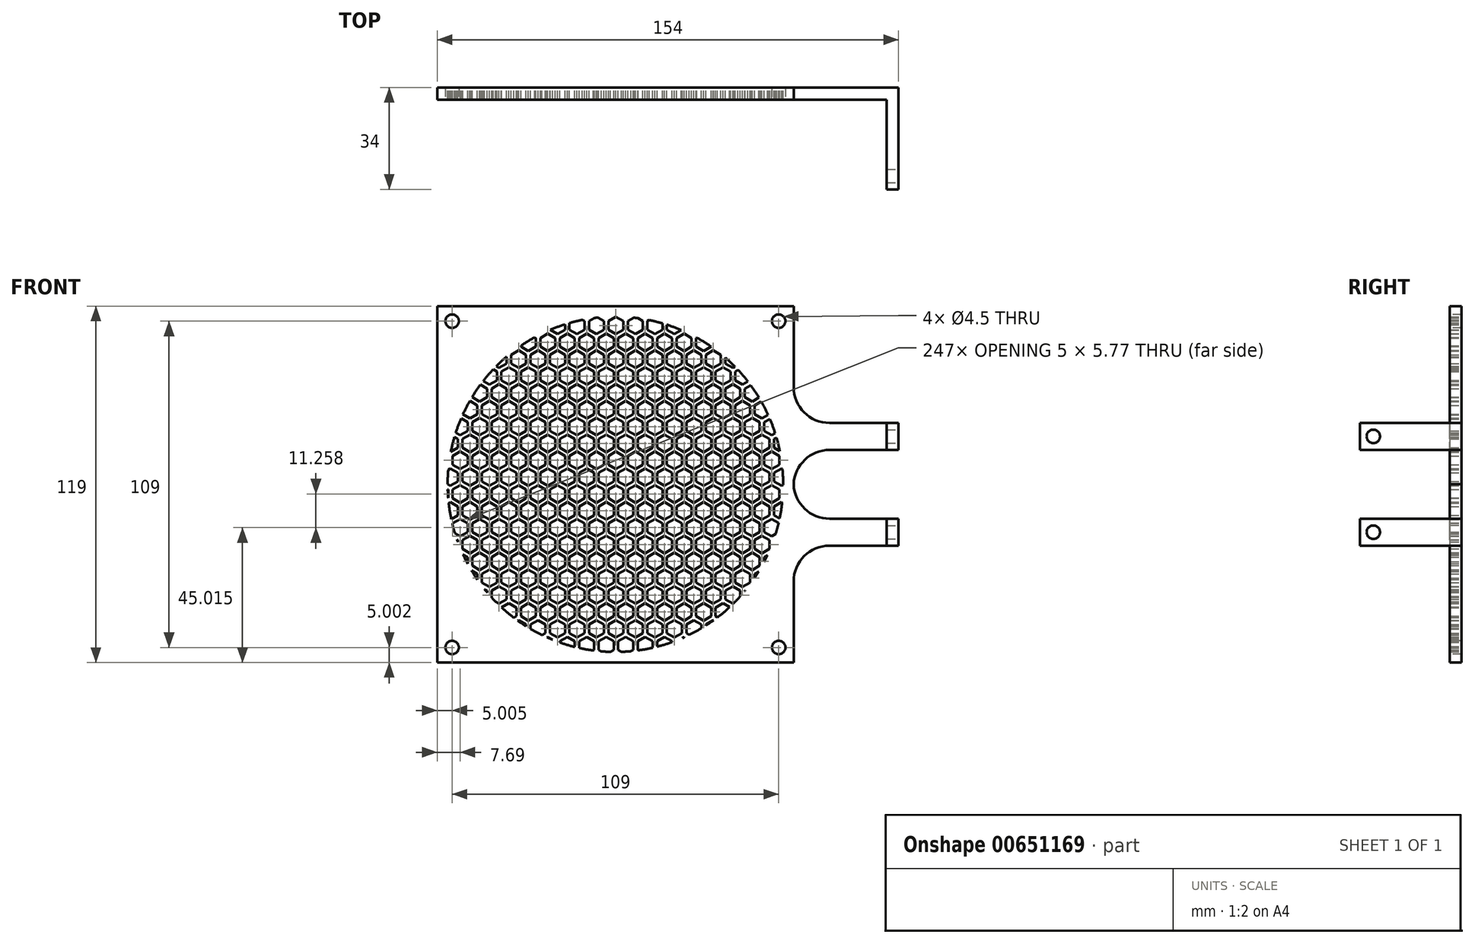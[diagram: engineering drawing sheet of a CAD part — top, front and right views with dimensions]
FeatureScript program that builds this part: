
annotation { "Feature Type Name" : "Feature", "Feature Type Description" : "" }
export const myFeature = defineFeature(function(context is Context, id is Id, definition is map)
    precondition{}
    {
        {
            var Q0;
            Q0=qCreatedBy(makeId("Front.planeOp"),FACE);
            var sketch = newSketch(context, id + "F0", { "sketchPlane" : qUnion([Q0])});
            skCircle(sketch, "E0.cCircle", {"center": v(0, 0) * mm, "radius": 2.5 * mm, "construction": true});
            skLineSegment(sketch, "E0.0", {"start": v(0, 2.89) * mm, "end": v(2.5, 1.44) * mm});
            skLineSegment(sketch, "E0.1", {"start": v(2.5, 1.44) * mm, "end": v(2.5, -1.44) * mm});
            skLineSegment(sketch, "E0.2", {"start": v(2.5, -1.44) * mm, "end": v(0, -2.89) * mm});
            skLineSegment(sketch, "E0.3", {"start": v(0, -2.89) * mm, "end": v(-2.5, -1.44) * mm});
            skLineSegment(sketch, "E0.4", {"start": v(-2.5, -1.44) * mm, "end": v(-2.5, 1.44) * mm});
            skLineSegment(sketch, "E0.5", {"start": v(-2.5, 1.44) * mm, "end": v(0, 2.89) * mm});
            skPoint(sketch, "E0.0.midPoint", {"position": v(1.25, 2.17) * mm});
            skLineSegment(sketch, "E1", {"start": v(0, 0) * mm, "end": v(18.77, -32.51) * mm, "construction": true});
            skCircle(sketch, "E2.cCircle", {"center": v(3.25, -5.63) * mm, "radius": 2.5 * mm, "construction": true});
            skLineSegment(sketch, "E2.0", {"start": v(3.25, -2.74) * mm, "end": v(5.75, -4.19) * mm});
            skLineSegment(sketch, "E2.1", {"start": v(5.75, -4.19) * mm, "end": v(5.75, -7.07) * mm});
            skLineSegment(sketch, "E2.2", {"start": v(5.75, -7.07) * mm, "end": v(3.25, -8.52) * mm});
            skLineSegment(sketch, "E2.3", {"start": v(3.25, -8.52) * mm, "end": v(0.75, -7.07) * mm});
            skLineSegment(sketch, "E2.4", {"start": v(0.75, -7.07) * mm, "end": v(0.75, -4.19) * mm});
            skLineSegment(sketch, "E2.5", {"start": v(0.75, -4.19) * mm, "end": v(3.25, -2.74) * mm});
            skPoint(sketch, "E2.0.midPoint", {"position": v(4.5, -3.46) * mm});
            skCircle(sketch, "E3.0.1.0", {"center": v(3.25, 5.63) * mm, "radius": 2.5 * mm, "construction": true});
            skCircle(sketch, "E3.0.1.1", {"center": v(0, 11.26) * mm, "radius": 2.5 * mm, "construction": true});
            skPoint(sketch, "E3.0.1.2", {"position": v(1.25, 13.42) * mm});
            skPoint(sketch, "E3.0.1.3", {"position": v(4.5, 7.8) * mm});
            skLineSegment(sketch, "E3.0.1.4", {"start": v(3.25, 2.74) * mm, "end": v(0.75, 4.19) * mm});
            skLineSegment(sketch, "E3.0.1.5", {"start": v(5.75, 4.19) * mm, "end": v(3.25, 2.74) * mm});
            skLineSegment(sketch, "E3.0.1.6", {"start": v(5.75, 7.07) * mm, "end": v(5.75, 4.19) * mm});
            skLineSegment(sketch, "E3.0.1.7", {"start": v(3.25, 8.52) * mm, "end": v(5.75, 7.07) * mm});
            skLineSegment(sketch, "E3.0.1.8", {"start": v(-2.5, 12.7) * mm, "end": v(0, 14.15) * mm});
            skLineSegment(sketch, "E3.0.1.9", {"start": v(-2.5, 9.81) * mm, "end": v(-2.5, 12.7) * mm});
            skLineSegment(sketch, "E3.0.1.10", {"start": v(0, 8.37) * mm, "end": v(-2.5, 9.81) * mm});
            skLineSegment(sketch, "E3.0.1.11", {"start": v(2.5, 9.81) * mm, "end": v(0, 8.37) * mm});
            skLineSegment(sketch, "E3.0.1.12", {"start": v(2.5, 12.7) * mm, "end": v(2.5, 9.81) * mm});
            skLineSegment(sketch, "E3.0.1.13", {"start": v(0, 14.15) * mm, "end": v(2.5, 12.7) * mm});
            skLineSegment(sketch, "E3.0.1.14", {"start": v(0.75, 7.07) * mm, "end": v(3.25, 8.52) * mm});
            skLineSegment(sketch, "E3.0.1.15", {"start": v(0.75, 4.19) * mm, "end": v(0.75, 7.07) * mm});
            skCircle(sketch, "E3.0.2.0", {"center": v(3.25, 16.89) * mm, "radius": 2.5 * mm, "construction": true});
            skCircle(sketch, "E3.0.2.1", {"center": v(0, 22.52) * mm, "radius": 2.5 * mm, "construction": true});
            skPoint(sketch, "E3.0.2.2", {"position": v(1.25, 24.68) * mm});
            skPoint(sketch, "E3.0.2.3", {"position": v(4.5, 19.05) * mm});
            skLineSegment(sketch, "E3.0.2.4", {"start": v(3.25, 14) * mm, "end": v(0.75, 15.44) * mm});
            skLineSegment(sketch, "E3.0.2.5", {"start": v(5.75, 15.44) * mm, "end": v(3.25, 14) * mm});
            skLineSegment(sketch, "E3.0.2.6", {"start": v(5.75, 18.33) * mm, "end": v(5.75, 15.44) * mm});
            skLineSegment(sketch, "E3.0.2.7", {"start": v(3.25, 19.77) * mm, "end": v(5.75, 18.33) * mm});
            skLineSegment(sketch, "E3.0.2.8", {"start": v(-2.5, 23.96) * mm, "end": v(0, 25.4) * mm});
            skLineSegment(sketch, "E3.0.2.9", {"start": v(-2.5, 21.07) * mm, "end": v(-2.5, 23.96) * mm});
            skLineSegment(sketch, "E3.0.2.10", {"start": v(0, 19.63) * mm, "end": v(-2.5, 21.07) * mm});
            skLineSegment(sketch, "E3.0.2.11", {"start": v(2.5, 21.07) * mm, "end": v(0, 19.63) * mm});
            skLineSegment(sketch, "E3.0.2.12", {"start": v(2.5, 23.96) * mm, "end": v(2.5, 21.07) * mm});
            skLineSegment(sketch, "E3.0.2.13", {"start": v(0, 25.4) * mm, "end": v(2.5, 23.96) * mm});
            skLineSegment(sketch, "E3.0.2.14", {"start": v(0.75, 18.33) * mm, "end": v(3.25, 19.77) * mm});
            skLineSegment(sketch, "E3.0.2.15", {"start": v(0.75, 15.44) * mm, "end": v(0.75, 18.33) * mm});
            skCircle(sketch, "E3.0.3.0", {"center": v(3.25, 28.15) * mm, "radius": 2.5 * mm, "construction": true});
            skCircle(sketch, "E3.0.3.1", {"center": v(0, 33.77) * mm, "radius": 2.5 * mm, "construction": true});
            skPoint(sketch, "E3.0.3.2", {"position": v(1.25, 35.94) * mm});
            skPoint(sketch, "E3.0.3.3", {"position": v(4.5, 30.31) * mm});
            skLineSegment(sketch, "E3.0.3.4", {"start": v(3.25, 25.26) * mm, "end": v(0.75, 26.7) * mm});
            skLineSegment(sketch, "E3.0.3.5", {"start": v(5.75, 26.7) * mm, "end": v(3.25, 25.26) * mm});
            skLineSegment(sketch, "E3.0.3.6", {"start": v(5.75, 29.59) * mm, "end": v(5.75, 26.7) * mm});
            skLineSegment(sketch, "E3.0.3.7", {"start": v(3.25, 31.03) * mm, "end": v(5.75, 29.59) * mm});
            skLineSegment(sketch, "E3.0.3.8", {"start": v(-2.5, 35.22) * mm, "end": v(0, 36.66) * mm});
            skLineSegment(sketch, "E3.0.3.9", {"start": v(-2.5, 32.33) * mm, "end": v(-2.5, 35.22) * mm});
            skLineSegment(sketch, "E3.0.3.10", {"start": v(0, 30.89) * mm, "end": v(-2.5, 32.33) * mm});
            skLineSegment(sketch, "E3.0.3.11", {"start": v(2.5, 32.33) * mm, "end": v(0, 30.89) * mm});
            skLineSegment(sketch, "E3.0.3.12", {"start": v(2.5, 35.22) * mm, "end": v(2.5, 32.33) * mm});
            skLineSegment(sketch, "E3.0.3.13", {"start": v(0, 36.66) * mm, "end": v(2.5, 35.22) * mm});
            skLineSegment(sketch, "E3.0.3.14", {"start": v(0.75, 29.59) * mm, "end": v(3.25, 31.03) * mm});
            skLineSegment(sketch, "E3.0.3.15", {"start": v(0.75, 26.7) * mm, "end": v(0.75, 29.59) * mm});
            skCircle(sketch, "E3.0.4.0", {"center": v(3.25, 39.4) * mm, "radius": 2.5 * mm, "construction": true});
            skCircle(sketch, "E3.0.4.1", {"center": v(0, 45.03) * mm, "radius": 2.5 * mm, "construction": true});
            skPoint(sketch, "E3.0.4.2", {"position": v(1.25, 47.2) * mm});
            skPoint(sketch, "E3.0.4.3", {"position": v(4.5, 41.57) * mm});
            skLineSegment(sketch, "E3.0.4.4", {"start": v(3.25, 36.52) * mm, "end": v(0.75, 37.96) * mm});
            skLineSegment(sketch, "E3.0.4.5", {"start": v(5.75, 37.96) * mm, "end": v(3.25, 36.52) * mm});
            skLineSegment(sketch, "E3.0.4.6", {"start": v(5.75, 40.85) * mm, "end": v(5.75, 37.96) * mm});
            skLineSegment(sketch, "E3.0.4.7", {"start": v(3.25, 42.3) * mm, "end": v(5.75, 40.85) * mm});
            skLineSegment(sketch, "E3.0.4.8", {"start": v(-2.5, 46.48) * mm, "end": v(0, 47.92) * mm});
            skLineSegment(sketch, "E3.0.4.9", {"start": v(-2.5, 43.59) * mm, "end": v(-2.5, 46.48) * mm});
            skLineSegment(sketch, "E3.0.4.10", {"start": v(0, 42.15) * mm, "end": v(-2.5, 43.59) * mm});
            skLineSegment(sketch, "E3.0.4.11", {"start": v(2.5, 43.59) * mm, "end": v(0, 42.15) * mm});
            skLineSegment(sketch, "E3.0.4.12", {"start": v(2.5, 46.48) * mm, "end": v(2.5, 43.59) * mm});
            skLineSegment(sketch, "E3.0.4.13", {"start": v(0, 47.92) * mm, "end": v(2.5, 46.48) * mm});
            skLineSegment(sketch, "E3.0.4.14", {"start": v(0.75, 40.85) * mm, "end": v(3.25, 42.3) * mm});
            skLineSegment(sketch, "E3.0.4.15", {"start": v(0.75, 37.96) * mm, "end": v(0.75, 40.85) * mm});
            skCircle(sketch, "E3.0.5.0", {"center": v(3.25, 50.66) * mm, "radius": 2.5 * mm, "construction": true});
            skCircle(sketch, "E3.0.5.1", {"center": v(0, 56.3) * mm, "radius": 2.5 * mm, "construction": true});
            skPoint(sketch, "E3.0.5.2", {"position": v(1.25, 58.46) * mm});
            skPoint(sketch, "E3.0.5.3", {"position": v(4.5, 52.83) * mm});
            skLineSegment(sketch, "E3.0.5.4", {"start": v(3.25, 47.78) * mm, "end": v(0.75, 49.22) * mm});
            skLineSegment(sketch, "E3.0.5.5", {"start": v(5.75, 49.22) * mm, "end": v(3.25, 47.78) * mm});
            skLineSegment(sketch, "E3.0.5.6", {"start": v(5.75, 52.1) * mm, "end": v(5.75, 49.22) * mm});
            skLineSegment(sketch, "E3.0.5.7", {"start": v(3.25, 53.55) * mm, "end": v(5.75, 52.1) * mm});
            skLineSegment(sketch, "E3.0.5.8", {"start": v(-2.5, 57.74) * mm, "end": v(0, 59.18) * mm});
            skLineSegment(sketch, "E3.0.5.9", {"start": v(-2.5, 54.85) * mm, "end": v(-2.5, 57.74) * mm});
            skLineSegment(sketch, "E3.0.5.10", {"start": v(0, 53.4) * mm, "end": v(-2.5, 54.85) * mm});
            skLineSegment(sketch, "E3.0.5.11", {"start": v(2.5, 54.85) * mm, "end": v(0, 53.4) * mm});
            skLineSegment(sketch, "E3.0.5.12", {"start": v(2.5, 57.74) * mm, "end": v(2.5, 54.85) * mm});
            skLineSegment(sketch, "E3.0.5.13", {"start": v(0, 59.18) * mm, "end": v(2.5, 57.74) * mm});
            skLineSegment(sketch, "E3.0.5.14", {"start": v(0.75, 52.1) * mm, "end": v(3.25, 53.55) * mm});
            skLineSegment(sketch, "E3.0.5.15", {"start": v(0.75, 49.22) * mm, "end": v(0.75, 52.1) * mm});
            skCircle(sketch, "E3.0.6.0", {"center": v(3.25, 61.92) * mm, "radius": 2.5 * mm, "construction": true});
            skCircle(sketch, "E3.0.6.1", {"center": v(0, 67.55) * mm, "radius": 2.5 * mm, "construction": true});
            skPoint(sketch, "E3.0.6.2", {"position": v(1.25, 69.72) * mm});
            skPoint(sketch, "E3.0.6.3", {"position": v(4.5, 64.09) * mm});
            skLineSegment(sketch, "E3.0.6.4", {"start": v(3.25, 59.03) * mm, "end": v(0.75, 60.48) * mm});
            skLineSegment(sketch, "E3.0.6.5", {"start": v(5.75, 60.48) * mm, "end": v(3.25, 59.03) * mm});
            skLineSegment(sketch, "E3.0.6.6", {"start": v(5.75, 63.36) * mm, "end": v(5.75, 60.48) * mm});
            skLineSegment(sketch, "E3.0.6.7", {"start": v(3.25, 64.8) * mm, "end": v(5.75, 63.36) * mm});
            skLineSegment(sketch, "E3.0.6.8", {"start": v(-2.5, 69) * mm, "end": v(0, 70.44) * mm});
            skLineSegment(sketch, "E3.0.6.9", {"start": v(-2.5, 66.1) * mm, "end": v(-2.5, 69) * mm});
            skLineSegment(sketch, "E3.0.6.10", {"start": v(0, 64.66) * mm, "end": v(-2.5, 66.1) * mm});
            skLineSegment(sketch, "E3.0.6.11", {"start": v(2.5, 66.1) * mm, "end": v(0, 64.66) * mm});
            skLineSegment(sketch, "E3.0.6.12", {"start": v(2.5, 69) * mm, "end": v(2.5, 66.1) * mm});
            skLineSegment(sketch, "E3.0.6.13", {"start": v(0, 70.44) * mm, "end": v(2.5, 69) * mm});
            skLineSegment(sketch, "E3.0.6.14", {"start": v(0.75, 63.36) * mm, "end": v(3.25, 64.8) * mm});
            skLineSegment(sketch, "E3.0.6.15", {"start": v(0.75, 60.48) * mm, "end": v(0.75, 63.36) * mm});
            skCircle(sketch, "E3.0.7.0", {"center": v(3.25, 73.18) * mm, "radius": 2.5 * mm, "construction": true});
            skCircle(sketch, "E3.0.7.1", {"center": v(0, 78.8) * mm, "radius": 2.5 * mm, "construction": true});
            skPoint(sketch, "E3.0.7.2", {"position": v(1.25, 80.97) * mm});
            skPoint(sketch, "E3.0.7.3", {"position": v(4.5, 75.34) * mm});
            skLineSegment(sketch, "E3.0.7.4", {"start": v(3.25, 70.3) * mm, "end": v(0.75, 71.74) * mm});
            skLineSegment(sketch, "E3.0.7.5", {"start": v(5.75, 71.74) * mm, "end": v(3.25, 70.3) * mm});
            skLineSegment(sketch, "E3.0.7.6", {"start": v(5.75, 74.62) * mm, "end": v(5.75, 71.74) * mm});
            skLineSegment(sketch, "E3.0.7.7", {"start": v(3.25, 76.07) * mm, "end": v(5.75, 74.62) * mm});
            skLineSegment(sketch, "E3.0.7.8", {"start": v(-2.5, 80.25) * mm, "end": v(0, 81.7) * mm});
            skLineSegment(sketch, "E3.0.7.9", {"start": v(-2.5, 77.36) * mm, "end": v(-2.5, 80.25) * mm});
            skLineSegment(sketch, "E3.0.7.10", {"start": v(0, 75.92) * mm, "end": v(-2.5, 77.36) * mm});
            skLineSegment(sketch, "E3.0.7.11", {"start": v(2.5, 77.36) * mm, "end": v(0, 75.92) * mm});
            skLineSegment(sketch, "E3.0.7.12", {"start": v(2.5, 80.25) * mm, "end": v(2.5, 77.36) * mm});
            skLineSegment(sketch, "E3.0.7.13", {"start": v(0, 81.7) * mm, "end": v(2.5, 80.25) * mm});
            skLineSegment(sketch, "E3.0.7.14", {"start": v(0.75, 74.62) * mm, "end": v(3.25, 76.07) * mm});
            skLineSegment(sketch, "E3.0.7.15", {"start": v(0.75, 71.74) * mm, "end": v(0.75, 74.62) * mm});
            skCircle(sketch, "E3.0.8.0", {"center": v(3.25, 84.44) * mm, "radius": 2.5 * mm, "construction": true});
            skCircle(sketch, "E3.0.8.1", {"center": v(0, 90.07) * mm, "radius": 2.5 * mm, "construction": true});
            skPoint(sketch, "E3.0.8.2", {"position": v(1.25, 92.23) * mm});
            skPoint(sketch, "E3.0.8.3", {"position": v(4.5, 86.6) * mm});
            skLineSegment(sketch, "E3.0.8.4", {"start": v(3.25, 81.55) * mm, "end": v(0.75, 83) * mm});
            skLineSegment(sketch, "E3.0.8.5", {"start": v(5.75, 83) * mm, "end": v(3.25, 81.55) * mm});
            skLineSegment(sketch, "E3.0.8.6", {"start": v(5.75, 85.88) * mm, "end": v(5.75, 83) * mm});
            skLineSegment(sketch, "E3.0.8.7", {"start": v(3.25, 87.32) * mm, "end": v(5.75, 85.88) * mm});
            skLineSegment(sketch, "E3.0.8.8", {"start": v(-2.5, 91.51) * mm, "end": v(0, 92.95) * mm});
            skLineSegment(sketch, "E3.0.8.9", {"start": v(-2.5, 88.62) * mm, "end": v(-2.5, 91.51) * mm});
            skLineSegment(sketch, "E3.0.8.10", {"start": v(0, 87.18) * mm, "end": v(-2.5, 88.62) * mm});
            skLineSegment(sketch, "E3.0.8.11", {"start": v(2.5, 88.62) * mm, "end": v(0, 87.18) * mm});
            skLineSegment(sketch, "E3.0.8.12", {"start": v(2.5, 91.51) * mm, "end": v(2.5, 88.62) * mm});
            skLineSegment(sketch, "E3.0.8.13", {"start": v(0, 92.95) * mm, "end": v(2.5, 91.51) * mm});
            skLineSegment(sketch, "E3.0.8.14", {"start": v(0.75, 85.88) * mm, "end": v(3.25, 87.32) * mm});
            skLineSegment(sketch, "E3.0.8.15", {"start": v(0.75, 83) * mm, "end": v(0.75, 85.88) * mm});
            skCircle(sketch, "E3.0.9.0", {"center": v(3.25, 95.7) * mm, "radius": 2.5 * mm, "construction": true});
            skCircle(sketch, "E3.0.9.1", {"center": v(0, 101.32) * mm, "radius": 2.5 * mm, "construction": true});
            skPoint(sketch, "E3.0.9.2", {"position": v(1.25, 103.5) * mm});
            skPoint(sketch, "E3.0.9.3", {"position": v(4.5, 97.86) * mm});
            skLineSegment(sketch, "E3.0.9.4", {"start": v(3.25, 92.8) * mm, "end": v(0.75, 94.25) * mm});
            skLineSegment(sketch, "E3.0.9.5", {"start": v(5.75, 94.25) * mm, "end": v(3.25, 92.8) * mm});
            skLineSegment(sketch, "E3.0.9.6", {"start": v(5.75, 97.14) * mm, "end": v(5.75, 94.25) * mm});
            skLineSegment(sketch, "E3.0.9.7", {"start": v(3.25, 98.58) * mm, "end": v(5.75, 97.14) * mm});
            skLineSegment(sketch, "E3.0.9.8", {"start": v(-2.5, 102.77) * mm, "end": v(0, 104.21) * mm});
            skLineSegment(sketch, "E3.0.9.9", {"start": v(-2.5, 99.88) * mm, "end": v(-2.5, 102.77) * mm});
            skLineSegment(sketch, "E3.0.9.10", {"start": v(0, 98.44) * mm, "end": v(-2.5, 99.88) * mm});
            skLineSegment(sketch, "E3.0.9.11", {"start": v(2.5, 99.88) * mm, "end": v(0, 98.44) * mm});
            skLineSegment(sketch, "E3.0.9.12", {"start": v(2.5, 102.77) * mm, "end": v(2.5, 99.88) * mm});
            skLineSegment(sketch, "E3.0.9.13", {"start": v(0, 104.21) * mm, "end": v(2.5, 102.77) * mm});
            skLineSegment(sketch, "E3.0.9.14", {"start": v(0.75, 97.14) * mm, "end": v(3.25, 98.58) * mm});
            skLineSegment(sketch, "E3.0.9.15", {"start": v(0.75, 94.25) * mm, "end": v(0.75, 97.14) * mm});
            skCircle(sketch, "E3.1.0.0", {"center": v(9.75, -5.63) * mm, "radius": 2.5 * mm, "construction": true});
            skCircle(sketch, "E3.1.0.1", {"center": v(6.5, 0) * mm, "radius": 2.5 * mm, "construction": true});
            skPoint(sketch, "E3.1.0.2", {"position": v(7.75, 2.17) * mm});
            skPoint(sketch, "E3.1.0.3", {"position": v(11, -3.46) * mm});
            skLineSegment(sketch, "E3.1.0.4", {"start": v(9.75, -8.52) * mm, "end": v(7.25, -7.07) * mm});
            skLineSegment(sketch, "E3.1.0.5", {"start": v(12.25, -7.07) * mm, "end": v(9.75, -8.52) * mm});
            skLineSegment(sketch, "E3.1.0.6", {"start": v(12.25, -4.19) * mm, "end": v(12.25, -7.07) * mm});
            skLineSegment(sketch, "E3.1.0.7", {"start": v(9.75, -2.74) * mm, "end": v(12.25, -4.19) * mm});
            skLineSegment(sketch, "E3.1.0.8", {"start": v(4, 1.44) * mm, "end": v(6.5, 2.89) * mm});
            skLineSegment(sketch, "E3.1.0.9", {"start": v(4, -1.44) * mm, "end": v(4, 1.44) * mm});
            skLineSegment(sketch, "E3.1.0.10", {"start": v(6.5, -2.89) * mm, "end": v(4, -1.44) * mm});
            skLineSegment(sketch, "E3.1.0.11", {"start": v(9, -1.44) * mm, "end": v(6.5, -2.89) * mm});
            skLineSegment(sketch, "E3.1.0.12", {"start": v(9, 1.44) * mm, "end": v(9, -1.44) * mm});
            skLineSegment(sketch, "E3.1.0.13", {"start": v(6.5, 2.89) * mm, "end": v(9, 1.44) * mm});
            skLineSegment(sketch, "E3.1.0.14", {"start": v(7.25, -4.19) * mm, "end": v(9.75, -2.74) * mm});
            skLineSegment(sketch, "E3.1.0.15", {"start": v(7.25, -7.07) * mm, "end": v(7.25, -4.19) * mm});
            skCircle(sketch, "E3.1.1.0", {"center": v(9.75, 5.63) * mm, "radius": 2.5 * mm, "construction": true});
            skCircle(sketch, "E3.1.1.1", {"center": v(6.5, 11.26) * mm, "radius": 2.5 * mm, "construction": true});
            skPoint(sketch, "E3.1.1.2", {"position": v(7.75, 13.42) * mm});
            skPoint(sketch, "E3.1.1.3", {"position": v(11, 7.8) * mm});
            skLineSegment(sketch, "E3.1.1.4", {"start": v(9.75, 2.74) * mm, "end": v(7.25, 4.19) * mm});
            skLineSegment(sketch, "E3.1.1.5", {"start": v(12.25, 4.19) * mm, "end": v(9.75, 2.74) * mm});
            skLineSegment(sketch, "E3.1.1.6", {"start": v(12.25, 7.07) * mm, "end": v(12.25, 4.19) * mm});
            skLineSegment(sketch, "E3.1.1.7", {"start": v(9.75, 8.52) * mm, "end": v(12.25, 7.07) * mm});
            skLineSegment(sketch, "E3.1.1.8", {"start": v(4, 12.7) * mm, "end": v(6.5, 14.15) * mm});
            skLineSegment(sketch, "E3.1.1.9", {"start": v(4, 9.81) * mm, "end": v(4, 12.7) * mm});
            skLineSegment(sketch, "E3.1.1.10", {"start": v(6.5, 8.37) * mm, "end": v(4, 9.81) * mm});
            skLineSegment(sketch, "E3.1.1.11", {"start": v(9, 9.81) * mm, "end": v(6.5, 8.37) * mm});
            skLineSegment(sketch, "E3.1.1.12", {"start": v(9, 12.7) * mm, "end": v(9, 9.81) * mm});
            skLineSegment(sketch, "E3.1.1.13", {"start": v(6.5, 14.15) * mm, "end": v(9, 12.7) * mm});
            skLineSegment(sketch, "E3.1.1.14", {"start": v(7.25, 7.07) * mm, "end": v(9.75, 8.52) * mm});
            skLineSegment(sketch, "E3.1.1.15", {"start": v(7.25, 4.19) * mm, "end": v(7.25, 7.07) * mm});
            skCircle(sketch, "E3.1.2.0", {"center": v(9.75, 16.89) * mm, "radius": 2.5 * mm, "construction": true});
            skCircle(sketch, "E3.1.2.1", {"center": v(6.5, 22.52) * mm, "radius": 2.5 * mm, "construction": true});
            skPoint(sketch, "E3.1.2.2", {"position": v(7.75, 24.68) * mm});
            skPoint(sketch, "E3.1.2.3", {"position": v(11, 19.05) * mm});
            skLineSegment(sketch, "E3.1.2.4", {"start": v(9.75, 14) * mm, "end": v(7.25, 15.44) * mm});
            skLineSegment(sketch, "E3.1.2.5", {"start": v(12.25, 15.44) * mm, "end": v(9.75, 14) * mm});
            skLineSegment(sketch, "E3.1.2.6", {"start": v(12.25, 18.33) * mm, "end": v(12.25, 15.44) * mm});
            skLineSegment(sketch, "E3.1.2.7", {"start": v(9.75, 19.77) * mm, "end": v(12.25, 18.33) * mm});
            skLineSegment(sketch, "E3.1.2.8", {"start": v(4, 23.96) * mm, "end": v(6.5, 25.4) * mm});
            skLineSegment(sketch, "E3.1.2.9", {"start": v(4, 21.07) * mm, "end": v(4, 23.96) * mm});
            skLineSegment(sketch, "E3.1.2.10", {"start": v(6.5, 19.63) * mm, "end": v(4, 21.07) * mm});
            skLineSegment(sketch, "E3.1.2.11", {"start": v(9, 21.07) * mm, "end": v(6.5, 19.63) * mm});
            skLineSegment(sketch, "E3.1.2.12", {"start": v(9, 23.96) * mm, "end": v(9, 21.07) * mm});
            skLineSegment(sketch, "E3.1.2.13", {"start": v(6.5, 25.4) * mm, "end": v(9, 23.96) * mm});
            skLineSegment(sketch, "E3.1.2.14", {"start": v(7.25, 18.33) * mm, "end": v(9.75, 19.77) * mm});
            skLineSegment(sketch, "E3.1.2.15", {"start": v(7.25, 15.44) * mm, "end": v(7.25, 18.33) * mm});
            skCircle(sketch, "E3.1.3.0", {"center": v(9.75, 28.15) * mm, "radius": 2.5 * mm, "construction": true});
            skCircle(sketch, "E3.1.3.1", {"center": v(6.5, 33.77) * mm, "radius": 2.5 * mm, "construction": true});
            skPoint(sketch, "E3.1.3.2", {"position": v(7.75, 35.94) * mm});
            skPoint(sketch, "E3.1.3.3", {"position": v(11, 30.31) * mm});
            skLineSegment(sketch, "E3.1.3.4", {"start": v(9.75, 25.26) * mm, "end": v(7.25, 26.7) * mm});
            skLineSegment(sketch, "E3.1.3.5", {"start": v(12.25, 26.7) * mm, "end": v(9.75, 25.26) * mm});
            skLineSegment(sketch, "E3.1.3.6", {"start": v(12.25, 29.59) * mm, "end": v(12.25, 26.7) * mm});
            skLineSegment(sketch, "E3.1.3.7", {"start": v(9.75, 31.03) * mm, "end": v(12.25, 29.59) * mm});
            skLineSegment(sketch, "E3.1.3.8", {"start": v(4, 35.22) * mm, "end": v(6.5, 36.66) * mm});
            skLineSegment(sketch, "E3.1.3.9", {"start": v(4, 32.33) * mm, "end": v(4, 35.22) * mm});
            skLineSegment(sketch, "E3.1.3.10", {"start": v(6.5, 30.89) * mm, "end": v(4, 32.33) * mm});
            skLineSegment(sketch, "E3.1.3.11", {"start": v(9, 32.33) * mm, "end": v(6.5, 30.89) * mm});
            skLineSegment(sketch, "E3.1.3.12", {"start": v(9, 35.22) * mm, "end": v(9, 32.33) * mm});
            skLineSegment(sketch, "E3.1.3.13", {"start": v(6.5, 36.66) * mm, "end": v(9, 35.22) * mm});
            skLineSegment(sketch, "E3.1.3.14", {"start": v(7.25, 29.59) * mm, "end": v(9.75, 31.03) * mm});
            skLineSegment(sketch, "E3.1.3.15", {"start": v(7.25, 26.7) * mm, "end": v(7.25, 29.59) * mm});
            skCircle(sketch, "E3.1.4.0", {"center": v(9.75, 39.4) * mm, "radius": 2.5 * mm, "construction": true});
            skCircle(sketch, "E3.1.4.1", {"center": v(6.5, 45.03) * mm, "radius": 2.5 * mm, "construction": true});
            skPoint(sketch, "E3.1.4.2", {"position": v(7.75, 47.2) * mm});
            skPoint(sketch, "E3.1.4.3", {"position": v(11, 41.57) * mm});
            skLineSegment(sketch, "E3.1.4.4", {"start": v(9.75, 36.52) * mm, "end": v(7.25, 37.96) * mm});
            skLineSegment(sketch, "E3.1.4.5", {"start": v(12.25, 37.96) * mm, "end": v(9.75, 36.52) * mm});
            skLineSegment(sketch, "E3.1.4.6", {"start": v(12.25, 40.85) * mm, "end": v(12.25, 37.96) * mm});
            skLineSegment(sketch, "E3.1.4.7", {"start": v(9.75, 42.3) * mm, "end": v(12.25, 40.85) * mm});
            skLineSegment(sketch, "E3.1.4.8", {"start": v(4, 46.48) * mm, "end": v(6.5, 47.92) * mm});
            skLineSegment(sketch, "E3.1.4.9", {"start": v(4, 43.59) * mm, "end": v(4, 46.48) * mm});
            skLineSegment(sketch, "E3.1.4.10", {"start": v(6.5, 42.15) * mm, "end": v(4, 43.59) * mm});
            skLineSegment(sketch, "E3.1.4.11", {"start": v(9, 43.59) * mm, "end": v(6.5, 42.15) * mm});
            skLineSegment(sketch, "E3.1.4.12", {"start": v(9, 46.48) * mm, "end": v(9, 43.59) * mm});
            skLineSegment(sketch, "E3.1.4.13", {"start": v(6.5, 47.92) * mm, "end": v(9, 46.48) * mm});
            skLineSegment(sketch, "E3.1.4.14", {"start": v(7.25, 40.85) * mm, "end": v(9.75, 42.3) * mm});
            skLineSegment(sketch, "E3.1.4.15", {"start": v(7.25, 37.96) * mm, "end": v(7.25, 40.85) * mm});
            skCircle(sketch, "E3.1.5.0", {"center": v(9.75, 50.66) * mm, "radius": 2.5 * mm, "construction": true});
            skCircle(sketch, "E3.1.5.1", {"center": v(6.5, 56.3) * mm, "radius": 2.5 * mm, "construction": true});
            skPoint(sketch, "E3.1.5.2", {"position": v(7.75, 58.46) * mm});
            skPoint(sketch, "E3.1.5.3", {"position": v(11, 52.83) * mm});
            skLineSegment(sketch, "E3.1.5.4", {"start": v(9.75, 47.78) * mm, "end": v(7.25, 49.22) * mm});
            skLineSegment(sketch, "E3.1.5.5", {"start": v(12.25, 49.22) * mm, "end": v(9.75, 47.78) * mm});
            skLineSegment(sketch, "E3.1.5.6", {"start": v(12.25, 52.1) * mm, "end": v(12.25, 49.22) * mm});
            skLineSegment(sketch, "E3.1.5.7", {"start": v(9.75, 53.55) * mm, "end": v(12.25, 52.1) * mm});
            skLineSegment(sketch, "E3.1.5.8", {"start": v(4, 57.74) * mm, "end": v(6.5, 59.18) * mm});
            skLineSegment(sketch, "E3.1.5.9", {"start": v(4, 54.85) * mm, "end": v(4, 57.74) * mm});
            skLineSegment(sketch, "E3.1.5.10", {"start": v(6.5, 53.4) * mm, "end": v(4, 54.85) * mm});
            skLineSegment(sketch, "E3.1.5.11", {"start": v(9, 54.85) * mm, "end": v(6.5, 53.4) * mm});
            skLineSegment(sketch, "E3.1.5.12", {"start": v(9, 57.74) * mm, "end": v(9, 54.85) * mm});
            skLineSegment(sketch, "E3.1.5.13", {"start": v(6.5, 59.18) * mm, "end": v(9, 57.74) * mm});
            skLineSegment(sketch, "E3.1.5.14", {"start": v(7.25, 52.1) * mm, "end": v(9.75, 53.55) * mm});
            skLineSegment(sketch, "E3.1.5.15", {"start": v(7.25, 49.22) * mm, "end": v(7.25, 52.1) * mm});
            skCircle(sketch, "E3.1.6.0", {"center": v(9.75, 61.92) * mm, "radius": 2.5 * mm, "construction": true});
            skCircle(sketch, "E3.1.6.1", {"center": v(6.5, 67.55) * mm, "radius": 2.5 * mm, "construction": true});
            skPoint(sketch, "E3.1.6.2", {"position": v(7.75, 69.72) * mm});
            skPoint(sketch, "E3.1.6.3", {"position": v(11, 64.09) * mm});
            skLineSegment(sketch, "E3.1.6.4", {"start": v(9.75, 59.03) * mm, "end": v(7.25, 60.48) * mm});
            skLineSegment(sketch, "E3.1.6.5", {"start": v(12.25, 60.48) * mm, "end": v(9.75, 59.03) * mm});
            skLineSegment(sketch, "E3.1.6.6", {"start": v(12.25, 63.36) * mm, "end": v(12.25, 60.48) * mm});
            skLineSegment(sketch, "E3.1.6.7", {"start": v(9.75, 64.8) * mm, "end": v(12.25, 63.36) * mm});
            skLineSegment(sketch, "E3.1.6.8", {"start": v(4, 69) * mm, "end": v(6.5, 70.44) * mm});
            skLineSegment(sketch, "E3.1.6.9", {"start": v(4, 66.1) * mm, "end": v(4, 69) * mm});
            skLineSegment(sketch, "E3.1.6.10", {"start": v(6.5, 64.66) * mm, "end": v(4, 66.1) * mm});
            skLineSegment(sketch, "E3.1.6.11", {"start": v(9, 66.1) * mm, "end": v(6.5, 64.66) * mm});
            skLineSegment(sketch, "E3.1.6.12", {"start": v(9, 69) * mm, "end": v(9, 66.1) * mm});
            skLineSegment(sketch, "E3.1.6.13", {"start": v(6.5, 70.44) * mm, "end": v(9, 69) * mm});
            skLineSegment(sketch, "E3.1.6.14", {"start": v(7.25, 63.36) * mm, "end": v(9.75, 64.8) * mm});
            skLineSegment(sketch, "E3.1.6.15", {"start": v(7.25, 60.48) * mm, "end": v(7.25, 63.36) * mm});
            skCircle(sketch, "E3.1.7.0", {"center": v(9.75, 73.18) * mm, "radius": 2.5 * mm, "construction": true});
            skCircle(sketch, "E3.1.7.1", {"center": v(6.5, 78.8) * mm, "radius": 2.5 * mm, "construction": true});
            skPoint(sketch, "E3.1.7.2", {"position": v(7.75, 80.97) * mm});
            skPoint(sketch, "E3.1.7.3", {"position": v(11, 75.34) * mm});
            skLineSegment(sketch, "E3.1.7.4", {"start": v(9.75, 70.3) * mm, "end": v(7.25, 71.74) * mm});
            skLineSegment(sketch, "E3.1.7.5", {"start": v(12.25, 71.74) * mm, "end": v(9.75, 70.3) * mm});
            skLineSegment(sketch, "E3.1.7.6", {"start": v(12.25, 74.62) * mm, "end": v(12.25, 71.74) * mm});
            skLineSegment(sketch, "E3.1.7.7", {"start": v(9.75, 76.07) * mm, "end": v(12.25, 74.62) * mm});
            skLineSegment(sketch, "E3.1.7.8", {"start": v(4, 80.25) * mm, "end": v(6.5, 81.7) * mm});
            skLineSegment(sketch, "E3.1.7.9", {"start": v(4, 77.36) * mm, "end": v(4, 80.25) * mm});
            skLineSegment(sketch, "E3.1.7.10", {"start": v(6.5, 75.92) * mm, "end": v(4, 77.36) * mm});
            skLineSegment(sketch, "E3.1.7.11", {"start": v(9, 77.36) * mm, "end": v(6.5, 75.92) * mm});
            skLineSegment(sketch, "E3.1.7.12", {"start": v(9, 80.25) * mm, "end": v(9, 77.36) * mm});
            skLineSegment(sketch, "E3.1.7.13", {"start": v(6.5, 81.7) * mm, "end": v(9, 80.25) * mm});
            skLineSegment(sketch, "E3.1.7.14", {"start": v(7.25, 74.62) * mm, "end": v(9.75, 76.07) * mm});
            skLineSegment(sketch, "E3.1.7.15", {"start": v(7.25, 71.74) * mm, "end": v(7.25, 74.62) * mm});
            skCircle(sketch, "E3.1.8.0", {"center": v(9.75, 84.44) * mm, "radius": 2.5 * mm, "construction": true});
            skCircle(sketch, "E3.1.8.1", {"center": v(6.5, 90.07) * mm, "radius": 2.5 * mm, "construction": true});
            skPoint(sketch, "E3.1.8.2", {"position": v(7.75, 92.23) * mm});
            skPoint(sketch, "E3.1.8.3", {"position": v(11, 86.6) * mm});
            skLineSegment(sketch, "E3.1.8.4", {"start": v(9.75, 81.55) * mm, "end": v(7.25, 83) * mm});
            skLineSegment(sketch, "E3.1.8.5", {"start": v(12.25, 83) * mm, "end": v(9.75, 81.55) * mm});
            skLineSegment(sketch, "E3.1.8.6", {"start": v(12.25, 85.88) * mm, "end": v(12.25, 83) * mm});
            skLineSegment(sketch, "E3.1.8.7", {"start": v(9.75, 87.32) * mm, "end": v(12.25, 85.88) * mm});
            skLineSegment(sketch, "E3.1.8.8", {"start": v(4, 91.51) * mm, "end": v(6.5, 92.95) * mm});
            skLineSegment(sketch, "E3.1.8.9", {"start": v(4, 88.62) * mm, "end": v(4, 91.51) * mm});
            skLineSegment(sketch, "E3.1.8.10", {"start": v(6.5, 87.18) * mm, "end": v(4, 88.62) * mm});
            skLineSegment(sketch, "E3.1.8.11", {"start": v(9, 88.62) * mm, "end": v(6.5, 87.18) * mm});
            skLineSegment(sketch, "E3.1.8.12", {"start": v(9, 91.51) * mm, "end": v(9, 88.62) * mm});
            skLineSegment(sketch, "E3.1.8.13", {"start": v(6.5, 92.95) * mm, "end": v(9, 91.51) * mm});
            skLineSegment(sketch, "E3.1.8.14", {"start": v(7.25, 85.88) * mm, "end": v(9.75, 87.32) * mm});
            skLineSegment(sketch, "E3.1.8.15", {"start": v(7.25, 83) * mm, "end": v(7.25, 85.88) * mm});
            skCircle(sketch, "E3.1.9.0", {"center": v(9.75, 95.7) * mm, "radius": 2.5 * mm, "construction": true});
            skCircle(sketch, "E3.1.9.1", {"center": v(6.5, 101.32) * mm, "radius": 2.5 * mm, "construction": true});
            skPoint(sketch, "E3.1.9.2", {"position": v(7.75, 103.5) * mm});
            skPoint(sketch, "E3.1.9.3", {"position": v(11, 97.86) * mm});
            skLineSegment(sketch, "E3.1.9.4", {"start": v(9.75, 92.8) * mm, "end": v(7.25, 94.25) * mm});
            skLineSegment(sketch, "E3.1.9.5", {"start": v(12.25, 94.25) * mm, "end": v(9.75, 92.8) * mm});
            skLineSegment(sketch, "E3.1.9.6", {"start": v(12.25, 97.14) * mm, "end": v(12.25, 94.25) * mm});
            skLineSegment(sketch, "E3.1.9.7", {"start": v(9.75, 98.58) * mm, "end": v(12.25, 97.14) * mm});
            skLineSegment(sketch, "E3.1.9.8", {"start": v(4, 102.77) * mm, "end": v(6.5, 104.21) * mm});
            skLineSegment(sketch, "E3.1.9.9", {"start": v(4, 99.88) * mm, "end": v(4, 102.77) * mm});
            skLineSegment(sketch, "E3.1.9.10", {"start": v(6.5, 98.44) * mm, "end": v(4, 99.88) * mm});
            skLineSegment(sketch, "E3.1.9.11", {"start": v(9, 99.88) * mm, "end": v(6.5, 98.44) * mm});
            skLineSegment(sketch, "E3.1.9.12", {"start": v(9, 102.77) * mm, "end": v(9, 99.88) * mm});
            skLineSegment(sketch, "E3.1.9.13", {"start": v(6.5, 104.21) * mm, "end": v(9, 102.77) * mm});
            skLineSegment(sketch, "E3.1.9.14", {"start": v(7.25, 97.14) * mm, "end": v(9.75, 98.58) * mm});
            skLineSegment(sketch, "E3.1.9.15", {"start": v(7.25, 94.25) * mm, "end": v(7.25, 97.14) * mm});
            skCircle(sketch, "E3.2.0.0", {"center": v(16.25, -5.63) * mm, "radius": 2.5 * mm, "construction": true});
            skCircle(sketch, "E3.2.0.1", {"center": v(13, 0) * mm, "radius": 2.5 * mm, "construction": true});
            skPoint(sketch, "E3.2.0.2", {"position": v(14.25, 2.17) * mm});
            skPoint(sketch, "E3.2.0.3", {"position": v(17.5, -3.46) * mm});
            skLineSegment(sketch, "E3.2.0.4", {"start": v(16.25, -8.52) * mm, "end": v(13.75, -7.07) * mm});
            skLineSegment(sketch, "E3.2.0.5", {"start": v(18.75, -7.07) * mm, "end": v(16.25, -8.52) * mm});
            skLineSegment(sketch, "E3.2.0.6", {"start": v(18.75, -4.19) * mm, "end": v(18.75, -7.07) * mm});
            skLineSegment(sketch, "E3.2.0.7", {"start": v(16.25, -2.74) * mm, "end": v(18.75, -4.19) * mm});
            skLineSegment(sketch, "E3.2.0.8", {"start": v(10.5, 1.44) * mm, "end": v(13, 2.89) * mm});
            skLineSegment(sketch, "E3.2.0.9", {"start": v(10.5, -1.44) * mm, "end": v(10.5, 1.44) * mm});
            skLineSegment(sketch, "E3.2.0.10", {"start": v(13, -2.89) * mm, "end": v(10.5, -1.44) * mm});
            skLineSegment(sketch, "E3.2.0.11", {"start": v(15.5, -1.44) * mm, "end": v(13, -2.89) * mm});
            skLineSegment(sketch, "E3.2.0.12", {"start": v(15.5, 1.44) * mm, "end": v(15.5, -1.44) * mm});
            skLineSegment(sketch, "E3.2.0.13", {"start": v(13, 2.89) * mm, "end": v(15.5, 1.44) * mm});
            skLineSegment(sketch, "E3.2.0.14", {"start": v(13.75, -4.19) * mm, "end": v(16.25, -2.74) * mm});
            skLineSegment(sketch, "E3.2.0.15", {"start": v(13.75, -7.07) * mm, "end": v(13.75, -4.19) * mm});
            skCircle(sketch, "E3.2.1.0", {"center": v(16.25, 5.63) * mm, "radius": 2.5 * mm, "construction": true});
            skCircle(sketch, "E3.2.1.1", {"center": v(13, 11.26) * mm, "radius": 2.5 * mm, "construction": true});
            skPoint(sketch, "E3.2.1.2", {"position": v(14.25, 13.42) * mm});
            skPoint(sketch, "E3.2.1.3", {"position": v(17.5, 7.8) * mm});
            skLineSegment(sketch, "E3.2.1.4", {"start": v(16.25, 2.74) * mm, "end": v(13.75, 4.19) * mm});
            skLineSegment(sketch, "E3.2.1.5", {"start": v(18.75, 4.19) * mm, "end": v(16.25, 2.74) * mm});
            skLineSegment(sketch, "E3.2.1.6", {"start": v(18.75, 7.07) * mm, "end": v(18.75, 4.19) * mm});
            skLineSegment(sketch, "E3.2.1.7", {"start": v(16.25, 8.52) * mm, "end": v(18.75, 7.07) * mm});
            skLineSegment(sketch, "E3.2.1.8", {"start": v(10.5, 12.7) * mm, "end": v(13, 14.15) * mm});
            skLineSegment(sketch, "E3.2.1.9", {"start": v(10.5, 9.81) * mm, "end": v(10.5, 12.7) * mm});
            skLineSegment(sketch, "E3.2.1.10", {"start": v(13, 8.37) * mm, "end": v(10.5, 9.81) * mm});
            skLineSegment(sketch, "E3.2.1.11", {"start": v(15.5, 9.81) * mm, "end": v(13, 8.37) * mm});
            skLineSegment(sketch, "E3.2.1.12", {"start": v(15.5, 12.7) * mm, "end": v(15.5, 9.81) * mm});
            skLineSegment(sketch, "E3.2.1.13", {"start": v(13, 14.15) * mm, "end": v(15.5, 12.7) * mm});
            skLineSegment(sketch, "E3.2.1.14", {"start": v(13.75, 7.07) * mm, "end": v(16.25, 8.52) * mm});
            skLineSegment(sketch, "E3.2.1.15", {"start": v(13.75, 4.19) * mm, "end": v(13.75, 7.07) * mm});
            skCircle(sketch, "E3.2.2.0", {"center": v(16.25, 16.89) * mm, "radius": 2.5 * mm, "construction": true});
            skCircle(sketch, "E3.2.2.1", {"center": v(13, 22.52) * mm, "radius": 2.5 * mm, "construction": true});
            skPoint(sketch, "E3.2.2.2", {"position": v(14.25, 24.68) * mm});
            skPoint(sketch, "E3.2.2.3", {"position": v(17.5, 19.05) * mm});
            skLineSegment(sketch, "E3.2.2.4", {"start": v(16.25, 14) * mm, "end": v(13.75, 15.44) * mm});
            skLineSegment(sketch, "E3.2.2.5", {"start": v(18.75, 15.44) * mm, "end": v(16.25, 14) * mm});
            skLineSegment(sketch, "E3.2.2.6", {"start": v(18.75, 18.33) * mm, "end": v(18.75, 15.44) * mm});
            skLineSegment(sketch, "E3.2.2.7", {"start": v(16.25, 19.77) * mm, "end": v(18.75, 18.33) * mm});
            skLineSegment(sketch, "E3.2.2.8", {"start": v(10.5, 23.96) * mm, "end": v(13, 25.4) * mm});
            skLineSegment(sketch, "E3.2.2.9", {"start": v(10.5, 21.07) * mm, "end": v(10.5, 23.96) * mm});
            skLineSegment(sketch, "E3.2.2.10", {"start": v(13, 19.63) * mm, "end": v(10.5, 21.07) * mm});
            skLineSegment(sketch, "E3.2.2.11", {"start": v(15.5, 21.07) * mm, "end": v(13, 19.63) * mm});
            skLineSegment(sketch, "E3.2.2.12", {"start": v(15.5, 23.96) * mm, "end": v(15.5, 21.07) * mm});
            skLineSegment(sketch, "E3.2.2.13", {"start": v(13, 25.4) * mm, "end": v(15.5, 23.96) * mm});
            skLineSegment(sketch, "E3.2.2.14", {"start": v(13.75, 18.33) * mm, "end": v(16.25, 19.77) * mm});
            skLineSegment(sketch, "E3.2.2.15", {"start": v(13.75, 15.44) * mm, "end": v(13.75, 18.33) * mm});
            skCircle(sketch, "E3.2.3.0", {"center": v(16.25, 28.15) * mm, "radius": 2.5 * mm, "construction": true});
            skCircle(sketch, "E3.2.3.1", {"center": v(13, 33.77) * mm, "radius": 2.5 * mm, "construction": true});
            skPoint(sketch, "E3.2.3.2", {"position": v(14.25, 35.94) * mm});
            skPoint(sketch, "E3.2.3.3", {"position": v(17.5, 30.31) * mm});
            skLineSegment(sketch, "E3.2.3.4", {"start": v(16.25, 25.26) * mm, "end": v(13.75, 26.7) * mm});
            skLineSegment(sketch, "E3.2.3.5", {"start": v(18.75, 26.7) * mm, "end": v(16.25, 25.26) * mm});
            skLineSegment(sketch, "E3.2.3.6", {"start": v(18.75, 29.59) * mm, "end": v(18.75, 26.7) * mm});
            skLineSegment(sketch, "E3.2.3.7", {"start": v(16.25, 31.03) * mm, "end": v(18.75, 29.59) * mm});
            skLineSegment(sketch, "E3.2.3.8", {"start": v(10.5, 35.22) * mm, "end": v(13, 36.66) * mm});
            skLineSegment(sketch, "E3.2.3.9", {"start": v(10.5, 32.33) * mm, "end": v(10.5, 35.22) * mm});
            skLineSegment(sketch, "E3.2.3.10", {"start": v(13, 30.89) * mm, "end": v(10.5, 32.33) * mm});
            skLineSegment(sketch, "E3.2.3.11", {"start": v(15.5, 32.33) * mm, "end": v(13, 30.89) * mm});
            skLineSegment(sketch, "E3.2.3.12", {"start": v(15.5, 35.22) * mm, "end": v(15.5, 32.33) * mm});
            skLineSegment(sketch, "E3.2.3.13", {"start": v(13, 36.66) * mm, "end": v(15.5, 35.22) * mm});
            skLineSegment(sketch, "E3.2.3.14", {"start": v(13.75, 29.59) * mm, "end": v(16.25, 31.03) * mm});
            skLineSegment(sketch, "E3.2.3.15", {"start": v(13.75, 26.7) * mm, "end": v(13.75, 29.59) * mm});
            skCircle(sketch, "E3.2.4.0", {"center": v(16.25, 39.4) * mm, "radius": 2.5 * mm, "construction": true});
            skCircle(sketch, "E3.2.4.1", {"center": v(13, 45.03) * mm, "radius": 2.5 * mm, "construction": true});
            skPoint(sketch, "E3.2.4.2", {"position": v(14.25, 47.2) * mm});
            skPoint(sketch, "E3.2.4.3", {"position": v(17.5, 41.57) * mm});
            skLineSegment(sketch, "E3.2.4.4", {"start": v(16.25, 36.52) * mm, "end": v(13.75, 37.96) * mm});
            skLineSegment(sketch, "E3.2.4.5", {"start": v(18.75, 37.96) * mm, "end": v(16.25, 36.52) * mm});
            skLineSegment(sketch, "E3.2.4.6", {"start": v(18.75, 40.85) * mm, "end": v(18.75, 37.96) * mm});
            skLineSegment(sketch, "E3.2.4.7", {"start": v(16.25, 42.3) * mm, "end": v(18.75, 40.85) * mm});
            skLineSegment(sketch, "E3.2.4.8", {"start": v(10.5, 46.48) * mm, "end": v(13, 47.92) * mm});
            skLineSegment(sketch, "E3.2.4.9", {"start": v(10.5, 43.59) * mm, "end": v(10.5, 46.48) * mm});
            skLineSegment(sketch, "E3.2.4.10", {"start": v(13, 42.15) * mm, "end": v(10.5, 43.59) * mm});
            skLineSegment(sketch, "E3.2.4.11", {"start": v(15.5, 43.59) * mm, "end": v(13, 42.15) * mm});
            skLineSegment(sketch, "E3.2.4.12", {"start": v(15.5, 46.48) * mm, "end": v(15.5, 43.59) * mm});
            skLineSegment(sketch, "E3.2.4.13", {"start": v(13, 47.92) * mm, "end": v(15.5, 46.48) * mm});
            skLineSegment(sketch, "E3.2.4.14", {"start": v(13.75, 40.85) * mm, "end": v(16.25, 42.3) * mm});
            skLineSegment(sketch, "E3.2.4.15", {"start": v(13.75, 37.96) * mm, "end": v(13.75, 40.85) * mm});
            skCircle(sketch, "E3.2.5.0", {"center": v(16.25, 50.66) * mm, "radius": 2.5 * mm, "construction": true});
            skCircle(sketch, "E3.2.5.1", {"center": v(13, 56.3) * mm, "radius": 2.5 * mm, "construction": true});
            skPoint(sketch, "E3.2.5.2", {"position": v(14.25, 58.46) * mm});
            skPoint(sketch, "E3.2.5.3", {"position": v(17.5, 52.83) * mm});
            skLineSegment(sketch, "E3.2.5.4", {"start": v(16.25, 47.78) * mm, "end": v(13.75, 49.22) * mm});
            skLineSegment(sketch, "E3.2.5.5", {"start": v(18.75, 49.22) * mm, "end": v(16.25, 47.78) * mm});
            skLineSegment(sketch, "E3.2.5.6", {"start": v(18.75, 52.1) * mm, "end": v(18.75, 49.22) * mm});
            skLineSegment(sketch, "E3.2.5.7", {"start": v(16.25, 53.55) * mm, "end": v(18.75, 52.1) * mm});
            skLineSegment(sketch, "E3.2.5.8", {"start": v(10.5, 57.74) * mm, "end": v(13, 59.18) * mm});
            skLineSegment(sketch, "E3.2.5.9", {"start": v(10.5, 54.85) * mm, "end": v(10.5, 57.74) * mm});
            skLineSegment(sketch, "E3.2.5.10", {"start": v(13, 53.4) * mm, "end": v(10.5, 54.85) * mm});
            skLineSegment(sketch, "E3.2.5.11", {"start": v(15.5, 54.85) * mm, "end": v(13, 53.4) * mm});
            skLineSegment(sketch, "E3.2.5.12", {"start": v(15.5, 57.74) * mm, "end": v(15.5, 54.85) * mm});
            skLineSegment(sketch, "E3.2.5.13", {"start": v(13, 59.18) * mm, "end": v(15.5, 57.74) * mm});
            skLineSegment(sketch, "E3.2.5.14", {"start": v(13.75, 52.1) * mm, "end": v(16.25, 53.55) * mm});
            skLineSegment(sketch, "E3.2.5.15", {"start": v(13.75, 49.22) * mm, "end": v(13.75, 52.1) * mm});
            skCircle(sketch, "E3.2.6.0", {"center": v(16.25, 61.92) * mm, "radius": 2.5 * mm, "construction": true});
            skCircle(sketch, "E3.2.6.1", {"center": v(13, 67.55) * mm, "radius": 2.5 * mm, "construction": true});
            skPoint(sketch, "E3.2.6.2", {"position": v(14.25, 69.72) * mm});
            skPoint(sketch, "E3.2.6.3", {"position": v(17.5, 64.09) * mm});
            skLineSegment(sketch, "E3.2.6.4", {"start": v(16.25, 59.03) * mm, "end": v(13.75, 60.48) * mm});
            skLineSegment(sketch, "E3.2.6.5", {"start": v(18.75, 60.48) * mm, "end": v(16.25, 59.03) * mm});
            skLineSegment(sketch, "E3.2.6.6", {"start": v(18.75, 63.36) * mm, "end": v(18.75, 60.48) * mm});
            skLineSegment(sketch, "E3.2.6.7", {"start": v(16.25, 64.8) * mm, "end": v(18.75, 63.36) * mm});
            skLineSegment(sketch, "E3.2.6.8", {"start": v(10.5, 69) * mm, "end": v(13, 70.44) * mm});
            skLineSegment(sketch, "E3.2.6.9", {"start": v(10.5, 66.1) * mm, "end": v(10.5, 69) * mm});
            skLineSegment(sketch, "E3.2.6.10", {"start": v(13, 64.66) * mm, "end": v(10.5, 66.1) * mm});
            skLineSegment(sketch, "E3.2.6.11", {"start": v(15.5, 66.1) * mm, "end": v(13, 64.66) * mm});
            skLineSegment(sketch, "E3.2.6.12", {"start": v(15.5, 69) * mm, "end": v(15.5, 66.1) * mm});
            skLineSegment(sketch, "E3.2.6.13", {"start": v(13, 70.44) * mm, "end": v(15.5, 69) * mm});
            skLineSegment(sketch, "E3.2.6.14", {"start": v(13.75, 63.36) * mm, "end": v(16.25, 64.8) * mm});
            skLineSegment(sketch, "E3.2.6.15", {"start": v(13.75, 60.48) * mm, "end": v(13.75, 63.36) * mm});
            skCircle(sketch, "E3.2.7.0", {"center": v(16.25, 73.18) * mm, "radius": 2.5 * mm, "construction": true});
            skCircle(sketch, "E3.2.7.1", {"center": v(13, 78.8) * mm, "radius": 2.5 * mm, "construction": true});
            skPoint(sketch, "E3.2.7.2", {"position": v(14.25, 80.97) * mm});
            skPoint(sketch, "E3.2.7.3", {"position": v(17.5, 75.34) * mm});
            skLineSegment(sketch, "E3.2.7.4", {"start": v(16.25, 70.3) * mm, "end": v(13.75, 71.74) * mm});
            skLineSegment(sketch, "E3.2.7.5", {"start": v(18.75, 71.74) * mm, "end": v(16.25, 70.3) * mm});
            skLineSegment(sketch, "E3.2.7.6", {"start": v(18.75, 74.62) * mm, "end": v(18.75, 71.74) * mm});
            skLineSegment(sketch, "E3.2.7.7", {"start": v(16.25, 76.07) * mm, "end": v(18.75, 74.62) * mm});
            skLineSegment(sketch, "E3.2.7.8", {"start": v(10.5, 80.25) * mm, "end": v(13, 81.7) * mm});
            skLineSegment(sketch, "E3.2.7.9", {"start": v(10.5, 77.36) * mm, "end": v(10.5, 80.25) * mm});
            skLineSegment(sketch, "E3.2.7.10", {"start": v(13, 75.92) * mm, "end": v(10.5, 77.36) * mm});
            skLineSegment(sketch, "E3.2.7.11", {"start": v(15.5, 77.36) * mm, "end": v(13, 75.92) * mm});
            skLineSegment(sketch, "E3.2.7.12", {"start": v(15.5, 80.25) * mm, "end": v(15.5, 77.36) * mm});
            skLineSegment(sketch, "E3.2.7.13", {"start": v(13, 81.7) * mm, "end": v(15.5, 80.25) * mm});
            skLineSegment(sketch, "E3.2.7.14", {"start": v(13.75, 74.62) * mm, "end": v(16.25, 76.07) * mm});
            skLineSegment(sketch, "E3.2.7.15", {"start": v(13.75, 71.74) * mm, "end": v(13.75, 74.62) * mm});
            skCircle(sketch, "E3.2.8.0", {"center": v(16.25, 84.44) * mm, "radius": 2.5 * mm, "construction": true});
            skCircle(sketch, "E3.2.8.1", {"center": v(13, 90.07) * mm, "radius": 2.5 * mm, "construction": true});
            skPoint(sketch, "E3.2.8.2", {"position": v(14.25, 92.23) * mm});
            skPoint(sketch, "E3.2.8.3", {"position": v(17.5, 86.6) * mm});
            skLineSegment(sketch, "E3.2.8.4", {"start": v(16.25, 81.55) * mm, "end": v(13.75, 83) * mm});
            skLineSegment(sketch, "E3.2.8.5", {"start": v(18.75, 83) * mm, "end": v(16.25, 81.55) * mm});
            skLineSegment(sketch, "E3.2.8.6", {"start": v(18.75, 85.88) * mm, "end": v(18.75, 83) * mm});
            skLineSegment(sketch, "E3.2.8.7", {"start": v(16.25, 87.32) * mm, "end": v(18.75, 85.88) * mm});
            skLineSegment(sketch, "E3.2.8.8", {"start": v(10.5, 91.51) * mm, "end": v(13, 92.95) * mm});
            skLineSegment(sketch, "E3.2.8.9", {"start": v(10.5, 88.62) * mm, "end": v(10.5, 91.51) * mm});
            skLineSegment(sketch, "E3.2.8.10", {"start": v(13, 87.18) * mm, "end": v(10.5, 88.62) * mm});
            skLineSegment(sketch, "E3.2.8.11", {"start": v(15.5, 88.62) * mm, "end": v(13, 87.18) * mm});
            skLineSegment(sketch, "E3.2.8.12", {"start": v(15.5, 91.51) * mm, "end": v(15.5, 88.62) * mm});
            skLineSegment(sketch, "E3.2.8.13", {"start": v(13, 92.95) * mm, "end": v(15.5, 91.51) * mm});
            skLineSegment(sketch, "E3.2.8.14", {"start": v(13.75, 85.88) * mm, "end": v(16.25, 87.32) * mm});
            skLineSegment(sketch, "E3.2.8.15", {"start": v(13.75, 83) * mm, "end": v(13.75, 85.88) * mm});
            skCircle(sketch, "E3.2.9.0", {"center": v(16.25, 95.7) * mm, "radius": 2.5 * mm, "construction": true});
            skCircle(sketch, "E3.2.9.1", {"center": v(13, 101.32) * mm, "radius": 2.5 * mm, "construction": true});
            skPoint(sketch, "E3.2.9.2", {"position": v(14.25, 103.5) * mm});
            skPoint(sketch, "E3.2.9.3", {"position": v(17.5, 97.86) * mm});
            skLineSegment(sketch, "E3.2.9.4", {"start": v(16.25, 92.8) * mm, "end": v(13.75, 94.25) * mm});
            skLineSegment(sketch, "E3.2.9.5", {"start": v(18.75, 94.25) * mm, "end": v(16.25, 92.8) * mm});
            skLineSegment(sketch, "E3.2.9.6", {"start": v(18.75, 97.14) * mm, "end": v(18.75, 94.25) * mm});
            skLineSegment(sketch, "E3.2.9.7", {"start": v(16.25, 98.58) * mm, "end": v(18.75, 97.14) * mm});
            skLineSegment(sketch, "E3.2.9.8", {"start": v(10.5, 102.77) * mm, "end": v(13, 104.21) * mm});
            skLineSegment(sketch, "E3.2.9.9", {"start": v(10.5, 99.88) * mm, "end": v(10.5, 102.77) * mm});
            skLineSegment(sketch, "E3.2.9.10", {"start": v(13, 98.44) * mm, "end": v(10.5, 99.88) * mm});
            skLineSegment(sketch, "E3.2.9.11", {"start": v(15.5, 99.88) * mm, "end": v(13, 98.44) * mm});
            skLineSegment(sketch, "E3.2.9.12", {"start": v(15.5, 102.77) * mm, "end": v(15.5, 99.88) * mm});
            skLineSegment(sketch, "E3.2.9.13", {"start": v(13, 104.21) * mm, "end": v(15.5, 102.77) * mm});
            skLineSegment(sketch, "E3.2.9.14", {"start": v(13.75, 97.14) * mm, "end": v(16.25, 98.58) * mm});
            skLineSegment(sketch, "E3.2.9.15", {"start": v(13.75, 94.25) * mm, "end": v(13.75, 97.14) * mm});
            skCircle(sketch, "E3.3.0.0", {"center": v(22.75, -5.63) * mm, "radius": 2.5 * mm, "construction": true});
            skCircle(sketch, "E3.3.0.1", {"center": v(19.5, 0) * mm, "radius": 2.5 * mm, "construction": true});
            skPoint(sketch, "E3.3.0.2", {"position": v(20.75, 2.17) * mm});
            skPoint(sketch, "E3.3.0.3", {"position": v(24, -3.46) * mm});
            skLineSegment(sketch, "E3.3.0.4", {"start": v(22.75, -8.52) * mm, "end": v(20.25, -7.07) * mm});
            skLineSegment(sketch, "E3.3.0.5", {"start": v(25.25, -7.07) * mm, "end": v(22.75, -8.52) * mm});
            skLineSegment(sketch, "E3.3.0.6", {"start": v(25.25, -4.19) * mm, "end": v(25.25, -7.07) * mm});
            skLineSegment(sketch, "E3.3.0.7", {"start": v(22.75, -2.74) * mm, "end": v(25.25, -4.19) * mm});
            skLineSegment(sketch, "E3.3.0.8", {"start": v(17, 1.44) * mm, "end": v(19.5, 2.89) * mm});
            skLineSegment(sketch, "E3.3.0.9", {"start": v(17, -1.44) * mm, "end": v(17, 1.44) * mm});
            skLineSegment(sketch, "E3.3.0.10", {"start": v(19.5, -2.89) * mm, "end": v(17, -1.44) * mm});
            skLineSegment(sketch, "E3.3.0.11", {"start": v(22, -1.44) * mm, "end": v(19.5, -2.89) * mm});
            skLineSegment(sketch, "E3.3.0.12", {"start": v(22, 1.44) * mm, "end": v(22, -1.44) * mm});
            skLineSegment(sketch, "E3.3.0.13", {"start": v(19.5, 2.89) * mm, "end": v(22, 1.44) * mm});
            skLineSegment(sketch, "E3.3.0.14", {"start": v(20.25, -4.19) * mm, "end": v(22.75, -2.74) * mm});
            skLineSegment(sketch, "E3.3.0.15", {"start": v(20.25, -7.07) * mm, "end": v(20.25, -4.19) * mm});
            skCircle(sketch, "E3.3.1.0", {"center": v(22.75, 5.63) * mm, "radius": 2.5 * mm, "construction": true});
            skCircle(sketch, "E3.3.1.1", {"center": v(19.5, 11.26) * mm, "radius": 2.5 * mm, "construction": true});
            skPoint(sketch, "E3.3.1.2", {"position": v(20.75, 13.42) * mm});
            skPoint(sketch, "E3.3.1.3", {"position": v(24, 7.8) * mm});
            skLineSegment(sketch, "E3.3.1.4", {"start": v(22.75, 2.74) * mm, "end": v(20.25, 4.19) * mm});
            skLineSegment(sketch, "E3.3.1.5", {"start": v(25.25, 4.19) * mm, "end": v(22.75, 2.74) * mm});
            skLineSegment(sketch, "E3.3.1.6", {"start": v(25.25, 7.07) * mm, "end": v(25.25, 4.19) * mm});
            skLineSegment(sketch, "E3.3.1.7", {"start": v(22.75, 8.52) * mm, "end": v(25.25, 7.07) * mm});
            skLineSegment(sketch, "E3.3.1.8", {"start": v(17, 12.7) * mm, "end": v(19.5, 14.15) * mm});
            skLineSegment(sketch, "E3.3.1.9", {"start": v(17, 9.81) * mm, "end": v(17, 12.7) * mm});
            skLineSegment(sketch, "E3.3.1.10", {"start": v(19.5, 8.37) * mm, "end": v(17, 9.81) * mm});
            skLineSegment(sketch, "E3.3.1.11", {"start": v(22, 9.81) * mm, "end": v(19.5, 8.37) * mm});
            skLineSegment(sketch, "E3.3.1.12", {"start": v(22, 12.7) * mm, "end": v(22, 9.81) * mm});
            skLineSegment(sketch, "E3.3.1.13", {"start": v(19.5, 14.15) * mm, "end": v(22, 12.7) * mm});
            skLineSegment(sketch, "E3.3.1.14", {"start": v(20.25, 7.07) * mm, "end": v(22.75, 8.52) * mm});
            skLineSegment(sketch, "E3.3.1.15", {"start": v(20.25, 4.19) * mm, "end": v(20.25, 7.07) * mm});
            skCircle(sketch, "E3.3.2.0", {"center": v(22.75, 16.89) * mm, "radius": 2.5 * mm, "construction": true});
            skCircle(sketch, "E3.3.2.1", {"center": v(19.5, 22.52) * mm, "radius": 2.5 * mm, "construction": true});
            skPoint(sketch, "E3.3.2.2", {"position": v(20.75, 24.68) * mm});
            skPoint(sketch, "E3.3.2.3", {"position": v(24, 19.05) * mm});
            skLineSegment(sketch, "E3.3.2.4", {"start": v(22.75, 14) * mm, "end": v(20.25, 15.44) * mm});
            skLineSegment(sketch, "E3.3.2.5", {"start": v(25.25, 15.44) * mm, "end": v(22.75, 14) * mm});
            skLineSegment(sketch, "E3.3.2.6", {"start": v(25.25, 18.33) * mm, "end": v(25.25, 15.44) * mm});
            skLineSegment(sketch, "E3.3.2.7", {"start": v(22.75, 19.77) * mm, "end": v(25.25, 18.33) * mm});
            skLineSegment(sketch, "E3.3.2.8", {"start": v(17, 23.96) * mm, "end": v(19.5, 25.4) * mm});
            skLineSegment(sketch, "E3.3.2.9", {"start": v(17, 21.07) * mm, "end": v(17, 23.96) * mm});
            skLineSegment(sketch, "E3.3.2.10", {"start": v(19.5, 19.63) * mm, "end": v(17, 21.07) * mm});
            skLineSegment(sketch, "E3.3.2.11", {"start": v(22, 21.07) * mm, "end": v(19.5, 19.63) * mm});
            skLineSegment(sketch, "E3.3.2.12", {"start": v(22, 23.96) * mm, "end": v(22, 21.07) * mm});
            skLineSegment(sketch, "E3.3.2.13", {"start": v(19.5, 25.4) * mm, "end": v(22, 23.96) * mm});
            skLineSegment(sketch, "E3.3.2.14", {"start": v(20.25, 18.33) * mm, "end": v(22.75, 19.77) * mm});
            skLineSegment(sketch, "E3.3.2.15", {"start": v(20.25, 15.44) * mm, "end": v(20.25, 18.33) * mm});
            skCircle(sketch, "E3.3.3.0", {"center": v(22.75, 28.15) * mm, "radius": 2.5 * mm, "construction": true});
            skCircle(sketch, "E3.3.3.1", {"center": v(19.5, 33.77) * mm, "radius": 2.5 * mm, "construction": true});
            skPoint(sketch, "E3.3.3.2", {"position": v(20.75, 35.94) * mm});
            skPoint(sketch, "E3.3.3.3", {"position": v(24, 30.31) * mm});
            skLineSegment(sketch, "E3.3.3.4", {"start": v(22.75, 25.26) * mm, "end": v(20.25, 26.7) * mm});
            skLineSegment(sketch, "E3.3.3.5", {"start": v(25.25, 26.7) * mm, "end": v(22.75, 25.26) * mm});
            skLineSegment(sketch, "E3.3.3.6", {"start": v(25.25, 29.59) * mm, "end": v(25.25, 26.7) * mm});
            skLineSegment(sketch, "E3.3.3.7", {"start": v(22.75, 31.03) * mm, "end": v(25.25, 29.59) * mm});
            skLineSegment(sketch, "E3.3.3.8", {"start": v(17, 35.22) * mm, "end": v(19.5, 36.66) * mm});
            skLineSegment(sketch, "E3.3.3.9", {"start": v(17, 32.33) * mm, "end": v(17, 35.22) * mm});
            skLineSegment(sketch, "E3.3.3.10", {"start": v(19.5, 30.89) * mm, "end": v(17, 32.33) * mm});
            skLineSegment(sketch, "E3.3.3.11", {"start": v(22, 32.33) * mm, "end": v(19.5, 30.89) * mm});
            skLineSegment(sketch, "E3.3.3.12", {"start": v(22, 35.22) * mm, "end": v(22, 32.33) * mm});
            skLineSegment(sketch, "E3.3.3.13", {"start": v(19.5, 36.66) * mm, "end": v(22, 35.22) * mm});
            skLineSegment(sketch, "E3.3.3.14", {"start": v(20.25, 29.59) * mm, "end": v(22.75, 31.03) * mm});
            skLineSegment(sketch, "E3.3.3.15", {"start": v(20.25, 26.7) * mm, "end": v(20.25, 29.59) * mm});
            skCircle(sketch, "E3.3.4.0", {"center": v(22.75, 39.4) * mm, "radius": 2.5 * mm, "construction": true});
            skCircle(sketch, "E3.3.4.1", {"center": v(19.5, 45.03) * mm, "radius": 2.5 * mm, "construction": true});
            skPoint(sketch, "E3.3.4.2", {"position": v(20.75, 47.2) * mm});
            skPoint(sketch, "E3.3.4.3", {"position": v(24, 41.57) * mm});
            skLineSegment(sketch, "E3.3.4.4", {"start": v(22.75, 36.52) * mm, "end": v(20.25, 37.96) * mm});
            skLineSegment(sketch, "E3.3.4.5", {"start": v(25.25, 37.96) * mm, "end": v(22.75, 36.52) * mm});
            skLineSegment(sketch, "E3.3.4.6", {"start": v(25.25, 40.85) * mm, "end": v(25.25, 37.96) * mm});
            skLineSegment(sketch, "E3.3.4.7", {"start": v(22.75, 42.3) * mm, "end": v(25.25, 40.85) * mm});
            skLineSegment(sketch, "E3.3.4.8", {"start": v(17, 46.48) * mm, "end": v(19.5, 47.92) * mm});
            skLineSegment(sketch, "E3.3.4.9", {"start": v(17, 43.59) * mm, "end": v(17, 46.48) * mm});
            skLineSegment(sketch, "E3.3.4.10", {"start": v(19.5, 42.15) * mm, "end": v(17, 43.59) * mm});
            skLineSegment(sketch, "E3.3.4.11", {"start": v(22, 43.59) * mm, "end": v(19.5, 42.15) * mm});
            skLineSegment(sketch, "E3.3.4.12", {"start": v(22, 46.48) * mm, "end": v(22, 43.59) * mm});
            skLineSegment(sketch, "E3.3.4.13", {"start": v(19.5, 47.92) * mm, "end": v(22, 46.48) * mm});
            skLineSegment(sketch, "E3.3.4.14", {"start": v(20.25, 40.85) * mm, "end": v(22.75, 42.3) * mm});
            skLineSegment(sketch, "E3.3.4.15", {"start": v(20.25, 37.96) * mm, "end": v(20.25, 40.85) * mm});
            skCircle(sketch, "E3.3.5.0", {"center": v(22.75, 50.66) * mm, "radius": 2.5 * mm, "construction": true});
            skCircle(sketch, "E3.3.5.1", {"center": v(19.5, 56.3) * mm, "radius": 2.5 * mm, "construction": true});
            skPoint(sketch, "E3.3.5.2", {"position": v(20.75, 58.46) * mm});
            skPoint(sketch, "E3.3.5.3", {"position": v(24, 52.83) * mm});
            skLineSegment(sketch, "E3.3.5.4", {"start": v(22.75, 47.78) * mm, "end": v(20.25, 49.22) * mm});
            skLineSegment(sketch, "E3.3.5.5", {"start": v(25.25, 49.22) * mm, "end": v(22.75, 47.78) * mm});
            skLineSegment(sketch, "E3.3.5.6", {"start": v(25.25, 52.1) * mm, "end": v(25.25, 49.22) * mm});
            skLineSegment(sketch, "E3.3.5.7", {"start": v(22.75, 53.55) * mm, "end": v(25.25, 52.1) * mm});
            skLineSegment(sketch, "E3.3.5.8", {"start": v(17, 57.74) * mm, "end": v(19.5, 59.18) * mm});
            skLineSegment(sketch, "E3.3.5.9", {"start": v(17, 54.85) * mm, "end": v(17, 57.74) * mm});
            skLineSegment(sketch, "E3.3.5.10", {"start": v(19.5, 53.4) * mm, "end": v(17, 54.85) * mm});
            skLineSegment(sketch, "E3.3.5.11", {"start": v(22, 54.85) * mm, "end": v(19.5, 53.4) * mm});
            skLineSegment(sketch, "E3.3.5.12", {"start": v(22, 57.74) * mm, "end": v(22, 54.85) * mm});
            skLineSegment(sketch, "E3.3.5.13", {"start": v(19.5, 59.18) * mm, "end": v(22, 57.74) * mm});
            skLineSegment(sketch, "E3.3.5.14", {"start": v(20.25, 52.1) * mm, "end": v(22.75, 53.55) * mm});
            skLineSegment(sketch, "E3.3.5.15", {"start": v(20.25, 49.22) * mm, "end": v(20.25, 52.1) * mm});
            skCircle(sketch, "E3.3.6.0", {"center": v(22.75, 61.92) * mm, "radius": 2.5 * mm, "construction": true});
            skCircle(sketch, "E3.3.6.1", {"center": v(19.5, 67.55) * mm, "radius": 2.5 * mm, "construction": true});
            skPoint(sketch, "E3.3.6.2", {"position": v(20.75, 69.72) * mm});
            skPoint(sketch, "E3.3.6.3", {"position": v(24, 64.09) * mm});
            skLineSegment(sketch, "E3.3.6.4", {"start": v(22.75, 59.03) * mm, "end": v(20.25, 60.48) * mm});
            skLineSegment(sketch, "E3.3.6.5", {"start": v(25.25, 60.48) * mm, "end": v(22.75, 59.03) * mm});
            skLineSegment(sketch, "E3.3.6.6", {"start": v(25.25, 63.36) * mm, "end": v(25.25, 60.48) * mm});
            skLineSegment(sketch, "E3.3.6.7", {"start": v(22.75, 64.8) * mm, "end": v(25.25, 63.36) * mm});
            skLineSegment(sketch, "E3.3.6.8", {"start": v(17, 69) * mm, "end": v(19.5, 70.44) * mm});
            skLineSegment(sketch, "E3.3.6.9", {"start": v(17, 66.1) * mm, "end": v(17, 69) * mm});
            skLineSegment(sketch, "E3.3.6.10", {"start": v(19.5, 64.66) * mm, "end": v(17, 66.1) * mm});
            skLineSegment(sketch, "E3.3.6.11", {"start": v(22, 66.1) * mm, "end": v(19.5, 64.66) * mm});
            skLineSegment(sketch, "E3.3.6.12", {"start": v(22, 69) * mm, "end": v(22, 66.1) * mm});
            skLineSegment(sketch, "E3.3.6.13", {"start": v(19.5, 70.44) * mm, "end": v(22, 69) * mm});
            skLineSegment(sketch, "E3.3.6.14", {"start": v(20.25, 63.36) * mm, "end": v(22.75, 64.8) * mm});
            skLineSegment(sketch, "E3.3.6.15", {"start": v(20.25, 60.48) * mm, "end": v(20.25, 63.36) * mm});
            skCircle(sketch, "E3.3.7.0", {"center": v(22.75, 73.18) * mm, "radius": 2.5 * mm, "construction": true});
            skCircle(sketch, "E3.3.7.1", {"center": v(19.5, 78.8) * mm, "radius": 2.5 * mm, "construction": true});
            skPoint(sketch, "E3.3.7.2", {"position": v(20.75, 80.97) * mm});
            skPoint(sketch, "E3.3.7.3", {"position": v(24, 75.34) * mm});
            skLineSegment(sketch, "E3.3.7.4", {"start": v(22.75, 70.3) * mm, "end": v(20.25, 71.74) * mm});
            skLineSegment(sketch, "E3.3.7.5", {"start": v(25.25, 71.74) * mm, "end": v(22.75, 70.3) * mm});
            skLineSegment(sketch, "E3.3.7.6", {"start": v(25.25, 74.62) * mm, "end": v(25.25, 71.74) * mm});
            skLineSegment(sketch, "E3.3.7.7", {"start": v(22.75, 76.07) * mm, "end": v(25.25, 74.62) * mm});
            skLineSegment(sketch, "E3.3.7.8", {"start": v(17, 80.25) * mm, "end": v(19.5, 81.7) * mm});
            skLineSegment(sketch, "E3.3.7.9", {"start": v(17, 77.36) * mm, "end": v(17, 80.25) * mm});
            skLineSegment(sketch, "E3.3.7.10", {"start": v(19.5, 75.92) * mm, "end": v(17, 77.36) * mm});
            skLineSegment(sketch, "E3.3.7.11", {"start": v(22, 77.36) * mm, "end": v(19.5, 75.92) * mm});
            skLineSegment(sketch, "E3.3.7.12", {"start": v(22, 80.25) * mm, "end": v(22, 77.36) * mm});
            skLineSegment(sketch, "E3.3.7.13", {"start": v(19.5, 81.7) * mm, "end": v(22, 80.25) * mm});
            skLineSegment(sketch, "E3.3.7.14", {"start": v(20.25, 74.62) * mm, "end": v(22.75, 76.07) * mm});
            skLineSegment(sketch, "E3.3.7.15", {"start": v(20.25, 71.74) * mm, "end": v(20.25, 74.62) * mm});
            skCircle(sketch, "E3.3.8.0", {"center": v(22.75, 84.44) * mm, "radius": 2.5 * mm, "construction": true});
            skCircle(sketch, "E3.3.8.1", {"center": v(19.5, 90.07) * mm, "radius": 2.5 * mm, "construction": true});
            skPoint(sketch, "E3.3.8.2", {"position": v(20.75, 92.23) * mm});
            skPoint(sketch, "E3.3.8.3", {"position": v(24, 86.6) * mm});
            skLineSegment(sketch, "E3.3.8.4", {"start": v(22.75, 81.55) * mm, "end": v(20.25, 83) * mm});
            skLineSegment(sketch, "E3.3.8.5", {"start": v(25.25, 83) * mm, "end": v(22.75, 81.55) * mm});
            skLineSegment(sketch, "E3.3.8.6", {"start": v(25.25, 85.88) * mm, "end": v(25.25, 83) * mm});
            skLineSegment(sketch, "E3.3.8.7", {"start": v(22.75, 87.32) * mm, "end": v(25.25, 85.88) * mm});
            skLineSegment(sketch, "E3.3.8.8", {"start": v(17, 91.51) * mm, "end": v(19.5, 92.95) * mm});
            skLineSegment(sketch, "E3.3.8.9", {"start": v(17, 88.62) * mm, "end": v(17, 91.51) * mm});
            skLineSegment(sketch, "E3.3.8.10", {"start": v(19.5, 87.18) * mm, "end": v(17, 88.62) * mm});
            skLineSegment(sketch, "E3.3.8.11", {"start": v(22, 88.62) * mm, "end": v(19.5, 87.18) * mm});
            skLineSegment(sketch, "E3.3.8.12", {"start": v(22, 91.51) * mm, "end": v(22, 88.62) * mm});
            skLineSegment(sketch, "E3.3.8.13", {"start": v(19.5, 92.95) * mm, "end": v(22, 91.51) * mm});
            skLineSegment(sketch, "E3.3.8.14", {"start": v(20.25, 85.88) * mm, "end": v(22.75, 87.32) * mm});
            skLineSegment(sketch, "E3.3.8.15", {"start": v(20.25, 83) * mm, "end": v(20.25, 85.88) * mm});
            skCircle(sketch, "E3.3.9.0", {"center": v(22.75, 95.7) * mm, "radius": 2.5 * mm, "construction": true});
            skCircle(sketch, "E3.3.9.1", {"center": v(19.5, 101.32) * mm, "radius": 2.5 * mm, "construction": true});
            skPoint(sketch, "E3.3.9.2", {"position": v(20.75, 103.5) * mm});
            skPoint(sketch, "E3.3.9.3", {"position": v(24, 97.86) * mm});
            skLineSegment(sketch, "E3.3.9.4", {"start": v(22.75, 92.8) * mm, "end": v(20.25, 94.25) * mm});
            skLineSegment(sketch, "E3.3.9.5", {"start": v(25.25, 94.25) * mm, "end": v(22.75, 92.8) * mm});
            skLineSegment(sketch, "E3.3.9.6", {"start": v(25.25, 97.14) * mm, "end": v(25.25, 94.25) * mm});
            skLineSegment(sketch, "E3.3.9.7", {"start": v(22.75, 98.58) * mm, "end": v(25.25, 97.14) * mm});
            skLineSegment(sketch, "E3.3.9.8", {"start": v(17, 102.77) * mm, "end": v(19.5, 104.21) * mm});
            skLineSegment(sketch, "E3.3.9.9", {"start": v(17, 99.88) * mm, "end": v(17, 102.77) * mm});
            skLineSegment(sketch, "E3.3.9.10", {"start": v(19.5, 98.44) * mm, "end": v(17, 99.88) * mm});
            skLineSegment(sketch, "E3.3.9.11", {"start": v(22, 99.88) * mm, "end": v(19.5, 98.44) * mm});
            skLineSegment(sketch, "E3.3.9.12", {"start": v(22, 102.77) * mm, "end": v(22, 99.88) * mm});
            skLineSegment(sketch, "E3.3.9.13", {"start": v(19.5, 104.21) * mm, "end": v(22, 102.77) * mm});
            skLineSegment(sketch, "E3.3.9.14", {"start": v(20.25, 97.14) * mm, "end": v(22.75, 98.58) * mm});
            skLineSegment(sketch, "E3.3.9.15", {"start": v(20.25, 94.25) * mm, "end": v(20.25, 97.14) * mm});
            skCircle(sketch, "E3.4.0.0", {"center": v(29.25, -5.63) * mm, "radius": 2.5 * mm, "construction": true});
            skCircle(sketch, "E3.4.0.1", {"center": v(26, 0) * mm, "radius": 2.5 * mm, "construction": true});
            skPoint(sketch, "E3.4.0.2", {"position": v(27.25, 2.17) * mm});
            skPoint(sketch, "E3.4.0.3", {"position": v(30.5, -3.46) * mm});
            skLineSegment(sketch, "E3.4.0.4", {"start": v(29.25, -8.52) * mm, "end": v(26.75, -7.07) * mm});
            skLineSegment(sketch, "E3.4.0.5", {"start": v(31.75, -7.07) * mm, "end": v(29.25, -8.52) * mm});
            skLineSegment(sketch, "E3.4.0.6", {"start": v(31.75, -4.19) * mm, "end": v(31.75, -7.07) * mm});
            skLineSegment(sketch, "E3.4.0.7", {"start": v(29.25, -2.74) * mm, "end": v(31.75, -4.19) * mm});
            skLineSegment(sketch, "E3.4.0.8", {"start": v(23.5, 1.44) * mm, "end": v(26, 2.89) * mm});
            skLineSegment(sketch, "E3.4.0.9", {"start": v(23.5, -1.44) * mm, "end": v(23.5, 1.44) * mm});
            skLineSegment(sketch, "E3.4.0.10", {"start": v(26, -2.89) * mm, "end": v(23.5, -1.44) * mm});
            skLineSegment(sketch, "E3.4.0.11", {"start": v(28.5, -1.44) * mm, "end": v(26, -2.89) * mm});
            skLineSegment(sketch, "E3.4.0.12", {"start": v(28.5, 1.44) * mm, "end": v(28.5, -1.44) * mm});
            skLineSegment(sketch, "E3.4.0.13", {"start": v(26, 2.89) * mm, "end": v(28.5, 1.44) * mm});
            skLineSegment(sketch, "E3.4.0.14", {"start": v(26.75, -4.19) * mm, "end": v(29.25, -2.74) * mm});
            skLineSegment(sketch, "E3.4.0.15", {"start": v(26.75, -7.07) * mm, "end": v(26.75, -4.19) * mm});
            skCircle(sketch, "E3.4.1.0", {"center": v(29.25, 5.63) * mm, "radius": 2.5 * mm, "construction": true});
            skCircle(sketch, "E3.4.1.1", {"center": v(26, 11.26) * mm, "radius": 2.5 * mm, "construction": true});
            skPoint(sketch, "E3.4.1.2", {"position": v(27.25, 13.42) * mm});
            skPoint(sketch, "E3.4.1.3", {"position": v(30.5, 7.8) * mm});
            skLineSegment(sketch, "E3.4.1.4", {"start": v(29.25, 2.74) * mm, "end": v(26.75, 4.19) * mm});
            skLineSegment(sketch, "E3.4.1.5", {"start": v(31.75, 4.19) * mm, "end": v(29.25, 2.74) * mm});
            skLineSegment(sketch, "E3.4.1.6", {"start": v(31.75, 7.07) * mm, "end": v(31.75, 4.19) * mm});
            skLineSegment(sketch, "E3.4.1.7", {"start": v(29.25, 8.52) * mm, "end": v(31.75, 7.07) * mm});
            skLineSegment(sketch, "E3.4.1.8", {"start": v(23.5, 12.7) * mm, "end": v(26, 14.15) * mm});
            skLineSegment(sketch, "E3.4.1.9", {"start": v(23.5, 9.81) * mm, "end": v(23.5, 12.7) * mm});
            skLineSegment(sketch, "E3.4.1.10", {"start": v(26, 8.37) * mm, "end": v(23.5, 9.81) * mm});
            skLineSegment(sketch, "E3.4.1.11", {"start": v(28.5, 9.81) * mm, "end": v(26, 8.37) * mm});
            skLineSegment(sketch, "E3.4.1.12", {"start": v(28.5, 12.7) * mm, "end": v(28.5, 9.81) * mm});
            skLineSegment(sketch, "E3.4.1.13", {"start": v(26, 14.15) * mm, "end": v(28.5, 12.7) * mm});
            skLineSegment(sketch, "E3.4.1.14", {"start": v(26.75, 7.07) * mm, "end": v(29.25, 8.52) * mm});
            skLineSegment(sketch, "E3.4.1.15", {"start": v(26.75, 4.19) * mm, "end": v(26.75, 7.07) * mm});
            skCircle(sketch, "E3.4.2.0", {"center": v(29.25, 16.89) * mm, "radius": 2.5 * mm, "construction": true});
            skCircle(sketch, "E3.4.2.1", {"center": v(26, 22.52) * mm, "radius": 2.5 * mm, "construction": true});
            skPoint(sketch, "E3.4.2.2", {"position": v(27.25, 24.68) * mm});
            skPoint(sketch, "E3.4.2.3", {"position": v(30.5, 19.05) * mm});
            skLineSegment(sketch, "E3.4.2.4", {"start": v(29.25, 14) * mm, "end": v(26.75, 15.44) * mm});
            skLineSegment(sketch, "E3.4.2.5", {"start": v(31.75, 15.44) * mm, "end": v(29.25, 14) * mm});
            skLineSegment(sketch, "E3.4.2.6", {"start": v(31.75, 18.33) * mm, "end": v(31.75, 15.44) * mm});
            skLineSegment(sketch, "E3.4.2.7", {"start": v(29.25, 19.77) * mm, "end": v(31.75, 18.33) * mm});
            skLineSegment(sketch, "E3.4.2.8", {"start": v(23.5, 23.96) * mm, "end": v(26, 25.4) * mm});
            skLineSegment(sketch, "E3.4.2.9", {"start": v(23.5, 21.07) * mm, "end": v(23.5, 23.96) * mm});
            skLineSegment(sketch, "E3.4.2.10", {"start": v(26, 19.63) * mm, "end": v(23.5, 21.07) * mm});
            skLineSegment(sketch, "E3.4.2.11", {"start": v(28.5, 21.07) * mm, "end": v(26, 19.63) * mm});
            skLineSegment(sketch, "E3.4.2.12", {"start": v(28.5, 23.96) * mm, "end": v(28.5, 21.07) * mm});
            skLineSegment(sketch, "E3.4.2.13", {"start": v(26, 25.4) * mm, "end": v(28.5, 23.96) * mm});
            skLineSegment(sketch, "E3.4.2.14", {"start": v(26.75, 18.33) * mm, "end": v(29.25, 19.77) * mm});
            skLineSegment(sketch, "E3.4.2.15", {"start": v(26.75, 15.44) * mm, "end": v(26.75, 18.33) * mm});
            skCircle(sketch, "E3.4.3.0", {"center": v(29.25, 28.15) * mm, "radius": 2.5 * mm, "construction": true});
            skCircle(sketch, "E3.4.3.1", {"center": v(26, 33.77) * mm, "radius": 2.5 * mm, "construction": true});
            skPoint(sketch, "E3.4.3.2", {"position": v(27.25, 35.94) * mm});
            skPoint(sketch, "E3.4.3.3", {"position": v(30.5, 30.31) * mm});
            skLineSegment(sketch, "E3.4.3.4", {"start": v(29.25, 25.26) * mm, "end": v(26.75, 26.7) * mm});
            skLineSegment(sketch, "E3.4.3.5", {"start": v(31.75, 26.7) * mm, "end": v(29.25, 25.26) * mm});
            skLineSegment(sketch, "E3.4.3.6", {"start": v(31.75, 29.59) * mm, "end": v(31.75, 26.7) * mm});
            skLineSegment(sketch, "E3.4.3.7", {"start": v(29.25, 31.03) * mm, "end": v(31.75, 29.59) * mm});
            skLineSegment(sketch, "E3.4.3.8", {"start": v(23.5, 35.22) * mm, "end": v(26, 36.66) * mm});
            skLineSegment(sketch, "E3.4.3.9", {"start": v(23.5, 32.33) * mm, "end": v(23.5, 35.22) * mm});
            skLineSegment(sketch, "E3.4.3.10", {"start": v(26, 30.89) * mm, "end": v(23.5, 32.33) * mm});
            skLineSegment(sketch, "E3.4.3.11", {"start": v(28.5, 32.33) * mm, "end": v(26, 30.89) * mm});
            skLineSegment(sketch, "E3.4.3.12", {"start": v(28.5, 35.22) * mm, "end": v(28.5, 32.33) * mm});
            skLineSegment(sketch, "E3.4.3.13", {"start": v(26, 36.66) * mm, "end": v(28.5, 35.22) * mm});
            skLineSegment(sketch, "E3.4.3.14", {"start": v(26.75, 29.59) * mm, "end": v(29.25, 31.03) * mm});
            skLineSegment(sketch, "E3.4.3.15", {"start": v(26.75, 26.7) * mm, "end": v(26.75, 29.59) * mm});
            skCircle(sketch, "E3.4.4.0", {"center": v(29.25, 39.4) * mm, "radius": 2.5 * mm, "construction": true});
            skCircle(sketch, "E3.4.4.1", {"center": v(26, 45.03) * mm, "radius": 2.5 * mm, "construction": true});
            skPoint(sketch, "E3.4.4.2", {"position": v(27.25, 47.2) * mm});
            skPoint(sketch, "E3.4.4.3", {"position": v(30.5, 41.57) * mm});
            skLineSegment(sketch, "E3.4.4.4", {"start": v(29.25, 36.52) * mm, "end": v(26.75, 37.96) * mm});
            skLineSegment(sketch, "E3.4.4.5", {"start": v(31.75, 37.96) * mm, "end": v(29.25, 36.52) * mm});
            skLineSegment(sketch, "E3.4.4.6", {"start": v(31.75, 40.85) * mm, "end": v(31.75, 37.96) * mm});
            skLineSegment(sketch, "E3.4.4.7", {"start": v(29.25, 42.3) * mm, "end": v(31.75, 40.85) * mm});
            skLineSegment(sketch, "E3.4.4.8", {"start": v(23.5, 46.48) * mm, "end": v(26, 47.92) * mm});
            skLineSegment(sketch, "E3.4.4.9", {"start": v(23.5, 43.59) * mm, "end": v(23.5, 46.48) * mm});
            skLineSegment(sketch, "E3.4.4.10", {"start": v(26, 42.15) * mm, "end": v(23.5, 43.59) * mm});
            skLineSegment(sketch, "E3.4.4.11", {"start": v(28.5, 43.59) * mm, "end": v(26, 42.15) * mm});
            skLineSegment(sketch, "E3.4.4.12", {"start": v(28.5, 46.48) * mm, "end": v(28.5, 43.59) * mm});
            skLineSegment(sketch, "E3.4.4.13", {"start": v(26, 47.92) * mm, "end": v(28.5, 46.48) * mm});
            skLineSegment(sketch, "E3.4.4.14", {"start": v(26.75, 40.85) * mm, "end": v(29.25, 42.3) * mm});
            skLineSegment(sketch, "E3.4.4.15", {"start": v(26.75, 37.96) * mm, "end": v(26.75, 40.85) * mm});
            skCircle(sketch, "E3.4.5.0", {"center": v(29.25, 50.66) * mm, "radius": 2.5 * mm, "construction": true});
            skCircle(sketch, "E3.4.5.1", {"center": v(26, 56.3) * mm, "radius": 2.5 * mm, "construction": true});
            skPoint(sketch, "E3.4.5.2", {"position": v(27.25, 58.46) * mm});
            skPoint(sketch, "E3.4.5.3", {"position": v(30.5, 52.83) * mm});
            skLineSegment(sketch, "E3.4.5.4", {"start": v(29.25, 47.78) * mm, "end": v(26.75, 49.22) * mm});
            skLineSegment(sketch, "E3.4.5.5", {"start": v(31.75, 49.22) * mm, "end": v(29.25, 47.78) * mm});
            skLineSegment(sketch, "E3.4.5.6", {"start": v(31.75, 52.1) * mm, "end": v(31.75, 49.22) * mm});
            skLineSegment(sketch, "E3.4.5.7", {"start": v(29.25, 53.55) * mm, "end": v(31.75, 52.1) * mm});
            skLineSegment(sketch, "E3.4.5.8", {"start": v(23.5, 57.74) * mm, "end": v(26, 59.18) * mm});
            skLineSegment(sketch, "E3.4.5.9", {"start": v(23.5, 54.85) * mm, "end": v(23.5, 57.74) * mm});
            skLineSegment(sketch, "E3.4.5.10", {"start": v(26, 53.4) * mm, "end": v(23.5, 54.85) * mm});
            skLineSegment(sketch, "E3.4.5.11", {"start": v(28.5, 54.85) * mm, "end": v(26, 53.4) * mm});
            skLineSegment(sketch, "E3.4.5.12", {"start": v(28.5, 57.74) * mm, "end": v(28.5, 54.85) * mm});
            skLineSegment(sketch, "E3.4.5.13", {"start": v(26, 59.18) * mm, "end": v(28.5, 57.74) * mm});
            skLineSegment(sketch, "E3.4.5.14", {"start": v(26.75, 52.1) * mm, "end": v(29.25, 53.55) * mm});
            skLineSegment(sketch, "E3.4.5.15", {"start": v(26.75, 49.22) * mm, "end": v(26.75, 52.1) * mm});
            skCircle(sketch, "E3.4.6.0", {"center": v(29.25, 61.92) * mm, "radius": 2.5 * mm, "construction": true});
            skCircle(sketch, "E3.4.6.1", {"center": v(26, 67.55) * mm, "radius": 2.5 * mm, "construction": true});
            skPoint(sketch, "E3.4.6.2", {"position": v(27.25, 69.72) * mm});
            skPoint(sketch, "E3.4.6.3", {"position": v(30.5, 64.09) * mm});
            skLineSegment(sketch, "E3.4.6.4", {"start": v(29.25, 59.03) * mm, "end": v(26.75, 60.48) * mm});
            skLineSegment(sketch, "E3.4.6.5", {"start": v(31.75, 60.48) * mm, "end": v(29.25, 59.03) * mm});
            skLineSegment(sketch, "E3.4.6.6", {"start": v(31.75, 63.36) * mm, "end": v(31.75, 60.48) * mm});
            skLineSegment(sketch, "E3.4.6.7", {"start": v(29.25, 64.8) * mm, "end": v(31.75, 63.36) * mm});
            skLineSegment(sketch, "E3.4.6.8", {"start": v(23.5, 69) * mm, "end": v(26, 70.44) * mm});
            skLineSegment(sketch, "E3.4.6.9", {"start": v(23.5, 66.1) * mm, "end": v(23.5, 69) * mm});
            skLineSegment(sketch, "E3.4.6.10", {"start": v(26, 64.66) * mm, "end": v(23.5, 66.1) * mm});
            skLineSegment(sketch, "E3.4.6.11", {"start": v(28.5, 66.1) * mm, "end": v(26, 64.66) * mm});
            skLineSegment(sketch, "E3.4.6.12", {"start": v(28.5, 69) * mm, "end": v(28.5, 66.1) * mm});
            skLineSegment(sketch, "E3.4.6.13", {"start": v(26, 70.44) * mm, "end": v(28.5, 69) * mm});
            skLineSegment(sketch, "E3.4.6.14", {"start": v(26.75, 63.36) * mm, "end": v(29.25, 64.8) * mm});
            skLineSegment(sketch, "E3.4.6.15", {"start": v(26.75, 60.48) * mm, "end": v(26.75, 63.36) * mm});
            skCircle(sketch, "E3.4.7.0", {"center": v(29.25, 73.18) * mm, "radius": 2.5 * mm, "construction": true});
            skCircle(sketch, "E3.4.7.1", {"center": v(26, 78.8) * mm, "radius": 2.5 * mm, "construction": true});
            skPoint(sketch, "E3.4.7.2", {"position": v(27.25, 80.97) * mm});
            skPoint(sketch, "E3.4.7.3", {"position": v(30.5, 75.34) * mm});
            skLineSegment(sketch, "E3.4.7.4", {"start": v(29.25, 70.3) * mm, "end": v(26.75, 71.74) * mm});
            skLineSegment(sketch, "E3.4.7.5", {"start": v(31.75, 71.74) * mm, "end": v(29.25, 70.3) * mm});
            skLineSegment(sketch, "E3.4.7.6", {"start": v(31.75, 74.62) * mm, "end": v(31.75, 71.74) * mm});
            skLineSegment(sketch, "E3.4.7.7", {"start": v(29.25, 76.07) * mm, "end": v(31.75, 74.62) * mm});
            skLineSegment(sketch, "E3.4.7.8", {"start": v(23.5, 80.25) * mm, "end": v(26, 81.7) * mm});
            skLineSegment(sketch, "E3.4.7.9", {"start": v(23.5, 77.36) * mm, "end": v(23.5, 80.25) * mm});
            skLineSegment(sketch, "E3.4.7.10", {"start": v(26, 75.92) * mm, "end": v(23.5, 77.36) * mm});
            skLineSegment(sketch, "E3.4.7.11", {"start": v(28.5, 77.36) * mm, "end": v(26, 75.92) * mm});
            skLineSegment(sketch, "E3.4.7.12", {"start": v(28.5, 80.25) * mm, "end": v(28.5, 77.36) * mm});
            skLineSegment(sketch, "E3.4.7.13", {"start": v(26, 81.7) * mm, "end": v(28.5, 80.25) * mm});
            skLineSegment(sketch, "E3.4.7.14", {"start": v(26.75, 74.62) * mm, "end": v(29.25, 76.07) * mm});
            skLineSegment(sketch, "E3.4.7.15", {"start": v(26.75, 71.74) * mm, "end": v(26.75, 74.62) * mm});
            skCircle(sketch, "E3.4.8.0", {"center": v(29.25, 84.44) * mm, "radius": 2.5 * mm, "construction": true});
            skCircle(sketch, "E3.4.8.1", {"center": v(26, 90.07) * mm, "radius": 2.5 * mm, "construction": true});
            skPoint(sketch, "E3.4.8.2", {"position": v(27.25, 92.23) * mm});
            skPoint(sketch, "E3.4.8.3", {"position": v(30.5, 86.6) * mm});
            skLineSegment(sketch, "E3.4.8.4", {"start": v(29.25, 81.55) * mm, "end": v(26.75, 83) * mm});
            skLineSegment(sketch, "E3.4.8.5", {"start": v(31.75, 83) * mm, "end": v(29.25, 81.55) * mm});
            skLineSegment(sketch, "E3.4.8.6", {"start": v(31.75, 85.88) * mm, "end": v(31.75, 83) * mm});
            skLineSegment(sketch, "E3.4.8.7", {"start": v(29.25, 87.32) * mm, "end": v(31.75, 85.88) * mm});
            skLineSegment(sketch, "E3.4.8.8", {"start": v(23.5, 91.51) * mm, "end": v(26, 92.95) * mm});
            skLineSegment(sketch, "E3.4.8.9", {"start": v(23.5, 88.62) * mm, "end": v(23.5, 91.51) * mm});
            skLineSegment(sketch, "E3.4.8.10", {"start": v(26, 87.18) * mm, "end": v(23.5, 88.62) * mm});
            skLineSegment(sketch, "E3.4.8.11", {"start": v(28.5, 88.62) * mm, "end": v(26, 87.18) * mm});
            skLineSegment(sketch, "E3.4.8.12", {"start": v(28.5, 91.51) * mm, "end": v(28.5, 88.62) * mm});
            skLineSegment(sketch, "E3.4.8.13", {"start": v(26, 92.95) * mm, "end": v(28.5, 91.51) * mm});
            skLineSegment(sketch, "E3.4.8.14", {"start": v(26.75, 85.88) * mm, "end": v(29.25, 87.32) * mm});
            skLineSegment(sketch, "E3.4.8.15", {"start": v(26.75, 83) * mm, "end": v(26.75, 85.88) * mm});
            skCircle(sketch, "E3.4.9.0", {"center": v(29.25, 95.7) * mm, "radius": 2.5 * mm, "construction": true});
            skCircle(sketch, "E3.4.9.1", {"center": v(26, 101.32) * mm, "radius": 2.5 * mm, "construction": true});
            skPoint(sketch, "E3.4.9.2", {"position": v(27.25, 103.5) * mm});
            skPoint(sketch, "E3.4.9.3", {"position": v(30.5, 97.86) * mm});
            skLineSegment(sketch, "E3.4.9.4", {"start": v(29.25, 92.8) * mm, "end": v(26.75, 94.25) * mm});
            skLineSegment(sketch, "E3.4.9.5", {"start": v(31.75, 94.25) * mm, "end": v(29.25, 92.8) * mm});
            skLineSegment(sketch, "E3.4.9.6", {"start": v(31.75, 97.14) * mm, "end": v(31.75, 94.25) * mm});
            skLineSegment(sketch, "E3.4.9.7", {"start": v(29.25, 98.58) * mm, "end": v(31.75, 97.14) * mm});
            skLineSegment(sketch, "E3.4.9.8", {"start": v(23.5, 102.77) * mm, "end": v(26, 104.21) * mm});
            skLineSegment(sketch, "E3.4.9.9", {"start": v(23.5, 99.88) * mm, "end": v(23.5, 102.77) * mm});
            skLineSegment(sketch, "E3.4.9.10", {"start": v(26, 98.44) * mm, "end": v(23.5, 99.88) * mm});
            skLineSegment(sketch, "E3.4.9.11", {"start": v(28.5, 99.88) * mm, "end": v(26, 98.44) * mm});
            skLineSegment(sketch, "E3.4.9.12", {"start": v(28.5, 102.77) * mm, "end": v(28.5, 99.88) * mm});
            skLineSegment(sketch, "E3.4.9.13", {"start": v(26, 104.21) * mm, "end": v(28.5, 102.77) * mm});
            skLineSegment(sketch, "E3.4.9.14", {"start": v(26.75, 97.14) * mm, "end": v(29.25, 98.58) * mm});
            skLineSegment(sketch, "E3.4.9.15", {"start": v(26.75, 94.25) * mm, "end": v(26.75, 97.14) * mm});
            skCircle(sketch, "E3.5.0.0", {"center": v(35.75, -5.63) * mm, "radius": 2.5 * mm, "construction": true});
            skCircle(sketch, "E3.5.0.1", {"center": v(32.5, 0) * mm, "radius": 2.5 * mm, "construction": true});
            skPoint(sketch, "E3.5.0.2", {"position": v(33.75, 2.17) * mm});
            skPoint(sketch, "E3.5.0.3", {"position": v(37, -3.46) * mm});
            skLineSegment(sketch, "E3.5.0.4", {"start": v(35.75, -8.52) * mm, "end": v(33.25, -7.07) * mm});
            skLineSegment(sketch, "E3.5.0.5", {"start": v(38.25, -7.07) * mm, "end": v(35.75, -8.52) * mm});
            skLineSegment(sketch, "E3.5.0.6", {"start": v(38.25, -4.19) * mm, "end": v(38.25, -7.07) * mm});
            skLineSegment(sketch, "E3.5.0.7", {"start": v(35.75, -2.74) * mm, "end": v(38.25, -4.19) * mm});
            skLineSegment(sketch, "E3.5.0.8", {"start": v(30, 1.44) * mm, "end": v(32.5, 2.89) * mm});
            skLineSegment(sketch, "E3.5.0.9", {"start": v(30, -1.44) * mm, "end": v(30, 1.44) * mm});
            skLineSegment(sketch, "E3.5.0.10", {"start": v(32.5, -2.89) * mm, "end": v(30, -1.44) * mm});
            skLineSegment(sketch, "E3.5.0.11", {"start": v(35, -1.44) * mm, "end": v(32.5, -2.89) * mm});
            skLineSegment(sketch, "E3.5.0.12", {"start": v(35, 1.44) * mm, "end": v(35, -1.44) * mm});
            skLineSegment(sketch, "E3.5.0.13", {"start": v(32.5, 2.89) * mm, "end": v(35, 1.44) * mm});
            skLineSegment(sketch, "E3.5.0.14", {"start": v(33.25, -4.19) * mm, "end": v(35.75, -2.74) * mm});
            skLineSegment(sketch, "E3.5.0.15", {"start": v(33.25, -7.07) * mm, "end": v(33.25, -4.19) * mm});
            skCircle(sketch, "E3.5.1.0", {"center": v(35.75, 5.63) * mm, "radius": 2.5 * mm, "construction": true});
            skCircle(sketch, "E3.5.1.1", {"center": v(32.5, 11.26) * mm, "radius": 2.5 * mm, "construction": true});
            skPoint(sketch, "E3.5.1.2", {"position": v(33.75, 13.42) * mm});
            skPoint(sketch, "E3.5.1.3", {"position": v(37, 7.8) * mm});
            skLineSegment(sketch, "E3.5.1.4", {"start": v(35.75, 2.74) * mm, "end": v(33.25, 4.19) * mm});
            skLineSegment(sketch, "E3.5.1.5", {"start": v(38.25, 4.19) * mm, "end": v(35.75, 2.74) * mm});
            skLineSegment(sketch, "E3.5.1.6", {"start": v(38.25, 7.07) * mm, "end": v(38.25, 4.19) * mm});
            skLineSegment(sketch, "E3.5.1.7", {"start": v(35.75, 8.52) * mm, "end": v(38.25, 7.07) * mm});
            skLineSegment(sketch, "E3.5.1.8", {"start": v(30, 12.7) * mm, "end": v(32.5, 14.15) * mm});
            skLineSegment(sketch, "E3.5.1.9", {"start": v(30, 9.81) * mm, "end": v(30, 12.7) * mm});
            skLineSegment(sketch, "E3.5.1.10", {"start": v(32.5, 8.37) * mm, "end": v(30, 9.81) * mm});
            skLineSegment(sketch, "E3.5.1.11", {"start": v(35, 9.81) * mm, "end": v(32.5, 8.37) * mm});
            skLineSegment(sketch, "E3.5.1.12", {"start": v(35, 12.7) * mm, "end": v(35, 9.81) * mm});
            skLineSegment(sketch, "E3.5.1.13", {"start": v(32.5, 14.15) * mm, "end": v(35, 12.7) * mm});
            skLineSegment(sketch, "E3.5.1.14", {"start": v(33.25, 7.07) * mm, "end": v(35.75, 8.52) * mm});
            skLineSegment(sketch, "E3.5.1.15", {"start": v(33.25, 4.19) * mm, "end": v(33.25, 7.07) * mm});
            skCircle(sketch, "E3.5.2.0", {"center": v(35.75, 16.89) * mm, "radius": 2.5 * mm, "construction": true});
            skCircle(sketch, "E3.5.2.1", {"center": v(32.5, 22.52) * mm, "radius": 2.5 * mm, "construction": true});
            skPoint(sketch, "E3.5.2.2", {"position": v(33.75, 24.68) * mm});
            skPoint(sketch, "E3.5.2.3", {"position": v(37, 19.05) * mm});
            skLineSegment(sketch, "E3.5.2.4", {"start": v(35.75, 14) * mm, "end": v(33.25, 15.44) * mm});
            skLineSegment(sketch, "E3.5.2.5", {"start": v(38.25, 15.44) * mm, "end": v(35.75, 14) * mm});
            skLineSegment(sketch, "E3.5.2.6", {"start": v(38.25, 18.33) * mm, "end": v(38.25, 15.44) * mm});
            skLineSegment(sketch, "E3.5.2.7", {"start": v(35.75, 19.77) * mm, "end": v(38.25, 18.33) * mm});
            skLineSegment(sketch, "E3.5.2.8", {"start": v(30, 23.96) * mm, "end": v(32.5, 25.4) * mm});
            skLineSegment(sketch, "E3.5.2.9", {"start": v(30, 21.07) * mm, "end": v(30, 23.96) * mm});
            skLineSegment(sketch, "E3.5.2.10", {"start": v(32.5, 19.63) * mm, "end": v(30, 21.07) * mm});
            skLineSegment(sketch, "E3.5.2.11", {"start": v(35, 21.07) * mm, "end": v(32.5, 19.63) * mm});
            skLineSegment(sketch, "E3.5.2.12", {"start": v(35, 23.96) * mm, "end": v(35, 21.07) * mm});
            skLineSegment(sketch, "E3.5.2.13", {"start": v(32.5, 25.4) * mm, "end": v(35, 23.96) * mm});
            skLineSegment(sketch, "E3.5.2.14", {"start": v(33.25, 18.33) * mm, "end": v(35.75, 19.77) * mm});
            skLineSegment(sketch, "E3.5.2.15", {"start": v(33.25, 15.44) * mm, "end": v(33.25, 18.33) * mm});
            skCircle(sketch, "E3.5.3.0", {"center": v(35.75, 28.15) * mm, "radius": 2.5 * mm, "construction": true});
            skCircle(sketch, "E3.5.3.1", {"center": v(32.5, 33.77) * mm, "radius": 2.5 * mm, "construction": true});
            skPoint(sketch, "E3.5.3.2", {"position": v(33.75, 35.94) * mm});
            skPoint(sketch, "E3.5.3.3", {"position": v(37, 30.31) * mm});
            skLineSegment(sketch, "E3.5.3.4", {"start": v(35.75, 25.26) * mm, "end": v(33.25, 26.7) * mm});
            skLineSegment(sketch, "E3.5.3.5", {"start": v(38.25, 26.7) * mm, "end": v(35.75, 25.26) * mm});
            skLineSegment(sketch, "E3.5.3.6", {"start": v(38.25, 29.59) * mm, "end": v(38.25, 26.7) * mm});
            skLineSegment(sketch, "E3.5.3.7", {"start": v(35.75, 31.03) * mm, "end": v(38.25, 29.59) * mm});
            skLineSegment(sketch, "E3.5.3.8", {"start": v(30, 35.22) * mm, "end": v(32.5, 36.66) * mm});
            skLineSegment(sketch, "E3.5.3.9", {"start": v(30, 32.33) * mm, "end": v(30, 35.22) * mm});
            skLineSegment(sketch, "E3.5.3.10", {"start": v(32.5, 30.89) * mm, "end": v(30, 32.33) * mm});
            skLineSegment(sketch, "E3.5.3.11", {"start": v(35, 32.33) * mm, "end": v(32.5, 30.89) * mm});
            skLineSegment(sketch, "E3.5.3.12", {"start": v(35, 35.22) * mm, "end": v(35, 32.33) * mm});
            skLineSegment(sketch, "E3.5.3.13", {"start": v(32.5, 36.66) * mm, "end": v(35, 35.22) * mm});
            skLineSegment(sketch, "E3.5.3.14", {"start": v(33.25, 29.59) * mm, "end": v(35.75, 31.03) * mm});
            skLineSegment(sketch, "E3.5.3.15", {"start": v(33.25, 26.7) * mm, "end": v(33.25, 29.59) * mm});
            skCircle(sketch, "E3.5.4.0", {"center": v(35.75, 39.4) * mm, "radius": 2.5 * mm, "construction": true});
            skCircle(sketch, "E3.5.4.1", {"center": v(32.5, 45.03) * mm, "radius": 2.5 * mm, "construction": true});
            skPoint(sketch, "E3.5.4.2", {"position": v(33.75, 47.2) * mm});
            skPoint(sketch, "E3.5.4.3", {"position": v(37, 41.57) * mm});
            skLineSegment(sketch, "E3.5.4.4", {"start": v(35.75, 36.52) * mm, "end": v(33.25, 37.96) * mm});
            skLineSegment(sketch, "E3.5.4.5", {"start": v(38.25, 37.96) * mm, "end": v(35.75, 36.52) * mm});
            skLineSegment(sketch, "E3.5.4.6", {"start": v(38.25, 40.85) * mm, "end": v(38.25, 37.96) * mm});
            skLineSegment(sketch, "E3.5.4.7", {"start": v(35.75, 42.3) * mm, "end": v(38.25, 40.85) * mm});
            skLineSegment(sketch, "E3.5.4.8", {"start": v(30, 46.48) * mm, "end": v(32.5, 47.92) * mm});
            skLineSegment(sketch, "E3.5.4.9", {"start": v(30, 43.59) * mm, "end": v(30, 46.48) * mm});
            skLineSegment(sketch, "E3.5.4.10", {"start": v(32.5, 42.15) * mm, "end": v(30, 43.59) * mm});
            skLineSegment(sketch, "E3.5.4.11", {"start": v(35, 43.59) * mm, "end": v(32.5, 42.15) * mm});
            skLineSegment(sketch, "E3.5.4.12", {"start": v(35, 46.48) * mm, "end": v(35, 43.59) * mm});
            skLineSegment(sketch, "E3.5.4.13", {"start": v(32.5, 47.92) * mm, "end": v(35, 46.48) * mm});
            skLineSegment(sketch, "E3.5.4.14", {"start": v(33.25, 40.85) * mm, "end": v(35.75, 42.3) * mm});
            skLineSegment(sketch, "E3.5.4.15", {"start": v(33.25, 37.96) * mm, "end": v(33.25, 40.85) * mm});
            skCircle(sketch, "E3.5.5.0", {"center": v(35.75, 50.66) * mm, "radius": 2.5 * mm, "construction": true});
            skCircle(sketch, "E3.5.5.1", {"center": v(32.5, 56.3) * mm, "radius": 2.5 * mm, "construction": true});
            skPoint(sketch, "E3.5.5.2", {"position": v(33.75, 58.46) * mm});
            skPoint(sketch, "E3.5.5.3", {"position": v(37, 52.83) * mm});
            skLineSegment(sketch, "E3.5.5.4", {"start": v(35.75, 47.78) * mm, "end": v(33.25, 49.22) * mm});
            skLineSegment(sketch, "E3.5.5.5", {"start": v(38.25, 49.22) * mm, "end": v(35.75, 47.78) * mm});
            skLineSegment(sketch, "E3.5.5.6", {"start": v(38.25, 52.1) * mm, "end": v(38.25, 49.22) * mm});
            skLineSegment(sketch, "E3.5.5.7", {"start": v(35.75, 53.55) * mm, "end": v(38.25, 52.1) * mm});
            skLineSegment(sketch, "E3.5.5.8", {"start": v(30, 57.74) * mm, "end": v(32.5, 59.18) * mm});
            skLineSegment(sketch, "E3.5.5.9", {"start": v(30, 54.85) * mm, "end": v(30, 57.74) * mm});
            skLineSegment(sketch, "E3.5.5.10", {"start": v(32.5, 53.4) * mm, "end": v(30, 54.85) * mm});
            skLineSegment(sketch, "E3.5.5.11", {"start": v(35, 54.85) * mm, "end": v(32.5, 53.4) * mm});
            skLineSegment(sketch, "E3.5.5.12", {"start": v(35, 57.74) * mm, "end": v(35, 54.85) * mm});
            skLineSegment(sketch, "E3.5.5.13", {"start": v(32.5, 59.18) * mm, "end": v(35, 57.74) * mm});
            skLineSegment(sketch, "E3.5.5.14", {"start": v(33.25, 52.1) * mm, "end": v(35.75, 53.55) * mm});
            skLineSegment(sketch, "E3.5.5.15", {"start": v(33.25, 49.22) * mm, "end": v(33.25, 52.1) * mm});
            skCircle(sketch, "E3.5.6.0", {"center": v(35.75, 61.92) * mm, "radius": 2.5 * mm, "construction": true});
            skCircle(sketch, "E3.5.6.1", {"center": v(32.5, 67.55) * mm, "radius": 2.5 * mm, "construction": true});
            skPoint(sketch, "E3.5.6.2", {"position": v(33.75, 69.72) * mm});
            skPoint(sketch, "E3.5.6.3", {"position": v(37, 64.09) * mm});
            skLineSegment(sketch, "E3.5.6.4", {"start": v(35.75, 59.03) * mm, "end": v(33.25, 60.48) * mm});
            skLineSegment(sketch, "E3.5.6.5", {"start": v(38.25, 60.48) * mm, "end": v(35.75, 59.03) * mm});
            skLineSegment(sketch, "E3.5.6.6", {"start": v(38.25, 63.36) * mm, "end": v(38.25, 60.48) * mm});
            skLineSegment(sketch, "E3.5.6.7", {"start": v(35.75, 64.8) * mm, "end": v(38.25, 63.36) * mm});
            skLineSegment(sketch, "E3.5.6.8", {"start": v(30, 69) * mm, "end": v(32.5, 70.44) * mm});
            skLineSegment(sketch, "E3.5.6.9", {"start": v(30, 66.1) * mm, "end": v(30, 69) * mm});
            skLineSegment(sketch, "E3.5.6.10", {"start": v(32.5, 64.66) * mm, "end": v(30, 66.1) * mm});
            skLineSegment(sketch, "E3.5.6.11", {"start": v(35, 66.1) * mm, "end": v(32.5, 64.66) * mm});
            skLineSegment(sketch, "E3.5.6.12", {"start": v(35, 69) * mm, "end": v(35, 66.1) * mm});
            skLineSegment(sketch, "E3.5.6.13", {"start": v(32.5, 70.44) * mm, "end": v(35, 69) * mm});
            skLineSegment(sketch, "E3.5.6.14", {"start": v(33.25, 63.36) * mm, "end": v(35.75, 64.8) * mm});
            skLineSegment(sketch, "E3.5.6.15", {"start": v(33.25, 60.48) * mm, "end": v(33.25, 63.36) * mm});
            skCircle(sketch, "E3.5.7.0", {"center": v(35.75, 73.18) * mm, "radius": 2.5 * mm, "construction": true});
            skCircle(sketch, "E3.5.7.1", {"center": v(32.5, 78.8) * mm, "radius": 2.5 * mm, "construction": true});
            skPoint(sketch, "E3.5.7.2", {"position": v(33.75, 80.97) * mm});
            skPoint(sketch, "E3.5.7.3", {"position": v(37, 75.34) * mm});
            skLineSegment(sketch, "E3.5.7.4", {"start": v(35.75, 70.3) * mm, "end": v(33.25, 71.74) * mm});
            skLineSegment(sketch, "E3.5.7.5", {"start": v(38.25, 71.74) * mm, "end": v(35.75, 70.3) * mm});
            skLineSegment(sketch, "E3.5.7.6", {"start": v(38.25, 74.62) * mm, "end": v(38.25, 71.74) * mm});
            skLineSegment(sketch, "E3.5.7.7", {"start": v(35.75, 76.07) * mm, "end": v(38.25, 74.62) * mm});
            skLineSegment(sketch, "E3.5.7.8", {"start": v(30, 80.25) * mm, "end": v(32.5, 81.7) * mm});
            skLineSegment(sketch, "E3.5.7.9", {"start": v(30, 77.36) * mm, "end": v(30, 80.25) * mm});
            skLineSegment(sketch, "E3.5.7.10", {"start": v(32.5, 75.92) * mm, "end": v(30, 77.36) * mm});
            skLineSegment(sketch, "E3.5.7.11", {"start": v(35, 77.36) * mm, "end": v(32.5, 75.92) * mm});
            skLineSegment(sketch, "E3.5.7.12", {"start": v(35, 80.25) * mm, "end": v(35, 77.36) * mm});
            skLineSegment(sketch, "E3.5.7.13", {"start": v(32.5, 81.7) * mm, "end": v(35, 80.25) * mm});
            skLineSegment(sketch, "E3.5.7.14", {"start": v(33.25, 74.62) * mm, "end": v(35.75, 76.07) * mm});
            skLineSegment(sketch, "E3.5.7.15", {"start": v(33.25, 71.74) * mm, "end": v(33.25, 74.62) * mm});
            skCircle(sketch, "E3.5.8.0", {"center": v(35.75, 84.44) * mm, "radius": 2.5 * mm, "construction": true});
            skCircle(sketch, "E3.5.8.1", {"center": v(32.5, 90.07) * mm, "radius": 2.5 * mm, "construction": true});
            skPoint(sketch, "E3.5.8.2", {"position": v(33.75, 92.23) * mm});
            skPoint(sketch, "E3.5.8.3", {"position": v(37, 86.6) * mm});
            skLineSegment(sketch, "E3.5.8.4", {"start": v(35.75, 81.55) * mm, "end": v(33.25, 83) * mm});
            skLineSegment(sketch, "E3.5.8.5", {"start": v(38.25, 83) * mm, "end": v(35.75, 81.55) * mm});
            skLineSegment(sketch, "E3.5.8.6", {"start": v(38.25, 85.88) * mm, "end": v(38.25, 83) * mm});
            skLineSegment(sketch, "E3.5.8.7", {"start": v(35.75, 87.32) * mm, "end": v(38.25, 85.88) * mm});
            skLineSegment(sketch, "E3.5.8.8", {"start": v(30, 91.51) * mm, "end": v(32.5, 92.95) * mm});
            skLineSegment(sketch, "E3.5.8.9", {"start": v(30, 88.62) * mm, "end": v(30, 91.51) * mm});
            skLineSegment(sketch, "E3.5.8.10", {"start": v(32.5, 87.18) * mm, "end": v(30, 88.62) * mm});
            skLineSegment(sketch, "E3.5.8.11", {"start": v(35, 88.62) * mm, "end": v(32.5, 87.18) * mm});
            skLineSegment(sketch, "E3.5.8.12", {"start": v(35, 91.51) * mm, "end": v(35, 88.62) * mm});
            skLineSegment(sketch, "E3.5.8.13", {"start": v(32.5, 92.95) * mm, "end": v(35, 91.51) * mm});
            skLineSegment(sketch, "E3.5.8.14", {"start": v(33.25, 85.88) * mm, "end": v(35.75, 87.32) * mm});
            skLineSegment(sketch, "E3.5.8.15", {"start": v(33.25, 83) * mm, "end": v(33.25, 85.88) * mm});
            skCircle(sketch, "E3.5.9.0", {"center": v(35.75, 95.7) * mm, "radius": 2.5 * mm, "construction": true});
            skCircle(sketch, "E3.5.9.1", {"center": v(32.5, 101.32) * mm, "radius": 2.5 * mm, "construction": true});
            skPoint(sketch, "E3.5.9.2", {"position": v(33.75, 103.5) * mm});
            skPoint(sketch, "E3.5.9.3", {"position": v(37, 97.86) * mm});
            skLineSegment(sketch, "E3.5.9.4", {"start": v(35.75, 92.8) * mm, "end": v(33.25, 94.25) * mm});
            skLineSegment(sketch, "E3.5.9.5", {"start": v(38.25, 94.25) * mm, "end": v(35.75, 92.8) * mm});
            skLineSegment(sketch, "E3.5.9.6", {"start": v(38.25, 97.14) * mm, "end": v(38.25, 94.25) * mm});
            skLineSegment(sketch, "E3.5.9.7", {"start": v(35.75, 98.58) * mm, "end": v(38.25, 97.14) * mm});
            skLineSegment(sketch, "E3.5.9.8", {"start": v(30, 102.77) * mm, "end": v(32.5, 104.21) * mm});
            skLineSegment(sketch, "E3.5.9.9", {"start": v(30, 99.88) * mm, "end": v(30, 102.77) * mm});
            skLineSegment(sketch, "E3.5.9.10", {"start": v(32.5, 98.44) * mm, "end": v(30, 99.88) * mm});
            skLineSegment(sketch, "E3.5.9.11", {"start": v(35, 99.88) * mm, "end": v(32.5, 98.44) * mm});
            skLineSegment(sketch, "E3.5.9.12", {"start": v(35, 102.77) * mm, "end": v(35, 99.88) * mm});
            skLineSegment(sketch, "E3.5.9.13", {"start": v(32.5, 104.21) * mm, "end": v(35, 102.77) * mm});
            skLineSegment(sketch, "E3.5.9.14", {"start": v(33.25, 97.14) * mm, "end": v(35.75, 98.58) * mm});
            skLineSegment(sketch, "E3.5.9.15", {"start": v(33.25, 94.25) * mm, "end": v(33.25, 97.14) * mm});
            skCircle(sketch, "E3.6.0.0", {"center": v(42.25, -5.63) * mm, "radius": 2.5 * mm, "construction": true});
            skCircle(sketch, "E3.6.0.1", {"center": v(39, 0) * mm, "radius": 2.5 * mm, "construction": true});
            skPoint(sketch, "E3.6.0.2", {"position": v(40.25, 2.17) * mm});
            skPoint(sketch, "E3.6.0.3", {"position": v(43.5, -3.46) * mm});
            skLineSegment(sketch, "E3.6.0.4", {"start": v(42.25, -8.52) * mm, "end": v(39.75, -7.07) * mm});
            skLineSegment(sketch, "E3.6.0.5", {"start": v(44.75, -7.07) * mm, "end": v(42.25, -8.52) * mm});
            skLineSegment(sketch, "E3.6.0.6", {"start": v(44.75, -4.19) * mm, "end": v(44.75, -7.07) * mm});
            skLineSegment(sketch, "E3.6.0.7", {"start": v(42.25, -2.74) * mm, "end": v(44.75, -4.19) * mm});
            skLineSegment(sketch, "E3.6.0.8", {"start": v(36.5, 1.44) * mm, "end": v(39, 2.89) * mm});
            skLineSegment(sketch, "E3.6.0.9", {"start": v(36.5, -1.44) * mm, "end": v(36.5, 1.44) * mm});
            skLineSegment(sketch, "E3.6.0.10", {"start": v(39, -2.89) * mm, "end": v(36.5, -1.44) * mm});
            skLineSegment(sketch, "E3.6.0.11", {"start": v(41.5, -1.44) * mm, "end": v(39, -2.89) * mm});
            skLineSegment(sketch, "E3.6.0.12", {"start": v(41.5, 1.44) * mm, "end": v(41.5, -1.44) * mm});
            skLineSegment(sketch, "E3.6.0.13", {"start": v(39, 2.89) * mm, "end": v(41.5, 1.44) * mm});
            skLineSegment(sketch, "E3.6.0.14", {"start": v(39.75, -4.19) * mm, "end": v(42.25, -2.74) * mm});
            skLineSegment(sketch, "E3.6.0.15", {"start": v(39.75, -7.07) * mm, "end": v(39.75, -4.19) * mm});
            skCircle(sketch, "E3.6.1.0", {"center": v(42.25, 5.63) * mm, "radius": 2.5 * mm, "construction": true});
            skCircle(sketch, "E3.6.1.1", {"center": v(39, 11.26) * mm, "radius": 2.5 * mm, "construction": true});
            skPoint(sketch, "E3.6.1.2", {"position": v(40.25, 13.42) * mm});
            skPoint(sketch, "E3.6.1.3", {"position": v(43.5, 7.8) * mm});
            skLineSegment(sketch, "E3.6.1.4", {"start": v(42.25, 2.74) * mm, "end": v(39.75, 4.19) * mm});
            skLineSegment(sketch, "E3.6.1.5", {"start": v(44.75, 4.19) * mm, "end": v(42.25, 2.74) * mm});
            skLineSegment(sketch, "E3.6.1.6", {"start": v(44.75, 7.07) * mm, "end": v(44.75, 4.19) * mm});
            skLineSegment(sketch, "E3.6.1.7", {"start": v(42.25, 8.52) * mm, "end": v(44.75, 7.07) * mm});
            skLineSegment(sketch, "E3.6.1.8", {"start": v(36.5, 12.7) * mm, "end": v(39, 14.15) * mm});
            skLineSegment(sketch, "E3.6.1.9", {"start": v(36.5, 9.81) * mm, "end": v(36.5, 12.7) * mm});
            skLineSegment(sketch, "E3.6.1.10", {"start": v(39, 8.37) * mm, "end": v(36.5, 9.81) * mm});
            skLineSegment(sketch, "E3.6.1.11", {"start": v(41.5, 9.81) * mm, "end": v(39, 8.37) * mm});
            skLineSegment(sketch, "E3.6.1.12", {"start": v(41.5, 12.7) * mm, "end": v(41.5, 9.81) * mm});
            skLineSegment(sketch, "E3.6.1.13", {"start": v(39, 14.15) * mm, "end": v(41.5, 12.7) * mm});
            skLineSegment(sketch, "E3.6.1.14", {"start": v(39.75, 7.07) * mm, "end": v(42.25, 8.52) * mm});
            skLineSegment(sketch, "E3.6.1.15", {"start": v(39.75, 4.19) * mm, "end": v(39.75, 7.07) * mm});
            skCircle(sketch, "E3.6.2.0", {"center": v(42.25, 16.89) * mm, "radius": 2.5 * mm, "construction": true});
            skCircle(sketch, "E3.6.2.1", {"center": v(39, 22.52) * mm, "radius": 2.5 * mm, "construction": true});
            skPoint(sketch, "E3.6.2.2", {"position": v(40.25, 24.68) * mm});
            skPoint(sketch, "E3.6.2.3", {"position": v(43.5, 19.05) * mm});
            skLineSegment(sketch, "E3.6.2.4", {"start": v(42.25, 14) * mm, "end": v(39.75, 15.44) * mm});
            skLineSegment(sketch, "E3.6.2.5", {"start": v(44.75, 15.44) * mm, "end": v(42.25, 14) * mm});
            skLineSegment(sketch, "E3.6.2.6", {"start": v(44.75, 18.33) * mm, "end": v(44.75, 15.44) * mm});
            skLineSegment(sketch, "E3.6.2.7", {"start": v(42.25, 19.77) * mm, "end": v(44.75, 18.33) * mm});
            skLineSegment(sketch, "E3.6.2.8", {"start": v(36.5, 23.96) * mm, "end": v(39, 25.4) * mm});
            skLineSegment(sketch, "E3.6.2.9", {"start": v(36.5, 21.07) * mm, "end": v(36.5, 23.96) * mm});
            skLineSegment(sketch, "E3.6.2.10", {"start": v(39, 19.63) * mm, "end": v(36.5, 21.07) * mm});
            skLineSegment(sketch, "E3.6.2.11", {"start": v(41.5, 21.07) * mm, "end": v(39, 19.63) * mm});
            skLineSegment(sketch, "E3.6.2.12", {"start": v(41.5, 23.96) * mm, "end": v(41.5, 21.07) * mm});
            skLineSegment(sketch, "E3.6.2.13", {"start": v(39, 25.4) * mm, "end": v(41.5, 23.96) * mm});
            skLineSegment(sketch, "E3.6.2.14", {"start": v(39.75, 18.33) * mm, "end": v(42.25, 19.77) * mm});
            skLineSegment(sketch, "E3.6.2.15", {"start": v(39.75, 15.44) * mm, "end": v(39.75, 18.33) * mm});
            skCircle(sketch, "E3.6.3.0", {"center": v(42.25, 28.15) * mm, "radius": 2.5 * mm, "construction": true});
            skCircle(sketch, "E3.6.3.1", {"center": v(39, 33.77) * mm, "radius": 2.5 * mm, "construction": true});
            skPoint(sketch, "E3.6.3.2", {"position": v(40.25, 35.94) * mm});
            skPoint(sketch, "E3.6.3.3", {"position": v(43.5, 30.31) * mm});
            skLineSegment(sketch, "E3.6.3.4", {"start": v(42.25, 25.26) * mm, "end": v(39.75, 26.7) * mm});
            skLineSegment(sketch, "E3.6.3.5", {"start": v(44.75, 26.7) * mm, "end": v(42.25, 25.26) * mm});
            skLineSegment(sketch, "E3.6.3.6", {"start": v(44.75, 29.59) * mm, "end": v(44.75, 26.7) * mm});
            skLineSegment(sketch, "E3.6.3.7", {"start": v(42.25, 31.03) * mm, "end": v(44.75, 29.59) * mm});
            skLineSegment(sketch, "E3.6.3.8", {"start": v(36.5, 35.22) * mm, "end": v(39, 36.66) * mm});
            skLineSegment(sketch, "E3.6.3.9", {"start": v(36.5, 32.33) * mm, "end": v(36.5, 35.22) * mm});
            skLineSegment(sketch, "E3.6.3.10", {"start": v(39, 30.89) * mm, "end": v(36.5, 32.33) * mm});
            skLineSegment(sketch, "E3.6.3.11", {"start": v(41.5, 32.33) * mm, "end": v(39, 30.89) * mm});
            skLineSegment(sketch, "E3.6.3.12", {"start": v(41.5, 35.22) * mm, "end": v(41.5, 32.33) * mm});
            skLineSegment(sketch, "E3.6.3.13", {"start": v(39, 36.66) * mm, "end": v(41.5, 35.22) * mm});
            skLineSegment(sketch, "E3.6.3.14", {"start": v(39.75, 29.59) * mm, "end": v(42.25, 31.03) * mm});
            skLineSegment(sketch, "E3.6.3.15", {"start": v(39.75, 26.7) * mm, "end": v(39.75, 29.59) * mm});
            skCircle(sketch, "E3.6.4.0", {"center": v(42.25, 39.4) * mm, "radius": 2.5 * mm, "construction": true});
            skCircle(sketch, "E3.6.4.1", {"center": v(39, 45.03) * mm, "radius": 2.5 * mm, "construction": true});
            skPoint(sketch, "E3.6.4.2", {"position": v(40.25, 47.2) * mm});
            skPoint(sketch, "E3.6.4.3", {"position": v(43.5, 41.57) * mm});
            skLineSegment(sketch, "E3.6.4.4", {"start": v(42.25, 36.52) * mm, "end": v(39.75, 37.96) * mm});
            skLineSegment(sketch, "E3.6.4.5", {"start": v(44.75, 37.96) * mm, "end": v(42.25, 36.52) * mm});
            skLineSegment(sketch, "E3.6.4.6", {"start": v(44.75, 40.85) * mm, "end": v(44.75, 37.96) * mm});
            skLineSegment(sketch, "E3.6.4.7", {"start": v(42.25, 42.3) * mm, "end": v(44.75, 40.85) * mm});
            skLineSegment(sketch, "E3.6.4.8", {"start": v(36.5, 46.48) * mm, "end": v(39, 47.92) * mm});
            skLineSegment(sketch, "E3.6.4.9", {"start": v(36.5, 43.59) * mm, "end": v(36.5, 46.48) * mm});
            skLineSegment(sketch, "E3.6.4.10", {"start": v(39, 42.15) * mm, "end": v(36.5, 43.59) * mm});
            skLineSegment(sketch, "E3.6.4.11", {"start": v(41.5, 43.59) * mm, "end": v(39, 42.15) * mm});
            skLineSegment(sketch, "E3.6.4.12", {"start": v(41.5, 46.48) * mm, "end": v(41.5, 43.59) * mm});
            skLineSegment(sketch, "E3.6.4.13", {"start": v(39, 47.92) * mm, "end": v(41.5, 46.48) * mm});
            skLineSegment(sketch, "E3.6.4.14", {"start": v(39.75, 40.85) * mm, "end": v(42.25, 42.3) * mm});
            skLineSegment(sketch, "E3.6.4.15", {"start": v(39.75, 37.96) * mm, "end": v(39.75, 40.85) * mm});
            skCircle(sketch, "E3.6.5.0", {"center": v(42.25, 50.66) * mm, "radius": 2.5 * mm, "construction": true});
            skCircle(sketch, "E3.6.5.1", {"center": v(39, 56.3) * mm, "radius": 2.5 * mm, "construction": true});
            skPoint(sketch, "E3.6.5.2", {"position": v(40.25, 58.46) * mm});
            skPoint(sketch, "E3.6.5.3", {"position": v(43.5, 52.83) * mm});
            skLineSegment(sketch, "E3.6.5.4", {"start": v(42.25, 47.78) * mm, "end": v(39.75, 49.22) * mm});
            skLineSegment(sketch, "E3.6.5.5", {"start": v(44.75, 49.22) * mm, "end": v(42.25, 47.78) * mm});
            skLineSegment(sketch, "E3.6.5.6", {"start": v(44.75, 52.1) * mm, "end": v(44.75, 49.22) * mm});
            skLineSegment(sketch, "E3.6.5.7", {"start": v(42.25, 53.55) * mm, "end": v(44.75, 52.1) * mm});
            skLineSegment(sketch, "E3.6.5.8", {"start": v(36.5, 57.74) * mm, "end": v(39, 59.18) * mm});
            skLineSegment(sketch, "E3.6.5.9", {"start": v(36.5, 54.85) * mm, "end": v(36.5, 57.74) * mm});
            skLineSegment(sketch, "E3.6.5.10", {"start": v(39, 53.4) * mm, "end": v(36.5, 54.85) * mm});
            skLineSegment(sketch, "E3.6.5.11", {"start": v(41.5, 54.85) * mm, "end": v(39, 53.4) * mm});
            skLineSegment(sketch, "E3.6.5.12", {"start": v(41.5, 57.74) * mm, "end": v(41.5, 54.85) * mm});
            skLineSegment(sketch, "E3.6.5.13", {"start": v(39, 59.18) * mm, "end": v(41.5, 57.74) * mm});
            skLineSegment(sketch, "E3.6.5.14", {"start": v(39.75, 52.1) * mm, "end": v(42.25, 53.55) * mm});
            skLineSegment(sketch, "E3.6.5.15", {"start": v(39.75, 49.22) * mm, "end": v(39.75, 52.1) * mm});
            skCircle(sketch, "E3.6.6.0", {"center": v(42.25, 61.92) * mm, "radius": 2.5 * mm, "construction": true});
            skCircle(sketch, "E3.6.6.1", {"center": v(39, 67.55) * mm, "radius": 2.5 * mm, "construction": true});
            skPoint(sketch, "E3.6.6.2", {"position": v(40.25, 69.72) * mm});
            skPoint(sketch, "E3.6.6.3", {"position": v(43.5, 64.09) * mm});
            skLineSegment(sketch, "E3.6.6.4", {"start": v(42.25, 59.03) * mm, "end": v(39.75, 60.48) * mm});
            skLineSegment(sketch, "E3.6.6.5", {"start": v(44.75, 60.48) * mm, "end": v(42.25, 59.03) * mm});
            skLineSegment(sketch, "E3.6.6.6", {"start": v(44.75, 63.36) * mm, "end": v(44.75, 60.48) * mm});
            skLineSegment(sketch, "E3.6.6.7", {"start": v(42.25, 64.8) * mm, "end": v(44.75, 63.36) * mm});
            skLineSegment(sketch, "E3.6.6.8", {"start": v(36.5, 69) * mm, "end": v(39, 70.44) * mm});
            skLineSegment(sketch, "E3.6.6.9", {"start": v(36.5, 66.1) * mm, "end": v(36.5, 69) * mm});
            skLineSegment(sketch, "E3.6.6.10", {"start": v(39, 64.66) * mm, "end": v(36.5, 66.1) * mm});
            skLineSegment(sketch, "E3.6.6.11", {"start": v(41.5, 66.1) * mm, "end": v(39, 64.66) * mm});
            skLineSegment(sketch, "E3.6.6.12", {"start": v(41.5, 69) * mm, "end": v(41.5, 66.1) * mm});
            skLineSegment(sketch, "E3.6.6.13", {"start": v(39, 70.44) * mm, "end": v(41.5, 69) * mm});
            skLineSegment(sketch, "E3.6.6.14", {"start": v(39.75, 63.36) * mm, "end": v(42.25, 64.8) * mm});
            skLineSegment(sketch, "E3.6.6.15", {"start": v(39.75, 60.48) * mm, "end": v(39.75, 63.36) * mm});
            skCircle(sketch, "E3.6.7.0", {"center": v(42.25, 73.18) * mm, "radius": 2.5 * mm, "construction": true});
            skCircle(sketch, "E3.6.7.1", {"center": v(39, 78.8) * mm, "radius": 2.5 * mm, "construction": true});
            skPoint(sketch, "E3.6.7.2", {"position": v(40.25, 80.97) * mm});
            skPoint(sketch, "E3.6.7.3", {"position": v(43.5, 75.34) * mm});
            skLineSegment(sketch, "E3.6.7.4", {"start": v(42.25, 70.3) * mm, "end": v(39.75, 71.74) * mm});
            skLineSegment(sketch, "E3.6.7.5", {"start": v(44.75, 71.74) * mm, "end": v(42.25, 70.3) * mm});
            skLineSegment(sketch, "E3.6.7.6", {"start": v(44.75, 74.62) * mm, "end": v(44.75, 71.74) * mm});
            skLineSegment(sketch, "E3.6.7.7", {"start": v(42.25, 76.07) * mm, "end": v(44.75, 74.62) * mm});
            skLineSegment(sketch, "E3.6.7.8", {"start": v(36.5, 80.25) * mm, "end": v(39, 81.7) * mm});
            skLineSegment(sketch, "E3.6.7.9", {"start": v(36.5, 77.36) * mm, "end": v(36.5, 80.25) * mm});
            skLineSegment(sketch, "E3.6.7.10", {"start": v(39, 75.92) * mm, "end": v(36.5, 77.36) * mm});
            skLineSegment(sketch, "E3.6.7.11", {"start": v(41.5, 77.36) * mm, "end": v(39, 75.92) * mm});
            skLineSegment(sketch, "E3.6.7.12", {"start": v(41.5, 80.25) * mm, "end": v(41.5, 77.36) * mm});
            skLineSegment(sketch, "E3.6.7.13", {"start": v(39, 81.7) * mm, "end": v(41.5, 80.25) * mm});
            skLineSegment(sketch, "E3.6.7.14", {"start": v(39.75, 74.62) * mm, "end": v(42.25, 76.07) * mm});
            skLineSegment(sketch, "E3.6.7.15", {"start": v(39.75, 71.74) * mm, "end": v(39.75, 74.62) * mm});
            skCircle(sketch, "E3.6.8.0", {"center": v(42.25, 84.44) * mm, "radius": 2.5 * mm, "construction": true});
            skCircle(sketch, "E3.6.8.1", {"center": v(39, 90.07) * mm, "radius": 2.5 * mm, "construction": true});
            skPoint(sketch, "E3.6.8.2", {"position": v(40.25, 92.23) * mm});
            skPoint(sketch, "E3.6.8.3", {"position": v(43.5, 86.6) * mm});
            skLineSegment(sketch, "E3.6.8.4", {"start": v(42.25, 81.55) * mm, "end": v(39.75, 83) * mm});
            skLineSegment(sketch, "E3.6.8.5", {"start": v(44.75, 83) * mm, "end": v(42.25, 81.55) * mm});
            skLineSegment(sketch, "E3.6.8.6", {"start": v(44.75, 85.88) * mm, "end": v(44.75, 83) * mm});
            skLineSegment(sketch, "E3.6.8.7", {"start": v(42.25, 87.32) * mm, "end": v(44.75, 85.88) * mm});
            skLineSegment(sketch, "E3.6.8.8", {"start": v(36.5, 91.51) * mm, "end": v(39, 92.95) * mm});
            skLineSegment(sketch, "E3.6.8.9", {"start": v(36.5, 88.62) * mm, "end": v(36.5, 91.51) * mm});
            skLineSegment(sketch, "E3.6.8.10", {"start": v(39, 87.18) * mm, "end": v(36.5, 88.62) * mm});
            skLineSegment(sketch, "E3.6.8.11", {"start": v(41.5, 88.62) * mm, "end": v(39, 87.18) * mm});
            skLineSegment(sketch, "E3.6.8.12", {"start": v(41.5, 91.51) * mm, "end": v(41.5, 88.62) * mm});
            skLineSegment(sketch, "E3.6.8.13", {"start": v(39, 92.95) * mm, "end": v(41.5, 91.51) * mm});
            skLineSegment(sketch, "E3.6.8.14", {"start": v(39.75, 85.88) * mm, "end": v(42.25, 87.32) * mm});
            skLineSegment(sketch, "E3.6.8.15", {"start": v(39.75, 83) * mm, "end": v(39.75, 85.88) * mm});
            skCircle(sketch, "E3.6.9.0", {"center": v(42.25, 95.7) * mm, "radius": 2.5 * mm, "construction": true});
            skCircle(sketch, "E3.6.9.1", {"center": v(39, 101.32) * mm, "radius": 2.5 * mm, "construction": true});
            skPoint(sketch, "E3.6.9.2", {"position": v(40.25, 103.5) * mm});
            skPoint(sketch, "E3.6.9.3", {"position": v(43.5, 97.86) * mm});
            skLineSegment(sketch, "E3.6.9.4", {"start": v(42.25, 92.8) * mm, "end": v(39.75, 94.25) * mm});
            skLineSegment(sketch, "E3.6.9.5", {"start": v(44.75, 94.25) * mm, "end": v(42.25, 92.8) * mm});
            skLineSegment(sketch, "E3.6.9.6", {"start": v(44.75, 97.14) * mm, "end": v(44.75, 94.25) * mm});
            skLineSegment(sketch, "E3.6.9.7", {"start": v(42.25, 98.58) * mm, "end": v(44.75, 97.14) * mm});
            skLineSegment(sketch, "E3.6.9.8", {"start": v(36.5, 102.77) * mm, "end": v(39, 104.21) * mm});
            skLineSegment(sketch, "E3.6.9.9", {"start": v(36.5, 99.88) * mm, "end": v(36.5, 102.77) * mm});
            skLineSegment(sketch, "E3.6.9.10", {"start": v(39, 98.44) * mm, "end": v(36.5, 99.88) * mm});
            skLineSegment(sketch, "E3.6.9.11", {"start": v(41.5, 99.88) * mm, "end": v(39, 98.44) * mm});
            skLineSegment(sketch, "E3.6.9.12", {"start": v(41.5, 102.77) * mm, "end": v(41.5, 99.88) * mm});
            skLineSegment(sketch, "E3.6.9.13", {"start": v(39, 104.21) * mm, "end": v(41.5, 102.77) * mm});
            skLineSegment(sketch, "E3.6.9.14", {"start": v(39.75, 97.14) * mm, "end": v(42.25, 98.58) * mm});
            skLineSegment(sketch, "E3.6.9.15", {"start": v(39.75, 94.25) * mm, "end": v(39.75, 97.14) * mm});
            skCircle(sketch, "E3.7.0.0", {"center": v(48.75, -5.63) * mm, "radius": 2.5 * mm, "construction": true});
            skCircle(sketch, "E3.7.0.1", {"center": v(45.5, 0) * mm, "radius": 2.5 * mm, "construction": true});
            skPoint(sketch, "E3.7.0.2", {"position": v(46.75, 2.17) * mm});
            skPoint(sketch, "E3.7.0.3", {"position": v(50, -3.46) * mm});
            skLineSegment(sketch, "E3.7.0.4", {"start": v(48.75, -8.52) * mm, "end": v(46.25, -7.07) * mm});
            skLineSegment(sketch, "E3.7.0.5", {"start": v(51.25, -7.07) * mm, "end": v(48.75, -8.52) * mm});
            skLineSegment(sketch, "E3.7.0.6", {"start": v(51.25, -4.19) * mm, "end": v(51.25, -7.07) * mm});
            skLineSegment(sketch, "E3.7.0.7", {"start": v(48.75, -2.74) * mm, "end": v(51.25, -4.19) * mm});
            skLineSegment(sketch, "E3.7.0.8", {"start": v(43, 1.44) * mm, "end": v(45.5, 2.89) * mm});
            skLineSegment(sketch, "E3.7.0.9", {"start": v(43, -1.44) * mm, "end": v(43, 1.44) * mm});
            skLineSegment(sketch, "E3.7.0.10", {"start": v(45.5, -2.89) * mm, "end": v(43, -1.44) * mm});
            skLineSegment(sketch, "E3.7.0.11", {"start": v(48, -1.44) * mm, "end": v(45.5, -2.89) * mm});
            skLineSegment(sketch, "E3.7.0.12", {"start": v(48, 1.44) * mm, "end": v(48, -1.44) * mm});
            skLineSegment(sketch, "E3.7.0.13", {"start": v(45.5, 2.89) * mm, "end": v(48, 1.44) * mm});
            skLineSegment(sketch, "E3.7.0.14", {"start": v(46.25, -4.19) * mm, "end": v(48.75, -2.74) * mm});
            skLineSegment(sketch, "E3.7.0.15", {"start": v(46.25, -7.07) * mm, "end": v(46.25, -4.19) * mm});
            skCircle(sketch, "E3.7.1.0", {"center": v(48.75, 5.63) * mm, "radius": 2.5 * mm, "construction": true});
            skCircle(sketch, "E3.7.1.1", {"center": v(45.5, 11.26) * mm, "radius": 2.5 * mm, "construction": true});
            skPoint(sketch, "E3.7.1.2", {"position": v(46.75, 13.42) * mm});
            skPoint(sketch, "E3.7.1.3", {"position": v(50, 7.8) * mm});
            skLineSegment(sketch, "E3.7.1.4", {"start": v(48.75, 2.74) * mm, "end": v(46.25, 4.19) * mm});
            skLineSegment(sketch, "E3.7.1.5", {"start": v(51.25, 4.19) * mm, "end": v(48.75, 2.74) * mm});
            skLineSegment(sketch, "E3.7.1.6", {"start": v(51.25, 7.07) * mm, "end": v(51.25, 4.19) * mm});
            skLineSegment(sketch, "E3.7.1.7", {"start": v(48.75, 8.52) * mm, "end": v(51.25, 7.07) * mm});
            skLineSegment(sketch, "E3.7.1.8", {"start": v(43, 12.7) * mm, "end": v(45.5, 14.15) * mm});
            skLineSegment(sketch, "E3.7.1.9", {"start": v(43, 9.81) * mm, "end": v(43, 12.7) * mm});
            skLineSegment(sketch, "E3.7.1.10", {"start": v(45.5, 8.37) * mm, "end": v(43, 9.81) * mm});
            skLineSegment(sketch, "E3.7.1.11", {"start": v(48, 9.81) * mm, "end": v(45.5, 8.37) * mm});
            skLineSegment(sketch, "E3.7.1.12", {"start": v(48, 12.7) * mm, "end": v(48, 9.81) * mm});
            skLineSegment(sketch, "E3.7.1.13", {"start": v(45.5, 14.15) * mm, "end": v(48, 12.7) * mm});
            skLineSegment(sketch, "E3.7.1.14", {"start": v(46.25, 7.07) * mm, "end": v(48.75, 8.52) * mm});
            skLineSegment(sketch, "E3.7.1.15", {"start": v(46.25, 4.19) * mm, "end": v(46.25, 7.07) * mm});
            skCircle(sketch, "E3.7.2.0", {"center": v(48.75, 16.89) * mm, "radius": 2.5 * mm, "construction": true});
            skCircle(sketch, "E3.7.2.1", {"center": v(45.5, 22.52) * mm, "radius": 2.5 * mm, "construction": true});
            skPoint(sketch, "E3.7.2.2", {"position": v(46.75, 24.68) * mm});
            skPoint(sketch, "E3.7.2.3", {"position": v(50, 19.05) * mm});
            skLineSegment(sketch, "E3.7.2.4", {"start": v(48.75, 14) * mm, "end": v(46.25, 15.44) * mm});
            skLineSegment(sketch, "E3.7.2.5", {"start": v(51.25, 15.44) * mm, "end": v(48.75, 14) * mm});
            skLineSegment(sketch, "E3.7.2.6", {"start": v(51.25, 18.33) * mm, "end": v(51.25, 15.44) * mm});
            skLineSegment(sketch, "E3.7.2.7", {"start": v(48.75, 19.77) * mm, "end": v(51.25, 18.33) * mm});
            skLineSegment(sketch, "E3.7.2.8", {"start": v(43, 23.96) * mm, "end": v(45.5, 25.4) * mm});
            skLineSegment(sketch, "E3.7.2.9", {"start": v(43, 21.07) * mm, "end": v(43, 23.96) * mm});
            skLineSegment(sketch, "E3.7.2.10", {"start": v(45.5, 19.63) * mm, "end": v(43, 21.07) * mm});
            skLineSegment(sketch, "E3.7.2.11", {"start": v(48, 21.07) * mm, "end": v(45.5, 19.63) * mm});
            skLineSegment(sketch, "E3.7.2.12", {"start": v(48, 23.96) * mm, "end": v(48, 21.07) * mm});
            skLineSegment(sketch, "E3.7.2.13", {"start": v(45.5, 25.4) * mm, "end": v(48, 23.96) * mm});
            skLineSegment(sketch, "E3.7.2.14", {"start": v(46.25, 18.33) * mm, "end": v(48.75, 19.77) * mm});
            skLineSegment(sketch, "E3.7.2.15", {"start": v(46.25, 15.44) * mm, "end": v(46.25, 18.33) * mm});
            skCircle(sketch, "E3.7.3.0", {"center": v(48.75, 28.15) * mm, "radius": 2.5 * mm, "construction": true});
            skCircle(sketch, "E3.7.3.1", {"center": v(45.5, 33.77) * mm, "radius": 2.5 * mm, "construction": true});
            skPoint(sketch, "E3.7.3.2", {"position": v(46.75, 35.94) * mm});
            skPoint(sketch, "E3.7.3.3", {"position": v(50, 30.31) * mm});
            skLineSegment(sketch, "E3.7.3.4", {"start": v(48.75, 25.26) * mm, "end": v(46.25, 26.7) * mm});
            skLineSegment(sketch, "E3.7.3.5", {"start": v(51.25, 26.7) * mm, "end": v(48.75, 25.26) * mm});
            skLineSegment(sketch, "E3.7.3.6", {"start": v(51.25, 29.59) * mm, "end": v(51.25, 26.7) * mm});
            skLineSegment(sketch, "E3.7.3.7", {"start": v(48.75, 31.03) * mm, "end": v(51.25, 29.59) * mm});
            skLineSegment(sketch, "E3.7.3.8", {"start": v(43, 35.22) * mm, "end": v(45.5, 36.66) * mm});
            skLineSegment(sketch, "E3.7.3.9", {"start": v(43, 32.33) * mm, "end": v(43, 35.22) * mm});
            skLineSegment(sketch, "E3.7.3.10", {"start": v(45.5, 30.89) * mm, "end": v(43, 32.33) * mm});
            skLineSegment(sketch, "E3.7.3.11", {"start": v(48, 32.33) * mm, "end": v(45.5, 30.89) * mm});
            skLineSegment(sketch, "E3.7.3.12", {"start": v(48, 35.22) * mm, "end": v(48, 32.33) * mm});
            skLineSegment(sketch, "E3.7.3.13", {"start": v(45.5, 36.66) * mm, "end": v(48, 35.22) * mm});
            skLineSegment(sketch, "E3.7.3.14", {"start": v(46.25, 29.59) * mm, "end": v(48.75, 31.03) * mm});
            skLineSegment(sketch, "E3.7.3.15", {"start": v(46.25, 26.7) * mm, "end": v(46.25, 29.59) * mm});
            skCircle(sketch, "E3.7.4.0", {"center": v(48.75, 39.4) * mm, "radius": 2.5 * mm, "construction": true});
            skCircle(sketch, "E3.7.4.1", {"center": v(45.5, 45.03) * mm, "radius": 2.5 * mm, "construction": true});
            skPoint(sketch, "E3.7.4.2", {"position": v(46.75, 47.2) * mm});
            skPoint(sketch, "E3.7.4.3", {"position": v(50, 41.57) * mm});
            skLineSegment(sketch, "E3.7.4.4", {"start": v(48.75, 36.52) * mm, "end": v(46.25, 37.96) * mm});
            skLineSegment(sketch, "E3.7.4.5", {"start": v(51.25, 37.96) * mm, "end": v(48.75, 36.52) * mm});
            skLineSegment(sketch, "E3.7.4.6", {"start": v(51.25, 40.85) * mm, "end": v(51.25, 37.96) * mm});
            skLineSegment(sketch, "E3.7.4.7", {"start": v(48.75, 42.3) * mm, "end": v(51.25, 40.85) * mm});
            skLineSegment(sketch, "E3.7.4.8", {"start": v(43, 46.48) * mm, "end": v(45.5, 47.92) * mm});
            skLineSegment(sketch, "E3.7.4.9", {"start": v(43, 43.59) * mm, "end": v(43, 46.48) * mm});
            skLineSegment(sketch, "E3.7.4.10", {"start": v(45.5, 42.15) * mm, "end": v(43, 43.59) * mm});
            skLineSegment(sketch, "E3.7.4.11", {"start": v(48, 43.59) * mm, "end": v(45.5, 42.15) * mm});
            skLineSegment(sketch, "E3.7.4.12", {"start": v(48, 46.48) * mm, "end": v(48, 43.59) * mm});
            skLineSegment(sketch, "E3.7.4.13", {"start": v(45.5, 47.92) * mm, "end": v(48, 46.48) * mm});
            skLineSegment(sketch, "E3.7.4.14", {"start": v(46.25, 40.85) * mm, "end": v(48.75, 42.3) * mm});
            skLineSegment(sketch, "E3.7.4.15", {"start": v(46.25, 37.96) * mm, "end": v(46.25, 40.85) * mm});
            skCircle(sketch, "E3.7.5.0", {"center": v(48.75, 50.66) * mm, "radius": 2.5 * mm, "construction": true});
            skCircle(sketch, "E3.7.5.1", {"center": v(45.5, 56.3) * mm, "radius": 2.5 * mm, "construction": true});
            skPoint(sketch, "E3.7.5.2", {"position": v(46.75, 58.46) * mm});
            skPoint(sketch, "E3.7.5.3", {"position": v(50, 52.83) * mm});
            skLineSegment(sketch, "E3.7.5.4", {"start": v(48.75, 47.78) * mm, "end": v(46.25, 49.22) * mm});
            skLineSegment(sketch, "E3.7.5.5", {"start": v(51.25, 49.22) * mm, "end": v(48.75, 47.78) * mm});
            skLineSegment(sketch, "E3.7.5.6", {"start": v(51.25, 52.1) * mm, "end": v(51.25, 49.22) * mm});
            skLineSegment(sketch, "E3.7.5.7", {"start": v(48.75, 53.55) * mm, "end": v(51.25, 52.1) * mm});
            skLineSegment(sketch, "E3.7.5.8", {"start": v(43, 57.74) * mm, "end": v(45.5, 59.18) * mm});
            skLineSegment(sketch, "E3.7.5.9", {"start": v(43, 54.85) * mm, "end": v(43, 57.74) * mm});
            skLineSegment(sketch, "E3.7.5.10", {"start": v(45.5, 53.4) * mm, "end": v(43, 54.85) * mm});
            skLineSegment(sketch, "E3.7.5.11", {"start": v(48, 54.85) * mm, "end": v(45.5, 53.4) * mm});
            skLineSegment(sketch, "E3.7.5.12", {"start": v(48, 57.74) * mm, "end": v(48, 54.85) * mm});
            skLineSegment(sketch, "E3.7.5.13", {"start": v(45.5, 59.18) * mm, "end": v(48, 57.74) * mm});
            skLineSegment(sketch, "E3.7.5.14", {"start": v(46.25, 52.1) * mm, "end": v(48.75, 53.55) * mm});
            skLineSegment(sketch, "E3.7.5.15", {"start": v(46.25, 49.22) * mm, "end": v(46.25, 52.1) * mm});
            skCircle(sketch, "E3.7.6.0", {"center": v(48.75, 61.92) * mm, "radius": 2.5 * mm, "construction": true});
            skCircle(sketch, "E3.7.6.1", {"center": v(45.5, 67.55) * mm, "radius": 2.5 * mm, "construction": true});
            skPoint(sketch, "E3.7.6.2", {"position": v(46.75, 69.72) * mm});
            skPoint(sketch, "E3.7.6.3", {"position": v(50, 64.09) * mm});
            skLineSegment(sketch, "E3.7.6.4", {"start": v(48.75, 59.03) * mm, "end": v(46.25, 60.48) * mm});
            skLineSegment(sketch, "E3.7.6.5", {"start": v(51.25, 60.48) * mm, "end": v(48.75, 59.03) * mm});
            skLineSegment(sketch, "E3.7.6.6", {"start": v(51.25, 63.36) * mm, "end": v(51.25, 60.48) * mm});
            skLineSegment(sketch, "E3.7.6.7", {"start": v(48.75, 64.8) * mm, "end": v(51.25, 63.36) * mm});
            skLineSegment(sketch, "E3.7.6.8", {"start": v(43, 69) * mm, "end": v(45.5, 70.44) * mm});
            skLineSegment(sketch, "E3.7.6.9", {"start": v(43, 66.1) * mm, "end": v(43, 69) * mm});
            skLineSegment(sketch, "E3.7.6.10", {"start": v(45.5, 64.66) * mm, "end": v(43, 66.1) * mm});
            skLineSegment(sketch, "E3.7.6.11", {"start": v(48, 66.1) * mm, "end": v(45.5, 64.66) * mm});
            skLineSegment(sketch, "E3.7.6.12", {"start": v(48, 69) * mm, "end": v(48, 66.1) * mm});
            skLineSegment(sketch, "E3.7.6.13", {"start": v(45.5, 70.44) * mm, "end": v(48, 69) * mm});
            skLineSegment(sketch, "E3.7.6.14", {"start": v(46.25, 63.36) * mm, "end": v(48.75, 64.8) * mm});
            skLineSegment(sketch, "E3.7.6.15", {"start": v(46.25, 60.48) * mm, "end": v(46.25, 63.36) * mm});
            skCircle(sketch, "E3.7.7.0", {"center": v(48.75, 73.18) * mm, "radius": 2.5 * mm, "construction": true});
            skCircle(sketch, "E3.7.7.1", {"center": v(45.5, 78.8) * mm, "radius": 2.5 * mm, "construction": true});
            skPoint(sketch, "E3.7.7.2", {"position": v(46.75, 80.97) * mm});
            skPoint(sketch, "E3.7.7.3", {"position": v(50, 75.34) * mm});
            skLineSegment(sketch, "E3.7.7.4", {"start": v(48.75, 70.3) * mm, "end": v(46.25, 71.74) * mm});
            skLineSegment(sketch, "E3.7.7.5", {"start": v(51.25, 71.74) * mm, "end": v(48.75, 70.3) * mm});
            skLineSegment(sketch, "E3.7.7.6", {"start": v(51.25, 74.62) * mm, "end": v(51.25, 71.74) * mm});
            skLineSegment(sketch, "E3.7.7.7", {"start": v(48.75, 76.07) * mm, "end": v(51.25, 74.62) * mm});
            skLineSegment(sketch, "E3.7.7.8", {"start": v(43, 80.25) * mm, "end": v(45.5, 81.7) * mm});
            skLineSegment(sketch, "E3.7.7.9", {"start": v(43, 77.36) * mm, "end": v(43, 80.25) * mm});
            skLineSegment(sketch, "E3.7.7.10", {"start": v(45.5, 75.92) * mm, "end": v(43, 77.36) * mm});
            skLineSegment(sketch, "E3.7.7.11", {"start": v(48, 77.36) * mm, "end": v(45.5, 75.92) * mm});
            skLineSegment(sketch, "E3.7.7.12", {"start": v(48, 80.25) * mm, "end": v(48, 77.36) * mm});
            skLineSegment(sketch, "E3.7.7.13", {"start": v(45.5, 81.7) * mm, "end": v(48, 80.25) * mm});
            skLineSegment(sketch, "E3.7.7.14", {"start": v(46.25, 74.62) * mm, "end": v(48.75, 76.07) * mm});
            skLineSegment(sketch, "E3.7.7.15", {"start": v(46.25, 71.74) * mm, "end": v(46.25, 74.62) * mm});
            skCircle(sketch, "E3.7.8.0", {"center": v(48.75, 84.44) * mm, "radius": 2.5 * mm, "construction": true});
            skCircle(sketch, "E3.7.8.1", {"center": v(45.5, 90.07) * mm, "radius": 2.5 * mm, "construction": true});
            skPoint(sketch, "E3.7.8.2", {"position": v(46.75, 92.23) * mm});
            skPoint(sketch, "E3.7.8.3", {"position": v(50, 86.6) * mm});
            skLineSegment(sketch, "E3.7.8.4", {"start": v(48.75, 81.55) * mm, "end": v(46.25, 83) * mm});
            skLineSegment(sketch, "E3.7.8.5", {"start": v(51.25, 83) * mm, "end": v(48.75, 81.55) * mm});
            skLineSegment(sketch, "E3.7.8.6", {"start": v(51.25, 85.88) * mm, "end": v(51.25, 83) * mm});
            skLineSegment(sketch, "E3.7.8.7", {"start": v(48.75, 87.32) * mm, "end": v(51.25, 85.88) * mm});
            skLineSegment(sketch, "E3.7.8.8", {"start": v(43, 91.51) * mm, "end": v(45.5, 92.95) * mm});
            skLineSegment(sketch, "E3.7.8.9", {"start": v(43, 88.62) * mm, "end": v(43, 91.51) * mm});
            skLineSegment(sketch, "E3.7.8.10", {"start": v(45.5, 87.18) * mm, "end": v(43, 88.62) * mm});
            skLineSegment(sketch, "E3.7.8.11", {"start": v(48, 88.62) * mm, "end": v(45.5, 87.18) * mm});
            skLineSegment(sketch, "E3.7.8.12", {"start": v(48, 91.51) * mm, "end": v(48, 88.62) * mm});
            skLineSegment(sketch, "E3.7.8.13", {"start": v(45.5, 92.95) * mm, "end": v(48, 91.51) * mm});
            skLineSegment(sketch, "E3.7.8.14", {"start": v(46.25, 85.88) * mm, "end": v(48.75, 87.32) * mm});
            skLineSegment(sketch, "E3.7.8.15", {"start": v(46.25, 83) * mm, "end": v(46.25, 85.88) * mm});
            skCircle(sketch, "E3.7.9.0", {"center": v(48.75, 95.7) * mm, "radius": 2.5 * mm, "construction": true});
            skCircle(sketch, "E3.7.9.1", {"center": v(45.5, 101.32) * mm, "radius": 2.5 * mm, "construction": true});
            skPoint(sketch, "E3.7.9.2", {"position": v(46.75, 103.5) * mm});
            skPoint(sketch, "E3.7.9.3", {"position": v(50, 97.86) * mm});
            skLineSegment(sketch, "E3.7.9.4", {"start": v(48.75, 92.8) * mm, "end": v(46.25, 94.25) * mm});
            skLineSegment(sketch, "E3.7.9.5", {"start": v(51.25, 94.25) * mm, "end": v(48.75, 92.8) * mm});
            skLineSegment(sketch, "E3.7.9.6", {"start": v(51.25, 97.14) * mm, "end": v(51.25, 94.25) * mm});
            skLineSegment(sketch, "E3.7.9.7", {"start": v(48.75, 98.58) * mm, "end": v(51.25, 97.14) * mm});
            skLineSegment(sketch, "E3.7.9.8", {"start": v(43, 102.77) * mm, "end": v(45.5, 104.21) * mm});
            skLineSegment(sketch, "E3.7.9.9", {"start": v(43, 99.88) * mm, "end": v(43, 102.77) * mm});
            skLineSegment(sketch, "E3.7.9.10", {"start": v(45.5, 98.44) * mm, "end": v(43, 99.88) * mm});
            skLineSegment(sketch, "E3.7.9.11", {"start": v(48, 99.88) * mm, "end": v(45.5, 98.44) * mm});
            skLineSegment(sketch, "E3.7.9.12", {"start": v(48, 102.77) * mm, "end": v(48, 99.88) * mm});
            skLineSegment(sketch, "E3.7.9.13", {"start": v(45.5, 104.21) * mm, "end": v(48, 102.77) * mm});
            skLineSegment(sketch, "E3.7.9.14", {"start": v(46.25, 97.14) * mm, "end": v(48.75, 98.58) * mm});
            skLineSegment(sketch, "E3.7.9.15", {"start": v(46.25, 94.25) * mm, "end": v(46.25, 97.14) * mm});
            skCircle(sketch, "E3.8.0.0", {"center": v(55.25, -5.63) * mm, "radius": 2.5 * mm, "construction": true});
            skCircle(sketch, "E3.8.0.1", {"center": v(52, 0) * mm, "radius": 2.5 * mm, "construction": true});
            skPoint(sketch, "E3.8.0.2", {"position": v(53.25, 2.17) * mm});
            skPoint(sketch, "E3.8.0.3", {"position": v(56.5, -3.46) * mm});
            skLineSegment(sketch, "E3.8.0.4", {"start": v(55.25, -8.52) * mm, "end": v(52.75, -7.07) * mm});
            skLineSegment(sketch, "E3.8.0.5", {"start": v(57.75, -7.07) * mm, "end": v(55.25, -8.52) * mm});
            skLineSegment(sketch, "E3.8.0.6", {"start": v(57.75, -4.19) * mm, "end": v(57.75, -7.07) * mm});
            skLineSegment(sketch, "E3.8.0.7", {"start": v(55.25, -2.74) * mm, "end": v(57.75, -4.19) * mm});
            skLineSegment(sketch, "E3.8.0.8", {"start": v(49.5, 1.44) * mm, "end": v(52, 2.89) * mm});
            skLineSegment(sketch, "E3.8.0.9", {"start": v(49.5, -1.44) * mm, "end": v(49.5, 1.44) * mm});
            skLineSegment(sketch, "E3.8.0.10", {"start": v(52, -2.89) * mm, "end": v(49.5, -1.44) * mm});
            skLineSegment(sketch, "E3.8.0.11", {"start": v(54.5, -1.44) * mm, "end": v(52, -2.89) * mm});
            skLineSegment(sketch, "E3.8.0.12", {"start": v(54.5, 1.44) * mm, "end": v(54.5, -1.44) * mm});
            skLineSegment(sketch, "E3.8.0.13", {"start": v(52, 2.89) * mm, "end": v(54.5, 1.44) * mm});
            skLineSegment(sketch, "E3.8.0.14", {"start": v(52.75, -4.19) * mm, "end": v(55.25, -2.74) * mm});
            skLineSegment(sketch, "E3.8.0.15", {"start": v(52.75, -7.07) * mm, "end": v(52.75, -4.19) * mm});
            skCircle(sketch, "E3.8.1.0", {"center": v(55.25, 5.63) * mm, "radius": 2.5 * mm, "construction": true});
            skCircle(sketch, "E3.8.1.1", {"center": v(52, 11.26) * mm, "radius": 2.5 * mm, "construction": true});
            skPoint(sketch, "E3.8.1.2", {"position": v(53.25, 13.42) * mm});
            skPoint(sketch, "E3.8.1.3", {"position": v(56.5, 7.8) * mm});
            skLineSegment(sketch, "E3.8.1.4", {"start": v(55.25, 2.74) * mm, "end": v(52.75, 4.19) * mm});
            skLineSegment(sketch, "E3.8.1.5", {"start": v(57.75, 4.19) * mm, "end": v(55.25, 2.74) * mm});
            skLineSegment(sketch, "E3.8.1.6", {"start": v(57.75, 7.07) * mm, "end": v(57.75, 4.19) * mm});
            skLineSegment(sketch, "E3.8.1.7", {"start": v(55.25, 8.52) * mm, "end": v(57.75, 7.07) * mm});
            skLineSegment(sketch, "E3.8.1.8", {"start": v(49.5, 12.7) * mm, "end": v(52, 14.15) * mm});
            skLineSegment(sketch, "E3.8.1.9", {"start": v(49.5, 9.81) * mm, "end": v(49.5, 12.7) * mm});
            skLineSegment(sketch, "E3.8.1.10", {"start": v(52, 8.37) * mm, "end": v(49.5, 9.81) * mm});
            skLineSegment(sketch, "E3.8.1.11", {"start": v(54.5, 9.81) * mm, "end": v(52, 8.37) * mm});
            skLineSegment(sketch, "E3.8.1.12", {"start": v(54.5, 12.7) * mm, "end": v(54.5, 9.81) * mm});
            skLineSegment(sketch, "E3.8.1.13", {"start": v(52, 14.15) * mm, "end": v(54.5, 12.7) * mm});
            skLineSegment(sketch, "E3.8.1.14", {"start": v(52.75, 7.07) * mm, "end": v(55.25, 8.52) * mm});
            skLineSegment(sketch, "E3.8.1.15", {"start": v(52.75, 4.19) * mm, "end": v(52.75, 7.07) * mm});
            skCircle(sketch, "E3.8.2.0", {"center": v(55.25, 16.89) * mm, "radius": 2.5 * mm, "construction": true});
            skCircle(sketch, "E3.8.2.1", {"center": v(52, 22.52) * mm, "radius": 2.5 * mm, "construction": true});
            skPoint(sketch, "E3.8.2.2", {"position": v(53.25, 24.68) * mm});
            skPoint(sketch, "E3.8.2.3", {"position": v(56.5, 19.05) * mm});
            skLineSegment(sketch, "E3.8.2.4", {"start": v(55.25, 14) * mm, "end": v(52.75, 15.44) * mm});
            skLineSegment(sketch, "E3.8.2.5", {"start": v(57.75, 15.44) * mm, "end": v(55.25, 14) * mm});
            skLineSegment(sketch, "E3.8.2.6", {"start": v(57.75, 18.33) * mm, "end": v(57.75, 15.44) * mm});
            skLineSegment(sketch, "E3.8.2.7", {"start": v(55.25, 19.77) * mm, "end": v(57.75, 18.33) * mm});
            skLineSegment(sketch, "E3.8.2.8", {"start": v(49.5, 23.96) * mm, "end": v(52, 25.4) * mm});
            skLineSegment(sketch, "E3.8.2.9", {"start": v(49.5, 21.07) * mm, "end": v(49.5, 23.96) * mm});
            skLineSegment(sketch, "E3.8.2.10", {"start": v(52, 19.63) * mm, "end": v(49.5, 21.07) * mm});
            skLineSegment(sketch, "E3.8.2.11", {"start": v(54.5, 21.07) * mm, "end": v(52, 19.63) * mm});
            skLineSegment(sketch, "E3.8.2.12", {"start": v(54.5, 23.96) * mm, "end": v(54.5, 21.07) * mm});
            skLineSegment(sketch, "E3.8.2.13", {"start": v(52, 25.4) * mm, "end": v(54.5, 23.96) * mm});
            skLineSegment(sketch, "E3.8.2.14", {"start": v(52.75, 18.33) * mm, "end": v(55.25, 19.77) * mm});
            skLineSegment(sketch, "E3.8.2.15", {"start": v(52.75, 15.44) * mm, "end": v(52.75, 18.33) * mm});
            skCircle(sketch, "E3.8.3.0", {"center": v(55.25, 28.15) * mm, "radius": 2.5 * mm, "construction": true});
            skCircle(sketch, "E3.8.3.1", {"center": v(52, 33.77) * mm, "radius": 2.5 * mm, "construction": true});
            skPoint(sketch, "E3.8.3.2", {"position": v(53.25, 35.94) * mm});
            skPoint(sketch, "E3.8.3.3", {"position": v(56.5, 30.31) * mm});
            skLineSegment(sketch, "E3.8.3.4", {"start": v(55.25, 25.26) * mm, "end": v(52.75, 26.7) * mm});
            skLineSegment(sketch, "E3.8.3.5", {"start": v(57.75, 26.7) * mm, "end": v(55.25, 25.26) * mm});
            skLineSegment(sketch, "E3.8.3.6", {"start": v(57.75, 29.59) * mm, "end": v(57.75, 26.7) * mm});
            skLineSegment(sketch, "E3.8.3.7", {"start": v(55.25, 31.03) * mm, "end": v(57.75, 29.59) * mm});
            skLineSegment(sketch, "E3.8.3.8", {"start": v(49.5, 35.22) * mm, "end": v(52, 36.66) * mm});
            skLineSegment(sketch, "E3.8.3.9", {"start": v(49.5, 32.33) * mm, "end": v(49.5, 35.22) * mm});
            skLineSegment(sketch, "E3.8.3.10", {"start": v(52, 30.89) * mm, "end": v(49.5, 32.33) * mm});
            skLineSegment(sketch, "E3.8.3.11", {"start": v(54.5, 32.33) * mm, "end": v(52, 30.89) * mm});
            skLineSegment(sketch, "E3.8.3.12", {"start": v(54.5, 35.22) * mm, "end": v(54.5, 32.33) * mm});
            skLineSegment(sketch, "E3.8.3.13", {"start": v(52, 36.66) * mm, "end": v(54.5, 35.22) * mm});
            skLineSegment(sketch, "E3.8.3.14", {"start": v(52.75, 29.59) * mm, "end": v(55.25, 31.03) * mm});
            skLineSegment(sketch, "E3.8.3.15", {"start": v(52.75, 26.7) * mm, "end": v(52.75, 29.59) * mm});
            skCircle(sketch, "E3.8.4.0", {"center": v(55.25, 39.4) * mm, "radius": 2.5 * mm, "construction": true});
            skCircle(sketch, "E3.8.4.1", {"center": v(52, 45.03) * mm, "radius": 2.5 * mm, "construction": true});
            skPoint(sketch, "E3.8.4.2", {"position": v(53.25, 47.2) * mm});
            skPoint(sketch, "E3.8.4.3", {"position": v(56.5, 41.57) * mm});
            skLineSegment(sketch, "E3.8.4.4", {"start": v(55.25, 36.52) * mm, "end": v(52.75, 37.96) * mm});
            skLineSegment(sketch, "E3.8.4.5", {"start": v(57.75, 37.96) * mm, "end": v(55.25, 36.52) * mm});
            skLineSegment(sketch, "E3.8.4.6", {"start": v(57.75, 40.85) * mm, "end": v(57.75, 37.96) * mm});
            skLineSegment(sketch, "E3.8.4.7", {"start": v(55.25, 42.3) * mm, "end": v(57.75, 40.85) * mm});
            skLineSegment(sketch, "E3.8.4.8", {"start": v(49.5, 46.48) * mm, "end": v(52, 47.92) * mm});
            skLineSegment(sketch, "E3.8.4.9", {"start": v(49.5, 43.59) * mm, "end": v(49.5, 46.48) * mm});
            skLineSegment(sketch, "E3.8.4.10", {"start": v(52, 42.15) * mm, "end": v(49.5, 43.59) * mm});
            skLineSegment(sketch, "E3.8.4.11", {"start": v(54.5, 43.59) * mm, "end": v(52, 42.15) * mm});
            skLineSegment(sketch, "E3.8.4.12", {"start": v(54.5, 46.48) * mm, "end": v(54.5, 43.59) * mm});
            skLineSegment(sketch, "E3.8.4.13", {"start": v(52, 47.92) * mm, "end": v(54.5, 46.48) * mm});
            skLineSegment(sketch, "E3.8.4.14", {"start": v(52.75, 40.85) * mm, "end": v(55.25, 42.3) * mm});
            skLineSegment(sketch, "E3.8.4.15", {"start": v(52.75, 37.96) * mm, "end": v(52.75, 40.85) * mm});
            skCircle(sketch, "E3.8.5.0", {"center": v(55.25, 50.66) * mm, "radius": 2.5 * mm, "construction": true});
            skCircle(sketch, "E3.8.5.1", {"center": v(52, 56.3) * mm, "radius": 2.5 * mm, "construction": true});
            skPoint(sketch, "E3.8.5.2", {"position": v(53.25, 58.46) * mm});
            skPoint(sketch, "E3.8.5.3", {"position": v(56.5, 52.83) * mm});
            skLineSegment(sketch, "E3.8.5.4", {"start": v(55.25, 47.78) * mm, "end": v(52.75, 49.22) * mm});
            skLineSegment(sketch, "E3.8.5.5", {"start": v(57.75, 49.22) * mm, "end": v(55.25, 47.78) * mm});
            skLineSegment(sketch, "E3.8.5.6", {"start": v(57.75, 52.1) * mm, "end": v(57.75, 49.22) * mm});
            skLineSegment(sketch, "E3.8.5.7", {"start": v(55.25, 53.55) * mm, "end": v(57.75, 52.1) * mm});
            skLineSegment(sketch, "E3.8.5.8", {"start": v(49.5, 57.74) * mm, "end": v(52, 59.18) * mm});
            skLineSegment(sketch, "E3.8.5.9", {"start": v(49.5, 54.85) * mm, "end": v(49.5, 57.74) * mm});
            skLineSegment(sketch, "E3.8.5.10", {"start": v(52, 53.4) * mm, "end": v(49.5, 54.85) * mm});
            skLineSegment(sketch, "E3.8.5.11", {"start": v(54.5, 54.85) * mm, "end": v(52, 53.4) * mm});
            skLineSegment(sketch, "E3.8.5.12", {"start": v(54.5, 57.74) * mm, "end": v(54.5, 54.85) * mm});
            skLineSegment(sketch, "E3.8.5.13", {"start": v(52, 59.18) * mm, "end": v(54.5, 57.74) * mm});
            skLineSegment(sketch, "E3.8.5.14", {"start": v(52.75, 52.1) * mm, "end": v(55.25, 53.55) * mm});
            skLineSegment(sketch, "E3.8.5.15", {"start": v(52.75, 49.22) * mm, "end": v(52.75, 52.1) * mm});
            skCircle(sketch, "E3.8.6.0", {"center": v(55.25, 61.92) * mm, "radius": 2.5 * mm, "construction": true});
            skCircle(sketch, "E3.8.6.1", {"center": v(52, 67.55) * mm, "radius": 2.5 * mm, "construction": true});
            skPoint(sketch, "E3.8.6.2", {"position": v(53.25, 69.72) * mm});
            skPoint(sketch, "E3.8.6.3", {"position": v(56.5, 64.09) * mm});
            skLineSegment(sketch, "E3.8.6.4", {"start": v(55.25, 59.03) * mm, "end": v(52.75, 60.48) * mm});
            skLineSegment(sketch, "E3.8.6.5", {"start": v(57.75, 60.48) * mm, "end": v(55.25, 59.03) * mm});
            skLineSegment(sketch, "E3.8.6.6", {"start": v(57.75, 63.36) * mm, "end": v(57.75, 60.48) * mm});
            skLineSegment(sketch, "E3.8.6.7", {"start": v(55.25, 64.8) * mm, "end": v(57.75, 63.36) * mm});
            skLineSegment(sketch, "E3.8.6.8", {"start": v(49.5, 69) * mm, "end": v(52, 70.44) * mm});
            skLineSegment(sketch, "E3.8.6.9", {"start": v(49.5, 66.1) * mm, "end": v(49.5, 69) * mm});
            skLineSegment(sketch, "E3.8.6.10", {"start": v(52, 64.66) * mm, "end": v(49.5, 66.1) * mm});
            skLineSegment(sketch, "E3.8.6.11", {"start": v(54.5, 66.1) * mm, "end": v(52, 64.66) * mm});
            skLineSegment(sketch, "E3.8.6.12", {"start": v(54.5, 69) * mm, "end": v(54.5, 66.1) * mm});
            skLineSegment(sketch, "E3.8.6.13", {"start": v(52, 70.44) * mm, "end": v(54.5, 69) * mm});
            skLineSegment(sketch, "E3.8.6.14", {"start": v(52.75, 63.36) * mm, "end": v(55.25, 64.8) * mm});
            skLineSegment(sketch, "E3.8.6.15", {"start": v(52.75, 60.48) * mm, "end": v(52.75, 63.36) * mm});
            skCircle(sketch, "E3.8.7.0", {"center": v(55.25, 73.18) * mm, "radius": 2.5 * mm, "construction": true});
            skCircle(sketch, "E3.8.7.1", {"center": v(52, 78.8) * mm, "radius": 2.5 * mm, "construction": true});
            skPoint(sketch, "E3.8.7.2", {"position": v(53.25, 80.97) * mm});
            skPoint(sketch, "E3.8.7.3", {"position": v(56.5, 75.34) * mm});
            skLineSegment(sketch, "E3.8.7.4", {"start": v(55.25, 70.3) * mm, "end": v(52.75, 71.74) * mm});
            skLineSegment(sketch, "E3.8.7.5", {"start": v(57.75, 71.74) * mm, "end": v(55.25, 70.3) * mm});
            skLineSegment(sketch, "E3.8.7.6", {"start": v(57.75, 74.62) * mm, "end": v(57.75, 71.74) * mm});
            skLineSegment(sketch, "E3.8.7.7", {"start": v(55.25, 76.07) * mm, "end": v(57.75, 74.62) * mm});
            skLineSegment(sketch, "E3.8.7.8", {"start": v(49.5, 80.25) * mm, "end": v(52, 81.7) * mm});
            skLineSegment(sketch, "E3.8.7.9", {"start": v(49.5, 77.36) * mm, "end": v(49.5, 80.25) * mm});
            skLineSegment(sketch, "E3.8.7.10", {"start": v(52, 75.92) * mm, "end": v(49.5, 77.36) * mm});
            skLineSegment(sketch, "E3.8.7.11", {"start": v(54.5, 77.36) * mm, "end": v(52, 75.92) * mm});
            skLineSegment(sketch, "E3.8.7.12", {"start": v(54.5, 80.25) * mm, "end": v(54.5, 77.36) * mm});
            skLineSegment(sketch, "E3.8.7.13", {"start": v(52, 81.7) * mm, "end": v(54.5, 80.25) * mm});
            skLineSegment(sketch, "E3.8.7.14", {"start": v(52.75, 74.62) * mm, "end": v(55.25, 76.07) * mm});
            skLineSegment(sketch, "E3.8.7.15", {"start": v(52.75, 71.74) * mm, "end": v(52.75, 74.62) * mm});
            skCircle(sketch, "E3.8.8.0", {"center": v(55.25, 84.44) * mm, "radius": 2.5 * mm, "construction": true});
            skCircle(sketch, "E3.8.8.1", {"center": v(52, 90.07) * mm, "radius": 2.5 * mm, "construction": true});
            skPoint(sketch, "E3.8.8.2", {"position": v(53.25, 92.23) * mm});
            skPoint(sketch, "E3.8.8.3", {"position": v(56.5, 86.6) * mm});
            skLineSegment(sketch, "E3.8.8.4", {"start": v(55.25, 81.55) * mm, "end": v(52.75, 83) * mm});
            skLineSegment(sketch, "E3.8.8.5", {"start": v(57.75, 83) * mm, "end": v(55.25, 81.55) * mm});
            skLineSegment(sketch, "E3.8.8.6", {"start": v(57.75, 85.88) * mm, "end": v(57.75, 83) * mm});
            skLineSegment(sketch, "E3.8.8.7", {"start": v(55.25, 87.32) * mm, "end": v(57.75, 85.88) * mm});
            skLineSegment(sketch, "E3.8.8.8", {"start": v(49.5, 91.51) * mm, "end": v(52, 92.95) * mm});
            skLineSegment(sketch, "E3.8.8.9", {"start": v(49.5, 88.62) * mm, "end": v(49.5, 91.51) * mm});
            skLineSegment(sketch, "E3.8.8.10", {"start": v(52, 87.18) * mm, "end": v(49.5, 88.62) * mm});
            skLineSegment(sketch, "E3.8.8.11", {"start": v(54.5, 88.62) * mm, "end": v(52, 87.18) * mm});
            skLineSegment(sketch, "E3.8.8.12", {"start": v(54.5, 91.51) * mm, "end": v(54.5, 88.62) * mm});
            skLineSegment(sketch, "E3.8.8.13", {"start": v(52, 92.95) * mm, "end": v(54.5, 91.51) * mm});
            skLineSegment(sketch, "E3.8.8.14", {"start": v(52.75, 85.88) * mm, "end": v(55.25, 87.32) * mm});
            skLineSegment(sketch, "E3.8.8.15", {"start": v(52.75, 83) * mm, "end": v(52.75, 85.88) * mm});
            skCircle(sketch, "E3.8.9.0", {"center": v(55.25, 95.7) * mm, "radius": 2.5 * mm, "construction": true});
            skCircle(sketch, "E3.8.9.1", {"center": v(52, 101.32) * mm, "radius": 2.5 * mm, "construction": true});
            skPoint(sketch, "E3.8.9.2", {"position": v(53.25, 103.5) * mm});
            skPoint(sketch, "E3.8.9.3", {"position": v(56.5, 97.86) * mm});
            skLineSegment(sketch, "E3.8.9.4", {"start": v(55.25, 92.8) * mm, "end": v(52.75, 94.25) * mm});
            skLineSegment(sketch, "E3.8.9.5", {"start": v(57.75, 94.25) * mm, "end": v(55.25, 92.8) * mm});
            skLineSegment(sketch, "E3.8.9.6", {"start": v(57.75, 97.14) * mm, "end": v(57.75, 94.25) * mm});
            skLineSegment(sketch, "E3.8.9.7", {"start": v(55.25, 98.58) * mm, "end": v(57.75, 97.14) * mm});
            skLineSegment(sketch, "E3.8.9.8", {"start": v(49.5, 102.77) * mm, "end": v(52, 104.21) * mm});
            skLineSegment(sketch, "E3.8.9.9", {"start": v(49.5, 99.88) * mm, "end": v(49.5, 102.77) * mm});
            skLineSegment(sketch, "E3.8.9.10", {"start": v(52, 98.44) * mm, "end": v(49.5, 99.88) * mm});
            skLineSegment(sketch, "E3.8.9.11", {"start": v(54.5, 99.88) * mm, "end": v(52, 98.44) * mm});
            skLineSegment(sketch, "E3.8.9.12", {"start": v(54.5, 102.77) * mm, "end": v(54.5, 99.88) * mm});
            skLineSegment(sketch, "E3.8.9.13", {"start": v(52, 104.21) * mm, "end": v(54.5, 102.77) * mm});
            skLineSegment(sketch, "E3.8.9.14", {"start": v(52.75, 97.14) * mm, "end": v(55.25, 98.58) * mm});
            skLineSegment(sketch, "E3.8.9.15", {"start": v(52.75, 94.25) * mm, "end": v(52.75, 97.14) * mm});
            skCircle(sketch, "E3.9.0.0", {"center": v(61.75, -5.63) * mm, "radius": 2.5 * mm, "construction": true});
            skCircle(sketch, "E3.9.0.1", {"center": v(58.5, 0) * mm, "radius": 2.5 * mm, "construction": true});
            skPoint(sketch, "E3.9.0.2", {"position": v(59.75, 2.17) * mm});
            skPoint(sketch, "E3.9.0.3", {"position": v(63, -3.46) * mm});
            skLineSegment(sketch, "E3.9.0.4", {"start": v(61.75, -8.52) * mm, "end": v(59.25, -7.07) * mm});
            skLineSegment(sketch, "E3.9.0.5", {"start": v(64.25, -7.07) * mm, "end": v(61.75, -8.52) * mm});
            skLineSegment(sketch, "E3.9.0.6", {"start": v(64.25, -4.19) * mm, "end": v(64.25, -7.07) * mm});
            skLineSegment(sketch, "E3.9.0.7", {"start": v(61.75, -2.74) * mm, "end": v(64.25, -4.19) * mm});
            skLineSegment(sketch, "E3.9.0.8", {"start": v(56, 1.44) * mm, "end": v(58.5, 2.89) * mm});
            skLineSegment(sketch, "E3.9.0.9", {"start": v(56, -1.44) * mm, "end": v(56, 1.44) * mm});
            skLineSegment(sketch, "E3.9.0.10", {"start": v(58.5, -2.89) * mm, "end": v(56, -1.44) * mm});
            skLineSegment(sketch, "E3.9.0.11", {"start": v(61, -1.44) * mm, "end": v(58.5, -2.89) * mm});
            skLineSegment(sketch, "E3.9.0.12", {"start": v(61, 1.44) * mm, "end": v(61, -1.44) * mm});
            skLineSegment(sketch, "E3.9.0.13", {"start": v(58.5, 2.89) * mm, "end": v(61, 1.44) * mm});
            skLineSegment(sketch, "E3.9.0.14", {"start": v(59.25, -4.19) * mm, "end": v(61.75, -2.74) * mm});
            skLineSegment(sketch, "E3.9.0.15", {"start": v(59.25, -7.07) * mm, "end": v(59.25, -4.19) * mm});
            skCircle(sketch, "E3.9.1.0", {"center": v(61.75, 5.63) * mm, "radius": 2.5 * mm, "construction": true});
            skCircle(sketch, "E3.9.1.1", {"center": v(58.5, 11.26) * mm, "radius": 2.5 * mm, "construction": true});
            skPoint(sketch, "E3.9.1.2", {"position": v(59.75, 13.42) * mm});
            skPoint(sketch, "E3.9.1.3", {"position": v(63, 7.8) * mm});
            skLineSegment(sketch, "E3.9.1.4", {"start": v(61.75, 2.74) * mm, "end": v(59.25, 4.19) * mm});
            skLineSegment(sketch, "E3.9.1.5", {"start": v(64.25, 4.19) * mm, "end": v(61.75, 2.74) * mm});
            skLineSegment(sketch, "E3.9.1.6", {"start": v(64.25, 7.07) * mm, "end": v(64.25, 4.19) * mm});
            skLineSegment(sketch, "E3.9.1.7", {"start": v(61.75, 8.52) * mm, "end": v(64.25, 7.07) * mm});
            skLineSegment(sketch, "E3.9.1.8", {"start": v(56, 12.7) * mm, "end": v(58.5, 14.15) * mm});
            skLineSegment(sketch, "E3.9.1.9", {"start": v(56, 9.81) * mm, "end": v(56, 12.7) * mm});
            skLineSegment(sketch, "E3.9.1.10", {"start": v(58.5, 8.37) * mm, "end": v(56, 9.81) * mm});
            skLineSegment(sketch, "E3.9.1.11", {"start": v(61, 9.81) * mm, "end": v(58.5, 8.37) * mm});
            skLineSegment(sketch, "E3.9.1.12", {"start": v(61, 12.7) * mm, "end": v(61, 9.81) * mm});
            skLineSegment(sketch, "E3.9.1.13", {"start": v(58.5, 14.15) * mm, "end": v(61, 12.7) * mm});
            skLineSegment(sketch, "E3.9.1.14", {"start": v(59.25, 7.07) * mm, "end": v(61.75, 8.52) * mm});
            skLineSegment(sketch, "E3.9.1.15", {"start": v(59.25, 4.19) * mm, "end": v(59.25, 7.07) * mm});
            skCircle(sketch, "E3.9.2.0", {"center": v(61.75, 16.89) * mm, "radius": 2.5 * mm, "construction": true});
            skCircle(sketch, "E3.9.2.1", {"center": v(58.5, 22.52) * mm, "radius": 2.5 * mm, "construction": true});
            skPoint(sketch, "E3.9.2.2", {"position": v(59.75, 24.68) * mm});
            skPoint(sketch, "E3.9.2.3", {"position": v(63, 19.05) * mm});
            skLineSegment(sketch, "E3.9.2.4", {"start": v(61.75, 14) * mm, "end": v(59.25, 15.44) * mm});
            skLineSegment(sketch, "E3.9.2.5", {"start": v(64.25, 15.44) * mm, "end": v(61.75, 14) * mm});
            skLineSegment(sketch, "E3.9.2.6", {"start": v(64.25, 18.33) * mm, "end": v(64.25, 15.44) * mm});
            skLineSegment(sketch, "E3.9.2.7", {"start": v(61.75, 19.77) * mm, "end": v(64.25, 18.33) * mm});
            skLineSegment(sketch, "E3.9.2.8", {"start": v(56, 23.96) * mm, "end": v(58.5, 25.4) * mm});
            skLineSegment(sketch, "E3.9.2.9", {"start": v(56, 21.07) * mm, "end": v(56, 23.96) * mm});
            skLineSegment(sketch, "E3.9.2.10", {"start": v(58.5, 19.63) * mm, "end": v(56, 21.07) * mm});
            skLineSegment(sketch, "E3.9.2.11", {"start": v(61, 21.07) * mm, "end": v(58.5, 19.63) * mm});
            skLineSegment(sketch, "E3.9.2.12", {"start": v(61, 23.96) * mm, "end": v(61, 21.07) * mm});
            skLineSegment(sketch, "E3.9.2.13", {"start": v(58.5, 25.4) * mm, "end": v(61, 23.96) * mm});
            skLineSegment(sketch, "E3.9.2.14", {"start": v(59.25, 18.33) * mm, "end": v(61.75, 19.77) * mm});
            skLineSegment(sketch, "E3.9.2.15", {"start": v(59.25, 15.44) * mm, "end": v(59.25, 18.33) * mm});
            skCircle(sketch, "E3.9.3.0", {"center": v(61.75, 28.15) * mm, "radius": 2.5 * mm, "construction": true});
            skCircle(sketch, "E3.9.3.1", {"center": v(58.5, 33.77) * mm, "radius": 2.5 * mm, "construction": true});
            skPoint(sketch, "E3.9.3.2", {"position": v(59.75, 35.94) * mm});
            skPoint(sketch, "E3.9.3.3", {"position": v(63, 30.31) * mm});
            skLineSegment(sketch, "E3.9.3.4", {"start": v(61.75, 25.26) * mm, "end": v(59.25, 26.7) * mm});
            skLineSegment(sketch, "E3.9.3.5", {"start": v(64.25, 26.7) * mm, "end": v(61.75, 25.26) * mm});
            skLineSegment(sketch, "E3.9.3.6", {"start": v(64.25, 29.59) * mm, "end": v(64.25, 26.7) * mm});
            skLineSegment(sketch, "E3.9.3.7", {"start": v(61.75, 31.03) * mm, "end": v(64.25, 29.59) * mm});
            skLineSegment(sketch, "E3.9.3.8", {"start": v(56, 35.22) * mm, "end": v(58.5, 36.66) * mm});
            skLineSegment(sketch, "E3.9.3.9", {"start": v(56, 32.33) * mm, "end": v(56, 35.22) * mm});
            skLineSegment(sketch, "E3.9.3.10", {"start": v(58.5, 30.89) * mm, "end": v(56, 32.33) * mm});
            skLineSegment(sketch, "E3.9.3.11", {"start": v(61, 32.33) * mm, "end": v(58.5, 30.89) * mm});
            skLineSegment(sketch, "E3.9.3.12", {"start": v(61, 35.22) * mm, "end": v(61, 32.33) * mm});
            skLineSegment(sketch, "E3.9.3.13", {"start": v(58.5, 36.66) * mm, "end": v(61, 35.22) * mm});
            skLineSegment(sketch, "E3.9.3.14", {"start": v(59.25, 29.59) * mm, "end": v(61.75, 31.03) * mm});
            skLineSegment(sketch, "E3.9.3.15", {"start": v(59.25, 26.7) * mm, "end": v(59.25, 29.59) * mm});
            skCircle(sketch, "E3.9.4.0", {"center": v(61.75, 39.4) * mm, "radius": 2.5 * mm, "construction": true});
            skCircle(sketch, "E3.9.4.1", {"center": v(58.5, 45.03) * mm, "radius": 2.5 * mm, "construction": true});
            skPoint(sketch, "E3.9.4.2", {"position": v(59.75, 47.2) * mm});
            skPoint(sketch, "E3.9.4.3", {"position": v(63, 41.57) * mm});
            skLineSegment(sketch, "E3.9.4.4", {"start": v(61.75, 36.52) * mm, "end": v(59.25, 37.96) * mm});
            skLineSegment(sketch, "E3.9.4.5", {"start": v(64.25, 37.96) * mm, "end": v(61.75, 36.52) * mm});
            skLineSegment(sketch, "E3.9.4.6", {"start": v(64.25, 40.85) * mm, "end": v(64.25, 37.96) * mm});
            skLineSegment(sketch, "E3.9.4.7", {"start": v(61.75, 42.3) * mm, "end": v(64.25, 40.85) * mm});
            skLineSegment(sketch, "E3.9.4.8", {"start": v(56, 46.48) * mm, "end": v(58.5, 47.92) * mm});
            skLineSegment(sketch, "E3.9.4.9", {"start": v(56, 43.59) * mm, "end": v(56, 46.48) * mm});
            skLineSegment(sketch, "E3.9.4.10", {"start": v(58.5, 42.15) * mm, "end": v(56, 43.59) * mm});
            skLineSegment(sketch, "E3.9.4.11", {"start": v(61, 43.59) * mm, "end": v(58.5, 42.15) * mm});
            skLineSegment(sketch, "E3.9.4.12", {"start": v(61, 46.48) * mm, "end": v(61, 43.59) * mm});
            skLineSegment(sketch, "E3.9.4.13", {"start": v(58.5, 47.92) * mm, "end": v(61, 46.48) * mm});
            skLineSegment(sketch, "E3.9.4.14", {"start": v(59.25, 40.85) * mm, "end": v(61.75, 42.3) * mm});
            skLineSegment(sketch, "E3.9.4.15", {"start": v(59.25, 37.96) * mm, "end": v(59.25, 40.85) * mm});
            skCircle(sketch, "E3.9.5.0", {"center": v(61.75, 50.66) * mm, "radius": 2.5 * mm, "construction": true});
            skCircle(sketch, "E3.9.5.1", {"center": v(58.5, 56.3) * mm, "radius": 2.5 * mm, "construction": true});
            skPoint(sketch, "E3.9.5.2", {"position": v(59.75, 58.46) * mm});
            skPoint(sketch, "E3.9.5.3", {"position": v(63, 52.83) * mm});
            skLineSegment(sketch, "E3.9.5.4", {"start": v(61.75, 47.78) * mm, "end": v(59.25, 49.22) * mm});
            skLineSegment(sketch, "E3.9.5.5", {"start": v(64.25, 49.22) * mm, "end": v(61.75, 47.78) * mm});
            skLineSegment(sketch, "E3.9.5.6", {"start": v(64.25, 52.1) * mm, "end": v(64.25, 49.22) * mm});
            skLineSegment(sketch, "E3.9.5.7", {"start": v(61.75, 53.55) * mm, "end": v(64.25, 52.1) * mm});
            skLineSegment(sketch, "E3.9.5.8", {"start": v(56, 57.74) * mm, "end": v(58.5, 59.18) * mm});
            skLineSegment(sketch, "E3.9.5.9", {"start": v(56, 54.85) * mm, "end": v(56, 57.74) * mm});
            skLineSegment(sketch, "E3.9.5.10", {"start": v(58.5, 53.4) * mm, "end": v(56, 54.85) * mm});
            skLineSegment(sketch, "E3.9.5.11", {"start": v(61, 54.85) * mm, "end": v(58.5, 53.4) * mm});
            skLineSegment(sketch, "E3.9.5.12", {"start": v(61, 57.74) * mm, "end": v(61, 54.85) * mm});
            skLineSegment(sketch, "E3.9.5.13", {"start": v(58.5, 59.18) * mm, "end": v(61, 57.74) * mm});
            skLineSegment(sketch, "E3.9.5.14", {"start": v(59.25, 52.1) * mm, "end": v(61.75, 53.55) * mm});
            skLineSegment(sketch, "E3.9.5.15", {"start": v(59.25, 49.22) * mm, "end": v(59.25, 52.1) * mm});
            skCircle(sketch, "E3.9.6.0", {"center": v(61.75, 61.92) * mm, "radius": 2.5 * mm, "construction": true});
            skCircle(sketch, "E3.9.6.1", {"center": v(58.5, 67.55) * mm, "radius": 2.5 * mm, "construction": true});
            skPoint(sketch, "E3.9.6.2", {"position": v(59.75, 69.72) * mm});
            skPoint(sketch, "E3.9.6.3", {"position": v(63, 64.09) * mm});
            skLineSegment(sketch, "E3.9.6.4", {"start": v(61.75, 59.03) * mm, "end": v(59.25, 60.48) * mm});
            skLineSegment(sketch, "E3.9.6.5", {"start": v(64.25, 60.48) * mm, "end": v(61.75, 59.03) * mm});
            skLineSegment(sketch, "E3.9.6.6", {"start": v(64.25, 63.36) * mm, "end": v(64.25, 60.48) * mm});
            skLineSegment(sketch, "E3.9.6.7", {"start": v(61.75, 64.8) * mm, "end": v(64.25, 63.36) * mm});
            skLineSegment(sketch, "E3.9.6.8", {"start": v(56, 69) * mm, "end": v(58.5, 70.44) * mm});
            skLineSegment(sketch, "E3.9.6.9", {"start": v(56, 66.1) * mm, "end": v(56, 69) * mm});
            skLineSegment(sketch, "E3.9.6.10", {"start": v(58.5, 64.66) * mm, "end": v(56, 66.1) * mm});
            skLineSegment(sketch, "E3.9.6.11", {"start": v(61, 66.1) * mm, "end": v(58.5, 64.66) * mm});
            skLineSegment(sketch, "E3.9.6.12", {"start": v(61, 69) * mm, "end": v(61, 66.1) * mm});
            skLineSegment(sketch, "E3.9.6.13", {"start": v(58.5, 70.44) * mm, "end": v(61, 69) * mm});
            skLineSegment(sketch, "E3.9.6.14", {"start": v(59.25, 63.36) * mm, "end": v(61.75, 64.8) * mm});
            skLineSegment(sketch, "E3.9.6.15", {"start": v(59.25, 60.48) * mm, "end": v(59.25, 63.36) * mm});
            skCircle(sketch, "E3.9.7.0", {"center": v(61.75, 73.18) * mm, "radius": 2.5 * mm, "construction": true});
            skCircle(sketch, "E3.9.7.1", {"center": v(58.5, 78.8) * mm, "radius": 2.5 * mm, "construction": true});
            skPoint(sketch, "E3.9.7.2", {"position": v(59.75, 80.97) * mm});
            skPoint(sketch, "E3.9.7.3", {"position": v(63, 75.34) * mm});
            skLineSegment(sketch, "E3.9.7.4", {"start": v(61.75, 70.3) * mm, "end": v(59.25, 71.74) * mm});
            skLineSegment(sketch, "E3.9.7.5", {"start": v(64.25, 71.74) * mm, "end": v(61.75, 70.3) * mm});
            skLineSegment(sketch, "E3.9.7.6", {"start": v(64.25, 74.62) * mm, "end": v(64.25, 71.74) * mm});
            skLineSegment(sketch, "E3.9.7.7", {"start": v(61.75, 76.07) * mm, "end": v(64.25, 74.62) * mm});
            skLineSegment(sketch, "E3.9.7.8", {"start": v(56, 80.25) * mm, "end": v(58.5, 81.7) * mm});
            skLineSegment(sketch, "E3.9.7.9", {"start": v(56, 77.36) * mm, "end": v(56, 80.25) * mm});
            skLineSegment(sketch, "E3.9.7.10", {"start": v(58.5, 75.92) * mm, "end": v(56, 77.36) * mm});
            skLineSegment(sketch, "E3.9.7.11", {"start": v(61, 77.36) * mm, "end": v(58.5, 75.92) * mm});
            skLineSegment(sketch, "E3.9.7.12", {"start": v(61, 80.25) * mm, "end": v(61, 77.36) * mm});
            skLineSegment(sketch, "E3.9.7.13", {"start": v(58.5, 81.7) * mm, "end": v(61, 80.25) * mm});
            skLineSegment(sketch, "E3.9.7.14", {"start": v(59.25, 74.62) * mm, "end": v(61.75, 76.07) * mm});
            skLineSegment(sketch, "E3.9.7.15", {"start": v(59.25, 71.74) * mm, "end": v(59.25, 74.62) * mm});
            skCircle(sketch, "E3.9.8.0", {"center": v(61.75, 84.44) * mm, "radius": 2.5 * mm, "construction": true});
            skCircle(sketch, "E3.9.8.1", {"center": v(58.5, 90.07) * mm, "radius": 2.5 * mm, "construction": true});
            skPoint(sketch, "E3.9.8.2", {"position": v(59.75, 92.23) * mm});
            skPoint(sketch, "E3.9.8.3", {"position": v(63, 86.6) * mm});
            skLineSegment(sketch, "E3.9.8.4", {"start": v(61.75, 81.55) * mm, "end": v(59.25, 83) * mm});
            skLineSegment(sketch, "E3.9.8.5", {"start": v(64.25, 83) * mm, "end": v(61.75, 81.55) * mm});
            skLineSegment(sketch, "E3.9.8.6", {"start": v(64.25, 85.88) * mm, "end": v(64.25, 83) * mm});
            skLineSegment(sketch, "E3.9.8.7", {"start": v(61.75, 87.32) * mm, "end": v(64.25, 85.88) * mm});
            skLineSegment(sketch, "E3.9.8.8", {"start": v(56, 91.51) * mm, "end": v(58.5, 92.95) * mm});
            skLineSegment(sketch, "E3.9.8.9", {"start": v(56, 88.62) * mm, "end": v(56, 91.51) * mm});
            skLineSegment(sketch, "E3.9.8.10", {"start": v(58.5, 87.18) * mm, "end": v(56, 88.62) * mm});
            skLineSegment(sketch, "E3.9.8.11", {"start": v(61, 88.62) * mm, "end": v(58.5, 87.18) * mm});
            skLineSegment(sketch, "E3.9.8.12", {"start": v(61, 91.51) * mm, "end": v(61, 88.62) * mm});
            skLineSegment(sketch, "E3.9.8.13", {"start": v(58.5, 92.95) * mm, "end": v(61, 91.51) * mm});
            skLineSegment(sketch, "E3.9.8.14", {"start": v(59.25, 85.88) * mm, "end": v(61.75, 87.32) * mm});
            skLineSegment(sketch, "E3.9.8.15", {"start": v(59.25, 83) * mm, "end": v(59.25, 85.88) * mm});
            skCircle(sketch, "E3.9.9.0", {"center": v(61.75, 95.7) * mm, "radius": 2.5 * mm, "construction": true});
            skCircle(sketch, "E3.9.9.1", {"center": v(58.5, 101.32) * mm, "radius": 2.5 * mm, "construction": true});
            skPoint(sketch, "E3.9.9.2", {"position": v(59.75, 103.5) * mm});
            skPoint(sketch, "E3.9.9.3", {"position": v(63, 97.86) * mm});
            skLineSegment(sketch, "E3.9.9.4", {"start": v(61.75, 92.8) * mm, "end": v(59.25, 94.25) * mm});
            skLineSegment(sketch, "E3.9.9.5", {"start": v(64.25, 94.25) * mm, "end": v(61.75, 92.8) * mm});
            skLineSegment(sketch, "E3.9.9.6", {"start": v(64.25, 97.14) * mm, "end": v(64.25, 94.25) * mm});
            skLineSegment(sketch, "E3.9.9.7", {"start": v(61.75, 98.58) * mm, "end": v(64.25, 97.14) * mm});
            skLineSegment(sketch, "E3.9.9.8", {"start": v(56, 102.77) * mm, "end": v(58.5, 104.21) * mm});
            skLineSegment(sketch, "E3.9.9.9", {"start": v(56, 99.88) * mm, "end": v(56, 102.77) * mm});
            skLineSegment(sketch, "E3.9.9.10", {"start": v(58.5, 98.44) * mm, "end": v(56, 99.88) * mm});
            skLineSegment(sketch, "E3.9.9.11", {"start": v(61, 99.88) * mm, "end": v(58.5, 98.44) * mm});
            skLineSegment(sketch, "E3.9.9.12", {"start": v(61, 102.77) * mm, "end": v(61, 99.88) * mm});
            skLineSegment(sketch, "E3.9.9.13", {"start": v(58.5, 104.21) * mm, "end": v(61, 102.77) * mm});
            skLineSegment(sketch, "E3.9.9.14", {"start": v(59.25, 97.14) * mm, "end": v(61.75, 98.58) * mm});
            skLineSegment(sketch, "E3.9.9.15", {"start": v(59.25, 94.25) * mm, "end": v(59.25, 97.14) * mm});
            skLineSegment(sketch, "E3.direction1", {"start": v(0.75, -7.07) * mm, "end": v(7.25, -7.07) * mm, "construction": true});
            skLineSegment(sketch, "E3.direction2", {"start": v(0.75, -7.07) * mm, "end": v(0.75, 4.19) * mm, "construction": true});
            skCircle(sketch, "E4.0.10.0", {"center": v(68.25, -5.63) * mm, "radius": 2.5 * mm, "construction": true});
            skCircle(sketch, "E4.2.10.0", {"center": v(65, 0) * mm, "radius": 2.5 * mm, "construction": true});
            skPoint(sketch, "E4.4.10.0", {"position": v(66.25, 2.17) * mm});
            skPoint(sketch, "E4.5.10.0", {"position": v(69.5, -3.46) * mm});
            skLineSegment(sketch, "E4.6.10.0", {"start": v(68.25, -8.52) * mm, "end": v(65.75, -7.07) * mm});
            skLineSegment(sketch, "E4.9.10.0", {"start": v(70.75, -7.07) * mm, "end": v(68.25, -8.52) * mm});
            skLineSegment(sketch, "E4.12.10.0", {"start": v(70.75, -4.19) * mm, "end": v(70.75, -7.07) * mm});
            skLineSegment(sketch, "E4.15.10.0", {"start": v(68.25, -2.74) * mm, "end": v(70.75, -4.19) * mm});
            skLineSegment(sketch, "E4.18.10.0", {"start": v(62.5, 1.44) * mm, "end": v(65, 2.89) * mm});
            skLineSegment(sketch, "E4.21.10.0", {"start": v(62.5, -1.44) * mm, "end": v(62.5, 1.44) * mm});
            skLineSegment(sketch, "E4.24.10.0", {"start": v(65, -2.89) * mm, "end": v(62.5, -1.44) * mm});
            skLineSegment(sketch, "E4.27.10.0", {"start": v(67.5, -1.44) * mm, "end": v(65, -2.89) * mm});
            skLineSegment(sketch, "E4.30.10.0", {"start": v(67.5, 1.44) * mm, "end": v(67.5, -1.44) * mm});
            skLineSegment(sketch, "E4.33.10.0", {"start": v(65, 2.89) * mm, "end": v(67.5, 1.44) * mm});
            skLineSegment(sketch, "E4.36.10.0", {"start": v(65.75, -4.19) * mm, "end": v(68.25, -2.74) * mm});
            skLineSegment(sketch, "E4.39.10.0", {"start": v(65.75, -7.07) * mm, "end": v(65.75, -4.19) * mm});
            skCircle(sketch, "E4.0.10.1", {"center": v(68.25, 5.63) * mm, "radius": 2.5 * mm, "construction": true});
            skCircle(sketch, "E4.2.10.1", {"center": v(65, 11.26) * mm, "radius": 2.5 * mm, "construction": true});
            skPoint(sketch, "E4.4.10.1", {"position": v(66.25, 13.42) * mm});
            skPoint(sketch, "E4.5.10.1", {"position": v(69.5, 7.8) * mm});
            skLineSegment(sketch, "E4.6.10.1", {"start": v(68.25, 2.74) * mm, "end": v(65.75, 4.19) * mm});
            skLineSegment(sketch, "E4.9.10.1", {"start": v(70.75, 4.19) * mm, "end": v(68.25, 2.74) * mm});
            skLineSegment(sketch, "E4.12.10.1", {"start": v(70.75, 7.07) * mm, "end": v(70.75, 4.19) * mm});
            skLineSegment(sketch, "E4.15.10.1", {"start": v(68.25, 8.52) * mm, "end": v(70.75, 7.07) * mm});
            skLineSegment(sketch, "E4.18.10.1", {"start": v(62.5, 12.7) * mm, "end": v(65, 14.15) * mm});
            skLineSegment(sketch, "E4.21.10.1", {"start": v(62.5, 9.81) * mm, "end": v(62.5, 12.7) * mm});
            skLineSegment(sketch, "E4.24.10.1", {"start": v(65, 8.37) * mm, "end": v(62.5, 9.81) * mm});
            skLineSegment(sketch, "E4.27.10.1", {"start": v(67.5, 9.81) * mm, "end": v(65, 8.37) * mm});
            skLineSegment(sketch, "E4.30.10.1", {"start": v(67.5, 12.7) * mm, "end": v(67.5, 9.81) * mm});
            skLineSegment(sketch, "E4.33.10.1", {"start": v(65, 14.15) * mm, "end": v(67.5, 12.7) * mm});
            skLineSegment(sketch, "E4.36.10.1", {"start": v(65.75, 7.07) * mm, "end": v(68.25, 8.52) * mm});
            skLineSegment(sketch, "E4.39.10.1", {"start": v(65.75, 4.19) * mm, "end": v(65.75, 7.07) * mm});
            skCircle(sketch, "E4.0.10.2", {"center": v(68.25, 16.89) * mm, "radius": 2.5 * mm, "construction": true});
            skCircle(sketch, "E4.2.10.2", {"center": v(65, 22.52) * mm, "radius": 2.5 * mm, "construction": true});
            skPoint(sketch, "E4.4.10.2", {"position": v(66.25, 24.68) * mm});
            skPoint(sketch, "E4.5.10.2", {"position": v(69.5, 19.05) * mm});
            skLineSegment(sketch, "E4.6.10.2", {"start": v(68.25, 14) * mm, "end": v(65.75, 15.44) * mm});
            skLineSegment(sketch, "E4.9.10.2", {"start": v(70.75, 15.44) * mm, "end": v(68.25, 14) * mm});
            skLineSegment(sketch, "E4.12.10.2", {"start": v(70.75, 18.33) * mm, "end": v(70.75, 15.44) * mm});
            skLineSegment(sketch, "E4.15.10.2", {"start": v(68.25, 19.77) * mm, "end": v(70.75, 18.33) * mm});
            skLineSegment(sketch, "E4.18.10.2", {"start": v(62.5, 23.96) * mm, "end": v(65, 25.4) * mm});
            skLineSegment(sketch, "E4.21.10.2", {"start": v(62.5, 21.07) * mm, "end": v(62.5, 23.96) * mm});
            skLineSegment(sketch, "E4.24.10.2", {"start": v(65, 19.63) * mm, "end": v(62.5, 21.07) * mm});
            skLineSegment(sketch, "E4.27.10.2", {"start": v(67.5, 21.07) * mm, "end": v(65, 19.63) * mm});
            skLineSegment(sketch, "E4.30.10.2", {"start": v(67.5, 23.96) * mm, "end": v(67.5, 21.07) * mm});
            skLineSegment(sketch, "E4.33.10.2", {"start": v(65, 25.4) * mm, "end": v(67.5, 23.96) * mm});
            skLineSegment(sketch, "E4.36.10.2", {"start": v(65.75, 18.33) * mm, "end": v(68.25, 19.77) * mm});
            skLineSegment(sketch, "E4.39.10.2", {"start": v(65.75, 15.44) * mm, "end": v(65.75, 18.33) * mm});
            skCircle(sketch, "E4.0.10.3", {"center": v(68.25, 28.15) * mm, "radius": 2.5 * mm, "construction": true});
            skCircle(sketch, "E4.2.10.3", {"center": v(65, 33.77) * mm, "radius": 2.5 * mm, "construction": true});
            skPoint(sketch, "E4.4.10.3", {"position": v(66.25, 35.94) * mm});
            skPoint(sketch, "E4.5.10.3", {"position": v(69.5, 30.31) * mm});
            skLineSegment(sketch, "E4.6.10.3", {"start": v(68.25, 25.26) * mm, "end": v(65.75, 26.7) * mm});
            skLineSegment(sketch, "E4.9.10.3", {"start": v(70.75, 26.7) * mm, "end": v(68.25, 25.26) * mm});
            skLineSegment(sketch, "E4.12.10.3", {"start": v(70.75, 29.59) * mm, "end": v(70.75, 26.7) * mm});
            skLineSegment(sketch, "E4.15.10.3", {"start": v(68.25, 31.03) * mm, "end": v(70.75, 29.59) * mm});
            skLineSegment(sketch, "E4.18.10.3", {"start": v(62.5, 35.22) * mm, "end": v(65, 36.66) * mm});
            skLineSegment(sketch, "E4.21.10.3", {"start": v(62.5, 32.33) * mm, "end": v(62.5, 35.22) * mm});
            skLineSegment(sketch, "E4.24.10.3", {"start": v(65, 30.89) * mm, "end": v(62.5, 32.33) * mm});
            skLineSegment(sketch, "E4.27.10.3", {"start": v(67.5, 32.33) * mm, "end": v(65, 30.89) * mm});
            skLineSegment(sketch, "E4.30.10.3", {"start": v(67.5, 35.22) * mm, "end": v(67.5, 32.33) * mm});
            skLineSegment(sketch, "E4.33.10.3", {"start": v(65, 36.66) * mm, "end": v(67.5, 35.22) * mm});
            skLineSegment(sketch, "E4.36.10.3", {"start": v(65.75, 29.59) * mm, "end": v(68.25, 31.03) * mm});
            skLineSegment(sketch, "E4.39.10.3", {"start": v(65.75, 26.7) * mm, "end": v(65.75, 29.59) * mm});
            skCircle(sketch, "E4.0.10.4", {"center": v(68.25, 39.4) * mm, "radius": 2.5 * mm, "construction": true});
            skCircle(sketch, "E4.2.10.4", {"center": v(65, 45.03) * mm, "radius": 2.5 * mm, "construction": true});
            skPoint(sketch, "E4.4.10.4", {"position": v(66.25, 47.2) * mm});
            skPoint(sketch, "E4.5.10.4", {"position": v(69.5, 41.57) * mm});
            skLineSegment(sketch, "E4.6.10.4", {"start": v(68.25, 36.52) * mm, "end": v(65.75, 37.96) * mm});
            skLineSegment(sketch, "E4.9.10.4", {"start": v(70.75, 37.96) * mm, "end": v(68.25, 36.52) * mm});
            skLineSegment(sketch, "E4.12.10.4", {"start": v(70.75, 40.85) * mm, "end": v(70.75, 37.96) * mm});
            skLineSegment(sketch, "E4.15.10.4", {"start": v(68.25, 42.3) * mm, "end": v(70.75, 40.85) * mm});
            skLineSegment(sketch, "E4.18.10.4", {"start": v(62.5, 46.48) * mm, "end": v(65, 47.92) * mm});
            skLineSegment(sketch, "E4.21.10.4", {"start": v(62.5, 43.59) * mm, "end": v(62.5, 46.48) * mm});
            skLineSegment(sketch, "E4.24.10.4", {"start": v(65, 42.15) * mm, "end": v(62.5, 43.59) * mm});
            skLineSegment(sketch, "E4.27.10.4", {"start": v(67.5, 43.59) * mm, "end": v(65, 42.15) * mm});
            skLineSegment(sketch, "E4.30.10.4", {"start": v(67.5, 46.48) * mm, "end": v(67.5, 43.59) * mm});
            skLineSegment(sketch, "E4.33.10.4", {"start": v(65, 47.92) * mm, "end": v(67.5, 46.48) * mm});
            skLineSegment(sketch, "E4.36.10.4", {"start": v(65.75, 40.85) * mm, "end": v(68.25, 42.3) * mm});
            skLineSegment(sketch, "E4.39.10.4", {"start": v(65.75, 37.96) * mm, "end": v(65.75, 40.85) * mm});
            skCircle(sketch, "E4.0.10.5", {"center": v(68.25, 50.66) * mm, "radius": 2.5 * mm, "construction": true});
            skCircle(sketch, "E4.2.10.5", {"center": v(65, 56.3) * mm, "radius": 2.5 * mm, "construction": true});
            skPoint(sketch, "E4.4.10.5", {"position": v(66.25, 58.46) * mm});
            skPoint(sketch, "E4.5.10.5", {"position": v(69.5, 52.83) * mm});
            skLineSegment(sketch, "E4.6.10.5", {"start": v(68.25, 47.78) * mm, "end": v(65.75, 49.22) * mm});
            skLineSegment(sketch, "E4.9.10.5", {"start": v(70.75, 49.22) * mm, "end": v(68.25, 47.78) * mm});
            skLineSegment(sketch, "E4.12.10.5", {"start": v(70.75, 52.1) * mm, "end": v(70.75, 49.22) * mm});
            skLineSegment(sketch, "E4.15.10.5", {"start": v(68.25, 53.55) * mm, "end": v(70.75, 52.1) * mm});
            skLineSegment(sketch, "E4.18.10.5", {"start": v(62.5, 57.74) * mm, "end": v(65, 59.18) * mm});
            skLineSegment(sketch, "E4.21.10.5", {"start": v(62.5, 54.85) * mm, "end": v(62.5, 57.74) * mm});
            skLineSegment(sketch, "E4.24.10.5", {"start": v(65, 53.4) * mm, "end": v(62.5, 54.85) * mm});
            skLineSegment(sketch, "E4.27.10.5", {"start": v(67.5, 54.85) * mm, "end": v(65, 53.4) * mm});
            skLineSegment(sketch, "E4.30.10.5", {"start": v(67.5, 57.74) * mm, "end": v(67.5, 54.85) * mm});
            skLineSegment(sketch, "E4.33.10.5", {"start": v(65, 59.18) * mm, "end": v(67.5, 57.74) * mm});
            skLineSegment(sketch, "E4.36.10.5", {"start": v(65.75, 52.1) * mm, "end": v(68.25, 53.55) * mm});
            skLineSegment(sketch, "E4.39.10.5", {"start": v(65.75, 49.22) * mm, "end": v(65.75, 52.1) * mm});
            skCircle(sketch, "E4.0.10.6", {"center": v(68.25, 61.92) * mm, "radius": 2.5 * mm, "construction": true});
            skCircle(sketch, "E4.2.10.6", {"center": v(65, 67.55) * mm, "radius": 2.5 * mm, "construction": true});
            skPoint(sketch, "E4.4.10.6", {"position": v(66.25, 69.72) * mm});
            skPoint(sketch, "E4.5.10.6", {"position": v(69.5, 64.09) * mm});
            skLineSegment(sketch, "E4.6.10.6", {"start": v(68.25, 59.03) * mm, "end": v(65.75, 60.48) * mm});
            skLineSegment(sketch, "E4.9.10.6", {"start": v(70.75, 60.48) * mm, "end": v(68.25, 59.03) * mm});
            skLineSegment(sketch, "E4.12.10.6", {"start": v(70.75, 63.36) * mm, "end": v(70.75, 60.48) * mm});
            skLineSegment(sketch, "E4.15.10.6", {"start": v(68.25, 64.8) * mm, "end": v(70.75, 63.36) * mm});
            skLineSegment(sketch, "E4.18.10.6", {"start": v(62.5, 69) * mm, "end": v(65, 70.44) * mm});
            skLineSegment(sketch, "E4.21.10.6", {"start": v(62.5, 66.1) * mm, "end": v(62.5, 69) * mm});
            skLineSegment(sketch, "E4.24.10.6", {"start": v(65, 64.66) * mm, "end": v(62.5, 66.1) * mm});
            skLineSegment(sketch, "E4.27.10.6", {"start": v(67.5, 66.1) * mm, "end": v(65, 64.66) * mm});
            skLineSegment(sketch, "E4.30.10.6", {"start": v(67.5, 69) * mm, "end": v(67.5, 66.1) * mm});
            skLineSegment(sketch, "E4.33.10.6", {"start": v(65, 70.44) * mm, "end": v(67.5, 69) * mm});
            skLineSegment(sketch, "E4.36.10.6", {"start": v(65.75, 63.36) * mm, "end": v(68.25, 64.8) * mm});
            skLineSegment(sketch, "E4.39.10.6", {"start": v(65.75, 60.48) * mm, "end": v(65.75, 63.36) * mm});
            skCircle(sketch, "E4.0.10.7", {"center": v(68.25, 73.18) * mm, "radius": 2.5 * mm, "construction": true});
            skCircle(sketch, "E4.2.10.7", {"center": v(65, 78.8) * mm, "radius": 2.5 * mm, "construction": true});
            skPoint(sketch, "E4.4.10.7", {"position": v(66.25, 80.97) * mm});
            skPoint(sketch, "E4.5.10.7", {"position": v(69.5, 75.34) * mm});
            skLineSegment(sketch, "E4.6.10.7", {"start": v(68.25, 70.3) * mm, "end": v(65.75, 71.74) * mm});
            skLineSegment(sketch, "E4.9.10.7", {"start": v(70.75, 71.74) * mm, "end": v(68.25, 70.3) * mm});
            skLineSegment(sketch, "E4.12.10.7", {"start": v(70.75, 74.62) * mm, "end": v(70.75, 71.74) * mm});
            skLineSegment(sketch, "E4.15.10.7", {"start": v(68.25, 76.07) * mm, "end": v(70.75, 74.62) * mm});
            skLineSegment(sketch, "E4.18.10.7", {"start": v(62.5, 80.25) * mm, "end": v(65, 81.7) * mm});
            skLineSegment(sketch, "E4.21.10.7", {"start": v(62.5, 77.36) * mm, "end": v(62.5, 80.25) * mm});
            skLineSegment(sketch, "E4.24.10.7", {"start": v(65, 75.92) * mm, "end": v(62.5, 77.36) * mm});
            skLineSegment(sketch, "E4.27.10.7", {"start": v(67.5, 77.36) * mm, "end": v(65, 75.92) * mm});
            skLineSegment(sketch, "E4.30.10.7", {"start": v(67.5, 80.25) * mm, "end": v(67.5, 77.36) * mm});
            skLineSegment(sketch, "E4.33.10.7", {"start": v(65, 81.7) * mm, "end": v(67.5, 80.25) * mm});
            skLineSegment(sketch, "E4.36.10.7", {"start": v(65.75, 74.62) * mm, "end": v(68.25, 76.07) * mm});
            skLineSegment(sketch, "E4.39.10.7", {"start": v(65.75, 71.74) * mm, "end": v(65.75, 74.62) * mm});
            skCircle(sketch, "E4.0.10.8", {"center": v(68.25, 84.44) * mm, "radius": 2.5 * mm, "construction": true});
            skCircle(sketch, "E4.2.10.8", {"center": v(65, 90.07) * mm, "radius": 2.5 * mm, "construction": true});
            skPoint(sketch, "E4.4.10.8", {"position": v(66.25, 92.23) * mm});
            skPoint(sketch, "E4.5.10.8", {"position": v(69.5, 86.6) * mm});
            skLineSegment(sketch, "E4.6.10.8", {"start": v(68.25, 81.55) * mm, "end": v(65.75, 83) * mm});
            skLineSegment(sketch, "E4.9.10.8", {"start": v(70.75, 83) * mm, "end": v(68.25, 81.55) * mm});
            skLineSegment(sketch, "E4.12.10.8", {"start": v(70.75, 85.88) * mm, "end": v(70.75, 83) * mm});
            skLineSegment(sketch, "E4.15.10.8", {"start": v(68.25, 87.32) * mm, "end": v(70.75, 85.88) * mm});
            skLineSegment(sketch, "E4.18.10.8", {"start": v(62.5, 91.51) * mm, "end": v(65, 92.95) * mm});
            skLineSegment(sketch, "E4.21.10.8", {"start": v(62.5, 88.62) * mm, "end": v(62.5, 91.51) * mm});
            skLineSegment(sketch, "E4.24.10.8", {"start": v(65, 87.18) * mm, "end": v(62.5, 88.62) * mm});
            skLineSegment(sketch, "E4.27.10.8", {"start": v(67.5, 88.62) * mm, "end": v(65, 87.18) * mm});
            skLineSegment(sketch, "E4.30.10.8", {"start": v(67.5, 91.51) * mm, "end": v(67.5, 88.62) * mm});
            skLineSegment(sketch, "E4.33.10.8", {"start": v(65, 92.95) * mm, "end": v(67.5, 91.51) * mm});
            skLineSegment(sketch, "E4.36.10.8", {"start": v(65.75, 85.88) * mm, "end": v(68.25, 87.32) * mm});
            skLineSegment(sketch, "E4.39.10.8", {"start": v(65.75, 83) * mm, "end": v(65.75, 85.88) * mm});
            skCircle(sketch, "E4.0.10.9", {"center": v(68.25, 95.7) * mm, "radius": 2.5 * mm, "construction": true});
            skCircle(sketch, "E4.2.10.9", {"center": v(65, 101.32) * mm, "radius": 2.5 * mm, "construction": true});
            skPoint(sketch, "E4.4.10.9", {"position": v(66.25, 103.5) * mm});
            skPoint(sketch, "E4.5.10.9", {"position": v(69.5, 97.86) * mm});
            skLineSegment(sketch, "E4.6.10.9", {"start": v(68.25, 92.8) * mm, "end": v(65.75, 94.25) * mm});
            skLineSegment(sketch, "E4.9.10.9", {"start": v(70.75, 94.25) * mm, "end": v(68.25, 92.8) * mm});
            skLineSegment(sketch, "E4.12.10.9", {"start": v(70.75, 97.14) * mm, "end": v(70.75, 94.25) * mm});
            skLineSegment(sketch, "E4.15.10.9", {"start": v(68.25, 98.58) * mm, "end": v(70.75, 97.14) * mm});
            skLineSegment(sketch, "E4.18.10.9", {"start": v(62.5, 102.77) * mm, "end": v(65, 104.21) * mm});
            skLineSegment(sketch, "E4.21.10.9", {"start": v(62.5, 99.88) * mm, "end": v(62.5, 102.77) * mm});
            skLineSegment(sketch, "E4.24.10.9", {"start": v(65, 98.44) * mm, "end": v(62.5, 99.88) * mm});
            skLineSegment(sketch, "E4.27.10.9", {"start": v(67.5, 99.88) * mm, "end": v(65, 98.44) * mm});
            skLineSegment(sketch, "E4.30.10.9", {"start": v(67.5, 102.77) * mm, "end": v(67.5, 99.88) * mm});
            skLineSegment(sketch, "E4.33.10.9", {"start": v(65, 104.21) * mm, "end": v(67.5, 102.77) * mm});
            skLineSegment(sketch, "E4.36.10.9", {"start": v(65.75, 97.14) * mm, "end": v(68.25, 98.58) * mm});
            skLineSegment(sketch, "E4.39.10.9", {"start": v(65.75, 94.25) * mm, "end": v(65.75, 97.14) * mm});
            skCircle(sketch, "E4.0.11.0", {"center": v(74.75, -5.63) * mm, "radius": 2.5 * mm, "construction": true});
            skCircle(sketch, "E4.2.11.0", {"center": v(71.5, 0) * mm, "radius": 2.5 * mm, "construction": true});
            skPoint(sketch, "E4.4.11.0", {"position": v(72.75, 2.17) * mm});
            skPoint(sketch, "E4.5.11.0", {"position": v(76, -3.46) * mm});
            skLineSegment(sketch, "E4.6.11.0", {"start": v(74.75, -8.52) * mm, "end": v(72.25, -7.07) * mm});
            skLineSegment(sketch, "E4.9.11.0", {"start": v(77.25, -7.07) * mm, "end": v(74.75, -8.52) * mm});
            skLineSegment(sketch, "E4.12.11.0", {"start": v(77.25, -4.19) * mm, "end": v(77.25, -7.07) * mm});
            skLineSegment(sketch, "E4.15.11.0", {"start": v(74.75, -2.74) * mm, "end": v(77.25, -4.19) * mm});
            skLineSegment(sketch, "E4.18.11.0", {"start": v(69, 1.44) * mm, "end": v(71.5, 2.89) * mm});
            skLineSegment(sketch, "E4.21.11.0", {"start": v(69, -1.44) * mm, "end": v(69, 1.44) * mm});
            skLineSegment(sketch, "E4.24.11.0", {"start": v(71.5, -2.89) * mm, "end": v(69, -1.44) * mm});
            skLineSegment(sketch, "E4.27.11.0", {"start": v(74, -1.44) * mm, "end": v(71.5, -2.89) * mm});
            skLineSegment(sketch, "E4.30.11.0", {"start": v(74, 1.44) * mm, "end": v(74, -1.44) * mm});
            skLineSegment(sketch, "E4.33.11.0", {"start": v(71.5, 2.89) * mm, "end": v(74, 1.44) * mm});
            skLineSegment(sketch, "E4.36.11.0", {"start": v(72.25, -4.19) * mm, "end": v(74.75, -2.74) * mm});
            skLineSegment(sketch, "E4.39.11.0", {"start": v(72.25, -7.07) * mm, "end": v(72.25, -4.19) * mm});
            skCircle(sketch, "E4.0.11.1", {"center": v(74.75, 5.63) * mm, "radius": 2.5 * mm, "construction": true});
            skCircle(sketch, "E4.2.11.1", {"center": v(71.5, 11.26) * mm, "radius": 2.5 * mm, "construction": true});
            skPoint(sketch, "E4.4.11.1", {"position": v(72.75, 13.42) * mm});
            skPoint(sketch, "E4.5.11.1", {"position": v(76, 7.8) * mm});
            skLineSegment(sketch, "E4.6.11.1", {"start": v(74.75, 2.74) * mm, "end": v(72.25, 4.19) * mm});
            skLineSegment(sketch, "E4.9.11.1", {"start": v(77.25, 4.19) * mm, "end": v(74.75, 2.74) * mm});
            skLineSegment(sketch, "E4.12.11.1", {"start": v(77.25, 7.07) * mm, "end": v(77.25, 4.19) * mm});
            skLineSegment(sketch, "E4.15.11.1", {"start": v(74.75, 8.52) * mm, "end": v(77.25, 7.07) * mm});
            skLineSegment(sketch, "E4.18.11.1", {"start": v(69, 12.7) * mm, "end": v(71.5, 14.15) * mm});
            skLineSegment(sketch, "E4.21.11.1", {"start": v(69, 9.81) * mm, "end": v(69, 12.7) * mm});
            skLineSegment(sketch, "E4.24.11.1", {"start": v(71.5, 8.37) * mm, "end": v(69, 9.81) * mm});
            skLineSegment(sketch, "E4.27.11.1", {"start": v(74, 9.81) * mm, "end": v(71.5, 8.37) * mm});
            skLineSegment(sketch, "E4.30.11.1", {"start": v(74, 12.7) * mm, "end": v(74, 9.81) * mm});
            skLineSegment(sketch, "E4.33.11.1", {"start": v(71.5, 14.15) * mm, "end": v(74, 12.7) * mm});
            skLineSegment(sketch, "E4.36.11.1", {"start": v(72.25, 7.07) * mm, "end": v(74.75, 8.52) * mm});
            skLineSegment(sketch, "E4.39.11.1", {"start": v(72.25, 4.19) * mm, "end": v(72.25, 7.07) * mm});
            skCircle(sketch, "E4.0.11.2", {"center": v(74.75, 16.89) * mm, "radius": 2.5 * mm, "construction": true});
            skCircle(sketch, "E4.2.11.2", {"center": v(71.5, 22.52) * mm, "radius": 2.5 * mm, "construction": true});
            skPoint(sketch, "E4.4.11.2", {"position": v(72.75, 24.68) * mm});
            skPoint(sketch, "E4.5.11.2", {"position": v(76, 19.05) * mm});
            skLineSegment(sketch, "E4.6.11.2", {"start": v(74.75, 14) * mm, "end": v(72.25, 15.44) * mm});
            skLineSegment(sketch, "E4.9.11.2", {"start": v(77.25, 15.44) * mm, "end": v(74.75, 14) * mm});
            skLineSegment(sketch, "E4.12.11.2", {"start": v(77.25, 18.33) * mm, "end": v(77.25, 15.44) * mm});
            skLineSegment(sketch, "E4.15.11.2", {"start": v(74.75, 19.77) * mm, "end": v(77.25, 18.33) * mm});
            skLineSegment(sketch, "E4.18.11.2", {"start": v(69, 23.96) * mm, "end": v(71.5, 25.4) * mm});
            skLineSegment(sketch, "E4.21.11.2", {"start": v(69, 21.07) * mm, "end": v(69, 23.96) * mm});
            skLineSegment(sketch, "E4.24.11.2", {"start": v(71.5, 19.63) * mm, "end": v(69, 21.07) * mm});
            skLineSegment(sketch, "E4.27.11.2", {"start": v(74, 21.07) * mm, "end": v(71.5, 19.63) * mm});
            skLineSegment(sketch, "E4.30.11.2", {"start": v(74, 23.96) * mm, "end": v(74, 21.07) * mm});
            skLineSegment(sketch, "E4.33.11.2", {"start": v(71.5, 25.4) * mm, "end": v(74, 23.96) * mm});
            skLineSegment(sketch, "E4.36.11.2", {"start": v(72.25, 18.33) * mm, "end": v(74.75, 19.77) * mm});
            skLineSegment(sketch, "E4.39.11.2", {"start": v(72.25, 15.44) * mm, "end": v(72.25, 18.33) * mm});
            skCircle(sketch, "E4.0.11.3", {"center": v(74.75, 28.15) * mm, "radius": 2.5 * mm, "construction": true});
            skCircle(sketch, "E4.2.11.3", {"center": v(71.5, 33.77) * mm, "radius": 2.5 * mm, "construction": true});
            skPoint(sketch, "E4.4.11.3", {"position": v(72.75, 35.94) * mm});
            skPoint(sketch, "E4.5.11.3", {"position": v(76, 30.31) * mm});
            skLineSegment(sketch, "E4.6.11.3", {"start": v(74.75, 25.26) * mm, "end": v(72.25, 26.7) * mm});
            skLineSegment(sketch, "E4.9.11.3", {"start": v(77.25, 26.7) * mm, "end": v(74.75, 25.26) * mm});
            skLineSegment(sketch, "E4.12.11.3", {"start": v(77.25, 29.59) * mm, "end": v(77.25, 26.7) * mm});
            skLineSegment(sketch, "E4.15.11.3", {"start": v(74.75, 31.03) * mm, "end": v(77.25, 29.59) * mm});
            skLineSegment(sketch, "E4.18.11.3", {"start": v(69, 35.22) * mm, "end": v(71.5, 36.66) * mm});
            skLineSegment(sketch, "E4.21.11.3", {"start": v(69, 32.33) * mm, "end": v(69, 35.22) * mm});
            skLineSegment(sketch, "E4.24.11.3", {"start": v(71.5, 30.89) * mm, "end": v(69, 32.33) * mm});
            skLineSegment(sketch, "E4.27.11.3", {"start": v(74, 32.33) * mm, "end": v(71.5, 30.89) * mm});
            skLineSegment(sketch, "E4.30.11.3", {"start": v(74, 35.22) * mm, "end": v(74, 32.33) * mm});
            skLineSegment(sketch, "E4.33.11.3", {"start": v(71.5, 36.66) * mm, "end": v(74, 35.22) * mm});
            skLineSegment(sketch, "E4.36.11.3", {"start": v(72.25, 29.59) * mm, "end": v(74.75, 31.03) * mm});
            skLineSegment(sketch, "E4.39.11.3", {"start": v(72.25, 26.7) * mm, "end": v(72.25, 29.59) * mm});
            skCircle(sketch, "E4.0.11.4", {"center": v(74.75, 39.4) * mm, "radius": 2.5 * mm, "construction": true});
            skCircle(sketch, "E4.2.11.4", {"center": v(71.5, 45.03) * mm, "radius": 2.5 * mm, "construction": true});
            skPoint(sketch, "E4.4.11.4", {"position": v(72.75, 47.2) * mm});
            skPoint(sketch, "E4.5.11.4", {"position": v(76, 41.57) * mm});
            skLineSegment(sketch, "E4.6.11.4", {"start": v(74.75, 36.52) * mm, "end": v(72.25, 37.96) * mm});
            skLineSegment(sketch, "E4.9.11.4", {"start": v(77.25, 37.96) * mm, "end": v(74.75, 36.52) * mm});
            skLineSegment(sketch, "E4.12.11.4", {"start": v(77.25, 40.85) * mm, "end": v(77.25, 37.96) * mm});
            skLineSegment(sketch, "E4.15.11.4", {"start": v(74.75, 42.3) * mm, "end": v(77.25, 40.85) * mm});
            skLineSegment(sketch, "E4.18.11.4", {"start": v(69, 46.48) * mm, "end": v(71.5, 47.92) * mm});
            skLineSegment(sketch, "E4.21.11.4", {"start": v(69, 43.59) * mm, "end": v(69, 46.48) * mm});
            skLineSegment(sketch, "E4.24.11.4", {"start": v(71.5, 42.15) * mm, "end": v(69, 43.59) * mm});
            skLineSegment(sketch, "E4.27.11.4", {"start": v(74, 43.59) * mm, "end": v(71.5, 42.15) * mm});
            skLineSegment(sketch, "E4.30.11.4", {"start": v(74, 46.48) * mm, "end": v(74, 43.59) * mm});
            skLineSegment(sketch, "E4.33.11.4", {"start": v(71.5, 47.92) * mm, "end": v(74, 46.48) * mm});
            skLineSegment(sketch, "E4.36.11.4", {"start": v(72.25, 40.85) * mm, "end": v(74.75, 42.3) * mm});
            skLineSegment(sketch, "E4.39.11.4", {"start": v(72.25, 37.96) * mm, "end": v(72.25, 40.85) * mm});
            skCircle(sketch, "E4.0.11.5", {"center": v(74.75, 50.66) * mm, "radius": 2.5 * mm, "construction": true});
            skCircle(sketch, "E4.2.11.5", {"center": v(71.5, 56.3) * mm, "radius": 2.5 * mm, "construction": true});
            skPoint(sketch, "E4.4.11.5", {"position": v(72.75, 58.46) * mm});
            skPoint(sketch, "E4.5.11.5", {"position": v(76, 52.83) * mm});
            skLineSegment(sketch, "E4.6.11.5", {"start": v(74.75, 47.78) * mm, "end": v(72.25, 49.22) * mm});
            skLineSegment(sketch, "E4.9.11.5", {"start": v(77.25, 49.22) * mm, "end": v(74.75, 47.78) * mm});
            skLineSegment(sketch, "E4.12.11.5", {"start": v(77.25, 52.1) * mm, "end": v(77.25, 49.22) * mm});
            skLineSegment(sketch, "E4.15.11.5", {"start": v(74.75, 53.55) * mm, "end": v(77.25, 52.1) * mm});
            skLineSegment(sketch, "E4.18.11.5", {"start": v(69, 57.74) * mm, "end": v(71.5, 59.18) * mm});
            skLineSegment(sketch, "E4.21.11.5", {"start": v(69, 54.85) * mm, "end": v(69, 57.74) * mm});
            skLineSegment(sketch, "E4.24.11.5", {"start": v(71.5, 53.4) * mm, "end": v(69, 54.85) * mm});
            skLineSegment(sketch, "E4.27.11.5", {"start": v(74, 54.85) * mm, "end": v(71.5, 53.4) * mm});
            skLineSegment(sketch, "E4.30.11.5", {"start": v(74, 57.74) * mm, "end": v(74, 54.85) * mm});
            skLineSegment(sketch, "E4.33.11.5", {"start": v(71.5, 59.18) * mm, "end": v(74, 57.74) * mm});
            skLineSegment(sketch, "E4.36.11.5", {"start": v(72.25, 52.1) * mm, "end": v(74.75, 53.55) * mm});
            skLineSegment(sketch, "E4.39.11.5", {"start": v(72.25, 49.22) * mm, "end": v(72.25, 52.1) * mm});
            skCircle(sketch, "E4.0.11.6", {"center": v(74.75, 61.92) * mm, "radius": 2.5 * mm, "construction": true});
            skCircle(sketch, "E4.2.11.6", {"center": v(71.5, 67.55) * mm, "radius": 2.5 * mm, "construction": true});
            skPoint(sketch, "E4.4.11.6", {"position": v(72.75, 69.72) * mm});
            skPoint(sketch, "E4.5.11.6", {"position": v(76, 64.09) * mm});
            skLineSegment(sketch, "E4.6.11.6", {"start": v(74.75, 59.03) * mm, "end": v(72.25, 60.48) * mm});
            skLineSegment(sketch, "E4.9.11.6", {"start": v(77.25, 60.48) * mm, "end": v(74.75, 59.03) * mm});
            skLineSegment(sketch, "E4.12.11.6", {"start": v(77.25, 63.36) * mm, "end": v(77.25, 60.48) * mm});
            skLineSegment(sketch, "E4.15.11.6", {"start": v(74.75, 64.8) * mm, "end": v(77.25, 63.36) * mm});
            skLineSegment(sketch, "E4.18.11.6", {"start": v(69, 69) * mm, "end": v(71.5, 70.44) * mm});
            skLineSegment(sketch, "E4.21.11.6", {"start": v(69, 66.1) * mm, "end": v(69, 69) * mm});
            skLineSegment(sketch, "E4.24.11.6", {"start": v(71.5, 64.66) * mm, "end": v(69, 66.1) * mm});
            skLineSegment(sketch, "E4.27.11.6", {"start": v(74, 66.1) * mm, "end": v(71.5, 64.66) * mm});
            skLineSegment(sketch, "E4.30.11.6", {"start": v(74, 69) * mm, "end": v(74, 66.1) * mm});
            skLineSegment(sketch, "E4.33.11.6", {"start": v(71.5, 70.44) * mm, "end": v(74, 69) * mm});
            skLineSegment(sketch, "E4.36.11.6", {"start": v(72.25, 63.36) * mm, "end": v(74.75, 64.8) * mm});
            skLineSegment(sketch, "E4.39.11.6", {"start": v(72.25, 60.48) * mm, "end": v(72.25, 63.36) * mm});
            skCircle(sketch, "E4.0.11.7", {"center": v(74.75, 73.18) * mm, "radius": 2.5 * mm, "construction": true});
            skCircle(sketch, "E4.2.11.7", {"center": v(71.5, 78.8) * mm, "radius": 2.5 * mm, "construction": true});
            skPoint(sketch, "E4.4.11.7", {"position": v(72.75, 80.97) * mm});
            skPoint(sketch, "E4.5.11.7", {"position": v(76, 75.34) * mm});
            skLineSegment(sketch, "E4.6.11.7", {"start": v(74.75, 70.3) * mm, "end": v(72.25, 71.74) * mm});
            skLineSegment(sketch, "E4.9.11.7", {"start": v(77.25, 71.74) * mm, "end": v(74.75, 70.3) * mm});
            skLineSegment(sketch, "E4.12.11.7", {"start": v(77.25, 74.62) * mm, "end": v(77.25, 71.74) * mm});
            skLineSegment(sketch, "E4.15.11.7", {"start": v(74.75, 76.07) * mm, "end": v(77.25, 74.62) * mm});
            skLineSegment(sketch, "E4.18.11.7", {"start": v(69, 80.25) * mm, "end": v(71.5, 81.7) * mm});
            skLineSegment(sketch, "E4.21.11.7", {"start": v(69, 77.36) * mm, "end": v(69, 80.25) * mm});
            skLineSegment(sketch, "E4.24.11.7", {"start": v(71.5, 75.92) * mm, "end": v(69, 77.36) * mm});
            skLineSegment(sketch, "E4.27.11.7", {"start": v(74, 77.36) * mm, "end": v(71.5, 75.92) * mm});
            skLineSegment(sketch, "E4.30.11.7", {"start": v(74, 80.25) * mm, "end": v(74, 77.36) * mm});
            skLineSegment(sketch, "E4.33.11.7", {"start": v(71.5, 81.7) * mm, "end": v(74, 80.25) * mm});
            skLineSegment(sketch, "E4.36.11.7", {"start": v(72.25, 74.62) * mm, "end": v(74.75, 76.07) * mm});
            skLineSegment(sketch, "E4.39.11.7", {"start": v(72.25, 71.74) * mm, "end": v(72.25, 74.62) * mm});
            skCircle(sketch, "E4.0.11.8", {"center": v(74.75, 84.44) * mm, "radius": 2.5 * mm, "construction": true});
            skCircle(sketch, "E4.2.11.8", {"center": v(71.5, 90.07) * mm, "radius": 2.5 * mm, "construction": true});
            skPoint(sketch, "E4.4.11.8", {"position": v(72.75, 92.23) * mm});
            skPoint(sketch, "E4.5.11.8", {"position": v(76, 86.6) * mm});
            skLineSegment(sketch, "E4.6.11.8", {"start": v(74.75, 81.55) * mm, "end": v(72.25, 83) * mm});
            skLineSegment(sketch, "E4.9.11.8", {"start": v(77.25, 83) * mm, "end": v(74.75, 81.55) * mm});
            skLineSegment(sketch, "E4.12.11.8", {"start": v(77.25, 85.88) * mm, "end": v(77.25, 83) * mm});
            skLineSegment(sketch, "E4.15.11.8", {"start": v(74.75, 87.32) * mm, "end": v(77.25, 85.88) * mm});
            skLineSegment(sketch, "E4.18.11.8", {"start": v(69, 91.51) * mm, "end": v(71.5, 92.95) * mm});
            skLineSegment(sketch, "E4.21.11.8", {"start": v(69, 88.62) * mm, "end": v(69, 91.51) * mm});
            skLineSegment(sketch, "E4.24.11.8", {"start": v(71.5, 87.18) * mm, "end": v(69, 88.62) * mm});
            skLineSegment(sketch, "E4.27.11.8", {"start": v(74, 88.62) * mm, "end": v(71.5, 87.18) * mm});
            skLineSegment(sketch, "E4.30.11.8", {"start": v(74, 91.51) * mm, "end": v(74, 88.62) * mm});
            skLineSegment(sketch, "E4.33.11.8", {"start": v(71.5, 92.95) * mm, "end": v(74, 91.51) * mm});
            skLineSegment(sketch, "E4.36.11.8", {"start": v(72.25, 85.88) * mm, "end": v(74.75, 87.32) * mm});
            skLineSegment(sketch, "E4.39.11.8", {"start": v(72.25, 83) * mm, "end": v(72.25, 85.88) * mm});
            skCircle(sketch, "E4.0.11.9", {"center": v(74.75, 95.7) * mm, "radius": 2.5 * mm, "construction": true});
            skCircle(sketch, "E4.2.11.9", {"center": v(71.5, 101.32) * mm, "radius": 2.5 * mm, "construction": true});
            skPoint(sketch, "E4.4.11.9", {"position": v(72.75, 103.5) * mm});
            skPoint(sketch, "E4.5.11.9", {"position": v(76, 97.86) * mm});
            skLineSegment(sketch, "E4.6.11.9", {"start": v(74.75, 92.8) * mm, "end": v(72.25, 94.25) * mm});
            skLineSegment(sketch, "E4.9.11.9", {"start": v(77.25, 94.25) * mm, "end": v(74.75, 92.8) * mm});
            skLineSegment(sketch, "E4.12.11.9", {"start": v(77.25, 97.14) * mm, "end": v(77.25, 94.25) * mm});
            skLineSegment(sketch, "E4.15.11.9", {"start": v(74.75, 98.58) * mm, "end": v(77.25, 97.14) * mm});
            skLineSegment(sketch, "E4.18.11.9", {"start": v(69, 102.77) * mm, "end": v(71.5, 104.21) * mm});
            skLineSegment(sketch, "E4.21.11.9", {"start": v(69, 99.88) * mm, "end": v(69, 102.77) * mm});
            skLineSegment(sketch, "E4.24.11.9", {"start": v(71.5, 98.44) * mm, "end": v(69, 99.88) * mm});
            skLineSegment(sketch, "E4.27.11.9", {"start": v(74, 99.88) * mm, "end": v(71.5, 98.44) * mm});
            skLineSegment(sketch, "E4.30.11.9", {"start": v(74, 102.77) * mm, "end": v(74, 99.88) * mm});
            skLineSegment(sketch, "E4.33.11.9", {"start": v(71.5, 104.21) * mm, "end": v(74, 102.77) * mm});
            skLineSegment(sketch, "E4.36.11.9", {"start": v(72.25, 97.14) * mm, "end": v(74.75, 98.58) * mm});
            skLineSegment(sketch, "E4.39.11.9", {"start": v(72.25, 94.25) * mm, "end": v(72.25, 97.14) * mm});
            skCircle(sketch, "E4.0.12.0", {"center": v(81.25, -5.63) * mm, "radius": 2.5 * mm, "construction": true});
            skCircle(sketch, "E4.2.12.0", {"center": v(78, 0) * mm, "radius": 2.5 * mm, "construction": true});
            skPoint(sketch, "E4.4.12.0", {"position": v(79.25, 2.17) * mm});
            skPoint(sketch, "E4.5.12.0", {"position": v(82.5, -3.46) * mm});
            skLineSegment(sketch, "E4.6.12.0", {"start": v(81.25, -8.52) * mm, "end": v(78.75, -7.07) * mm});
            skLineSegment(sketch, "E4.9.12.0", {"start": v(83.75, -7.07) * mm, "end": v(81.25, -8.52) * mm});
            skLineSegment(sketch, "E4.12.12.0", {"start": v(83.75, -4.19) * mm, "end": v(83.75, -7.07) * mm});
            skLineSegment(sketch, "E4.15.12.0", {"start": v(81.25, -2.74) * mm, "end": v(83.75, -4.19) * mm});
            skLineSegment(sketch, "E4.18.12.0", {"start": v(75.5, 1.44) * mm, "end": v(78, 2.89) * mm});
            skLineSegment(sketch, "E4.21.12.0", {"start": v(75.5, -1.44) * mm, "end": v(75.5, 1.44) * mm});
            skLineSegment(sketch, "E4.24.12.0", {"start": v(78, -2.89) * mm, "end": v(75.5, -1.44) * mm});
            skLineSegment(sketch, "E4.27.12.0", {"start": v(80.5, -1.44) * mm, "end": v(78, -2.89) * mm});
            skLineSegment(sketch, "E4.30.12.0", {"start": v(80.5, 1.44) * mm, "end": v(80.5, -1.44) * mm});
            skLineSegment(sketch, "E4.33.12.0", {"start": v(78, 2.89) * mm, "end": v(80.5, 1.44) * mm});
            skLineSegment(sketch, "E4.36.12.0", {"start": v(78.75, -4.19) * mm, "end": v(81.25, -2.74) * mm});
            skLineSegment(sketch, "E4.39.12.0", {"start": v(78.75, -7.07) * mm, "end": v(78.75, -4.19) * mm});
            skCircle(sketch, "E4.0.12.1", {"center": v(81.25, 5.63) * mm, "radius": 2.5 * mm, "construction": true});
            skCircle(sketch, "E4.2.12.1", {"center": v(78, 11.26) * mm, "radius": 2.5 * mm, "construction": true});
            skPoint(sketch, "E4.4.12.1", {"position": v(79.25, 13.42) * mm});
            skPoint(sketch, "E4.5.12.1", {"position": v(82.5, 7.8) * mm});
            skLineSegment(sketch, "E4.6.12.1", {"start": v(81.25, 2.74) * mm, "end": v(78.75, 4.19) * mm});
            skLineSegment(sketch, "E4.9.12.1", {"start": v(83.75, 4.19) * mm, "end": v(81.25, 2.74) * mm});
            skLineSegment(sketch, "E4.12.12.1", {"start": v(83.75, 7.07) * mm, "end": v(83.75, 4.19) * mm});
            skLineSegment(sketch, "E4.15.12.1", {"start": v(81.25, 8.52) * mm, "end": v(83.75, 7.07) * mm});
            skLineSegment(sketch, "E4.18.12.1", {"start": v(75.5, 12.7) * mm, "end": v(78, 14.15) * mm});
            skLineSegment(sketch, "E4.21.12.1", {"start": v(75.5, 9.81) * mm, "end": v(75.5, 12.7) * mm});
            skLineSegment(sketch, "E4.24.12.1", {"start": v(78, 8.37) * mm, "end": v(75.5, 9.81) * mm});
            skLineSegment(sketch, "E4.27.12.1", {"start": v(80.5, 9.81) * mm, "end": v(78, 8.37) * mm});
            skLineSegment(sketch, "E4.30.12.1", {"start": v(80.5, 12.7) * mm, "end": v(80.5, 9.81) * mm});
            skLineSegment(sketch, "E4.33.12.1", {"start": v(78, 14.15) * mm, "end": v(80.5, 12.7) * mm});
            skLineSegment(sketch, "E4.36.12.1", {"start": v(78.75, 7.07) * mm, "end": v(81.25, 8.52) * mm});
            skLineSegment(sketch, "E4.39.12.1", {"start": v(78.75, 4.19) * mm, "end": v(78.75, 7.07) * mm});
            skCircle(sketch, "E4.0.12.2", {"center": v(81.25, 16.89) * mm, "radius": 2.5 * mm, "construction": true});
            skCircle(sketch, "E4.2.12.2", {"center": v(78, 22.52) * mm, "radius": 2.5 * mm, "construction": true});
            skPoint(sketch, "E4.4.12.2", {"position": v(79.25, 24.68) * mm});
            skPoint(sketch, "E4.5.12.2", {"position": v(82.5, 19.05) * mm});
            skLineSegment(sketch, "E4.6.12.2", {"start": v(81.25, 14) * mm, "end": v(78.75, 15.44) * mm});
            skLineSegment(sketch, "E4.9.12.2", {"start": v(83.75, 15.44) * mm, "end": v(81.25, 14) * mm});
            skLineSegment(sketch, "E4.12.12.2", {"start": v(83.75, 18.33) * mm, "end": v(83.75, 15.44) * mm});
            skLineSegment(sketch, "E4.15.12.2", {"start": v(81.25, 19.77) * mm, "end": v(83.75, 18.33) * mm});
            skLineSegment(sketch, "E4.18.12.2", {"start": v(75.5, 23.96) * mm, "end": v(78, 25.4) * mm});
            skLineSegment(sketch, "E4.21.12.2", {"start": v(75.5, 21.07) * mm, "end": v(75.5, 23.96) * mm});
            skLineSegment(sketch, "E4.24.12.2", {"start": v(78, 19.63) * mm, "end": v(75.5, 21.07) * mm});
            skLineSegment(sketch, "E4.27.12.2", {"start": v(80.5, 21.07) * mm, "end": v(78, 19.63) * mm});
            skLineSegment(sketch, "E4.30.12.2", {"start": v(80.5, 23.96) * mm, "end": v(80.5, 21.07) * mm});
            skLineSegment(sketch, "E4.33.12.2", {"start": v(78, 25.4) * mm, "end": v(80.5, 23.96) * mm});
            skLineSegment(sketch, "E4.36.12.2", {"start": v(78.75, 18.33) * mm, "end": v(81.25, 19.77) * mm});
            skLineSegment(sketch, "E4.39.12.2", {"start": v(78.75, 15.44) * mm, "end": v(78.75, 18.33) * mm});
            skCircle(sketch, "E4.0.12.3", {"center": v(81.25, 28.15) * mm, "radius": 2.5 * mm, "construction": true});
            skCircle(sketch, "E4.2.12.3", {"center": v(78, 33.77) * mm, "radius": 2.5 * mm, "construction": true});
            skPoint(sketch, "E4.4.12.3", {"position": v(79.25, 35.94) * mm});
            skPoint(sketch, "E4.5.12.3", {"position": v(82.5, 30.31) * mm});
            skLineSegment(sketch, "E4.6.12.3", {"start": v(81.25, 25.26) * mm, "end": v(78.75, 26.7) * mm});
            skLineSegment(sketch, "E4.9.12.3", {"start": v(83.75, 26.7) * mm, "end": v(81.25, 25.26) * mm});
            skLineSegment(sketch, "E4.12.12.3", {"start": v(83.75, 29.59) * mm, "end": v(83.75, 26.7) * mm});
            skLineSegment(sketch, "E4.15.12.3", {"start": v(81.25, 31.03) * mm, "end": v(83.75, 29.59) * mm});
            skLineSegment(sketch, "E4.18.12.3", {"start": v(75.5, 35.22) * mm, "end": v(78, 36.66) * mm});
            skLineSegment(sketch, "E4.21.12.3", {"start": v(75.5, 32.33) * mm, "end": v(75.5, 35.22) * mm});
            skLineSegment(sketch, "E4.24.12.3", {"start": v(78, 30.89) * mm, "end": v(75.5, 32.33) * mm});
            skLineSegment(sketch, "E4.27.12.3", {"start": v(80.5, 32.33) * mm, "end": v(78, 30.89) * mm});
            skLineSegment(sketch, "E4.30.12.3", {"start": v(80.5, 35.22) * mm, "end": v(80.5, 32.33) * mm});
            skLineSegment(sketch, "E4.33.12.3", {"start": v(78, 36.66) * mm, "end": v(80.5, 35.22) * mm});
            skLineSegment(sketch, "E4.36.12.3", {"start": v(78.75, 29.59) * mm, "end": v(81.25, 31.03) * mm});
            skLineSegment(sketch, "E4.39.12.3", {"start": v(78.75, 26.7) * mm, "end": v(78.75, 29.59) * mm});
            skCircle(sketch, "E4.0.12.4", {"center": v(81.25, 39.4) * mm, "radius": 2.5 * mm, "construction": true});
            skCircle(sketch, "E4.2.12.4", {"center": v(78, 45.03) * mm, "radius": 2.5 * mm, "construction": true});
            skPoint(sketch, "E4.4.12.4", {"position": v(79.25, 47.2) * mm});
            skPoint(sketch, "E4.5.12.4", {"position": v(82.5, 41.57) * mm});
            skLineSegment(sketch, "E4.6.12.4", {"start": v(81.25, 36.52) * mm, "end": v(78.75, 37.96) * mm});
            skLineSegment(sketch, "E4.9.12.4", {"start": v(83.75, 37.96) * mm, "end": v(81.25, 36.52) * mm});
            skLineSegment(sketch, "E4.12.12.4", {"start": v(83.75, 40.85) * mm, "end": v(83.75, 37.96) * mm});
            skLineSegment(sketch, "E4.15.12.4", {"start": v(81.25, 42.3) * mm, "end": v(83.75, 40.85) * mm});
            skLineSegment(sketch, "E4.18.12.4", {"start": v(75.5, 46.48) * mm, "end": v(78, 47.92) * mm});
            skLineSegment(sketch, "E4.21.12.4", {"start": v(75.5, 43.59) * mm, "end": v(75.5, 46.48) * mm});
            skLineSegment(sketch, "E4.24.12.4", {"start": v(78, 42.15) * mm, "end": v(75.5, 43.59) * mm});
            skLineSegment(sketch, "E4.27.12.4", {"start": v(80.5, 43.59) * mm, "end": v(78, 42.15) * mm});
            skLineSegment(sketch, "E4.30.12.4", {"start": v(80.5, 46.48) * mm, "end": v(80.5, 43.59) * mm});
            skLineSegment(sketch, "E4.33.12.4", {"start": v(78, 47.92) * mm, "end": v(80.5, 46.48) * mm});
            skLineSegment(sketch, "E4.36.12.4", {"start": v(78.75, 40.85) * mm, "end": v(81.25, 42.3) * mm});
            skLineSegment(sketch, "E4.39.12.4", {"start": v(78.75, 37.96) * mm, "end": v(78.75, 40.85) * mm});
            skCircle(sketch, "E4.0.12.5", {"center": v(81.25, 50.66) * mm, "radius": 2.5 * mm, "construction": true});
            skCircle(sketch, "E4.2.12.5", {"center": v(78, 56.3) * mm, "radius": 2.5 * mm, "construction": true});
            skPoint(sketch, "E4.4.12.5", {"position": v(79.25, 58.46) * mm});
            skPoint(sketch, "E4.5.12.5", {"position": v(82.5, 52.83) * mm});
            skLineSegment(sketch, "E4.6.12.5", {"start": v(81.25, 47.78) * mm, "end": v(78.75, 49.22) * mm});
            skLineSegment(sketch, "E4.9.12.5", {"start": v(83.75, 49.22) * mm, "end": v(81.25, 47.78) * mm});
            skLineSegment(sketch, "E4.12.12.5", {"start": v(83.75, 52.1) * mm, "end": v(83.75, 49.22) * mm});
            skLineSegment(sketch, "E4.15.12.5", {"start": v(81.25, 53.55) * mm, "end": v(83.75, 52.1) * mm});
            skLineSegment(sketch, "E4.18.12.5", {"start": v(75.5, 57.74) * mm, "end": v(78, 59.18) * mm});
            skLineSegment(sketch, "E4.21.12.5", {"start": v(75.5, 54.85) * mm, "end": v(75.5, 57.74) * mm});
            skLineSegment(sketch, "E4.24.12.5", {"start": v(78, 53.4) * mm, "end": v(75.5, 54.85) * mm});
            skLineSegment(sketch, "E4.27.12.5", {"start": v(80.5, 54.85) * mm, "end": v(78, 53.4) * mm});
            skLineSegment(sketch, "E4.30.12.5", {"start": v(80.5, 57.74) * mm, "end": v(80.5, 54.85) * mm});
            skLineSegment(sketch, "E4.33.12.5", {"start": v(78, 59.18) * mm, "end": v(80.5, 57.74) * mm});
            skLineSegment(sketch, "E4.36.12.5", {"start": v(78.75, 52.1) * mm, "end": v(81.25, 53.55) * mm});
            skLineSegment(sketch, "E4.39.12.5", {"start": v(78.75, 49.22) * mm, "end": v(78.75, 52.1) * mm});
            skCircle(sketch, "E4.0.12.6", {"center": v(81.25, 61.92) * mm, "radius": 2.5 * mm, "construction": true});
            skCircle(sketch, "E4.2.12.6", {"center": v(78, 67.55) * mm, "radius": 2.5 * mm, "construction": true});
            skPoint(sketch, "E4.4.12.6", {"position": v(79.25, 69.72) * mm});
            skPoint(sketch, "E4.5.12.6", {"position": v(82.5, 64.09) * mm});
            skLineSegment(sketch, "E4.6.12.6", {"start": v(81.25, 59.03) * mm, "end": v(78.75, 60.48) * mm});
            skLineSegment(sketch, "E4.9.12.6", {"start": v(83.75, 60.48) * mm, "end": v(81.25, 59.03) * mm});
            skLineSegment(sketch, "E4.12.12.6", {"start": v(83.75, 63.36) * mm, "end": v(83.75, 60.48) * mm});
            skLineSegment(sketch, "E4.15.12.6", {"start": v(81.25, 64.8) * mm, "end": v(83.75, 63.36) * mm});
            skLineSegment(sketch, "E4.18.12.6", {"start": v(75.5, 69) * mm, "end": v(78, 70.44) * mm});
            skLineSegment(sketch, "E4.21.12.6", {"start": v(75.5, 66.1) * mm, "end": v(75.5, 69) * mm});
            skLineSegment(sketch, "E4.24.12.6", {"start": v(78, 64.66) * mm, "end": v(75.5, 66.1) * mm});
            skLineSegment(sketch, "E4.27.12.6", {"start": v(80.5, 66.1) * mm, "end": v(78, 64.66) * mm});
            skLineSegment(sketch, "E4.30.12.6", {"start": v(80.5, 69) * mm, "end": v(80.5, 66.1) * mm});
            skLineSegment(sketch, "E4.33.12.6", {"start": v(78, 70.44) * mm, "end": v(80.5, 69) * mm});
            skLineSegment(sketch, "E4.36.12.6", {"start": v(78.75, 63.36) * mm, "end": v(81.25, 64.8) * mm});
            skLineSegment(sketch, "E4.39.12.6", {"start": v(78.75, 60.48) * mm, "end": v(78.75, 63.36) * mm});
            skCircle(sketch, "E4.0.12.7", {"center": v(81.25, 73.18) * mm, "radius": 2.5 * mm, "construction": true});
            skCircle(sketch, "E4.2.12.7", {"center": v(78, 78.8) * mm, "radius": 2.5 * mm, "construction": true});
            skPoint(sketch, "E4.4.12.7", {"position": v(79.25, 80.97) * mm});
            skPoint(sketch, "E4.5.12.7", {"position": v(82.5, 75.34) * mm});
            skLineSegment(sketch, "E4.6.12.7", {"start": v(81.25, 70.3) * mm, "end": v(78.75, 71.74) * mm});
            skLineSegment(sketch, "E4.9.12.7", {"start": v(83.75, 71.74) * mm, "end": v(81.25, 70.3) * mm});
            skLineSegment(sketch, "E4.12.12.7", {"start": v(83.75, 74.62) * mm, "end": v(83.75, 71.74) * mm});
            skLineSegment(sketch, "E4.15.12.7", {"start": v(81.25, 76.07) * mm, "end": v(83.75, 74.62) * mm});
            skLineSegment(sketch, "E4.18.12.7", {"start": v(75.5, 80.25) * mm, "end": v(78, 81.7) * mm});
            skLineSegment(sketch, "E4.21.12.7", {"start": v(75.5, 77.36) * mm, "end": v(75.5, 80.25) * mm});
            skLineSegment(sketch, "E4.24.12.7", {"start": v(78, 75.92) * mm, "end": v(75.5, 77.36) * mm});
            skLineSegment(sketch, "E4.27.12.7", {"start": v(80.5, 77.36) * mm, "end": v(78, 75.92) * mm});
            skLineSegment(sketch, "E4.30.12.7", {"start": v(80.5, 80.25) * mm, "end": v(80.5, 77.36) * mm});
            skLineSegment(sketch, "E4.33.12.7", {"start": v(78, 81.7) * mm, "end": v(80.5, 80.25) * mm});
            skLineSegment(sketch, "E4.36.12.7", {"start": v(78.75, 74.62) * mm, "end": v(81.25, 76.07) * mm});
            skLineSegment(sketch, "E4.39.12.7", {"start": v(78.75, 71.74) * mm, "end": v(78.75, 74.62) * mm});
            skCircle(sketch, "E4.0.12.8", {"center": v(81.25, 84.44) * mm, "radius": 2.5 * mm, "construction": true});
            skCircle(sketch, "E4.2.12.8", {"center": v(78, 90.07) * mm, "radius": 2.5 * mm, "construction": true});
            skPoint(sketch, "E4.4.12.8", {"position": v(79.25, 92.23) * mm});
            skPoint(sketch, "E4.5.12.8", {"position": v(82.5, 86.6) * mm});
            skLineSegment(sketch, "E4.6.12.8", {"start": v(81.25, 81.55) * mm, "end": v(78.75, 83) * mm});
            skLineSegment(sketch, "E4.9.12.8", {"start": v(83.75, 83) * mm, "end": v(81.25, 81.55) * mm});
            skLineSegment(sketch, "E4.12.12.8", {"start": v(83.75, 85.88) * mm, "end": v(83.75, 83) * mm});
            skLineSegment(sketch, "E4.15.12.8", {"start": v(81.25, 87.32) * mm, "end": v(83.75, 85.88) * mm});
            skLineSegment(sketch, "E4.18.12.8", {"start": v(75.5, 91.51) * mm, "end": v(78, 92.95) * mm});
            skLineSegment(sketch, "E4.21.12.8", {"start": v(75.5, 88.62) * mm, "end": v(75.5, 91.51) * mm});
            skLineSegment(sketch, "E4.24.12.8", {"start": v(78, 87.18) * mm, "end": v(75.5, 88.62) * mm});
            skLineSegment(sketch, "E4.27.12.8", {"start": v(80.5, 88.62) * mm, "end": v(78, 87.18) * mm});
            skLineSegment(sketch, "E4.30.12.8", {"start": v(80.5, 91.51) * mm, "end": v(80.5, 88.62) * mm});
            skLineSegment(sketch, "E4.33.12.8", {"start": v(78, 92.95) * mm, "end": v(80.5, 91.51) * mm});
            skLineSegment(sketch, "E4.36.12.8", {"start": v(78.75, 85.88) * mm, "end": v(81.25, 87.32) * mm});
            skLineSegment(sketch, "E4.39.12.8", {"start": v(78.75, 83) * mm, "end": v(78.75, 85.88) * mm});
            skCircle(sketch, "E4.0.12.9", {"center": v(81.25, 95.7) * mm, "radius": 2.5 * mm, "construction": true});
            skCircle(sketch, "E4.2.12.9", {"center": v(78, 101.32) * mm, "radius": 2.5 * mm, "construction": true});
            skPoint(sketch, "E4.4.12.9", {"position": v(79.25, 103.5) * mm});
            skPoint(sketch, "E4.5.12.9", {"position": v(82.5, 97.86) * mm});
            skLineSegment(sketch, "E4.6.12.9", {"start": v(81.25, 92.8) * mm, "end": v(78.75, 94.25) * mm});
            skLineSegment(sketch, "E4.9.12.9", {"start": v(83.75, 94.25) * mm, "end": v(81.25, 92.8) * mm});
            skLineSegment(sketch, "E4.12.12.9", {"start": v(83.75, 97.14) * mm, "end": v(83.75, 94.25) * mm});
            skLineSegment(sketch, "E4.15.12.9", {"start": v(81.25, 98.58) * mm, "end": v(83.75, 97.14) * mm});
            skLineSegment(sketch, "E4.18.12.9", {"start": v(75.5, 102.77) * mm, "end": v(78, 104.21) * mm});
            skLineSegment(sketch, "E4.21.12.9", {"start": v(75.5, 99.88) * mm, "end": v(75.5, 102.77) * mm});
            skLineSegment(sketch, "E4.24.12.9", {"start": v(78, 98.44) * mm, "end": v(75.5, 99.88) * mm});
            skLineSegment(sketch, "E4.27.12.9", {"start": v(80.5, 99.88) * mm, "end": v(78, 98.44) * mm});
            skLineSegment(sketch, "E4.30.12.9", {"start": v(80.5, 102.77) * mm, "end": v(80.5, 99.88) * mm});
            skLineSegment(sketch, "E4.33.12.9", {"start": v(78, 104.21) * mm, "end": v(80.5, 102.77) * mm});
            skLineSegment(sketch, "E4.36.12.9", {"start": v(78.75, 97.14) * mm, "end": v(81.25, 98.58) * mm});
            skLineSegment(sketch, "E4.39.12.9", {"start": v(78.75, 94.25) * mm, "end": v(78.75, 97.14) * mm});
            skCircle(sketch, "E4.0.13.0", {"center": v(87.75, -5.63) * mm, "radius": 2.5 * mm, "construction": true});
            skCircle(sketch, "E4.2.13.0", {"center": v(84.5, 0) * mm, "radius": 2.5 * mm, "construction": true});
            skPoint(sketch, "E4.4.13.0", {"position": v(85.75, 2.17) * mm});
            skPoint(sketch, "E4.5.13.0", {"position": v(89, -3.46) * mm});
            skLineSegment(sketch, "E4.6.13.0", {"start": v(87.75, -8.52) * mm, "end": v(85.25, -7.07) * mm});
            skLineSegment(sketch, "E4.9.13.0", {"start": v(90.25, -7.07) * mm, "end": v(87.75, -8.52) * mm});
            skLineSegment(sketch, "E4.12.13.0", {"start": v(90.25, -4.19) * mm, "end": v(90.25, -7.07) * mm});
            skLineSegment(sketch, "E4.15.13.0", {"start": v(87.75, -2.74) * mm, "end": v(90.25, -4.19) * mm});
            skLineSegment(sketch, "E4.18.13.0", {"start": v(82, 1.44) * mm, "end": v(84.5, 2.89) * mm});
            skLineSegment(sketch, "E4.21.13.0", {"start": v(82, -1.44) * mm, "end": v(82, 1.44) * mm});
            skLineSegment(sketch, "E4.24.13.0", {"start": v(84.5, -2.89) * mm, "end": v(82, -1.44) * mm});
            skLineSegment(sketch, "E4.27.13.0", {"start": v(87, -1.44) * mm, "end": v(84.5, -2.89) * mm});
            skLineSegment(sketch, "E4.30.13.0", {"start": v(87, 1.44) * mm, "end": v(87, -1.44) * mm});
            skLineSegment(sketch, "E4.33.13.0", {"start": v(84.5, 2.89) * mm, "end": v(87, 1.44) * mm});
            skLineSegment(sketch, "E4.36.13.0", {"start": v(85.25, -4.19) * mm, "end": v(87.75, -2.74) * mm});
            skLineSegment(sketch, "E4.39.13.0", {"start": v(85.25, -7.07) * mm, "end": v(85.25, -4.19) * mm});
            skCircle(sketch, "E4.0.13.1", {"center": v(87.75, 5.63) * mm, "radius": 2.5 * mm, "construction": true});
            skCircle(sketch, "E4.2.13.1", {"center": v(84.5, 11.26) * mm, "radius": 2.5 * mm, "construction": true});
            skPoint(sketch, "E4.4.13.1", {"position": v(85.75, 13.42) * mm});
            skPoint(sketch, "E4.5.13.1", {"position": v(89, 7.8) * mm});
            skLineSegment(sketch, "E4.6.13.1", {"start": v(87.75, 2.74) * mm, "end": v(85.25, 4.19) * mm});
            skLineSegment(sketch, "E4.9.13.1", {"start": v(90.25, 4.19) * mm, "end": v(87.75, 2.74) * mm});
            skLineSegment(sketch, "E4.12.13.1", {"start": v(90.25, 7.07) * mm, "end": v(90.25, 4.19) * mm});
            skLineSegment(sketch, "E4.15.13.1", {"start": v(87.75, 8.52) * mm, "end": v(90.25, 7.07) * mm});
            skLineSegment(sketch, "E4.18.13.1", {"start": v(82, 12.7) * mm, "end": v(84.5, 14.15) * mm});
            skLineSegment(sketch, "E4.21.13.1", {"start": v(82, 9.81) * mm, "end": v(82, 12.7) * mm});
            skLineSegment(sketch, "E4.24.13.1", {"start": v(84.5, 8.37) * mm, "end": v(82, 9.81) * mm});
            skLineSegment(sketch, "E4.27.13.1", {"start": v(87, 9.81) * mm, "end": v(84.5, 8.37) * mm});
            skLineSegment(sketch, "E4.30.13.1", {"start": v(87, 12.7) * mm, "end": v(87, 9.81) * mm});
            skLineSegment(sketch, "E4.33.13.1", {"start": v(84.5, 14.15) * mm, "end": v(87, 12.7) * mm});
            skLineSegment(sketch, "E4.36.13.1", {"start": v(85.25, 7.07) * mm, "end": v(87.75, 8.52) * mm});
            skLineSegment(sketch, "E4.39.13.1", {"start": v(85.25, 4.19) * mm, "end": v(85.25, 7.07) * mm});
            skCircle(sketch, "E4.0.13.2", {"center": v(87.75, 16.89) * mm, "radius": 2.5 * mm, "construction": true});
            skCircle(sketch, "E4.2.13.2", {"center": v(84.5, 22.52) * mm, "radius": 2.5 * mm, "construction": true});
            skPoint(sketch, "E4.4.13.2", {"position": v(85.75, 24.68) * mm});
            skPoint(sketch, "E4.5.13.2", {"position": v(89, 19.05) * mm});
            skLineSegment(sketch, "E4.6.13.2", {"start": v(87.75, 14) * mm, "end": v(85.25, 15.44) * mm});
            skLineSegment(sketch, "E4.9.13.2", {"start": v(90.25, 15.44) * mm, "end": v(87.75, 14) * mm});
            skLineSegment(sketch, "E4.12.13.2", {"start": v(90.25, 18.33) * mm, "end": v(90.25, 15.44) * mm});
            skLineSegment(sketch, "E4.15.13.2", {"start": v(87.75, 19.77) * mm, "end": v(90.25, 18.33) * mm});
            skLineSegment(sketch, "E4.18.13.2", {"start": v(82, 23.96) * mm, "end": v(84.5, 25.4) * mm});
            skLineSegment(sketch, "E4.21.13.2", {"start": v(82, 21.07) * mm, "end": v(82, 23.96) * mm});
            skLineSegment(sketch, "E4.24.13.2", {"start": v(84.5, 19.63) * mm, "end": v(82, 21.07) * mm});
            skLineSegment(sketch, "E4.27.13.2", {"start": v(87, 21.07) * mm, "end": v(84.5, 19.63) * mm});
            skLineSegment(sketch, "E4.30.13.2", {"start": v(87, 23.96) * mm, "end": v(87, 21.07) * mm});
            skLineSegment(sketch, "E4.33.13.2", {"start": v(84.5, 25.4) * mm, "end": v(87, 23.96) * mm});
            skLineSegment(sketch, "E4.36.13.2", {"start": v(85.25, 18.33) * mm, "end": v(87.75, 19.77) * mm});
            skLineSegment(sketch, "E4.39.13.2", {"start": v(85.25, 15.44) * mm, "end": v(85.25, 18.33) * mm});
            skCircle(sketch, "E4.0.13.3", {"center": v(87.75, 28.15) * mm, "radius": 2.5 * mm, "construction": true});
            skCircle(sketch, "E4.2.13.3", {"center": v(84.5, 33.77) * mm, "radius": 2.5 * mm, "construction": true});
            skPoint(sketch, "E4.4.13.3", {"position": v(85.75, 35.94) * mm});
            skPoint(sketch, "E4.5.13.3", {"position": v(89, 30.31) * mm});
            skLineSegment(sketch, "E4.6.13.3", {"start": v(87.75, 25.26) * mm, "end": v(85.25, 26.7) * mm});
            skLineSegment(sketch, "E4.9.13.3", {"start": v(90.25, 26.7) * mm, "end": v(87.75, 25.26) * mm});
            skLineSegment(sketch, "E4.12.13.3", {"start": v(90.25, 29.59) * mm, "end": v(90.25, 26.7) * mm});
            skLineSegment(sketch, "E4.15.13.3", {"start": v(87.75, 31.03) * mm, "end": v(90.25, 29.59) * mm});
            skLineSegment(sketch, "E4.18.13.3", {"start": v(82, 35.22) * mm, "end": v(84.5, 36.66) * mm});
            skLineSegment(sketch, "E4.21.13.3", {"start": v(82, 32.33) * mm, "end": v(82, 35.22) * mm});
            skLineSegment(sketch, "E4.24.13.3", {"start": v(84.5, 30.89) * mm, "end": v(82, 32.33) * mm});
            skLineSegment(sketch, "E4.27.13.3", {"start": v(87, 32.33) * mm, "end": v(84.5, 30.89) * mm});
            skLineSegment(sketch, "E4.30.13.3", {"start": v(87, 35.22) * mm, "end": v(87, 32.33) * mm});
            skLineSegment(sketch, "E4.33.13.3", {"start": v(84.5, 36.66) * mm, "end": v(87, 35.22) * mm});
            skLineSegment(sketch, "E4.36.13.3", {"start": v(85.25, 29.59) * mm, "end": v(87.75, 31.03) * mm});
            skLineSegment(sketch, "E4.39.13.3", {"start": v(85.25, 26.7) * mm, "end": v(85.25, 29.59) * mm});
            skCircle(sketch, "E4.0.13.4", {"center": v(87.75, 39.4) * mm, "radius": 2.5 * mm, "construction": true});
            skCircle(sketch, "E4.2.13.4", {"center": v(84.5, 45.03) * mm, "radius": 2.5 * mm, "construction": true});
            skPoint(sketch, "E4.4.13.4", {"position": v(85.75, 47.2) * mm});
            skPoint(sketch, "E4.5.13.4", {"position": v(89, 41.57) * mm});
            skLineSegment(sketch, "E4.6.13.4", {"start": v(87.75, 36.52) * mm, "end": v(85.25, 37.96) * mm});
            skLineSegment(sketch, "E4.9.13.4", {"start": v(90.25, 37.96) * mm, "end": v(87.75, 36.52) * mm});
            skLineSegment(sketch, "E4.12.13.4", {"start": v(90.25, 40.85) * mm, "end": v(90.25, 37.96) * mm});
            skLineSegment(sketch, "E4.15.13.4", {"start": v(87.75, 42.3) * mm, "end": v(90.25, 40.85) * mm});
            skLineSegment(sketch, "E4.18.13.4", {"start": v(82, 46.48) * mm, "end": v(84.5, 47.92) * mm});
            skLineSegment(sketch, "E4.21.13.4", {"start": v(82, 43.59) * mm, "end": v(82, 46.48) * mm});
            skLineSegment(sketch, "E4.24.13.4", {"start": v(84.5, 42.15) * mm, "end": v(82, 43.59) * mm});
            skLineSegment(sketch, "E4.27.13.4", {"start": v(87, 43.59) * mm, "end": v(84.5, 42.15) * mm});
            skLineSegment(sketch, "E4.30.13.4", {"start": v(87, 46.48) * mm, "end": v(87, 43.59) * mm});
            skLineSegment(sketch, "E4.33.13.4", {"start": v(84.5, 47.92) * mm, "end": v(87, 46.48) * mm});
            skLineSegment(sketch, "E4.36.13.4", {"start": v(85.25, 40.85) * mm, "end": v(87.75, 42.3) * mm});
            skLineSegment(sketch, "E4.39.13.4", {"start": v(85.25, 37.96) * mm, "end": v(85.25, 40.85) * mm});
            skCircle(sketch, "E4.0.13.5", {"center": v(87.75, 50.66) * mm, "radius": 2.5 * mm, "construction": true});
            skCircle(sketch, "E4.2.13.5", {"center": v(84.5, 56.3) * mm, "radius": 2.5 * mm, "construction": true});
            skPoint(sketch, "E4.4.13.5", {"position": v(85.75, 58.46) * mm});
            skPoint(sketch, "E4.5.13.5", {"position": v(89, 52.83) * mm});
            skLineSegment(sketch, "E4.6.13.5", {"start": v(87.75, 47.78) * mm, "end": v(85.25, 49.22) * mm});
            skLineSegment(sketch, "E4.9.13.5", {"start": v(90.25, 49.22) * mm, "end": v(87.75, 47.78) * mm});
            skLineSegment(sketch, "E4.12.13.5", {"start": v(90.25, 52.1) * mm, "end": v(90.25, 49.22) * mm});
            skLineSegment(sketch, "E4.15.13.5", {"start": v(87.75, 53.55) * mm, "end": v(90.25, 52.1) * mm});
            skLineSegment(sketch, "E4.18.13.5", {"start": v(82, 57.74) * mm, "end": v(84.5, 59.18) * mm});
            skLineSegment(sketch, "E4.21.13.5", {"start": v(82, 54.85) * mm, "end": v(82, 57.74) * mm});
            skLineSegment(sketch, "E4.24.13.5", {"start": v(84.5, 53.4) * mm, "end": v(82, 54.85) * mm});
            skLineSegment(sketch, "E4.27.13.5", {"start": v(87, 54.85) * mm, "end": v(84.5, 53.4) * mm});
            skLineSegment(sketch, "E4.30.13.5", {"start": v(87, 57.74) * mm, "end": v(87, 54.85) * mm});
            skLineSegment(sketch, "E4.33.13.5", {"start": v(84.5, 59.18) * mm, "end": v(87, 57.74) * mm});
            skLineSegment(sketch, "E4.36.13.5", {"start": v(85.25, 52.1) * mm, "end": v(87.75, 53.55) * mm});
            skLineSegment(sketch, "E4.39.13.5", {"start": v(85.25, 49.22) * mm, "end": v(85.25, 52.1) * mm});
            skCircle(sketch, "E4.0.13.6", {"center": v(87.75, 61.92) * mm, "radius": 2.5 * mm, "construction": true});
            skCircle(sketch, "E4.2.13.6", {"center": v(84.5, 67.55) * mm, "radius": 2.5 * mm, "construction": true});
            skPoint(sketch, "E4.4.13.6", {"position": v(85.75, 69.72) * mm});
            skPoint(sketch, "E4.5.13.6", {"position": v(89, 64.09) * mm});
            skLineSegment(sketch, "E4.6.13.6", {"start": v(87.75, 59.03) * mm, "end": v(85.25, 60.48) * mm});
            skLineSegment(sketch, "E4.9.13.6", {"start": v(90.25, 60.48) * mm, "end": v(87.75, 59.03) * mm});
            skLineSegment(sketch, "E4.12.13.6", {"start": v(90.25, 63.36) * mm, "end": v(90.25, 60.48) * mm});
            skLineSegment(sketch, "E4.15.13.6", {"start": v(87.75, 64.8) * mm, "end": v(90.25, 63.36) * mm});
            skLineSegment(sketch, "E4.18.13.6", {"start": v(82, 69) * mm, "end": v(84.5, 70.44) * mm});
            skLineSegment(sketch, "E4.21.13.6", {"start": v(82, 66.1) * mm, "end": v(82, 69) * mm});
            skLineSegment(sketch, "E4.24.13.6", {"start": v(84.5, 64.66) * mm, "end": v(82, 66.1) * mm});
            skLineSegment(sketch, "E4.27.13.6", {"start": v(87, 66.1) * mm, "end": v(84.5, 64.66) * mm});
            skLineSegment(sketch, "E4.30.13.6", {"start": v(87, 69) * mm, "end": v(87, 66.1) * mm});
            skLineSegment(sketch, "E4.33.13.6", {"start": v(84.5, 70.44) * mm, "end": v(87, 69) * mm});
            skLineSegment(sketch, "E4.36.13.6", {"start": v(85.25, 63.36) * mm, "end": v(87.75, 64.8) * mm});
            skLineSegment(sketch, "E4.39.13.6", {"start": v(85.25, 60.48) * mm, "end": v(85.25, 63.36) * mm});
            skCircle(sketch, "E4.0.13.7", {"center": v(87.75, 73.18) * mm, "radius": 2.5 * mm, "construction": true});
            skCircle(sketch, "E4.2.13.7", {"center": v(84.5, 78.8) * mm, "radius": 2.5 * mm, "construction": true});
            skPoint(sketch, "E4.4.13.7", {"position": v(85.75, 80.97) * mm});
            skPoint(sketch, "E4.5.13.7", {"position": v(89, 75.34) * mm});
            skLineSegment(sketch, "E4.6.13.7", {"start": v(87.75, 70.3) * mm, "end": v(85.25, 71.74) * mm});
            skLineSegment(sketch, "E4.9.13.7", {"start": v(90.25, 71.74) * mm, "end": v(87.75, 70.3) * mm});
            skLineSegment(sketch, "E4.12.13.7", {"start": v(90.25, 74.62) * mm, "end": v(90.25, 71.74) * mm});
            skLineSegment(sketch, "E4.15.13.7", {"start": v(87.75, 76.07) * mm, "end": v(90.25, 74.62) * mm});
            skLineSegment(sketch, "E4.18.13.7", {"start": v(82, 80.25) * mm, "end": v(84.5, 81.7) * mm});
            skLineSegment(sketch, "E4.21.13.7", {"start": v(82, 77.36) * mm, "end": v(82, 80.25) * mm});
            skLineSegment(sketch, "E4.24.13.7", {"start": v(84.5, 75.92) * mm, "end": v(82, 77.36) * mm});
            skLineSegment(sketch, "E4.27.13.7", {"start": v(87, 77.36) * mm, "end": v(84.5, 75.92) * mm});
            skLineSegment(sketch, "E4.30.13.7", {"start": v(87, 80.25) * mm, "end": v(87, 77.36) * mm});
            skLineSegment(sketch, "E4.33.13.7", {"start": v(84.5, 81.7) * mm, "end": v(87, 80.25) * mm});
            skLineSegment(sketch, "E4.36.13.7", {"start": v(85.25, 74.62) * mm, "end": v(87.75, 76.07) * mm});
            skLineSegment(sketch, "E4.39.13.7", {"start": v(85.25, 71.74) * mm, "end": v(85.25, 74.62) * mm});
            skCircle(sketch, "E4.0.13.8", {"center": v(87.75, 84.44) * mm, "radius": 2.5 * mm, "construction": true});
            skCircle(sketch, "E4.2.13.8", {"center": v(84.5, 90.07) * mm, "radius": 2.5 * mm, "construction": true});
            skPoint(sketch, "E4.4.13.8", {"position": v(85.75, 92.23) * mm});
            skPoint(sketch, "E4.5.13.8", {"position": v(89, 86.6) * mm});
            skLineSegment(sketch, "E4.6.13.8", {"start": v(87.75, 81.55) * mm, "end": v(85.25, 83) * mm});
            skLineSegment(sketch, "E4.9.13.8", {"start": v(90.25, 83) * mm, "end": v(87.75, 81.55) * mm});
            skLineSegment(sketch, "E4.12.13.8", {"start": v(90.25, 85.88) * mm, "end": v(90.25, 83) * mm});
            skLineSegment(sketch, "E4.15.13.8", {"start": v(87.75, 87.32) * mm, "end": v(90.25, 85.88) * mm});
            skLineSegment(sketch, "E4.18.13.8", {"start": v(82, 91.51) * mm, "end": v(84.5, 92.95) * mm});
            skLineSegment(sketch, "E4.21.13.8", {"start": v(82, 88.62) * mm, "end": v(82, 91.51) * mm});
            skLineSegment(sketch, "E4.24.13.8", {"start": v(84.5, 87.18) * mm, "end": v(82, 88.62) * mm});
            skLineSegment(sketch, "E4.27.13.8", {"start": v(87, 88.62) * mm, "end": v(84.5, 87.18) * mm});
            skLineSegment(sketch, "E4.30.13.8", {"start": v(87, 91.51) * mm, "end": v(87, 88.62) * mm});
            skLineSegment(sketch, "E4.33.13.8", {"start": v(84.5, 92.95) * mm, "end": v(87, 91.51) * mm});
            skLineSegment(sketch, "E4.36.13.8", {"start": v(85.25, 85.88) * mm, "end": v(87.75, 87.32) * mm});
            skLineSegment(sketch, "E4.39.13.8", {"start": v(85.25, 83) * mm, "end": v(85.25, 85.88) * mm});
            skCircle(sketch, "E4.0.13.9", {"center": v(87.75, 95.7) * mm, "radius": 2.5 * mm, "construction": true});
            skCircle(sketch, "E4.2.13.9", {"center": v(84.5, 101.32) * mm, "radius": 2.5 * mm, "construction": true});
            skPoint(sketch, "E4.4.13.9", {"position": v(85.75, 103.5) * mm});
            skPoint(sketch, "E4.5.13.9", {"position": v(89, 97.86) * mm});
            skLineSegment(sketch, "E4.6.13.9", {"start": v(87.75, 92.8) * mm, "end": v(85.25, 94.25) * mm});
            skLineSegment(sketch, "E4.9.13.9", {"start": v(90.25, 94.25) * mm, "end": v(87.75, 92.8) * mm});
            skLineSegment(sketch, "E4.12.13.9", {"start": v(90.25, 97.14) * mm, "end": v(90.25, 94.25) * mm});
            skLineSegment(sketch, "E4.15.13.9", {"start": v(87.75, 98.58) * mm, "end": v(90.25, 97.14) * mm});
            skLineSegment(sketch, "E4.18.13.9", {"start": v(82, 102.77) * mm, "end": v(84.5, 104.21) * mm});
            skLineSegment(sketch, "E4.21.13.9", {"start": v(82, 99.88) * mm, "end": v(82, 102.77) * mm});
            skLineSegment(sketch, "E4.24.13.9", {"start": v(84.5, 98.44) * mm, "end": v(82, 99.88) * mm});
            skLineSegment(sketch, "E4.27.13.9", {"start": v(87, 99.88) * mm, "end": v(84.5, 98.44) * mm});
            skLineSegment(sketch, "E4.30.13.9", {"start": v(87, 102.77) * mm, "end": v(87, 99.88) * mm});
            skLineSegment(sketch, "E4.33.13.9", {"start": v(84.5, 104.21) * mm, "end": v(87, 102.77) * mm});
            skLineSegment(sketch, "E4.36.13.9", {"start": v(85.25, 97.14) * mm, "end": v(87.75, 98.58) * mm});
            skLineSegment(sketch, "E4.39.13.9", {"start": v(85.25, 94.25) * mm, "end": v(85.25, 97.14) * mm});
            skCircle(sketch, "E4.0.14.0", {"center": v(94.25, -5.63) * mm, "radius": 2.5 * mm, "construction": true});
            skCircle(sketch, "E4.2.14.0", {"center": v(91, 0) * mm, "radius": 2.5 * mm, "construction": true});
            skPoint(sketch, "E4.4.14.0", {"position": v(92.25, 2.17) * mm});
            skPoint(sketch, "E4.5.14.0", {"position": v(95.5, -3.46) * mm});
            skLineSegment(sketch, "E4.6.14.0", {"start": v(94.25, -8.52) * mm, "end": v(91.75, -7.07) * mm});
            skLineSegment(sketch, "E4.9.14.0", {"start": v(96.75, -7.07) * mm, "end": v(94.25, -8.52) * mm});
            skLineSegment(sketch, "E4.12.14.0", {"start": v(96.75, -4.19) * mm, "end": v(96.75, -7.07) * mm});
            skLineSegment(sketch, "E4.15.14.0", {"start": v(94.25, -2.74) * mm, "end": v(96.75, -4.19) * mm});
            skLineSegment(sketch, "E4.18.14.0", {"start": v(88.5, 1.44) * mm, "end": v(91, 2.89) * mm});
            skLineSegment(sketch, "E4.21.14.0", {"start": v(88.5, -1.44) * mm, "end": v(88.5, 1.44) * mm});
            skLineSegment(sketch, "E4.24.14.0", {"start": v(91, -2.89) * mm, "end": v(88.5, -1.44) * mm});
            skLineSegment(sketch, "E4.27.14.0", {"start": v(93.5, -1.44) * mm, "end": v(91, -2.89) * mm});
            skLineSegment(sketch, "E4.30.14.0", {"start": v(93.5, 1.44) * mm, "end": v(93.5, -1.44) * mm});
            skLineSegment(sketch, "E4.33.14.0", {"start": v(91, 2.89) * mm, "end": v(93.5, 1.44) * mm});
            skLineSegment(sketch, "E4.36.14.0", {"start": v(91.75, -4.19) * mm, "end": v(94.25, -2.74) * mm});
            skLineSegment(sketch, "E4.39.14.0", {"start": v(91.75, -7.07) * mm, "end": v(91.75, -4.19) * mm});
            skCircle(sketch, "E4.0.14.1", {"center": v(94.25, 5.63) * mm, "radius": 2.5 * mm, "construction": true});
            skCircle(sketch, "E4.2.14.1", {"center": v(91, 11.26) * mm, "radius": 2.5 * mm, "construction": true});
            skPoint(sketch, "E4.4.14.1", {"position": v(92.25, 13.42) * mm});
            skPoint(sketch, "E4.5.14.1", {"position": v(95.5, 7.8) * mm});
            skLineSegment(sketch, "E4.6.14.1", {"start": v(94.25, 2.74) * mm, "end": v(91.75, 4.19) * mm});
            skLineSegment(sketch, "E4.9.14.1", {"start": v(96.75, 4.19) * mm, "end": v(94.25, 2.74) * mm});
            skLineSegment(sketch, "E4.12.14.1", {"start": v(96.75, 7.07) * mm, "end": v(96.75, 4.19) * mm});
            skLineSegment(sketch, "E4.15.14.1", {"start": v(94.25, 8.52) * mm, "end": v(96.75, 7.07) * mm});
            skLineSegment(sketch, "E4.18.14.1", {"start": v(88.5, 12.7) * mm, "end": v(91, 14.15) * mm});
            skLineSegment(sketch, "E4.21.14.1", {"start": v(88.5, 9.81) * mm, "end": v(88.5, 12.7) * mm});
            skLineSegment(sketch, "E4.24.14.1", {"start": v(91, 8.37) * mm, "end": v(88.5, 9.81) * mm});
            skLineSegment(sketch, "E4.27.14.1", {"start": v(93.5, 9.81) * mm, "end": v(91, 8.37) * mm});
            skLineSegment(sketch, "E4.30.14.1", {"start": v(93.5, 12.7) * mm, "end": v(93.5, 9.81) * mm});
            skLineSegment(sketch, "E4.33.14.1", {"start": v(91, 14.15) * mm, "end": v(93.5, 12.7) * mm});
            skLineSegment(sketch, "E4.36.14.1", {"start": v(91.75, 7.07) * mm, "end": v(94.25, 8.52) * mm});
            skLineSegment(sketch, "E4.39.14.1", {"start": v(91.75, 4.19) * mm, "end": v(91.75, 7.07) * mm});
            skCircle(sketch, "E4.0.14.2", {"center": v(94.25, 16.89) * mm, "radius": 2.5 * mm, "construction": true});
            skCircle(sketch, "E4.2.14.2", {"center": v(91, 22.52) * mm, "radius": 2.5 * mm, "construction": true});
            skPoint(sketch, "E4.4.14.2", {"position": v(92.25, 24.68) * mm});
            skPoint(sketch, "E4.5.14.2", {"position": v(95.5, 19.05) * mm});
            skLineSegment(sketch, "E4.6.14.2", {"start": v(94.25, 14) * mm, "end": v(91.75, 15.44) * mm});
            skLineSegment(sketch, "E4.9.14.2", {"start": v(96.75, 15.44) * mm, "end": v(94.25, 14) * mm});
            skLineSegment(sketch, "E4.12.14.2", {"start": v(96.75, 18.33) * mm, "end": v(96.75, 15.44) * mm});
            skLineSegment(sketch, "E4.15.14.2", {"start": v(94.25, 19.77) * mm, "end": v(96.75, 18.33) * mm});
            skLineSegment(sketch, "E4.18.14.2", {"start": v(88.5, 23.96) * mm, "end": v(91, 25.4) * mm});
            skLineSegment(sketch, "E4.21.14.2", {"start": v(88.5, 21.07) * mm, "end": v(88.5, 23.96) * mm});
            skLineSegment(sketch, "E4.24.14.2", {"start": v(91, 19.63) * mm, "end": v(88.5, 21.07) * mm});
            skLineSegment(sketch, "E4.27.14.2", {"start": v(93.5, 21.07) * mm, "end": v(91, 19.63) * mm});
            skLineSegment(sketch, "E4.30.14.2", {"start": v(93.5, 23.96) * mm, "end": v(93.5, 21.07) * mm});
            skLineSegment(sketch, "E4.33.14.2", {"start": v(91, 25.4) * mm, "end": v(93.5, 23.96) * mm});
            skLineSegment(sketch, "E4.36.14.2", {"start": v(91.75, 18.33) * mm, "end": v(94.25, 19.77) * mm});
            skLineSegment(sketch, "E4.39.14.2", {"start": v(91.75, 15.44) * mm, "end": v(91.75, 18.33) * mm});
            skCircle(sketch, "E4.0.14.3", {"center": v(94.25, 28.15) * mm, "radius": 2.5 * mm, "construction": true});
            skCircle(sketch, "E4.2.14.3", {"center": v(91, 33.77) * mm, "radius": 2.5 * mm, "construction": true});
            skPoint(sketch, "E4.4.14.3", {"position": v(92.25, 35.94) * mm});
            skPoint(sketch, "E4.5.14.3", {"position": v(95.5, 30.31) * mm});
            skLineSegment(sketch, "E4.6.14.3", {"start": v(94.25, 25.26) * mm, "end": v(91.75, 26.7) * mm});
            skLineSegment(sketch, "E4.9.14.3", {"start": v(96.75, 26.7) * mm, "end": v(94.25, 25.26) * mm});
            skLineSegment(sketch, "E4.12.14.3", {"start": v(96.75, 29.59) * mm, "end": v(96.75, 26.7) * mm});
            skLineSegment(sketch, "E4.15.14.3", {"start": v(94.25, 31.03) * mm, "end": v(96.75, 29.59) * mm});
            skLineSegment(sketch, "E4.18.14.3", {"start": v(88.5, 35.22) * mm, "end": v(91, 36.66) * mm});
            skLineSegment(sketch, "E4.21.14.3", {"start": v(88.5, 32.33) * mm, "end": v(88.5, 35.22) * mm});
            skLineSegment(sketch, "E4.24.14.3", {"start": v(91, 30.89) * mm, "end": v(88.5, 32.33) * mm});
            skLineSegment(sketch, "E4.27.14.3", {"start": v(93.5, 32.33) * mm, "end": v(91, 30.89) * mm});
            skLineSegment(sketch, "E4.30.14.3", {"start": v(93.5, 35.22) * mm, "end": v(93.5, 32.33) * mm});
            skLineSegment(sketch, "E4.33.14.3", {"start": v(91, 36.66) * mm, "end": v(93.5, 35.22) * mm});
            skLineSegment(sketch, "E4.36.14.3", {"start": v(91.75, 29.59) * mm, "end": v(94.25, 31.03) * mm});
            skLineSegment(sketch, "E4.39.14.3", {"start": v(91.75, 26.7) * mm, "end": v(91.75, 29.59) * mm});
            skCircle(sketch, "E4.0.14.4", {"center": v(94.25, 39.4) * mm, "radius": 2.5 * mm, "construction": true});
            skCircle(sketch, "E4.2.14.4", {"center": v(91, 45.03) * mm, "radius": 2.5 * mm, "construction": true});
            skPoint(sketch, "E4.4.14.4", {"position": v(92.25, 47.2) * mm});
            skPoint(sketch, "E4.5.14.4", {"position": v(95.5, 41.57) * mm});
            skLineSegment(sketch, "E4.6.14.4", {"start": v(94.25, 36.52) * mm, "end": v(91.75, 37.96) * mm});
            skLineSegment(sketch, "E4.9.14.4", {"start": v(96.75, 37.96) * mm, "end": v(94.25, 36.52) * mm});
            skLineSegment(sketch, "E4.12.14.4", {"start": v(96.75, 40.85) * mm, "end": v(96.75, 37.96) * mm});
            skLineSegment(sketch, "E4.15.14.4", {"start": v(94.25, 42.3) * mm, "end": v(96.75, 40.85) * mm});
            skLineSegment(sketch, "E4.18.14.4", {"start": v(88.5, 46.48) * mm, "end": v(91, 47.92) * mm});
            skLineSegment(sketch, "E4.21.14.4", {"start": v(88.5, 43.59) * mm, "end": v(88.5, 46.48) * mm});
            skLineSegment(sketch, "E4.24.14.4", {"start": v(91, 42.15) * mm, "end": v(88.5, 43.59) * mm});
            skLineSegment(sketch, "E4.27.14.4", {"start": v(93.5, 43.59) * mm, "end": v(91, 42.15) * mm});
            skLineSegment(sketch, "E4.30.14.4", {"start": v(93.5, 46.48) * mm, "end": v(93.5, 43.59) * mm});
            skLineSegment(sketch, "E4.33.14.4", {"start": v(91, 47.92) * mm, "end": v(93.5, 46.48) * mm});
            skLineSegment(sketch, "E4.36.14.4", {"start": v(91.75, 40.85) * mm, "end": v(94.25, 42.3) * mm});
            skLineSegment(sketch, "E4.39.14.4", {"start": v(91.75, 37.96) * mm, "end": v(91.75, 40.85) * mm});
            skCircle(sketch, "E4.0.14.5", {"center": v(94.25, 50.66) * mm, "radius": 2.5 * mm, "construction": true});
            skCircle(sketch, "E4.2.14.5", {"center": v(91, 56.3) * mm, "radius": 2.5 * mm, "construction": true});
            skPoint(sketch, "E4.4.14.5", {"position": v(92.25, 58.46) * mm});
            skPoint(sketch, "E4.5.14.5", {"position": v(95.5, 52.83) * mm});
            skLineSegment(sketch, "E4.6.14.5", {"start": v(94.25, 47.78) * mm, "end": v(91.75, 49.22) * mm});
            skLineSegment(sketch, "E4.9.14.5", {"start": v(96.75, 49.22) * mm, "end": v(94.25, 47.78) * mm});
            skLineSegment(sketch, "E4.12.14.5", {"start": v(96.75, 52.1) * mm, "end": v(96.75, 49.22) * mm});
            skLineSegment(sketch, "E4.15.14.5", {"start": v(94.25, 53.55) * mm, "end": v(96.75, 52.1) * mm});
            skLineSegment(sketch, "E4.18.14.5", {"start": v(88.5, 57.74) * mm, "end": v(91, 59.18) * mm});
            skLineSegment(sketch, "E4.21.14.5", {"start": v(88.5, 54.85) * mm, "end": v(88.5, 57.74) * mm});
            skLineSegment(sketch, "E4.24.14.5", {"start": v(91, 53.4) * mm, "end": v(88.5, 54.85) * mm});
            skLineSegment(sketch, "E4.27.14.5", {"start": v(93.5, 54.85) * mm, "end": v(91, 53.4) * mm});
            skLineSegment(sketch, "E4.30.14.5", {"start": v(93.5, 57.74) * mm, "end": v(93.5, 54.85) * mm});
            skLineSegment(sketch, "E4.33.14.5", {"start": v(91, 59.18) * mm, "end": v(93.5, 57.74) * mm});
            skLineSegment(sketch, "E4.36.14.5", {"start": v(91.75, 52.1) * mm, "end": v(94.25, 53.55) * mm});
            skLineSegment(sketch, "E4.39.14.5", {"start": v(91.75, 49.22) * mm, "end": v(91.75, 52.1) * mm});
            skCircle(sketch, "E4.0.14.6", {"center": v(94.25, 61.92) * mm, "radius": 2.5 * mm, "construction": true});
            skCircle(sketch, "E4.2.14.6", {"center": v(91, 67.55) * mm, "radius": 2.5 * mm, "construction": true});
            skPoint(sketch, "E4.4.14.6", {"position": v(92.25, 69.72) * mm});
            skPoint(sketch, "E4.5.14.6", {"position": v(95.5, 64.09) * mm});
            skLineSegment(sketch, "E4.6.14.6", {"start": v(94.25, 59.03) * mm, "end": v(91.75, 60.48) * mm});
            skLineSegment(sketch, "E4.9.14.6", {"start": v(96.75, 60.48) * mm, "end": v(94.25, 59.03) * mm});
            skLineSegment(sketch, "E4.12.14.6", {"start": v(96.75, 63.36) * mm, "end": v(96.75, 60.48) * mm});
            skLineSegment(sketch, "E4.15.14.6", {"start": v(94.25, 64.8) * mm, "end": v(96.75, 63.36) * mm});
            skLineSegment(sketch, "E4.18.14.6", {"start": v(88.5, 69) * mm, "end": v(91, 70.44) * mm});
            skLineSegment(sketch, "E4.21.14.6", {"start": v(88.5, 66.1) * mm, "end": v(88.5, 69) * mm});
            skLineSegment(sketch, "E4.24.14.6", {"start": v(91, 64.66) * mm, "end": v(88.5, 66.1) * mm});
            skLineSegment(sketch, "E4.27.14.6", {"start": v(93.5, 66.1) * mm, "end": v(91, 64.66) * mm});
            skLineSegment(sketch, "E4.30.14.6", {"start": v(93.5, 69) * mm, "end": v(93.5, 66.1) * mm});
            skLineSegment(sketch, "E4.33.14.6", {"start": v(91, 70.44) * mm, "end": v(93.5, 69) * mm});
            skLineSegment(sketch, "E4.36.14.6", {"start": v(91.75, 63.36) * mm, "end": v(94.25, 64.8) * mm});
            skLineSegment(sketch, "E4.39.14.6", {"start": v(91.75, 60.48) * mm, "end": v(91.75, 63.36) * mm});
            skCircle(sketch, "E4.0.14.7", {"center": v(94.25, 73.18) * mm, "radius": 2.5 * mm, "construction": true});
            skCircle(sketch, "E4.2.14.7", {"center": v(91, 78.8) * mm, "radius": 2.5 * mm, "construction": true});
            skPoint(sketch, "E4.4.14.7", {"position": v(92.25, 80.97) * mm});
            skPoint(sketch, "E4.5.14.7", {"position": v(95.5, 75.34) * mm});
            skLineSegment(sketch, "E4.6.14.7", {"start": v(94.25, 70.3) * mm, "end": v(91.75, 71.74) * mm});
            skLineSegment(sketch, "E4.9.14.7", {"start": v(96.75, 71.74) * mm, "end": v(94.25, 70.3) * mm});
            skLineSegment(sketch, "E4.12.14.7", {"start": v(96.75, 74.62) * mm, "end": v(96.75, 71.74) * mm});
            skLineSegment(sketch, "E4.15.14.7", {"start": v(94.25, 76.07) * mm, "end": v(96.75, 74.62) * mm});
            skLineSegment(sketch, "E4.18.14.7", {"start": v(88.5, 80.25) * mm, "end": v(91, 81.7) * mm});
            skLineSegment(sketch, "E4.21.14.7", {"start": v(88.5, 77.36) * mm, "end": v(88.5, 80.25) * mm});
            skLineSegment(sketch, "E4.24.14.7", {"start": v(91, 75.92) * mm, "end": v(88.5, 77.36) * mm});
            skLineSegment(sketch, "E4.27.14.7", {"start": v(93.5, 77.36) * mm, "end": v(91, 75.92) * mm});
            skLineSegment(sketch, "E4.30.14.7", {"start": v(93.5, 80.25) * mm, "end": v(93.5, 77.36) * mm});
            skLineSegment(sketch, "E4.33.14.7", {"start": v(91, 81.7) * mm, "end": v(93.5, 80.25) * mm});
            skLineSegment(sketch, "E4.36.14.7", {"start": v(91.75, 74.62) * mm, "end": v(94.25, 76.07) * mm});
            skLineSegment(sketch, "E4.39.14.7", {"start": v(91.75, 71.74) * mm, "end": v(91.75, 74.62) * mm});
            skCircle(sketch, "E4.0.14.8", {"center": v(94.25, 84.44) * mm, "radius": 2.5 * mm, "construction": true});
            skCircle(sketch, "E4.2.14.8", {"center": v(91, 90.07) * mm, "radius": 2.5 * mm, "construction": true});
            skPoint(sketch, "E4.4.14.8", {"position": v(92.25, 92.23) * mm});
            skPoint(sketch, "E4.5.14.8", {"position": v(95.5, 86.6) * mm});
            skLineSegment(sketch, "E4.6.14.8", {"start": v(94.25, 81.55) * mm, "end": v(91.75, 83) * mm});
            skLineSegment(sketch, "E4.9.14.8", {"start": v(96.75, 83) * mm, "end": v(94.25, 81.55) * mm});
            skLineSegment(sketch, "E4.12.14.8", {"start": v(96.75, 85.88) * mm, "end": v(96.75, 83) * mm});
            skLineSegment(sketch, "E4.15.14.8", {"start": v(94.25, 87.32) * mm, "end": v(96.75, 85.88) * mm});
            skLineSegment(sketch, "E4.18.14.8", {"start": v(88.5, 91.51) * mm, "end": v(91, 92.95) * mm});
            skLineSegment(sketch, "E4.21.14.8", {"start": v(88.5, 88.62) * mm, "end": v(88.5, 91.51) * mm});
            skLineSegment(sketch, "E4.24.14.8", {"start": v(91, 87.18) * mm, "end": v(88.5, 88.62) * mm});
            skLineSegment(sketch, "E4.27.14.8", {"start": v(93.5, 88.62) * mm, "end": v(91, 87.18) * mm});
            skLineSegment(sketch, "E4.30.14.8", {"start": v(93.5, 91.51) * mm, "end": v(93.5, 88.62) * mm});
            skLineSegment(sketch, "E4.33.14.8", {"start": v(91, 92.95) * mm, "end": v(93.5, 91.51) * mm});
            skLineSegment(sketch, "E4.36.14.8", {"start": v(91.75, 85.88) * mm, "end": v(94.25, 87.32) * mm});
            skLineSegment(sketch, "E4.39.14.8", {"start": v(91.75, 83) * mm, "end": v(91.75, 85.88) * mm});
            skCircle(sketch, "E4.0.14.9", {"center": v(94.25, 95.7) * mm, "radius": 2.5 * mm, "construction": true});
            skCircle(sketch, "E4.2.14.9", {"center": v(91, 101.32) * mm, "radius": 2.5 * mm, "construction": true});
            skPoint(sketch, "E4.4.14.9", {"position": v(92.25, 103.5) * mm});
            skPoint(sketch, "E4.5.14.9", {"position": v(95.5, 97.86) * mm});
            skLineSegment(sketch, "E4.6.14.9", {"start": v(94.25, 92.8) * mm, "end": v(91.75, 94.25) * mm});
            skLineSegment(sketch, "E4.9.14.9", {"start": v(96.75, 94.25) * mm, "end": v(94.25, 92.8) * mm});
            skLineSegment(sketch, "E4.12.14.9", {"start": v(96.75, 97.14) * mm, "end": v(96.75, 94.25) * mm});
            skLineSegment(sketch, "E4.15.14.9", {"start": v(94.25, 98.58) * mm, "end": v(96.75, 97.14) * mm});
            skLineSegment(sketch, "E4.18.14.9", {"start": v(88.5, 102.77) * mm, "end": v(91, 104.21) * mm});
            skLineSegment(sketch, "E4.21.14.9", {"start": v(88.5, 99.88) * mm, "end": v(88.5, 102.77) * mm});
            skLineSegment(sketch, "E4.24.14.9", {"start": v(91, 98.44) * mm, "end": v(88.5, 99.88) * mm});
            skLineSegment(sketch, "E4.27.14.9", {"start": v(93.5, 99.88) * mm, "end": v(91, 98.44) * mm});
            skLineSegment(sketch, "E4.30.14.9", {"start": v(93.5, 102.77) * mm, "end": v(93.5, 99.88) * mm});
            skLineSegment(sketch, "E4.33.14.9", {"start": v(91, 104.21) * mm, "end": v(93.5, 102.77) * mm});
            skLineSegment(sketch, "E4.36.14.9", {"start": v(91.75, 97.14) * mm, "end": v(94.25, 98.58) * mm});
            skLineSegment(sketch, "E4.39.14.9", {"start": v(91.75, 94.25) * mm, "end": v(91.75, 97.14) * mm});
            skCircle(sketch, "E4.0.15.0", {"center": v(100.75, -5.63) * mm, "radius": 2.5 * mm, "construction": true});
            skCircle(sketch, "E4.2.15.0", {"center": v(97.5, 0) * mm, "radius": 2.5 * mm, "construction": true});
            skPoint(sketch, "E4.4.15.0", {"position": v(98.75, 2.17) * mm});
            skPoint(sketch, "E4.5.15.0", {"position": v(102, -3.46) * mm});
            skLineSegment(sketch, "E4.6.15.0", {"start": v(100.75, -8.52) * mm, "end": v(98.25, -7.07) * mm});
            skLineSegment(sketch, "E4.9.15.0", {"start": v(103.25, -7.07) * mm, "end": v(100.75, -8.52) * mm});
            skLineSegment(sketch, "E4.12.15.0", {"start": v(103.25, -4.19) * mm, "end": v(103.25, -7.07) * mm});
            skLineSegment(sketch, "E4.15.15.0", {"start": v(100.75, -2.74) * mm, "end": v(103.25, -4.19) * mm});
            skLineSegment(sketch, "E4.18.15.0", {"start": v(95, 1.44) * mm, "end": v(97.5, 2.89) * mm});
            skLineSegment(sketch, "E4.21.15.0", {"start": v(95, -1.44) * mm, "end": v(95, 1.44) * mm});
            skLineSegment(sketch, "E4.24.15.0", {"start": v(97.5, -2.89) * mm, "end": v(95, -1.44) * mm});
            skLineSegment(sketch, "E4.27.15.0", {"start": v(100, -1.44) * mm, "end": v(97.5, -2.89) * mm});
            skLineSegment(sketch, "E4.30.15.0", {"start": v(100, 1.44) * mm, "end": v(100, -1.44) * mm});
            skLineSegment(sketch, "E4.33.15.0", {"start": v(97.5, 2.89) * mm, "end": v(100, 1.44) * mm});
            skLineSegment(sketch, "E4.36.15.0", {"start": v(98.25, -4.19) * mm, "end": v(100.75, -2.74) * mm});
            skLineSegment(sketch, "E4.39.15.0", {"start": v(98.25, -7.07) * mm, "end": v(98.25, -4.19) * mm});
            skCircle(sketch, "E4.0.15.1", {"center": v(100.75, 5.63) * mm, "radius": 2.5 * mm, "construction": true});
            skCircle(sketch, "E4.2.15.1", {"center": v(97.5, 11.26) * mm, "radius": 2.5 * mm, "construction": true});
            skPoint(sketch, "E4.4.15.1", {"position": v(98.75, 13.42) * mm});
            skPoint(sketch, "E4.5.15.1", {"position": v(102, 7.8) * mm});
            skLineSegment(sketch, "E4.6.15.1", {"start": v(100.75, 2.74) * mm, "end": v(98.25, 4.19) * mm});
            skLineSegment(sketch, "E4.9.15.1", {"start": v(103.25, 4.19) * mm, "end": v(100.75, 2.74) * mm});
            skLineSegment(sketch, "E4.12.15.1", {"start": v(103.25, 7.07) * mm, "end": v(103.25, 4.19) * mm});
            skLineSegment(sketch, "E4.15.15.1", {"start": v(100.75, 8.52) * mm, "end": v(103.25, 7.07) * mm});
            skLineSegment(sketch, "E4.18.15.1", {"start": v(95, 12.7) * mm, "end": v(97.5, 14.15) * mm});
            skLineSegment(sketch, "E4.21.15.1", {"start": v(95, 9.81) * mm, "end": v(95, 12.7) * mm});
            skLineSegment(sketch, "E4.24.15.1", {"start": v(97.5, 8.37) * mm, "end": v(95, 9.81) * mm});
            skLineSegment(sketch, "E4.27.15.1", {"start": v(100, 9.81) * mm, "end": v(97.5, 8.37) * mm});
            skLineSegment(sketch, "E4.30.15.1", {"start": v(100, 12.7) * mm, "end": v(100, 9.81) * mm});
            skLineSegment(sketch, "E4.33.15.1", {"start": v(97.5, 14.15) * mm, "end": v(100, 12.7) * mm});
            skLineSegment(sketch, "E4.36.15.1", {"start": v(98.25, 7.07) * mm, "end": v(100.75, 8.52) * mm});
            skLineSegment(sketch, "E4.39.15.1", {"start": v(98.25, 4.19) * mm, "end": v(98.25, 7.07) * mm});
            skCircle(sketch, "E4.0.15.2", {"center": v(100.75, 16.89) * mm, "radius": 2.5 * mm, "construction": true});
            skCircle(sketch, "E4.2.15.2", {"center": v(97.5, 22.52) * mm, "radius": 2.5 * mm, "construction": true});
            skPoint(sketch, "E4.4.15.2", {"position": v(98.75, 24.68) * mm});
            skPoint(sketch, "E4.5.15.2", {"position": v(102, 19.05) * mm});
            skLineSegment(sketch, "E4.6.15.2", {"start": v(100.75, 14) * mm, "end": v(98.25, 15.44) * mm});
            skLineSegment(sketch, "E4.9.15.2", {"start": v(103.25, 15.44) * mm, "end": v(100.75, 14) * mm});
            skLineSegment(sketch, "E4.12.15.2", {"start": v(103.25, 18.33) * mm, "end": v(103.25, 15.44) * mm});
            skLineSegment(sketch, "E4.15.15.2", {"start": v(100.75, 19.77) * mm, "end": v(103.25, 18.33) * mm});
            skLineSegment(sketch, "E4.18.15.2", {"start": v(95, 23.96) * mm, "end": v(97.5, 25.4) * mm});
            skLineSegment(sketch, "E4.21.15.2", {"start": v(95, 21.07) * mm, "end": v(95, 23.96) * mm});
            skLineSegment(sketch, "E4.24.15.2", {"start": v(97.5, 19.63) * mm, "end": v(95, 21.07) * mm});
            skLineSegment(sketch, "E4.27.15.2", {"start": v(100, 21.07) * mm, "end": v(97.5, 19.63) * mm});
            skLineSegment(sketch, "E4.30.15.2", {"start": v(100, 23.96) * mm, "end": v(100, 21.07) * mm});
            skLineSegment(sketch, "E4.33.15.2", {"start": v(97.5, 25.4) * mm, "end": v(100, 23.96) * mm});
            skLineSegment(sketch, "E4.36.15.2", {"start": v(98.25, 18.33) * mm, "end": v(100.75, 19.77) * mm});
            skLineSegment(sketch, "E4.39.15.2", {"start": v(98.25, 15.44) * mm, "end": v(98.25, 18.33) * mm});
            skCircle(sketch, "E4.0.15.3", {"center": v(100.75, 28.15) * mm, "radius": 2.5 * mm, "construction": true});
            skCircle(sketch, "E4.2.15.3", {"center": v(97.5, 33.77) * mm, "radius": 2.5 * mm, "construction": true});
            skPoint(sketch, "E4.4.15.3", {"position": v(98.75, 35.94) * mm});
            skPoint(sketch, "E4.5.15.3", {"position": v(102, 30.31) * mm});
            skLineSegment(sketch, "E4.6.15.3", {"start": v(100.75, 25.26) * mm, "end": v(98.25, 26.7) * mm});
            skLineSegment(sketch, "E4.9.15.3", {"start": v(103.25, 26.7) * mm, "end": v(100.75, 25.26) * mm});
            skLineSegment(sketch, "E4.12.15.3", {"start": v(103.25, 29.59) * mm, "end": v(103.25, 26.7) * mm});
            skLineSegment(sketch, "E4.15.15.3", {"start": v(100.75, 31.03) * mm, "end": v(103.25, 29.59) * mm});
            skLineSegment(sketch, "E4.18.15.3", {"start": v(95, 35.22) * mm, "end": v(97.5, 36.66) * mm});
            skLineSegment(sketch, "E4.21.15.3", {"start": v(95, 32.33) * mm, "end": v(95, 35.22) * mm});
            skLineSegment(sketch, "E4.24.15.3", {"start": v(97.5, 30.89) * mm, "end": v(95, 32.33) * mm});
            skLineSegment(sketch, "E4.27.15.3", {"start": v(100, 32.33) * mm, "end": v(97.5, 30.89) * mm});
            skLineSegment(sketch, "E4.30.15.3", {"start": v(100, 35.22) * mm, "end": v(100, 32.33) * mm});
            skLineSegment(sketch, "E4.33.15.3", {"start": v(97.5, 36.66) * mm, "end": v(100, 35.22) * mm});
            skLineSegment(sketch, "E4.36.15.3", {"start": v(98.25, 29.59) * mm, "end": v(100.75, 31.03) * mm});
            skLineSegment(sketch, "E4.39.15.3", {"start": v(98.25, 26.7) * mm, "end": v(98.25, 29.59) * mm});
            skCircle(sketch, "E4.0.15.4", {"center": v(100.75, 39.4) * mm, "radius": 2.5 * mm, "construction": true});
            skCircle(sketch, "E4.2.15.4", {"center": v(97.5, 45.03) * mm, "radius": 2.5 * mm, "construction": true});
            skPoint(sketch, "E4.4.15.4", {"position": v(98.75, 47.2) * mm});
            skPoint(sketch, "E4.5.15.4", {"position": v(102, 41.57) * mm});
            skLineSegment(sketch, "E4.6.15.4", {"start": v(100.75, 36.52) * mm, "end": v(98.25, 37.96) * mm});
            skLineSegment(sketch, "E4.9.15.4", {"start": v(103.25, 37.96) * mm, "end": v(100.75, 36.52) * mm});
            skLineSegment(sketch, "E4.12.15.4", {"start": v(103.25, 40.85) * mm, "end": v(103.25, 37.96) * mm});
            skLineSegment(sketch, "E4.15.15.4", {"start": v(100.75, 42.3) * mm, "end": v(103.25, 40.85) * mm});
            skLineSegment(sketch, "E4.18.15.4", {"start": v(95, 46.48) * mm, "end": v(97.5, 47.92) * mm});
            skLineSegment(sketch, "E4.21.15.4", {"start": v(95, 43.59) * mm, "end": v(95, 46.48) * mm});
            skLineSegment(sketch, "E4.24.15.4", {"start": v(97.5, 42.15) * mm, "end": v(95, 43.59) * mm});
            skLineSegment(sketch, "E4.27.15.4", {"start": v(100, 43.59) * mm, "end": v(97.5, 42.15) * mm});
            skLineSegment(sketch, "E4.30.15.4", {"start": v(100, 46.48) * mm, "end": v(100, 43.59) * mm});
            skLineSegment(sketch, "E4.33.15.4", {"start": v(97.5, 47.92) * mm, "end": v(100, 46.48) * mm});
            skLineSegment(sketch, "E4.36.15.4", {"start": v(98.25, 40.85) * mm, "end": v(100.75, 42.3) * mm});
            skLineSegment(sketch, "E4.39.15.4", {"start": v(98.25, 37.96) * mm, "end": v(98.25, 40.85) * mm});
            skCircle(sketch, "E4.0.15.5", {"center": v(100.75, 50.66) * mm, "radius": 2.5 * mm, "construction": true});
            skCircle(sketch, "E4.2.15.5", {"center": v(97.5, 56.3) * mm, "radius": 2.5 * mm, "construction": true});
            skPoint(sketch, "E4.4.15.5", {"position": v(98.75, 58.46) * mm});
            skPoint(sketch, "E4.5.15.5", {"position": v(102, 52.83) * mm});
            skLineSegment(sketch, "E4.6.15.5", {"start": v(100.75, 47.78) * mm, "end": v(98.25, 49.22) * mm});
            skLineSegment(sketch, "E4.9.15.5", {"start": v(103.25, 49.22) * mm, "end": v(100.75, 47.78) * mm});
            skLineSegment(sketch, "E4.12.15.5", {"start": v(103.25, 52.1) * mm, "end": v(103.25, 49.22) * mm});
            skLineSegment(sketch, "E4.15.15.5", {"start": v(100.75, 53.55) * mm, "end": v(103.25, 52.1) * mm});
            skLineSegment(sketch, "E4.18.15.5", {"start": v(95, 57.74) * mm, "end": v(97.5, 59.18) * mm});
            skLineSegment(sketch, "E4.21.15.5", {"start": v(95, 54.85) * mm, "end": v(95, 57.74) * mm});
            skLineSegment(sketch, "E4.24.15.5", {"start": v(97.5, 53.4) * mm, "end": v(95, 54.85) * mm});
            skLineSegment(sketch, "E4.27.15.5", {"start": v(100, 54.85) * mm, "end": v(97.5, 53.4) * mm});
            skLineSegment(sketch, "E4.30.15.5", {"start": v(100, 57.74) * mm, "end": v(100, 54.85) * mm});
            skLineSegment(sketch, "E4.33.15.5", {"start": v(97.5, 59.18) * mm, "end": v(100, 57.74) * mm});
            skLineSegment(sketch, "E4.36.15.5", {"start": v(98.25, 52.1) * mm, "end": v(100.75, 53.55) * mm});
            skLineSegment(sketch, "E4.39.15.5", {"start": v(98.25, 49.22) * mm, "end": v(98.25, 52.1) * mm});
            skCircle(sketch, "E4.0.15.6", {"center": v(100.75, 61.92) * mm, "radius": 2.5 * mm, "construction": true});
            skCircle(sketch, "E4.2.15.6", {"center": v(97.5, 67.55) * mm, "radius": 2.5 * mm, "construction": true});
            skPoint(sketch, "E4.4.15.6", {"position": v(98.75, 69.72) * mm});
            skPoint(sketch, "E4.5.15.6", {"position": v(102, 64.09) * mm});
            skLineSegment(sketch, "E4.6.15.6", {"start": v(100.75, 59.03) * mm, "end": v(98.25, 60.48) * mm});
            skLineSegment(sketch, "E4.9.15.6", {"start": v(103.25, 60.48) * mm, "end": v(100.75, 59.03) * mm});
            skLineSegment(sketch, "E4.12.15.6", {"start": v(103.25, 63.36) * mm, "end": v(103.25, 60.48) * mm});
            skLineSegment(sketch, "E4.15.15.6", {"start": v(100.75, 64.8) * mm, "end": v(103.25, 63.36) * mm});
            skLineSegment(sketch, "E4.18.15.6", {"start": v(95, 69) * mm, "end": v(97.5, 70.44) * mm});
            skLineSegment(sketch, "E4.21.15.6", {"start": v(95, 66.1) * mm, "end": v(95, 69) * mm});
            skLineSegment(sketch, "E4.24.15.6", {"start": v(97.5, 64.66) * mm, "end": v(95, 66.1) * mm});
            skLineSegment(sketch, "E4.27.15.6", {"start": v(100, 66.1) * mm, "end": v(97.5, 64.66) * mm});
            skLineSegment(sketch, "E4.30.15.6", {"start": v(100, 69) * mm, "end": v(100, 66.1) * mm});
            skLineSegment(sketch, "E4.33.15.6", {"start": v(97.5, 70.44) * mm, "end": v(100, 69) * mm});
            skLineSegment(sketch, "E4.36.15.6", {"start": v(98.25, 63.36) * mm, "end": v(100.75, 64.8) * mm});
            skLineSegment(sketch, "E4.39.15.6", {"start": v(98.25, 60.48) * mm, "end": v(98.25, 63.36) * mm});
            skCircle(sketch, "E4.0.15.7", {"center": v(100.75, 73.18) * mm, "radius": 2.5 * mm, "construction": true});
            skCircle(sketch, "E4.2.15.7", {"center": v(97.5, 78.8) * mm, "radius": 2.5 * mm, "construction": true});
            skPoint(sketch, "E4.4.15.7", {"position": v(98.75, 80.97) * mm});
            skPoint(sketch, "E4.5.15.7", {"position": v(102, 75.34) * mm});
            skLineSegment(sketch, "E4.6.15.7", {"start": v(100.75, 70.3) * mm, "end": v(98.25, 71.74) * mm});
            skLineSegment(sketch, "E4.9.15.7", {"start": v(103.25, 71.74) * mm, "end": v(100.75, 70.3) * mm});
            skLineSegment(sketch, "E4.12.15.7", {"start": v(103.25, 74.62) * mm, "end": v(103.25, 71.74) * mm});
            skLineSegment(sketch, "E4.15.15.7", {"start": v(100.75, 76.07) * mm, "end": v(103.25, 74.62) * mm});
            skLineSegment(sketch, "E4.18.15.7", {"start": v(95, 80.25) * mm, "end": v(97.5, 81.7) * mm});
            skLineSegment(sketch, "E4.21.15.7", {"start": v(95, 77.36) * mm, "end": v(95, 80.25) * mm});
            skLineSegment(sketch, "E4.24.15.7", {"start": v(97.5, 75.92) * mm, "end": v(95, 77.36) * mm});
            skLineSegment(sketch, "E4.27.15.7", {"start": v(100, 77.36) * mm, "end": v(97.5, 75.92) * mm});
            skLineSegment(sketch, "E4.30.15.7", {"start": v(100, 80.25) * mm, "end": v(100, 77.36) * mm});
            skLineSegment(sketch, "E4.33.15.7", {"start": v(97.5, 81.7) * mm, "end": v(100, 80.25) * mm});
            skLineSegment(sketch, "E4.36.15.7", {"start": v(98.25, 74.62) * mm, "end": v(100.75, 76.07) * mm});
            skLineSegment(sketch, "E4.39.15.7", {"start": v(98.25, 71.74) * mm, "end": v(98.25, 74.62) * mm});
            skCircle(sketch, "E4.0.15.8", {"center": v(100.75, 84.44) * mm, "radius": 2.5 * mm, "construction": true});
            skCircle(sketch, "E4.2.15.8", {"center": v(97.5, 90.07) * mm, "radius": 2.5 * mm, "construction": true});
            skPoint(sketch, "E4.4.15.8", {"position": v(98.75, 92.23) * mm});
            skPoint(sketch, "E4.5.15.8", {"position": v(102, 86.6) * mm});
            skLineSegment(sketch, "E4.6.15.8", {"start": v(100.75, 81.55) * mm, "end": v(98.25, 83) * mm});
            skLineSegment(sketch, "E4.9.15.8", {"start": v(103.25, 83) * mm, "end": v(100.75, 81.55) * mm});
            skLineSegment(sketch, "E4.12.15.8", {"start": v(103.25, 85.88) * mm, "end": v(103.25, 83) * mm});
            skLineSegment(sketch, "E4.15.15.8", {"start": v(100.75, 87.32) * mm, "end": v(103.25, 85.88) * mm});
            skLineSegment(sketch, "E4.18.15.8", {"start": v(95, 91.51) * mm, "end": v(97.5, 92.95) * mm});
            skLineSegment(sketch, "E4.21.15.8", {"start": v(95, 88.62) * mm, "end": v(95, 91.51) * mm});
            skLineSegment(sketch, "E4.24.15.8", {"start": v(97.5, 87.18) * mm, "end": v(95, 88.62) * mm});
            skLineSegment(sketch, "E4.27.15.8", {"start": v(100, 88.62) * mm, "end": v(97.5, 87.18) * mm});
            skLineSegment(sketch, "E4.30.15.8", {"start": v(100, 91.51) * mm, "end": v(100, 88.62) * mm});
            skLineSegment(sketch, "E4.33.15.8", {"start": v(97.5, 92.95) * mm, "end": v(100, 91.51) * mm});
            skLineSegment(sketch, "E4.36.15.8", {"start": v(98.25, 85.88) * mm, "end": v(100.75, 87.32) * mm});
            skLineSegment(sketch, "E4.39.15.8", {"start": v(98.25, 83) * mm, "end": v(98.25, 85.88) * mm});
            skCircle(sketch, "E4.0.15.9", {"center": v(100.75, 95.7) * mm, "radius": 2.5 * mm, "construction": true});
            skCircle(sketch, "E4.2.15.9", {"center": v(97.5, 101.32) * mm, "radius": 2.5 * mm, "construction": true});
            skPoint(sketch, "E4.4.15.9", {"position": v(98.75, 103.5) * mm});
            skPoint(sketch, "E4.5.15.9", {"position": v(102, 97.86) * mm});
            skLineSegment(sketch, "E4.6.15.9", {"start": v(100.75, 92.8) * mm, "end": v(98.25, 94.25) * mm});
            skLineSegment(sketch, "E4.9.15.9", {"start": v(103.25, 94.25) * mm, "end": v(100.75, 92.8) * mm});
            skLineSegment(sketch, "E4.12.15.9", {"start": v(103.25, 97.14) * mm, "end": v(103.25, 94.25) * mm});
            skLineSegment(sketch, "E4.15.15.9", {"start": v(100.75, 98.58) * mm, "end": v(103.25, 97.14) * mm});
            skLineSegment(sketch, "E4.18.15.9", {"start": v(95, 102.77) * mm, "end": v(97.5, 104.21) * mm});
            skLineSegment(sketch, "E4.21.15.9", {"start": v(95, 99.88) * mm, "end": v(95, 102.77) * mm});
            skLineSegment(sketch, "E4.24.15.9", {"start": v(97.5, 98.44) * mm, "end": v(95, 99.88) * mm});
            skLineSegment(sketch, "E4.27.15.9", {"start": v(100, 99.88) * mm, "end": v(97.5, 98.44) * mm});
            skLineSegment(sketch, "E4.30.15.9", {"start": v(100, 102.77) * mm, "end": v(100, 99.88) * mm});
            skLineSegment(sketch, "E4.33.15.9", {"start": v(97.5, 104.21) * mm, "end": v(100, 102.77) * mm});
            skLineSegment(sketch, "E4.36.15.9", {"start": v(98.25, 97.14) * mm, "end": v(100.75, 98.58) * mm});
            skLineSegment(sketch, "E4.39.15.9", {"start": v(98.25, 94.25) * mm, "end": v(98.25, 97.14) * mm});
            skCircle(sketch, "E4.0.16.0", {"center": v(107.25, -5.63) * mm, "radius": 2.5 * mm, "construction": true});
            skCircle(sketch, "E4.2.16.0", {"center": v(104, 0) * mm, "radius": 2.5 * mm, "construction": true});
            skPoint(sketch, "E4.4.16.0", {"position": v(105.25, 2.17) * mm});
            skPoint(sketch, "E4.5.16.0", {"position": v(108.5, -3.46) * mm});
            skLineSegment(sketch, "E4.6.16.0", {"start": v(107.25, -8.52) * mm, "end": v(104.75, -7.07) * mm});
            skLineSegment(sketch, "E4.9.16.0", {"start": v(109.75, -7.07) * mm, "end": v(107.25, -8.52) * mm});
            skLineSegment(sketch, "E4.12.16.0", {"start": v(109.75, -4.19) * mm, "end": v(109.75, -7.07) * mm});
            skLineSegment(sketch, "E4.15.16.0", {"start": v(107.25, -2.74) * mm, "end": v(109.75, -4.19) * mm});
            skLineSegment(sketch, "E4.18.16.0", {"start": v(101.5, 1.44) * mm, "end": v(104, 2.89) * mm});
            skLineSegment(sketch, "E4.21.16.0", {"start": v(101.5, -1.44) * mm, "end": v(101.5, 1.44) * mm});
            skLineSegment(sketch, "E4.24.16.0", {"start": v(104, -2.89) * mm, "end": v(101.5, -1.44) * mm});
            skLineSegment(sketch, "E4.27.16.0", {"start": v(106.5, -1.44) * mm, "end": v(104, -2.89) * mm});
            skLineSegment(sketch, "E4.30.16.0", {"start": v(106.5, 1.44) * mm, "end": v(106.5, -1.44) * mm});
            skLineSegment(sketch, "E4.33.16.0", {"start": v(104, 2.89) * mm, "end": v(106.5, 1.44) * mm});
            skLineSegment(sketch, "E4.36.16.0", {"start": v(104.75, -4.19) * mm, "end": v(107.25, -2.74) * mm});
            skLineSegment(sketch, "E4.39.16.0", {"start": v(104.75, -7.07) * mm, "end": v(104.75, -4.19) * mm});
            skCircle(sketch, "E4.0.16.1", {"center": v(107.25, 5.63) * mm, "radius": 2.5 * mm, "construction": true});
            skCircle(sketch, "E4.2.16.1", {"center": v(104, 11.26) * mm, "radius": 2.5 * mm, "construction": true});
            skPoint(sketch, "E4.4.16.1", {"position": v(105.25, 13.42) * mm});
            skPoint(sketch, "E4.5.16.1", {"position": v(108.5, 7.8) * mm});
            skLineSegment(sketch, "E4.6.16.1", {"start": v(107.25, 2.74) * mm, "end": v(104.75, 4.19) * mm});
            skLineSegment(sketch, "E4.9.16.1", {"start": v(109.75, 4.19) * mm, "end": v(107.25, 2.74) * mm});
            skLineSegment(sketch, "E4.12.16.1", {"start": v(109.75, 7.07) * mm, "end": v(109.75, 4.19) * mm});
            skLineSegment(sketch, "E4.15.16.1", {"start": v(107.25, 8.52) * mm, "end": v(109.75, 7.07) * mm});
            skLineSegment(sketch, "E4.18.16.1", {"start": v(101.5, 12.7) * mm, "end": v(104, 14.15) * mm});
            skLineSegment(sketch, "E4.21.16.1", {"start": v(101.5, 9.81) * mm, "end": v(101.5, 12.7) * mm});
            skLineSegment(sketch, "E4.24.16.1", {"start": v(104, 8.37) * mm, "end": v(101.5, 9.81) * mm});
            skLineSegment(sketch, "E4.27.16.1", {"start": v(106.5, 9.81) * mm, "end": v(104, 8.37) * mm});
            skLineSegment(sketch, "E4.30.16.1", {"start": v(106.5, 12.7) * mm, "end": v(106.5, 9.81) * mm});
            skLineSegment(sketch, "E4.33.16.1", {"start": v(104, 14.15) * mm, "end": v(106.5, 12.7) * mm});
            skLineSegment(sketch, "E4.36.16.1", {"start": v(104.75, 7.07) * mm, "end": v(107.25, 8.52) * mm});
            skLineSegment(sketch, "E4.39.16.1", {"start": v(104.75, 4.19) * mm, "end": v(104.75, 7.07) * mm});
            skCircle(sketch, "E4.0.16.2", {"center": v(107.25, 16.89) * mm, "radius": 2.5 * mm, "construction": true});
            skCircle(sketch, "E4.2.16.2", {"center": v(104, 22.52) * mm, "radius": 2.5 * mm, "construction": true});
            skPoint(sketch, "E4.4.16.2", {"position": v(105.25, 24.68) * mm});
            skPoint(sketch, "E4.5.16.2", {"position": v(108.5, 19.05) * mm});
            skLineSegment(sketch, "E4.6.16.2", {"start": v(107.25, 14) * mm, "end": v(104.75, 15.44) * mm});
            skLineSegment(sketch, "E4.9.16.2", {"start": v(109.75, 15.44) * mm, "end": v(107.25, 14) * mm});
            skLineSegment(sketch, "E4.12.16.2", {"start": v(109.75, 18.33) * mm, "end": v(109.75, 15.44) * mm});
            skLineSegment(sketch, "E4.15.16.2", {"start": v(107.25, 19.77) * mm, "end": v(109.75, 18.33) * mm});
            skLineSegment(sketch, "E4.18.16.2", {"start": v(101.5, 23.96) * mm, "end": v(104, 25.4) * mm});
            skLineSegment(sketch, "E4.21.16.2", {"start": v(101.5, 21.07) * mm, "end": v(101.5, 23.96) * mm});
            skLineSegment(sketch, "E4.24.16.2", {"start": v(104, 19.63) * mm, "end": v(101.5, 21.07) * mm});
            skLineSegment(sketch, "E4.27.16.2", {"start": v(106.5, 21.07) * mm, "end": v(104, 19.63) * mm});
            skLineSegment(sketch, "E4.30.16.2", {"start": v(106.5, 23.96) * mm, "end": v(106.5, 21.07) * mm});
            skLineSegment(sketch, "E4.33.16.2", {"start": v(104, 25.4) * mm, "end": v(106.5, 23.96) * mm});
            skLineSegment(sketch, "E4.36.16.2", {"start": v(104.75, 18.33) * mm, "end": v(107.25, 19.77) * mm});
            skLineSegment(sketch, "E4.39.16.2", {"start": v(104.75, 15.44) * mm, "end": v(104.75, 18.33) * mm});
            skCircle(sketch, "E4.0.16.3", {"center": v(107.25, 28.15) * mm, "radius": 2.5 * mm, "construction": true});
            skCircle(sketch, "E4.2.16.3", {"center": v(104, 33.77) * mm, "radius": 2.5 * mm, "construction": true});
            skPoint(sketch, "E4.4.16.3", {"position": v(105.25, 35.94) * mm});
            skPoint(sketch, "E4.5.16.3", {"position": v(108.5, 30.31) * mm});
            skLineSegment(sketch, "E4.6.16.3", {"start": v(107.25, 25.26) * mm, "end": v(104.75, 26.7) * mm});
            skLineSegment(sketch, "E4.9.16.3", {"start": v(109.75, 26.7) * mm, "end": v(107.25, 25.26) * mm});
            skLineSegment(sketch, "E4.12.16.3", {"start": v(109.75, 29.59) * mm, "end": v(109.75, 26.7) * mm});
            skLineSegment(sketch, "E4.15.16.3", {"start": v(107.25, 31.03) * mm, "end": v(109.75, 29.59) * mm});
            skLineSegment(sketch, "E4.18.16.3", {"start": v(101.5, 35.22) * mm, "end": v(104, 36.66) * mm});
            skLineSegment(sketch, "E4.21.16.3", {"start": v(101.5, 32.33) * mm, "end": v(101.5, 35.22) * mm});
            skLineSegment(sketch, "E4.24.16.3", {"start": v(104, 30.89) * mm, "end": v(101.5, 32.33) * mm});
            skLineSegment(sketch, "E4.27.16.3", {"start": v(106.5, 32.33) * mm, "end": v(104, 30.89) * mm});
            skLineSegment(sketch, "E4.30.16.3", {"start": v(106.5, 35.22) * mm, "end": v(106.5, 32.33) * mm});
            skLineSegment(sketch, "E4.33.16.3", {"start": v(104, 36.66) * mm, "end": v(106.5, 35.22) * mm});
            skLineSegment(sketch, "E4.36.16.3", {"start": v(104.75, 29.59) * mm, "end": v(107.25, 31.03) * mm});
            skLineSegment(sketch, "E4.39.16.3", {"start": v(104.75, 26.7) * mm, "end": v(104.75, 29.59) * mm});
            skCircle(sketch, "E4.0.16.4", {"center": v(107.25, 39.4) * mm, "radius": 2.5 * mm, "construction": true});
            skCircle(sketch, "E4.2.16.4", {"center": v(104, 45.03) * mm, "radius": 2.5 * mm, "construction": true});
            skPoint(sketch, "E4.4.16.4", {"position": v(105.25, 47.2) * mm});
            skPoint(sketch, "E4.5.16.4", {"position": v(108.5, 41.57) * mm});
            skLineSegment(sketch, "E4.6.16.4", {"start": v(107.25, 36.52) * mm, "end": v(104.75, 37.96) * mm});
            skLineSegment(sketch, "E4.9.16.4", {"start": v(109.75, 37.96) * mm, "end": v(107.25, 36.52) * mm});
            skLineSegment(sketch, "E4.12.16.4", {"start": v(109.75, 40.85) * mm, "end": v(109.75, 37.96) * mm});
            skLineSegment(sketch, "E4.15.16.4", {"start": v(107.25, 42.3) * mm, "end": v(109.75, 40.85) * mm});
            skLineSegment(sketch, "E4.18.16.4", {"start": v(101.5, 46.48) * mm, "end": v(104, 47.92) * mm});
            skLineSegment(sketch, "E4.21.16.4", {"start": v(101.5, 43.59) * mm, "end": v(101.5, 46.48) * mm});
            skLineSegment(sketch, "E4.24.16.4", {"start": v(104, 42.15) * mm, "end": v(101.5, 43.59) * mm});
            skLineSegment(sketch, "E4.27.16.4", {"start": v(106.5, 43.59) * mm, "end": v(104, 42.15) * mm});
            skLineSegment(sketch, "E4.30.16.4", {"start": v(106.5, 46.48) * mm, "end": v(106.5, 43.59) * mm});
            skLineSegment(sketch, "E4.33.16.4", {"start": v(104, 47.92) * mm, "end": v(106.5, 46.48) * mm});
            skLineSegment(sketch, "E4.36.16.4", {"start": v(104.75, 40.85) * mm, "end": v(107.25, 42.3) * mm});
            skLineSegment(sketch, "E4.39.16.4", {"start": v(104.75, 37.96) * mm, "end": v(104.75, 40.85) * mm});
            skCircle(sketch, "E4.0.16.5", {"center": v(107.25, 50.66) * mm, "radius": 2.5 * mm, "construction": true});
            skCircle(sketch, "E4.2.16.5", {"center": v(104, 56.3) * mm, "radius": 2.5 * mm, "construction": true});
            skPoint(sketch, "E4.4.16.5", {"position": v(105.25, 58.46) * mm});
            skPoint(sketch, "E4.5.16.5", {"position": v(108.5, 52.83) * mm});
            skLineSegment(sketch, "E4.6.16.5", {"start": v(107.25, 47.78) * mm, "end": v(104.75, 49.22) * mm});
            skLineSegment(sketch, "E4.9.16.5", {"start": v(109.75, 49.22) * mm, "end": v(107.25, 47.78) * mm});
            skLineSegment(sketch, "E4.12.16.5", {"start": v(109.75, 52.1) * mm, "end": v(109.75, 49.22) * mm});
            skLineSegment(sketch, "E4.15.16.5", {"start": v(107.25, 53.55) * mm, "end": v(109.75, 52.1) * mm});
            skLineSegment(sketch, "E4.18.16.5", {"start": v(101.5, 57.74) * mm, "end": v(104, 59.18) * mm});
            skLineSegment(sketch, "E4.21.16.5", {"start": v(101.5, 54.85) * mm, "end": v(101.5, 57.74) * mm});
            skLineSegment(sketch, "E4.24.16.5", {"start": v(104, 53.4) * mm, "end": v(101.5, 54.85) * mm});
            skLineSegment(sketch, "E4.27.16.5", {"start": v(106.5, 54.85) * mm, "end": v(104, 53.4) * mm});
            skLineSegment(sketch, "E4.30.16.5", {"start": v(106.5, 57.74) * mm, "end": v(106.5, 54.85) * mm});
            skLineSegment(sketch, "E4.33.16.5", {"start": v(104, 59.18) * mm, "end": v(106.5, 57.74) * mm});
            skLineSegment(sketch, "E4.36.16.5", {"start": v(104.75, 52.1) * mm, "end": v(107.25, 53.55) * mm});
            skLineSegment(sketch, "E4.39.16.5", {"start": v(104.75, 49.22) * mm, "end": v(104.75, 52.1) * mm});
            skCircle(sketch, "E4.0.16.6", {"center": v(107.25, 61.92) * mm, "radius": 2.5 * mm, "construction": true});
            skCircle(sketch, "E4.2.16.6", {"center": v(104, 67.55) * mm, "radius": 2.5 * mm, "construction": true});
            skPoint(sketch, "E4.4.16.6", {"position": v(105.25, 69.72) * mm});
            skPoint(sketch, "E4.5.16.6", {"position": v(108.5, 64.09) * mm});
            skLineSegment(sketch, "E4.6.16.6", {"start": v(107.25, 59.03) * mm, "end": v(104.75, 60.48) * mm});
            skLineSegment(sketch, "E4.9.16.6", {"start": v(109.75, 60.48) * mm, "end": v(107.25, 59.03) * mm});
            skLineSegment(sketch, "E4.12.16.6", {"start": v(109.75, 63.36) * mm, "end": v(109.75, 60.48) * mm});
            skLineSegment(sketch, "E4.15.16.6", {"start": v(107.25, 64.8) * mm, "end": v(109.75, 63.36) * mm});
            skLineSegment(sketch, "E4.18.16.6", {"start": v(101.5, 69) * mm, "end": v(104, 70.44) * mm});
            skLineSegment(sketch, "E4.21.16.6", {"start": v(101.5, 66.1) * mm, "end": v(101.5, 69) * mm});
            skLineSegment(sketch, "E4.24.16.6", {"start": v(104, 64.66) * mm, "end": v(101.5, 66.1) * mm});
            skLineSegment(sketch, "E4.27.16.6", {"start": v(106.5, 66.1) * mm, "end": v(104, 64.66) * mm});
            skLineSegment(sketch, "E4.30.16.6", {"start": v(106.5, 69) * mm, "end": v(106.5, 66.1) * mm});
            skLineSegment(sketch, "E4.33.16.6", {"start": v(104, 70.44) * mm, "end": v(106.5, 69) * mm});
            skLineSegment(sketch, "E4.36.16.6", {"start": v(104.75, 63.36) * mm, "end": v(107.25, 64.8) * mm});
            skLineSegment(sketch, "E4.39.16.6", {"start": v(104.75, 60.48) * mm, "end": v(104.75, 63.36) * mm});
            skCircle(sketch, "E4.0.16.7", {"center": v(107.25, 73.18) * mm, "radius": 2.5 * mm, "construction": true});
            skCircle(sketch, "E4.2.16.7", {"center": v(104, 78.8) * mm, "radius": 2.5 * mm, "construction": true});
            skPoint(sketch, "E4.4.16.7", {"position": v(105.25, 80.97) * mm});
            skPoint(sketch, "E4.5.16.7", {"position": v(108.5, 75.34) * mm});
            skLineSegment(sketch, "E4.6.16.7", {"start": v(107.25, 70.3) * mm, "end": v(104.75, 71.74) * mm});
            skLineSegment(sketch, "E4.9.16.7", {"start": v(109.75, 71.74) * mm, "end": v(107.25, 70.3) * mm});
            skLineSegment(sketch, "E4.12.16.7", {"start": v(109.75, 74.62) * mm, "end": v(109.75, 71.74) * mm});
            skLineSegment(sketch, "E4.15.16.7", {"start": v(107.25, 76.07) * mm, "end": v(109.75, 74.62) * mm});
            skLineSegment(sketch, "E4.18.16.7", {"start": v(101.5, 80.25) * mm, "end": v(104, 81.7) * mm});
            skLineSegment(sketch, "E4.21.16.7", {"start": v(101.5, 77.36) * mm, "end": v(101.5, 80.25) * mm});
            skLineSegment(sketch, "E4.24.16.7", {"start": v(104, 75.92) * mm, "end": v(101.5, 77.36) * mm});
            skLineSegment(sketch, "E4.27.16.7", {"start": v(106.5, 77.36) * mm, "end": v(104, 75.92) * mm});
            skLineSegment(sketch, "E4.30.16.7", {"start": v(106.5, 80.25) * mm, "end": v(106.5, 77.36) * mm});
            skLineSegment(sketch, "E4.33.16.7", {"start": v(104, 81.7) * mm, "end": v(106.5, 80.25) * mm});
            skLineSegment(sketch, "E4.36.16.7", {"start": v(104.75, 74.62) * mm, "end": v(107.25, 76.07) * mm});
            skLineSegment(sketch, "E4.39.16.7", {"start": v(104.75, 71.74) * mm, "end": v(104.75, 74.62) * mm});
            skCircle(sketch, "E4.0.16.8", {"center": v(107.25, 84.44) * mm, "radius": 2.5 * mm, "construction": true});
            skCircle(sketch, "E4.2.16.8", {"center": v(104, 90.07) * mm, "radius": 2.5 * mm, "construction": true});
            skPoint(sketch, "E4.4.16.8", {"position": v(105.25, 92.23) * mm});
            skPoint(sketch, "E4.5.16.8", {"position": v(108.5, 86.6) * mm});
            skLineSegment(sketch, "E4.6.16.8", {"start": v(107.25, 81.55) * mm, "end": v(104.75, 83) * mm});
            skLineSegment(sketch, "E4.9.16.8", {"start": v(109.75, 83) * mm, "end": v(107.25, 81.55) * mm});
            skLineSegment(sketch, "E4.12.16.8", {"start": v(109.75, 85.88) * mm, "end": v(109.75, 83) * mm});
            skLineSegment(sketch, "E4.15.16.8", {"start": v(107.25, 87.32) * mm, "end": v(109.75, 85.88) * mm});
            skLineSegment(sketch, "E4.18.16.8", {"start": v(101.5, 91.51) * mm, "end": v(104, 92.95) * mm});
            skLineSegment(sketch, "E4.21.16.8", {"start": v(101.5, 88.62) * mm, "end": v(101.5, 91.51) * mm});
            skLineSegment(sketch, "E4.24.16.8", {"start": v(104, 87.18) * mm, "end": v(101.5, 88.62) * mm});
            skLineSegment(sketch, "E4.27.16.8", {"start": v(106.5, 88.62) * mm, "end": v(104, 87.18) * mm});
            skLineSegment(sketch, "E4.30.16.8", {"start": v(106.5, 91.51) * mm, "end": v(106.5, 88.62) * mm});
            skLineSegment(sketch, "E4.33.16.8", {"start": v(104, 92.95) * mm, "end": v(106.5, 91.51) * mm});
            skLineSegment(sketch, "E4.36.16.8", {"start": v(104.75, 85.88) * mm, "end": v(107.25, 87.32) * mm});
            skLineSegment(sketch, "E4.39.16.8", {"start": v(104.75, 83) * mm, "end": v(104.75, 85.88) * mm});
            skCircle(sketch, "E4.0.16.9", {"center": v(107.25, 95.7) * mm, "radius": 2.5 * mm, "construction": true});
            skCircle(sketch, "E4.2.16.9", {"center": v(104, 101.32) * mm, "radius": 2.5 * mm, "construction": true});
            skPoint(sketch, "E4.4.16.9", {"position": v(105.25, 103.5) * mm});
            skPoint(sketch, "E4.5.16.9", {"position": v(108.5, 97.86) * mm});
            skLineSegment(sketch, "E4.6.16.9", {"start": v(107.25, 92.8) * mm, "end": v(104.75, 94.25) * mm});
            skLineSegment(sketch, "E4.9.16.9", {"start": v(109.75, 94.25) * mm, "end": v(107.25, 92.8) * mm});
            skLineSegment(sketch, "E4.12.16.9", {"start": v(109.75, 97.14) * mm, "end": v(109.75, 94.25) * mm});
            skLineSegment(sketch, "E4.15.16.9", {"start": v(107.25, 98.58) * mm, "end": v(109.75, 97.14) * mm});
            skLineSegment(sketch, "E4.18.16.9", {"start": v(101.5, 102.77) * mm, "end": v(104, 104.21) * mm});
            skLineSegment(sketch, "E4.21.16.9", {"start": v(101.5, 99.88) * mm, "end": v(101.5, 102.77) * mm});
            skLineSegment(sketch, "E4.24.16.9", {"start": v(104, 98.44) * mm, "end": v(101.5, 99.88) * mm});
            skLineSegment(sketch, "E4.27.16.9", {"start": v(106.5, 99.88) * mm, "end": v(104, 98.44) * mm});
            skLineSegment(sketch, "E4.30.16.9", {"start": v(106.5, 102.77) * mm, "end": v(106.5, 99.88) * mm});
            skLineSegment(sketch, "E4.33.16.9", {"start": v(104, 104.21) * mm, "end": v(106.5, 102.77) * mm});
            skLineSegment(sketch, "E4.36.16.9", {"start": v(104.75, 97.14) * mm, "end": v(107.25, 98.58) * mm});
            skLineSegment(sketch, "E4.39.16.9", {"start": v(104.75, 94.25) * mm, "end": v(104.75, 97.14) * mm});
            skCircle(sketch, "E4.0.17.0", {"center": v(113.75, -5.63) * mm, "radius": 2.5 * mm, "construction": true});
            skCircle(sketch, "E4.2.17.0", {"center": v(110.5, 0) * mm, "radius": 2.5 * mm, "construction": true});
            skPoint(sketch, "E4.4.17.0", {"position": v(111.75, 2.17) * mm});
            skPoint(sketch, "E4.5.17.0", {"position": v(115, -3.46) * mm});
            skLineSegment(sketch, "E4.6.17.0", {"start": v(113.75, -8.52) * mm, "end": v(111.25, -7.07) * mm});
            skLineSegment(sketch, "E4.9.17.0", {"start": v(116.25, -7.07) * mm, "end": v(113.75, -8.52) * mm});
            skLineSegment(sketch, "E4.12.17.0", {"start": v(116.25, -4.19) * mm, "end": v(116.25, -7.07) * mm});
            skLineSegment(sketch, "E4.15.17.0", {"start": v(113.75, -2.74) * mm, "end": v(116.25, -4.19) * mm});
            skLineSegment(sketch, "E4.18.17.0", {"start": v(108, 1.44) * mm, "end": v(110.5, 2.89) * mm});
            skLineSegment(sketch, "E4.21.17.0", {"start": v(108, -1.44) * mm, "end": v(108, 1.44) * mm});
            skLineSegment(sketch, "E4.24.17.0", {"start": v(110.5, -2.89) * mm, "end": v(108, -1.44) * mm});
            skLineSegment(sketch, "E4.27.17.0", {"start": v(113, -1.44) * mm, "end": v(110.5, -2.89) * mm});
            skLineSegment(sketch, "E4.30.17.0", {"start": v(113, 1.44) * mm, "end": v(113, -1.44) * mm});
            skLineSegment(sketch, "E4.33.17.0", {"start": v(110.5, 2.89) * mm, "end": v(113, 1.44) * mm});
            skLineSegment(sketch, "E4.36.17.0", {"start": v(111.25, -4.19) * mm, "end": v(113.75, -2.74) * mm});
            skLineSegment(sketch, "E4.39.17.0", {"start": v(111.25, -7.07) * mm, "end": v(111.25, -4.19) * mm});
            skCircle(sketch, "E4.0.17.1", {"center": v(113.75, 5.63) * mm, "radius": 2.5 * mm, "construction": true});
            skCircle(sketch, "E4.2.17.1", {"center": v(110.5, 11.26) * mm, "radius": 2.5 * mm, "construction": true});
            skPoint(sketch, "E4.4.17.1", {"position": v(111.75, 13.42) * mm});
            skPoint(sketch, "E4.5.17.1", {"position": v(115, 7.8) * mm});
            skLineSegment(sketch, "E4.6.17.1", {"start": v(113.75, 2.74) * mm, "end": v(111.25, 4.19) * mm});
            skLineSegment(sketch, "E4.9.17.1", {"start": v(116.25, 4.19) * mm, "end": v(113.75, 2.74) * mm});
            skLineSegment(sketch, "E4.12.17.1", {"start": v(116.25, 7.07) * mm, "end": v(116.25, 4.19) * mm});
            skLineSegment(sketch, "E4.15.17.1", {"start": v(113.75, 8.52) * mm, "end": v(116.25, 7.07) * mm});
            skLineSegment(sketch, "E4.18.17.1", {"start": v(108, 12.7) * mm, "end": v(110.5, 14.15) * mm});
            skLineSegment(sketch, "E4.21.17.1", {"start": v(108, 9.81) * mm, "end": v(108, 12.7) * mm});
            skLineSegment(sketch, "E4.24.17.1", {"start": v(110.5, 8.37) * mm, "end": v(108, 9.81) * mm});
            skLineSegment(sketch, "E4.27.17.1", {"start": v(113, 9.81) * mm, "end": v(110.5, 8.37) * mm});
            skLineSegment(sketch, "E4.30.17.1", {"start": v(113, 12.7) * mm, "end": v(113, 9.81) * mm});
            skLineSegment(sketch, "E4.33.17.1", {"start": v(110.5, 14.15) * mm, "end": v(113, 12.7) * mm});
            skLineSegment(sketch, "E4.36.17.1", {"start": v(111.25, 7.07) * mm, "end": v(113.75, 8.52) * mm});
            skLineSegment(sketch, "E4.39.17.1", {"start": v(111.25, 4.19) * mm, "end": v(111.25, 7.07) * mm});
            skCircle(sketch, "E4.0.17.2", {"center": v(113.75, 16.89) * mm, "radius": 2.5 * mm, "construction": true});
            skCircle(sketch, "E4.2.17.2", {"center": v(110.5, 22.52) * mm, "radius": 2.5 * mm, "construction": true});
            skPoint(sketch, "E4.4.17.2", {"position": v(111.75, 24.68) * mm});
            skPoint(sketch, "E4.5.17.2", {"position": v(115, 19.05) * mm});
            skLineSegment(sketch, "E4.6.17.2", {"start": v(113.75, 14) * mm, "end": v(111.25, 15.44) * mm});
            skLineSegment(sketch, "E4.9.17.2", {"start": v(116.25, 15.44) * mm, "end": v(113.75, 14) * mm});
            skLineSegment(sketch, "E4.12.17.2", {"start": v(116.25, 18.33) * mm, "end": v(116.25, 15.44) * mm});
            skLineSegment(sketch, "E4.15.17.2", {"start": v(113.75, 19.77) * mm, "end": v(116.25, 18.33) * mm});
            skLineSegment(sketch, "E4.18.17.2", {"start": v(108, 23.96) * mm, "end": v(110.5, 25.4) * mm});
            skLineSegment(sketch, "E4.21.17.2", {"start": v(108, 21.07) * mm, "end": v(108, 23.96) * mm});
            skLineSegment(sketch, "E4.24.17.2", {"start": v(110.5, 19.63) * mm, "end": v(108, 21.07) * mm});
            skLineSegment(sketch, "E4.27.17.2", {"start": v(113, 21.07) * mm, "end": v(110.5, 19.63) * mm});
            skLineSegment(sketch, "E4.30.17.2", {"start": v(113, 23.96) * mm, "end": v(113, 21.07) * mm});
            skLineSegment(sketch, "E4.33.17.2", {"start": v(110.5, 25.4) * mm, "end": v(113, 23.96) * mm});
            skLineSegment(sketch, "E4.36.17.2", {"start": v(111.25, 18.33) * mm, "end": v(113.75, 19.77) * mm});
            skLineSegment(sketch, "E4.39.17.2", {"start": v(111.25, 15.44) * mm, "end": v(111.25, 18.33) * mm});
            skCircle(sketch, "E4.0.17.3", {"center": v(113.75, 28.15) * mm, "radius": 2.5 * mm, "construction": true});
            skCircle(sketch, "E4.2.17.3", {"center": v(110.5, 33.77) * mm, "radius": 2.5 * mm, "construction": true});
            skPoint(sketch, "E4.4.17.3", {"position": v(111.75, 35.94) * mm});
            skPoint(sketch, "E4.5.17.3", {"position": v(115, 30.31) * mm});
            skLineSegment(sketch, "E4.6.17.3", {"start": v(113.75, 25.26) * mm, "end": v(111.25, 26.7) * mm});
            skLineSegment(sketch, "E4.9.17.3", {"start": v(116.25, 26.7) * mm, "end": v(113.75, 25.26) * mm});
            skLineSegment(sketch, "E4.12.17.3", {"start": v(116.25, 29.59) * mm, "end": v(116.25, 26.7) * mm});
            skLineSegment(sketch, "E4.15.17.3", {"start": v(113.75, 31.03) * mm, "end": v(116.25, 29.59) * mm});
            skLineSegment(sketch, "E4.18.17.3", {"start": v(108, 35.22) * mm, "end": v(110.5, 36.66) * mm});
            skLineSegment(sketch, "E4.21.17.3", {"start": v(108, 32.33) * mm, "end": v(108, 35.22) * mm});
            skLineSegment(sketch, "E4.24.17.3", {"start": v(110.5, 30.89) * mm, "end": v(108, 32.33) * mm});
            skLineSegment(sketch, "E4.27.17.3", {"start": v(113, 32.33) * mm, "end": v(110.5, 30.89) * mm});
            skLineSegment(sketch, "E4.30.17.3", {"start": v(113, 35.22) * mm, "end": v(113, 32.33) * mm});
            skLineSegment(sketch, "E4.33.17.3", {"start": v(110.5, 36.66) * mm, "end": v(113, 35.22) * mm});
            skLineSegment(sketch, "E4.36.17.3", {"start": v(111.25, 29.59) * mm, "end": v(113.75, 31.03) * mm});
            skLineSegment(sketch, "E4.39.17.3", {"start": v(111.25, 26.7) * mm, "end": v(111.25, 29.59) * mm});
            skCircle(sketch, "E4.0.17.4", {"center": v(113.75, 39.4) * mm, "radius": 2.5 * mm, "construction": true});
            skCircle(sketch, "E4.2.17.4", {"center": v(110.5, 45.03) * mm, "radius": 2.5 * mm, "construction": true});
            skPoint(sketch, "E4.4.17.4", {"position": v(111.75, 47.2) * mm});
            skPoint(sketch, "E4.5.17.4", {"position": v(115, 41.57) * mm});
            skLineSegment(sketch, "E4.6.17.4", {"start": v(113.75, 36.52) * mm, "end": v(111.25, 37.96) * mm});
            skLineSegment(sketch, "E4.9.17.4", {"start": v(116.25, 37.96) * mm, "end": v(113.75, 36.52) * mm});
            skLineSegment(sketch, "E4.12.17.4", {"start": v(116.25, 40.85) * mm, "end": v(116.25, 37.96) * mm});
            skLineSegment(sketch, "E4.15.17.4", {"start": v(113.75, 42.3) * mm, "end": v(116.25, 40.85) * mm});
            skLineSegment(sketch, "E4.18.17.4", {"start": v(108, 46.48) * mm, "end": v(110.5, 47.92) * mm});
            skLineSegment(sketch, "E4.21.17.4", {"start": v(108, 43.59) * mm, "end": v(108, 46.48) * mm});
            skLineSegment(sketch, "E4.24.17.4", {"start": v(110.5, 42.15) * mm, "end": v(108, 43.59) * mm});
            skLineSegment(sketch, "E4.27.17.4", {"start": v(113, 43.59) * mm, "end": v(110.5, 42.15) * mm});
            skLineSegment(sketch, "E4.30.17.4", {"start": v(113, 46.48) * mm, "end": v(113, 43.59) * mm});
            skLineSegment(sketch, "E4.33.17.4", {"start": v(110.5, 47.92) * mm, "end": v(113, 46.48) * mm});
            skLineSegment(sketch, "E4.36.17.4", {"start": v(111.25, 40.85) * mm, "end": v(113.75, 42.3) * mm});
            skLineSegment(sketch, "E4.39.17.4", {"start": v(111.25, 37.96) * mm, "end": v(111.25, 40.85) * mm});
            skCircle(sketch, "E4.0.17.5", {"center": v(113.75, 50.66) * mm, "radius": 2.5 * mm, "construction": true});
            skCircle(sketch, "E4.2.17.5", {"center": v(110.5, 56.3) * mm, "radius": 2.5 * mm, "construction": true});
            skPoint(sketch, "E4.4.17.5", {"position": v(111.75, 58.46) * mm});
            skPoint(sketch, "E4.5.17.5", {"position": v(115, 52.83) * mm});
            skLineSegment(sketch, "E4.6.17.5", {"start": v(113.75, 47.78) * mm, "end": v(111.25, 49.22) * mm});
            skLineSegment(sketch, "E4.9.17.5", {"start": v(116.25, 49.22) * mm, "end": v(113.75, 47.78) * mm});
            skLineSegment(sketch, "E4.12.17.5", {"start": v(116.25, 52.1) * mm, "end": v(116.25, 49.22) * mm});
            skLineSegment(sketch, "E4.15.17.5", {"start": v(113.75, 53.55) * mm, "end": v(116.25, 52.1) * mm});
            skLineSegment(sketch, "E4.18.17.5", {"start": v(108, 57.74) * mm, "end": v(110.5, 59.18) * mm});
            skLineSegment(sketch, "E4.21.17.5", {"start": v(108, 54.85) * mm, "end": v(108, 57.74) * mm});
            skLineSegment(sketch, "E4.24.17.5", {"start": v(110.5, 53.4) * mm, "end": v(108, 54.85) * mm});
            skLineSegment(sketch, "E4.27.17.5", {"start": v(113, 54.85) * mm, "end": v(110.5, 53.4) * mm});
            skLineSegment(sketch, "E4.30.17.5", {"start": v(113, 57.74) * mm, "end": v(113, 54.85) * mm});
            skLineSegment(sketch, "E4.33.17.5", {"start": v(110.5, 59.18) * mm, "end": v(113, 57.74) * mm});
            skLineSegment(sketch, "E4.36.17.5", {"start": v(111.25, 52.1) * mm, "end": v(113.75, 53.55) * mm});
            skLineSegment(sketch, "E4.39.17.5", {"start": v(111.25, 49.22) * mm, "end": v(111.25, 52.1) * mm});
            skCircle(sketch, "E4.0.17.6", {"center": v(113.75, 61.92) * mm, "radius": 2.5 * mm, "construction": true});
            skCircle(sketch, "E4.2.17.6", {"center": v(110.5, 67.55) * mm, "radius": 2.5 * mm, "construction": true});
            skPoint(sketch, "E4.4.17.6", {"position": v(111.75, 69.72) * mm});
            skPoint(sketch, "E4.5.17.6", {"position": v(115, 64.09) * mm});
            skLineSegment(sketch, "E4.6.17.6", {"start": v(113.75, 59.03) * mm, "end": v(111.25, 60.48) * mm});
            skLineSegment(sketch, "E4.9.17.6", {"start": v(116.25, 60.48) * mm, "end": v(113.75, 59.03) * mm});
            skLineSegment(sketch, "E4.12.17.6", {"start": v(116.25, 63.36) * mm, "end": v(116.25, 60.48) * mm});
            skLineSegment(sketch, "E4.15.17.6", {"start": v(113.75, 64.8) * mm, "end": v(116.25, 63.36) * mm});
            skLineSegment(sketch, "E4.18.17.6", {"start": v(108, 69) * mm, "end": v(110.5, 70.44) * mm});
            skLineSegment(sketch, "E4.21.17.6", {"start": v(108, 66.1) * mm, "end": v(108, 69) * mm});
            skLineSegment(sketch, "E4.24.17.6", {"start": v(110.5, 64.66) * mm, "end": v(108, 66.1) * mm});
            skLineSegment(sketch, "E4.27.17.6", {"start": v(113, 66.1) * mm, "end": v(110.5, 64.66) * mm});
            skLineSegment(sketch, "E4.30.17.6", {"start": v(113, 69) * mm, "end": v(113, 66.1) * mm});
            skLineSegment(sketch, "E4.33.17.6", {"start": v(110.5, 70.44) * mm, "end": v(113, 69) * mm});
            skLineSegment(sketch, "E4.36.17.6", {"start": v(111.25, 63.36) * mm, "end": v(113.75, 64.8) * mm});
            skLineSegment(sketch, "E4.39.17.6", {"start": v(111.25, 60.48) * mm, "end": v(111.25, 63.36) * mm});
            skCircle(sketch, "E4.0.17.7", {"center": v(113.75, 73.18) * mm, "radius": 2.5 * mm, "construction": true});
            skCircle(sketch, "E4.2.17.7", {"center": v(110.5, 78.8) * mm, "radius": 2.5 * mm, "construction": true});
            skPoint(sketch, "E4.4.17.7", {"position": v(111.75, 80.97) * mm});
            skPoint(sketch, "E4.5.17.7", {"position": v(115, 75.34) * mm});
            skLineSegment(sketch, "E4.6.17.7", {"start": v(113.75, 70.3) * mm, "end": v(111.25, 71.74) * mm});
            skLineSegment(sketch, "E4.9.17.7", {"start": v(116.25, 71.74) * mm, "end": v(113.75, 70.3) * mm});
            skLineSegment(sketch, "E4.12.17.7", {"start": v(116.25, 74.62) * mm, "end": v(116.25, 71.74) * mm});
            skLineSegment(sketch, "E4.15.17.7", {"start": v(113.75, 76.07) * mm, "end": v(116.25, 74.62) * mm});
            skLineSegment(sketch, "E4.18.17.7", {"start": v(108, 80.25) * mm, "end": v(110.5, 81.7) * mm});
            skLineSegment(sketch, "E4.21.17.7", {"start": v(108, 77.36) * mm, "end": v(108, 80.25) * mm});
            skLineSegment(sketch, "E4.24.17.7", {"start": v(110.5, 75.92) * mm, "end": v(108, 77.36) * mm});
            skLineSegment(sketch, "E4.27.17.7", {"start": v(113, 77.36) * mm, "end": v(110.5, 75.92) * mm});
            skLineSegment(sketch, "E4.30.17.7", {"start": v(113, 80.25) * mm, "end": v(113, 77.36) * mm});
            skLineSegment(sketch, "E4.33.17.7", {"start": v(110.5, 81.7) * mm, "end": v(113, 80.25) * mm});
            skLineSegment(sketch, "E4.36.17.7", {"start": v(111.25, 74.62) * mm, "end": v(113.75, 76.07) * mm});
            skLineSegment(sketch, "E4.39.17.7", {"start": v(111.25, 71.74) * mm, "end": v(111.25, 74.62) * mm});
            skCircle(sketch, "E4.0.17.8", {"center": v(113.75, 84.44) * mm, "radius": 2.5 * mm, "construction": true});
            skCircle(sketch, "E4.2.17.8", {"center": v(110.5, 90.07) * mm, "radius": 2.5 * mm, "construction": true});
            skPoint(sketch, "E4.4.17.8", {"position": v(111.75, 92.23) * mm});
            skPoint(sketch, "E4.5.17.8", {"position": v(115, 86.6) * mm});
            skLineSegment(sketch, "E4.6.17.8", {"start": v(113.75, 81.55) * mm, "end": v(111.25, 83) * mm});
            skLineSegment(sketch, "E4.9.17.8", {"start": v(116.25, 83) * mm, "end": v(113.75, 81.55) * mm});
            skLineSegment(sketch, "E4.12.17.8", {"start": v(116.25, 85.88) * mm, "end": v(116.25, 83) * mm});
            skLineSegment(sketch, "E4.15.17.8", {"start": v(113.75, 87.32) * mm, "end": v(116.25, 85.88) * mm});
            skLineSegment(sketch, "E4.18.17.8", {"start": v(108, 91.51) * mm, "end": v(110.5, 92.95) * mm});
            skLineSegment(sketch, "E4.21.17.8", {"start": v(108, 88.62) * mm, "end": v(108, 91.51) * mm});
            skLineSegment(sketch, "E4.24.17.8", {"start": v(110.5, 87.18) * mm, "end": v(108, 88.62) * mm});
            skLineSegment(sketch, "E4.27.17.8", {"start": v(113, 88.62) * mm, "end": v(110.5, 87.18) * mm});
            skLineSegment(sketch, "E4.30.17.8", {"start": v(113, 91.51) * mm, "end": v(113, 88.62) * mm});
            skLineSegment(sketch, "E4.33.17.8", {"start": v(110.5, 92.95) * mm, "end": v(113, 91.51) * mm});
            skLineSegment(sketch, "E4.36.17.8", {"start": v(111.25, 85.88) * mm, "end": v(113.75, 87.32) * mm});
            skLineSegment(sketch, "E4.39.17.8", {"start": v(111.25, 83) * mm, "end": v(111.25, 85.88) * mm});
            skCircle(sketch, "E4.0.17.9", {"center": v(113.75, 95.7) * mm, "radius": 2.5 * mm, "construction": true});
            skCircle(sketch, "E4.2.17.9", {"center": v(110.5, 101.32) * mm, "radius": 2.5 * mm, "construction": true});
            skPoint(sketch, "E4.4.17.9", {"position": v(111.75, 103.5) * mm});
            skPoint(sketch, "E4.5.17.9", {"position": v(115, 97.86) * mm});
            skLineSegment(sketch, "E4.6.17.9", {"start": v(113.75, 92.8) * mm, "end": v(111.25, 94.25) * mm});
            skLineSegment(sketch, "E4.9.17.9", {"start": v(116.25, 94.25) * mm, "end": v(113.75, 92.8) * mm});
            skLineSegment(sketch, "E4.12.17.9", {"start": v(116.25, 97.14) * mm, "end": v(116.25, 94.25) * mm});
            skLineSegment(sketch, "E4.15.17.9", {"start": v(113.75, 98.58) * mm, "end": v(116.25, 97.14) * mm});
            skLineSegment(sketch, "E4.18.17.9", {"start": v(108, 102.77) * mm, "end": v(110.5, 104.21) * mm});
            skLineSegment(sketch, "E4.21.17.9", {"start": v(108, 99.88) * mm, "end": v(108, 102.77) * mm});
            skLineSegment(sketch, "E4.24.17.9", {"start": v(110.5, 98.44) * mm, "end": v(108, 99.88) * mm});
            skLineSegment(sketch, "E4.27.17.9", {"start": v(113, 99.88) * mm, "end": v(110.5, 98.44) * mm});
            skLineSegment(sketch, "E4.30.17.9", {"start": v(113, 102.77) * mm, "end": v(113, 99.88) * mm});
            skLineSegment(sketch, "E4.33.17.9", {"start": v(110.5, 104.21) * mm, "end": v(113, 102.77) * mm});
            skLineSegment(sketch, "E4.36.17.9", {"start": v(111.25, 97.14) * mm, "end": v(113.75, 98.58) * mm});
            skLineSegment(sketch, "E4.39.17.9", {"start": v(111.25, 94.25) * mm, "end": v(111.25, 97.14) * mm});
            skCircle(sketch, "E4.0.18.0", {"center": v(120.25, -5.63) * mm, "radius": 2.5 * mm, "construction": true});
            skCircle(sketch, "E4.2.18.0", {"center": v(117, 0) * mm, "radius": 2.5 * mm, "construction": true});
            skPoint(sketch, "E4.4.18.0", {"position": v(118.25, 2.17) * mm});
            skPoint(sketch, "E4.5.18.0", {"position": v(121.5, -3.46) * mm});
            skLineSegment(sketch, "E4.6.18.0", {"start": v(120.25, -8.52) * mm, "end": v(117.75, -7.07) * mm});
            skLineSegment(sketch, "E4.9.18.0", {"start": v(122.75, -7.07) * mm, "end": v(120.25, -8.52) * mm});
            skLineSegment(sketch, "E4.12.18.0", {"start": v(122.75, -4.19) * mm, "end": v(122.75, -7.07) * mm});
            skLineSegment(sketch, "E4.15.18.0", {"start": v(120.25, -2.74) * mm, "end": v(122.75, -4.19) * mm});
            skLineSegment(sketch, "E4.18.18.0", {"start": v(114.5, 1.44) * mm, "end": v(117, 2.89) * mm});
            skLineSegment(sketch, "E4.21.18.0", {"start": v(114.5, -1.44) * mm, "end": v(114.5, 1.44) * mm});
            skLineSegment(sketch, "E4.24.18.0", {"start": v(117, -2.89) * mm, "end": v(114.5, -1.44) * mm});
            skLineSegment(sketch, "E4.27.18.0", {"start": v(119.5, -1.44) * mm, "end": v(117, -2.89) * mm});
            skLineSegment(sketch, "E4.30.18.0", {"start": v(119.5, 1.44) * mm, "end": v(119.5, -1.44) * mm});
            skLineSegment(sketch, "E4.33.18.0", {"start": v(117, 2.89) * mm, "end": v(119.5, 1.44) * mm});
            skLineSegment(sketch, "E4.36.18.0", {"start": v(117.75, -4.19) * mm, "end": v(120.25, -2.74) * mm});
            skLineSegment(sketch, "E4.39.18.0", {"start": v(117.75, -7.07) * mm, "end": v(117.75, -4.19) * mm});
            skCircle(sketch, "E4.0.18.1", {"center": v(120.25, 5.63) * mm, "radius": 2.5 * mm, "construction": true});
            skCircle(sketch, "E4.2.18.1", {"center": v(117, 11.26) * mm, "radius": 2.5 * mm, "construction": true});
            skPoint(sketch, "E4.4.18.1", {"position": v(118.25, 13.42) * mm});
            skPoint(sketch, "E4.5.18.1", {"position": v(121.5, 7.8) * mm});
            skLineSegment(sketch, "E4.6.18.1", {"start": v(120.25, 2.74) * mm, "end": v(117.75, 4.19) * mm});
            skLineSegment(sketch, "E4.9.18.1", {"start": v(122.75, 4.19) * mm, "end": v(120.25, 2.74) * mm});
            skLineSegment(sketch, "E4.12.18.1", {"start": v(122.75, 7.07) * mm, "end": v(122.75, 4.19) * mm});
            skLineSegment(sketch, "E4.15.18.1", {"start": v(120.25, 8.52) * mm, "end": v(122.75, 7.07) * mm});
            skLineSegment(sketch, "E4.18.18.1", {"start": v(114.5, 12.7) * mm, "end": v(117, 14.15) * mm});
            skLineSegment(sketch, "E4.21.18.1", {"start": v(114.5, 9.81) * mm, "end": v(114.5, 12.7) * mm});
            skLineSegment(sketch, "E4.24.18.1", {"start": v(117, 8.37) * mm, "end": v(114.5, 9.81) * mm});
            skLineSegment(sketch, "E4.27.18.1", {"start": v(119.5, 9.81) * mm, "end": v(117, 8.37) * mm});
            skLineSegment(sketch, "E4.30.18.1", {"start": v(119.5, 12.7) * mm, "end": v(119.5, 9.81) * mm});
            skLineSegment(sketch, "E4.33.18.1", {"start": v(117, 14.15) * mm, "end": v(119.5, 12.7) * mm});
            skLineSegment(sketch, "E4.36.18.1", {"start": v(117.75, 7.07) * mm, "end": v(120.25, 8.52) * mm});
            skLineSegment(sketch, "E4.39.18.1", {"start": v(117.75, 4.19) * mm, "end": v(117.75, 7.07) * mm});
            skCircle(sketch, "E4.0.18.2", {"center": v(120.25, 16.89) * mm, "radius": 2.5 * mm, "construction": true});
            skCircle(sketch, "E4.2.18.2", {"center": v(117, 22.52) * mm, "radius": 2.5 * mm, "construction": true});
            skPoint(sketch, "E4.4.18.2", {"position": v(118.25, 24.68) * mm});
            skPoint(sketch, "E4.5.18.2", {"position": v(121.5, 19.05) * mm});
            skLineSegment(sketch, "E4.6.18.2", {"start": v(120.25, 14) * mm, "end": v(117.75, 15.44) * mm});
            skLineSegment(sketch, "E4.9.18.2", {"start": v(122.75, 15.44) * mm, "end": v(120.25, 14) * mm});
            skLineSegment(sketch, "E4.12.18.2", {"start": v(122.75, 18.33) * mm, "end": v(122.75, 15.44) * mm});
            skLineSegment(sketch, "E4.15.18.2", {"start": v(120.25, 19.77) * mm, "end": v(122.75, 18.33) * mm});
            skLineSegment(sketch, "E4.18.18.2", {"start": v(114.5, 23.96) * mm, "end": v(117, 25.4) * mm});
            skLineSegment(sketch, "E4.21.18.2", {"start": v(114.5, 21.07) * mm, "end": v(114.5, 23.96) * mm});
            skLineSegment(sketch, "E4.24.18.2", {"start": v(117, 19.63) * mm, "end": v(114.5, 21.07) * mm});
            skLineSegment(sketch, "E4.27.18.2", {"start": v(119.5, 21.07) * mm, "end": v(117, 19.63) * mm});
            skLineSegment(sketch, "E4.30.18.2", {"start": v(119.5, 23.96) * mm, "end": v(119.5, 21.07) * mm});
            skLineSegment(sketch, "E4.33.18.2", {"start": v(117, 25.4) * mm, "end": v(119.5, 23.96) * mm});
            skLineSegment(sketch, "E4.36.18.2", {"start": v(117.75, 18.33) * mm, "end": v(120.25, 19.77) * mm});
            skLineSegment(sketch, "E4.39.18.2", {"start": v(117.75, 15.44) * mm, "end": v(117.75, 18.33) * mm});
            skCircle(sketch, "E4.0.18.3", {"center": v(120.25, 28.15) * mm, "radius": 2.5 * mm, "construction": true});
            skCircle(sketch, "E4.2.18.3", {"center": v(117, 33.77) * mm, "radius": 2.5 * mm, "construction": true});
            skPoint(sketch, "E4.4.18.3", {"position": v(118.25, 35.94) * mm});
            skPoint(sketch, "E4.5.18.3", {"position": v(121.5, 30.31) * mm});
            skLineSegment(sketch, "E4.6.18.3", {"start": v(120.25, 25.26) * mm, "end": v(117.75, 26.7) * mm});
            skLineSegment(sketch, "E4.9.18.3", {"start": v(122.75, 26.7) * mm, "end": v(120.25, 25.26) * mm});
            skLineSegment(sketch, "E4.12.18.3", {"start": v(122.75, 29.59) * mm, "end": v(122.75, 26.7) * mm});
            skLineSegment(sketch, "E4.15.18.3", {"start": v(120.25, 31.03) * mm, "end": v(122.75, 29.59) * mm});
            skLineSegment(sketch, "E4.18.18.3", {"start": v(114.5, 35.22) * mm, "end": v(117, 36.66) * mm});
            skLineSegment(sketch, "E4.21.18.3", {"start": v(114.5, 32.33) * mm, "end": v(114.5, 35.22) * mm});
            skLineSegment(sketch, "E4.24.18.3", {"start": v(117, 30.89) * mm, "end": v(114.5, 32.33) * mm});
            skLineSegment(sketch, "E4.27.18.3", {"start": v(119.5, 32.33) * mm, "end": v(117, 30.89) * mm});
            skLineSegment(sketch, "E4.30.18.3", {"start": v(119.5, 35.22) * mm, "end": v(119.5, 32.33) * mm});
            skLineSegment(sketch, "E4.33.18.3", {"start": v(117, 36.66) * mm, "end": v(119.5, 35.22) * mm});
            skLineSegment(sketch, "E4.36.18.3", {"start": v(117.75, 29.59) * mm, "end": v(120.25, 31.03) * mm});
            skLineSegment(sketch, "E4.39.18.3", {"start": v(117.75, 26.7) * mm, "end": v(117.75, 29.59) * mm});
            skCircle(sketch, "E4.0.18.4", {"center": v(120.25, 39.4) * mm, "radius": 2.5 * mm, "construction": true});
            skCircle(sketch, "E4.2.18.4", {"center": v(117, 45.03) * mm, "radius": 2.5 * mm, "construction": true});
            skPoint(sketch, "E4.4.18.4", {"position": v(118.25, 47.2) * mm});
            skPoint(sketch, "E4.5.18.4", {"position": v(121.5, 41.57) * mm});
            skLineSegment(sketch, "E4.6.18.4", {"start": v(120.25, 36.52) * mm, "end": v(117.75, 37.96) * mm});
            skLineSegment(sketch, "E4.9.18.4", {"start": v(122.75, 37.96) * mm, "end": v(120.25, 36.52) * mm});
            skLineSegment(sketch, "E4.12.18.4", {"start": v(122.75, 40.85) * mm, "end": v(122.75, 37.96) * mm});
            skLineSegment(sketch, "E4.15.18.4", {"start": v(120.25, 42.3) * mm, "end": v(122.75, 40.85) * mm});
            skLineSegment(sketch, "E4.18.18.4", {"start": v(114.5, 46.48) * mm, "end": v(117, 47.92) * mm});
            skLineSegment(sketch, "E4.21.18.4", {"start": v(114.5, 43.59) * mm, "end": v(114.5, 46.48) * mm});
            skLineSegment(sketch, "E4.24.18.4", {"start": v(117, 42.15) * mm, "end": v(114.5, 43.59) * mm});
            skLineSegment(sketch, "E4.27.18.4", {"start": v(119.5, 43.59) * mm, "end": v(117, 42.15) * mm});
            skLineSegment(sketch, "E4.30.18.4", {"start": v(119.5, 46.48) * mm, "end": v(119.5, 43.59) * mm});
            skLineSegment(sketch, "E4.33.18.4", {"start": v(117, 47.92) * mm, "end": v(119.5, 46.48) * mm});
            skLineSegment(sketch, "E4.36.18.4", {"start": v(117.75, 40.85) * mm, "end": v(120.25, 42.3) * mm});
            skLineSegment(sketch, "E4.39.18.4", {"start": v(117.75, 37.96) * mm, "end": v(117.75, 40.85) * mm});
            skCircle(sketch, "E4.0.18.5", {"center": v(120.25, 50.66) * mm, "radius": 2.5 * mm, "construction": true});
            skCircle(sketch, "E4.2.18.5", {"center": v(117, 56.3) * mm, "radius": 2.5 * mm, "construction": true});
            skPoint(sketch, "E4.4.18.5", {"position": v(118.25, 58.46) * mm});
            skPoint(sketch, "E4.5.18.5", {"position": v(121.5, 52.83) * mm});
            skLineSegment(sketch, "E4.6.18.5", {"start": v(120.25, 47.78) * mm, "end": v(117.75, 49.22) * mm});
            skLineSegment(sketch, "E4.9.18.5", {"start": v(122.75, 49.22) * mm, "end": v(120.25, 47.78) * mm});
            skLineSegment(sketch, "E4.12.18.5", {"start": v(122.75, 52.1) * mm, "end": v(122.75, 49.22) * mm});
            skLineSegment(sketch, "E4.15.18.5", {"start": v(120.25, 53.55) * mm, "end": v(122.75, 52.1) * mm});
            skLineSegment(sketch, "E4.18.18.5", {"start": v(114.5, 57.74) * mm, "end": v(117, 59.18) * mm});
            skLineSegment(sketch, "E4.21.18.5", {"start": v(114.5, 54.85) * mm, "end": v(114.5, 57.74) * mm});
            skLineSegment(sketch, "E4.24.18.5", {"start": v(117, 53.4) * mm, "end": v(114.5, 54.85) * mm});
            skLineSegment(sketch, "E4.27.18.5", {"start": v(119.5, 54.85) * mm, "end": v(117, 53.4) * mm});
            skLineSegment(sketch, "E4.30.18.5", {"start": v(119.5, 57.74) * mm, "end": v(119.5, 54.85) * mm});
            skLineSegment(sketch, "E4.33.18.5", {"start": v(117, 59.18) * mm, "end": v(119.5, 57.74) * mm});
            skLineSegment(sketch, "E4.36.18.5", {"start": v(117.75, 52.1) * mm, "end": v(120.25, 53.55) * mm});
            skLineSegment(sketch, "E4.39.18.5", {"start": v(117.75, 49.22) * mm, "end": v(117.75, 52.1) * mm});
            skCircle(sketch, "E4.0.18.6", {"center": v(120.25, 61.92) * mm, "radius": 2.5 * mm, "construction": true});
            skCircle(sketch, "E4.2.18.6", {"center": v(117, 67.55) * mm, "radius": 2.5 * mm, "construction": true});
            skPoint(sketch, "E4.4.18.6", {"position": v(118.25, 69.72) * mm});
            skPoint(sketch, "E4.5.18.6", {"position": v(121.5, 64.09) * mm});
            skLineSegment(sketch, "E4.6.18.6", {"start": v(120.25, 59.03) * mm, "end": v(117.75, 60.48) * mm});
            skLineSegment(sketch, "E4.9.18.6", {"start": v(122.75, 60.48) * mm, "end": v(120.25, 59.03) * mm});
            skLineSegment(sketch, "E4.12.18.6", {"start": v(122.75, 63.36) * mm, "end": v(122.75, 60.48) * mm});
            skLineSegment(sketch, "E4.15.18.6", {"start": v(120.25, 64.8) * mm, "end": v(122.75, 63.36) * mm});
            skLineSegment(sketch, "E4.18.18.6", {"start": v(114.5, 69) * mm, "end": v(117, 70.44) * mm});
            skLineSegment(sketch, "E4.21.18.6", {"start": v(114.5, 66.1) * mm, "end": v(114.5, 69) * mm});
            skLineSegment(sketch, "E4.24.18.6", {"start": v(117, 64.66) * mm, "end": v(114.5, 66.1) * mm});
            skLineSegment(sketch, "E4.27.18.6", {"start": v(119.5, 66.1) * mm, "end": v(117, 64.66) * mm});
            skLineSegment(sketch, "E4.30.18.6", {"start": v(119.5, 69) * mm, "end": v(119.5, 66.1) * mm});
            skLineSegment(sketch, "E4.33.18.6", {"start": v(117, 70.44) * mm, "end": v(119.5, 69) * mm});
            skLineSegment(sketch, "E4.36.18.6", {"start": v(117.75, 63.36) * mm, "end": v(120.25, 64.8) * mm});
            skLineSegment(sketch, "E4.39.18.6", {"start": v(117.75, 60.48) * mm, "end": v(117.75, 63.36) * mm});
            skCircle(sketch, "E4.0.18.7", {"center": v(120.25, 73.18) * mm, "radius": 2.5 * mm, "construction": true});
            skCircle(sketch, "E4.2.18.7", {"center": v(117, 78.8) * mm, "radius": 2.5 * mm, "construction": true});
            skPoint(sketch, "E4.4.18.7", {"position": v(118.25, 80.97) * mm});
            skPoint(sketch, "E4.5.18.7", {"position": v(121.5, 75.34) * mm});
            skLineSegment(sketch, "E4.6.18.7", {"start": v(120.25, 70.3) * mm, "end": v(117.75, 71.74) * mm});
            skLineSegment(sketch, "E4.9.18.7", {"start": v(122.75, 71.74) * mm, "end": v(120.25, 70.3) * mm});
            skLineSegment(sketch, "E4.12.18.7", {"start": v(122.75, 74.62) * mm, "end": v(122.75, 71.74) * mm});
            skLineSegment(sketch, "E4.15.18.7", {"start": v(120.25, 76.07) * mm, "end": v(122.75, 74.62) * mm});
            skLineSegment(sketch, "E4.18.18.7", {"start": v(114.5, 80.25) * mm, "end": v(117, 81.7) * mm});
            skLineSegment(sketch, "E4.21.18.7", {"start": v(114.5, 77.36) * mm, "end": v(114.5, 80.25) * mm});
            skLineSegment(sketch, "E4.24.18.7", {"start": v(117, 75.92) * mm, "end": v(114.5, 77.36) * mm});
            skLineSegment(sketch, "E4.27.18.7", {"start": v(119.5, 77.36) * mm, "end": v(117, 75.92) * mm});
            skLineSegment(sketch, "E4.30.18.7", {"start": v(119.5, 80.25) * mm, "end": v(119.5, 77.36) * mm});
            skLineSegment(sketch, "E4.33.18.7", {"start": v(117, 81.7) * mm, "end": v(119.5, 80.25) * mm});
            skLineSegment(sketch, "E4.36.18.7", {"start": v(117.75, 74.62) * mm, "end": v(120.25, 76.07) * mm});
            skLineSegment(sketch, "E4.39.18.7", {"start": v(117.75, 71.74) * mm, "end": v(117.75, 74.62) * mm});
            skCircle(sketch, "E4.0.18.8", {"center": v(120.25, 84.44) * mm, "radius": 2.5 * mm, "construction": true});
            skCircle(sketch, "E4.2.18.8", {"center": v(117, 90.07) * mm, "radius": 2.5 * mm, "construction": true});
            skPoint(sketch, "E4.4.18.8", {"position": v(118.25, 92.23) * mm});
            skPoint(sketch, "E4.5.18.8", {"position": v(121.5, 86.6) * mm});
            skLineSegment(sketch, "E4.6.18.8", {"start": v(120.25, 81.55) * mm, "end": v(117.75, 83) * mm});
            skLineSegment(sketch, "E4.9.18.8", {"start": v(122.75, 83) * mm, "end": v(120.25, 81.55) * mm});
            skLineSegment(sketch, "E4.12.18.8", {"start": v(122.75, 85.88) * mm, "end": v(122.75, 83) * mm});
            skLineSegment(sketch, "E4.15.18.8", {"start": v(120.25, 87.32) * mm, "end": v(122.75, 85.88) * mm});
            skLineSegment(sketch, "E4.18.18.8", {"start": v(114.5, 91.51) * mm, "end": v(117, 92.95) * mm});
            skLineSegment(sketch, "E4.21.18.8", {"start": v(114.5, 88.62) * mm, "end": v(114.5, 91.51) * mm});
            skLineSegment(sketch, "E4.24.18.8", {"start": v(117, 87.18) * mm, "end": v(114.5, 88.62) * mm});
            skLineSegment(sketch, "E4.27.18.8", {"start": v(119.5, 88.62) * mm, "end": v(117, 87.18) * mm});
            skLineSegment(sketch, "E4.30.18.8", {"start": v(119.5, 91.51) * mm, "end": v(119.5, 88.62) * mm});
            skLineSegment(sketch, "E4.33.18.8", {"start": v(117, 92.95) * mm, "end": v(119.5, 91.51) * mm});
            skLineSegment(sketch, "E4.36.18.8", {"start": v(117.75, 85.88) * mm, "end": v(120.25, 87.32) * mm});
            skLineSegment(sketch, "E4.39.18.8", {"start": v(117.75, 83) * mm, "end": v(117.75, 85.88) * mm});
            skCircle(sketch, "E4.0.18.9", {"center": v(120.25, 95.7) * mm, "radius": 2.5 * mm, "construction": true});
            skCircle(sketch, "E4.2.18.9", {"center": v(117, 101.32) * mm, "radius": 2.5 * mm, "construction": true});
            skPoint(sketch, "E4.4.18.9", {"position": v(118.25, 103.5) * mm});
            skPoint(sketch, "E4.5.18.9", {"position": v(121.5, 97.86) * mm});
            skLineSegment(sketch, "E4.6.18.9", {"start": v(120.25, 92.8) * mm, "end": v(117.75, 94.25) * mm});
            skLineSegment(sketch, "E4.9.18.9", {"start": v(122.75, 94.25) * mm, "end": v(120.25, 92.8) * mm});
            skLineSegment(sketch, "E4.12.18.9", {"start": v(122.75, 97.14) * mm, "end": v(122.75, 94.25) * mm});
            skLineSegment(sketch, "E4.15.18.9", {"start": v(120.25, 98.58) * mm, "end": v(122.75, 97.14) * mm});
            skLineSegment(sketch, "E4.18.18.9", {"start": v(114.5, 102.77) * mm, "end": v(117, 104.21) * mm});
            skLineSegment(sketch, "E4.21.18.9", {"start": v(114.5, 99.88) * mm, "end": v(114.5, 102.77) * mm});
            skLineSegment(sketch, "E4.24.18.9", {"start": v(117, 98.44) * mm, "end": v(114.5, 99.88) * mm});
            skLineSegment(sketch, "E4.27.18.9", {"start": v(119.5, 99.88) * mm, "end": v(117, 98.44) * mm});
            skLineSegment(sketch, "E4.30.18.9", {"start": v(119.5, 102.77) * mm, "end": v(119.5, 99.88) * mm});
            skLineSegment(sketch, "E4.33.18.9", {"start": v(117, 104.21) * mm, "end": v(119.5, 102.77) * mm});
            skLineSegment(sketch, "E4.36.18.9", {"start": v(117.75, 97.14) * mm, "end": v(120.25, 98.58) * mm});
            skLineSegment(sketch, "E4.39.18.9", {"start": v(117.75, 94.25) * mm, "end": v(117.75, 97.14) * mm});
            skCircle(sketch, "E4.0.19.0", {"center": v(126.75, -5.63) * mm, "radius": 2.5 * mm, "construction": true});
            skCircle(sketch, "E4.2.19.0", {"center": v(123.5, 0) * mm, "radius": 2.5 * mm, "construction": true});
            skPoint(sketch, "E4.4.19.0", {"position": v(124.75, 2.17) * mm});
            skPoint(sketch, "E4.5.19.0", {"position": v(128, -3.46) * mm});
            skLineSegment(sketch, "E4.6.19.0", {"start": v(126.75, -8.52) * mm, "end": v(124.25, -7.07) * mm});
            skLineSegment(sketch, "E4.9.19.0", {"start": v(129.25, -7.07) * mm, "end": v(126.75, -8.52) * mm});
            skLineSegment(sketch, "E4.12.19.0", {"start": v(129.25, -4.19) * mm, "end": v(129.25, -7.07) * mm});
            skLineSegment(sketch, "E4.15.19.0", {"start": v(126.75, -2.74) * mm, "end": v(129.25, -4.19) * mm});
            skLineSegment(sketch, "E4.18.19.0", {"start": v(121, 1.44) * mm, "end": v(123.5, 2.89) * mm});
            skLineSegment(sketch, "E4.21.19.0", {"start": v(121, -1.44) * mm, "end": v(121, 1.44) * mm});
            skLineSegment(sketch, "E4.24.19.0", {"start": v(123.5, -2.89) * mm, "end": v(121, -1.44) * mm});
            skLineSegment(sketch, "E4.27.19.0", {"start": v(126, -1.44) * mm, "end": v(123.5, -2.89) * mm});
            skLineSegment(sketch, "E4.30.19.0", {"start": v(126, 1.44) * mm, "end": v(126, -1.44) * mm});
            skLineSegment(sketch, "E4.33.19.0", {"start": v(123.5, 2.89) * mm, "end": v(126, 1.44) * mm});
            skLineSegment(sketch, "E4.36.19.0", {"start": v(124.25, -4.19) * mm, "end": v(126.75, -2.74) * mm});
            skLineSegment(sketch, "E4.39.19.0", {"start": v(124.25, -7.07) * mm, "end": v(124.25, -4.19) * mm});
            skCircle(sketch, "E4.0.19.1", {"center": v(126.75, 5.63) * mm, "radius": 2.5 * mm, "construction": true});
            skCircle(sketch, "E4.2.19.1", {"center": v(123.5, 11.26) * mm, "radius": 2.5 * mm, "construction": true});
            skPoint(sketch, "E4.4.19.1", {"position": v(124.75, 13.42) * mm});
            skPoint(sketch, "E4.5.19.1", {"position": v(128, 7.8) * mm});
            skLineSegment(sketch, "E4.6.19.1", {"start": v(126.75, 2.74) * mm, "end": v(124.25, 4.19) * mm});
            skLineSegment(sketch, "E4.9.19.1", {"start": v(129.25, 4.19) * mm, "end": v(126.75, 2.74) * mm});
            skLineSegment(sketch, "E4.12.19.1", {"start": v(129.25, 7.07) * mm, "end": v(129.25, 4.19) * mm});
            skLineSegment(sketch, "E4.15.19.1", {"start": v(126.75, 8.52) * mm, "end": v(129.25, 7.07) * mm});
            skLineSegment(sketch, "E4.18.19.1", {"start": v(121, 12.7) * mm, "end": v(123.5, 14.15) * mm});
            skLineSegment(sketch, "E4.21.19.1", {"start": v(121, 9.81) * mm, "end": v(121, 12.7) * mm});
            skLineSegment(sketch, "E4.24.19.1", {"start": v(123.5, 8.37) * mm, "end": v(121, 9.81) * mm});
            skLineSegment(sketch, "E4.27.19.1", {"start": v(126, 9.81) * mm, "end": v(123.5, 8.37) * mm});
            skLineSegment(sketch, "E4.30.19.1", {"start": v(126, 12.7) * mm, "end": v(126, 9.81) * mm});
            skLineSegment(sketch, "E4.33.19.1", {"start": v(123.5, 14.15) * mm, "end": v(126, 12.7) * mm});
            skLineSegment(sketch, "E4.36.19.1", {"start": v(124.25, 7.07) * mm, "end": v(126.75, 8.52) * mm});
            skLineSegment(sketch, "E4.39.19.1", {"start": v(124.25, 4.19) * mm, "end": v(124.25, 7.07) * mm});
            skCircle(sketch, "E4.0.19.2", {"center": v(126.75, 16.89) * mm, "radius": 2.5 * mm, "construction": true});
            skCircle(sketch, "E4.2.19.2", {"center": v(123.5, 22.52) * mm, "radius": 2.5 * mm, "construction": true});
            skPoint(sketch, "E4.4.19.2", {"position": v(124.75, 24.68) * mm});
            skPoint(sketch, "E4.5.19.2", {"position": v(128, 19.05) * mm});
            skLineSegment(sketch, "E4.6.19.2", {"start": v(126.75, 14) * mm, "end": v(124.25, 15.44) * mm});
            skLineSegment(sketch, "E4.9.19.2", {"start": v(129.25, 15.44) * mm, "end": v(126.75, 14) * mm});
            skLineSegment(sketch, "E4.12.19.2", {"start": v(129.25, 18.33) * mm, "end": v(129.25, 15.44) * mm});
            skLineSegment(sketch, "E4.15.19.2", {"start": v(126.75, 19.77) * mm, "end": v(129.25, 18.33) * mm});
            skLineSegment(sketch, "E4.18.19.2", {"start": v(121, 23.96) * mm, "end": v(123.5, 25.4) * mm});
            skLineSegment(sketch, "E4.21.19.2", {"start": v(121, 21.07) * mm, "end": v(121, 23.96) * mm});
            skLineSegment(sketch, "E4.24.19.2", {"start": v(123.5, 19.63) * mm, "end": v(121, 21.07) * mm});
            skLineSegment(sketch, "E4.27.19.2", {"start": v(126, 21.07) * mm, "end": v(123.5, 19.63) * mm});
            skLineSegment(sketch, "E4.30.19.2", {"start": v(126, 23.96) * mm, "end": v(126, 21.07) * mm});
            skLineSegment(sketch, "E4.33.19.2", {"start": v(123.5, 25.4) * mm, "end": v(126, 23.96) * mm});
            skLineSegment(sketch, "E4.36.19.2", {"start": v(124.25, 18.33) * mm, "end": v(126.75, 19.77) * mm});
            skLineSegment(sketch, "E4.39.19.2", {"start": v(124.25, 15.44) * mm, "end": v(124.25, 18.33) * mm});
            skCircle(sketch, "E4.0.19.3", {"center": v(126.75, 28.15) * mm, "radius": 2.5 * mm, "construction": true});
            skCircle(sketch, "E4.2.19.3", {"center": v(123.5, 33.77) * mm, "radius": 2.5 * mm, "construction": true});
            skPoint(sketch, "E4.4.19.3", {"position": v(124.75, 35.94) * mm});
            skPoint(sketch, "E4.5.19.3", {"position": v(128, 30.31) * mm});
            skLineSegment(sketch, "E4.6.19.3", {"start": v(126.75, 25.26) * mm, "end": v(124.25, 26.7) * mm});
            skLineSegment(sketch, "E4.9.19.3", {"start": v(129.25, 26.7) * mm, "end": v(126.75, 25.26) * mm});
            skLineSegment(sketch, "E4.12.19.3", {"start": v(129.25, 29.59) * mm, "end": v(129.25, 26.7) * mm});
            skLineSegment(sketch, "E4.15.19.3", {"start": v(126.75, 31.03) * mm, "end": v(129.25, 29.59) * mm});
            skLineSegment(sketch, "E4.18.19.3", {"start": v(121, 35.22) * mm, "end": v(123.5, 36.66) * mm});
            skLineSegment(sketch, "E4.21.19.3", {"start": v(121, 32.33) * mm, "end": v(121, 35.22) * mm});
            skLineSegment(sketch, "E4.24.19.3", {"start": v(123.5, 30.89) * mm, "end": v(121, 32.33) * mm});
            skLineSegment(sketch, "E4.27.19.3", {"start": v(126, 32.33) * mm, "end": v(123.5, 30.89) * mm});
            skLineSegment(sketch, "E4.30.19.3", {"start": v(126, 35.22) * mm, "end": v(126, 32.33) * mm});
            skLineSegment(sketch, "E4.33.19.3", {"start": v(123.5, 36.66) * mm, "end": v(126, 35.22) * mm});
            skLineSegment(sketch, "E4.36.19.3", {"start": v(124.25, 29.59) * mm, "end": v(126.75, 31.03) * mm});
            skLineSegment(sketch, "E4.39.19.3", {"start": v(124.25, 26.7) * mm, "end": v(124.25, 29.59) * mm});
            skCircle(sketch, "E4.0.19.4", {"center": v(126.75, 39.4) * mm, "radius": 2.5 * mm, "construction": true});
            skCircle(sketch, "E4.2.19.4", {"center": v(123.5, 45.03) * mm, "radius": 2.5 * mm, "construction": true});
            skPoint(sketch, "E4.4.19.4", {"position": v(124.75, 47.2) * mm});
            skPoint(sketch, "E4.5.19.4", {"position": v(128, 41.57) * mm});
            skLineSegment(sketch, "E4.6.19.4", {"start": v(126.75, 36.52) * mm, "end": v(124.25, 37.96) * mm});
            skLineSegment(sketch, "E4.9.19.4", {"start": v(129.25, 37.96) * mm, "end": v(126.75, 36.52) * mm});
            skLineSegment(sketch, "E4.12.19.4", {"start": v(129.25, 40.85) * mm, "end": v(129.25, 37.96) * mm});
            skLineSegment(sketch, "E4.15.19.4", {"start": v(126.75, 42.3) * mm, "end": v(129.25, 40.85) * mm});
            skLineSegment(sketch, "E4.18.19.4", {"start": v(121, 46.48) * mm, "end": v(123.5, 47.92) * mm});
            skLineSegment(sketch, "E4.21.19.4", {"start": v(121, 43.59) * mm, "end": v(121, 46.48) * mm});
            skLineSegment(sketch, "E4.24.19.4", {"start": v(123.5, 42.15) * mm, "end": v(121, 43.59) * mm});
            skLineSegment(sketch, "E4.27.19.4", {"start": v(126, 43.59) * mm, "end": v(123.5, 42.15) * mm});
            skLineSegment(sketch, "E4.30.19.4", {"start": v(126, 46.48) * mm, "end": v(126, 43.59) * mm});
            skLineSegment(sketch, "E4.33.19.4", {"start": v(123.5, 47.92) * mm, "end": v(126, 46.48) * mm});
            skLineSegment(sketch, "E4.36.19.4", {"start": v(124.25, 40.85) * mm, "end": v(126.75, 42.3) * mm});
            skLineSegment(sketch, "E4.39.19.4", {"start": v(124.25, 37.96) * mm, "end": v(124.25, 40.85) * mm});
            skCircle(sketch, "E4.0.19.5", {"center": v(126.75, 50.66) * mm, "radius": 2.5 * mm, "construction": true});
            skCircle(sketch, "E4.2.19.5", {"center": v(123.5, 56.3) * mm, "radius": 2.5 * mm, "construction": true});
            skPoint(sketch, "E4.4.19.5", {"position": v(124.75, 58.46) * mm});
            skPoint(sketch, "E4.5.19.5", {"position": v(128, 52.83) * mm});
            skLineSegment(sketch, "E4.6.19.5", {"start": v(126.75, 47.78) * mm, "end": v(124.25, 49.22) * mm});
            skLineSegment(sketch, "E4.9.19.5", {"start": v(129.25, 49.22) * mm, "end": v(126.75, 47.78) * mm});
            skLineSegment(sketch, "E4.12.19.5", {"start": v(129.25, 52.1) * mm, "end": v(129.25, 49.22) * mm});
            skLineSegment(sketch, "E4.15.19.5", {"start": v(126.75, 53.55) * mm, "end": v(129.25, 52.1) * mm});
            skLineSegment(sketch, "E4.18.19.5", {"start": v(121, 57.74) * mm, "end": v(123.5, 59.18) * mm});
            skLineSegment(sketch, "E4.21.19.5", {"start": v(121, 54.85) * mm, "end": v(121, 57.74) * mm});
            skLineSegment(sketch, "E4.24.19.5", {"start": v(123.5, 53.4) * mm, "end": v(121, 54.85) * mm});
            skLineSegment(sketch, "E4.27.19.5", {"start": v(126, 54.85) * mm, "end": v(123.5, 53.4) * mm});
            skLineSegment(sketch, "E4.30.19.5", {"start": v(126, 57.74) * mm, "end": v(126, 54.85) * mm});
            skLineSegment(sketch, "E4.33.19.5", {"start": v(123.5, 59.18) * mm, "end": v(126, 57.74) * mm});
            skLineSegment(sketch, "E4.36.19.5", {"start": v(124.25, 52.1) * mm, "end": v(126.75, 53.55) * mm});
            skLineSegment(sketch, "E4.39.19.5", {"start": v(124.25, 49.22) * mm, "end": v(124.25, 52.1) * mm});
            skCircle(sketch, "E4.0.19.6", {"center": v(126.75, 61.92) * mm, "radius": 2.5 * mm, "construction": true});
            skCircle(sketch, "E4.2.19.6", {"center": v(123.5, 67.55) * mm, "radius": 2.5 * mm, "construction": true});
            skPoint(sketch, "E4.4.19.6", {"position": v(124.75, 69.72) * mm});
            skPoint(sketch, "E4.5.19.6", {"position": v(128, 64.09) * mm});
            skLineSegment(sketch, "E4.6.19.6", {"start": v(126.75, 59.03) * mm, "end": v(124.25, 60.48) * mm});
            skLineSegment(sketch, "E4.9.19.6", {"start": v(129.25, 60.48) * mm, "end": v(126.75, 59.03) * mm});
            skLineSegment(sketch, "E4.12.19.6", {"start": v(129.25, 63.36) * mm, "end": v(129.25, 60.48) * mm});
            skLineSegment(sketch, "E4.15.19.6", {"start": v(126.75, 64.8) * mm, "end": v(129.25, 63.36) * mm});
            skLineSegment(sketch, "E4.18.19.6", {"start": v(121, 69) * mm, "end": v(123.5, 70.44) * mm});
            skLineSegment(sketch, "E4.21.19.6", {"start": v(121, 66.1) * mm, "end": v(121, 69) * mm});
            skLineSegment(sketch, "E4.24.19.6", {"start": v(123.5, 64.66) * mm, "end": v(121, 66.1) * mm});
            skLineSegment(sketch, "E4.27.19.6", {"start": v(126, 66.1) * mm, "end": v(123.5, 64.66) * mm});
            skLineSegment(sketch, "E4.30.19.6", {"start": v(126, 69) * mm, "end": v(126, 66.1) * mm});
            skLineSegment(sketch, "E4.33.19.6", {"start": v(123.5, 70.44) * mm, "end": v(126, 69) * mm});
            skLineSegment(sketch, "E4.36.19.6", {"start": v(124.25, 63.36) * mm, "end": v(126.75, 64.8) * mm});
            skLineSegment(sketch, "E4.39.19.6", {"start": v(124.25, 60.48) * mm, "end": v(124.25, 63.36) * mm});
            skCircle(sketch, "E4.0.19.7", {"center": v(126.75, 73.18) * mm, "radius": 2.5 * mm, "construction": true});
            skCircle(sketch, "E4.2.19.7", {"center": v(123.5, 78.8) * mm, "radius": 2.5 * mm, "construction": true});
            skPoint(sketch, "E4.4.19.7", {"position": v(124.75, 80.97) * mm});
            skPoint(sketch, "E4.5.19.7", {"position": v(128, 75.34) * mm});
            skLineSegment(sketch, "E4.6.19.7", {"start": v(126.75, 70.3) * mm, "end": v(124.25, 71.74) * mm});
            skLineSegment(sketch, "E4.9.19.7", {"start": v(129.25, 71.74) * mm, "end": v(126.75, 70.3) * mm});
            skLineSegment(sketch, "E4.12.19.7", {"start": v(129.25, 74.62) * mm, "end": v(129.25, 71.74) * mm});
            skLineSegment(sketch, "E4.15.19.7", {"start": v(126.75, 76.07) * mm, "end": v(129.25, 74.62) * mm});
            skLineSegment(sketch, "E4.18.19.7", {"start": v(121, 80.25) * mm, "end": v(123.5, 81.7) * mm});
            skLineSegment(sketch, "E4.21.19.7", {"start": v(121, 77.36) * mm, "end": v(121, 80.25) * mm});
            skLineSegment(sketch, "E4.24.19.7", {"start": v(123.5, 75.92) * mm, "end": v(121, 77.36) * mm});
            skLineSegment(sketch, "E4.27.19.7", {"start": v(126, 77.36) * mm, "end": v(123.5, 75.92) * mm});
            skLineSegment(sketch, "E4.30.19.7", {"start": v(126, 80.25) * mm, "end": v(126, 77.36) * mm});
            skLineSegment(sketch, "E4.33.19.7", {"start": v(123.5, 81.7) * mm, "end": v(126, 80.25) * mm});
            skLineSegment(sketch, "E4.36.19.7", {"start": v(124.25, 74.62) * mm, "end": v(126.75, 76.07) * mm});
            skLineSegment(sketch, "E4.39.19.7", {"start": v(124.25, 71.74) * mm, "end": v(124.25, 74.62) * mm});
            skCircle(sketch, "E4.0.19.8", {"center": v(126.75, 84.44) * mm, "radius": 2.5 * mm, "construction": true});
            skCircle(sketch, "E4.2.19.8", {"center": v(123.5, 90.07) * mm, "radius": 2.5 * mm, "construction": true});
            skPoint(sketch, "E4.4.19.8", {"position": v(124.75, 92.23) * mm});
            skPoint(sketch, "E4.5.19.8", {"position": v(128, 86.6) * mm});
            skLineSegment(sketch, "E4.6.19.8", {"start": v(126.75, 81.55) * mm, "end": v(124.25, 83) * mm});
            skLineSegment(sketch, "E4.9.19.8", {"start": v(129.25, 83) * mm, "end": v(126.75, 81.55) * mm});
            skLineSegment(sketch, "E4.12.19.8", {"start": v(129.25, 85.88) * mm, "end": v(129.25, 83) * mm});
            skLineSegment(sketch, "E4.15.19.8", {"start": v(126.75, 87.32) * mm, "end": v(129.25, 85.88) * mm});
            skLineSegment(sketch, "E4.18.19.8", {"start": v(121, 91.51) * mm, "end": v(123.5, 92.95) * mm});
            skLineSegment(sketch, "E4.21.19.8", {"start": v(121, 88.62) * mm, "end": v(121, 91.51) * mm});
            skLineSegment(sketch, "E4.24.19.8", {"start": v(123.5, 87.18) * mm, "end": v(121, 88.62) * mm});
            skLineSegment(sketch, "E4.27.19.8", {"start": v(126, 88.62) * mm, "end": v(123.5, 87.18) * mm});
            skLineSegment(sketch, "E4.30.19.8", {"start": v(126, 91.51) * mm, "end": v(126, 88.62) * mm});
            skLineSegment(sketch, "E4.33.19.8", {"start": v(123.5, 92.95) * mm, "end": v(126, 91.51) * mm});
            skLineSegment(sketch, "E4.36.19.8", {"start": v(124.25, 85.88) * mm, "end": v(126.75, 87.32) * mm});
            skLineSegment(sketch, "E4.39.19.8", {"start": v(124.25, 83) * mm, "end": v(124.25, 85.88) * mm});
            skCircle(sketch, "E4.0.19.9", {"center": v(126.75, 95.7) * mm, "radius": 2.5 * mm, "construction": true});
            skCircle(sketch, "E4.2.19.9", {"center": v(123.5, 101.32) * mm, "radius": 2.5 * mm, "construction": true});
            skPoint(sketch, "E4.4.19.9", {"position": v(124.75, 103.5) * mm});
            skPoint(sketch, "E4.5.19.9", {"position": v(128, 97.86) * mm});
            skLineSegment(sketch, "E4.6.19.9", {"start": v(126.75, 92.8) * mm, "end": v(124.25, 94.25) * mm});
            skLineSegment(sketch, "E4.9.19.9", {"start": v(129.25, 94.25) * mm, "end": v(126.75, 92.8) * mm});
            skLineSegment(sketch, "E4.12.19.9", {"start": v(129.25, 97.14) * mm, "end": v(129.25, 94.25) * mm});
            skLineSegment(sketch, "E4.15.19.9", {"start": v(126.75, 98.58) * mm, "end": v(129.25, 97.14) * mm});
            skLineSegment(sketch, "E4.18.19.9", {"start": v(121, 102.77) * mm, "end": v(123.5, 104.21) * mm});
            skLineSegment(sketch, "E4.21.19.9", {"start": v(121, 99.88) * mm, "end": v(121, 102.77) * mm});
            skLineSegment(sketch, "E4.24.19.9", {"start": v(123.5, 98.44) * mm, "end": v(121, 99.88) * mm});
            skLineSegment(sketch, "E4.27.19.9", {"start": v(126, 99.88) * mm, "end": v(123.5, 98.44) * mm});
            skLineSegment(sketch, "E4.30.19.9", {"start": v(126, 102.77) * mm, "end": v(126, 99.88) * mm});
            skLineSegment(sketch, "E4.33.19.9", {"start": v(123.5, 104.21) * mm, "end": v(126, 102.77) * mm});
            skLineSegment(sketch, "E4.36.19.9", {"start": v(124.25, 97.14) * mm, "end": v(126.75, 98.58) * mm});
            skLineSegment(sketch, "E4.39.19.9", {"start": v(124.25, 94.25) * mm, "end": v(124.25, 97.14) * mm});
            skLineSegment(sketch, "E5.bottom", {"start": v(131.67, 107.67) * mm, "end": v(-9.45, 107.67) * mm});
            skLineSegment(sketch, "E5.top", {"start": v(131.67, -11.15) * mm, "end": v(-9.45, -11.15) * mm});
            skLineSegment(sketch, "E5.left", {"start": v(131.67, 107.67) * mm, "end": v(131.67, -11.15) * mm});
            skLineSegment(sketch, "E5.right", {"start": v(-9.45, 107.67) * mm, "end": v(-9.45, -11.15) * mm});
            skSolve(sketch);
        }
        {
            var Q0;
            {var subQ19=sQuery(id+"F0.wireOp",EDGE,"E2.0");Q0=makeQuery(id+"F0.imprint","IMPRINT",FACE,{"disambiguationData":[TD([[makeQuery(id+"F0.imprint","IMPRINT",EDGE,{"derivedFrom":subQ19}),1.0]])]});}
            extrude(context, id + "F1", {"entities" : qUnion([Q0]), "depth" : 5 * mm, "offsetDistance" : 25 * mm});
        }
        {
            var Q0;
            Q0=makeQuery(id+"F0.imprint","IMPRINT",FACE,{"disambiguationData":[TD([[makeQuery(id+"F0.imprint","IMPRINT",EDGE,{"derivedFrom":sQuery(id+"F0.wireOp",EDGE,"E0.0")}),1.0]])]});
            extrude(context, id + "F2", {"entities" : qUnion([Q0]), "operationType" : NewBodyOperationType.ADD, "depth" : 4 * mm, "offsetDistance" : 25 * mm});
        }
        {
            var Q0;
            Q0=qCreatedBy(makeId("Front.planeOp"),FACE);
            var Q1;
            Q1=qCreatedBy(makeId("Front.planeOp"),FACE);
            var sketch = newSketch(context, id + "F3", { "sketchPlane" : qUnion([Q0, Q1])});
            skLineSegment(sketch, "E6.bottom", {"start": v(0, 0) * mm, "end": v(56, 0) * mm, "construction": true});
            skLineSegment(sketch, "E6.left", {"start": v(0, 0) * mm, "end": v(0, 56) * mm, "construction": true});
            skCircle(sketch, "E7", {"center": v(64.81, 48.26) * mm, "radius": 56 * mm});
            skCircle(sketch, "E8", {"center": v(64.81, 48.26) * mm, "radius": 56.5 * mm});
            skSolve(sketch);
        }
        {
            var Q0;
            Q0=makeQuery(id+"F3.imprint","IMPRINT",FACE,{"disambiguationData":[TD([[makeQuery(id+"F3.imprint","IMPRINT",EDGE,{"derivedFrom":sQuery(id+"F3.wireOp",EDGE,"E7")}),1.0]])]});
            extrude(context, id + "F4", {"entities" : qUnion([Q0]), "depth" : 4 * mm, "offsetDistance" : 25 * mm});
        }
        {
            var Q0;
            Q0=makeQuery(id+"F1.opExtrude","SWEPT_BODY",BODY,{"disambiguationData":[OSD([sQuery(id+"F0.wireOp",EDGE,"E0.0"),sQuery(id+"F0.wireOp",EDGE,"E0.1"),sQuery(id+"F0.wireOp",EDGE,"E0.2"),sQuery(id+"F0.wireOp",EDGE,"E0.3"),sQuery(id+"F0.wireOp",EDGE,"E0.4"),sQuery(id+"F0.wireOp",EDGE,"E0.5"),sQuery(id+"F0.wireOp",EDGE,"E2.0"),sQuery(id+"F0.wireOp",EDGE,"E2.1"),sQuery(id+"F0.wireOp",EDGE,"E2.2"),sQuery(id+"F0.wireOp",EDGE,"E2.3"),sQuery(id+"F0.wireOp",EDGE,"E2.4"),sQuery(id+"F0.wireOp",EDGE,"E2.5"),sQuery(id+"F0.wireOp",EDGE,"E3.0.1.4"),sQuery(id+"F0.wireOp",EDGE,"E3.0.1.5"),sQuery(id+"F0.wireOp",EDGE,"E3.0.1.6"),sQuery(id+"F0.wireOp",EDGE,"E3.0.1.7"),sQuery(id+"F0.wireOp",EDGE,"E3.0.1.8"),sQuery(id+"F0.wireOp",EDGE,"E3.0.1.9"),sQuery(id+"F0.wireOp",EDGE,"E3.0.1.10"),sQuery(id+"F0.wireOp",EDGE,"E3.0.1.11"),sQuery(id+"F0.wireOp",EDGE,"E3.0.1.12"),sQuery(id+"F0.wireOp",EDGE,"E3.0.1.13"),sQuery(id+"F0.wireOp",EDGE,"E3.0.1.14"),sQuery(id+"F0.wireOp",EDGE,"E3.0.1.15"),sQuery(id+"F0.wireOp",EDGE,"E3.0.2.4"),sQuery(id+"F0.wireOp",EDGE,"E3.0.2.5"),sQuery(id+"F0.wireOp",EDGE,"E3.0.2.6"),sQuery(id+"F0.wireOp",EDGE,"E3.0.2.7"),sQuery(id+"F0.wireOp",EDGE,"E3.0.2.8"),sQuery(id+"F0.wireOp",EDGE,"E3.0.2.9"),sQuery(id+"F0.wireOp",EDGE,"E3.0.2.10"),sQuery(id+"F0.wireOp",EDGE,"E3.0.2.11"),sQuery(id+"F0.wireOp",EDGE,"E3.0.2.12"),sQuery(id+"F0.wireOp",EDGE,"E3.0.2.13"),sQuery(id+"F0.wireOp",EDGE,"E3.0.2.14"),sQuery(id+"F0.wireOp",EDGE,"E3.0.2.15"),sQuery(id+"F0.wireOp",EDGE,"E3.0.3.4"),sQuery(id+"F0.wireOp",EDGE,"E3.0.3.5"),sQuery(id+"F0.wireOp",EDGE,"E3.0.3.6"),sQuery(id+"F0.wireOp",EDGE,"E3.0.3.7"),sQuery(id+"F0.wireOp",EDGE,"E3.0.3.8"),sQuery(id+"F0.wireOp",EDGE,"E3.0.3.9"),sQuery(id+"F0.wireOp",EDGE,"E3.0.3.10"),sQuery(id+"F0.wireOp",EDGE,"E3.0.3.11"),sQuery(id+"F0.wireOp",EDGE,"E3.0.3.12"),sQuery(id+"F0.wireOp",EDGE,"E3.0.3.13"),sQuery(id+"F0.wireOp",EDGE,"E3.0.3.14"),sQuery(id+"F0.wireOp",EDGE,"E3.0.3.15"),sQuery(id+"F0.wireOp",EDGE,"E3.0.4.4"),sQuery(id+"F0.wireOp",EDGE,"E3.0.4.5"),sQuery(id+"F0.wireOp",EDGE,"E3.0.4.6"),sQuery(id+"F0.wireOp",EDGE,"E3.0.4.7"),sQuery(id+"F0.wireOp",EDGE,"E3.0.4.8"),sQuery(id+"F0.wireOp",EDGE,"E3.0.4.9"),sQuery(id+"F0.wireOp",EDGE,"E3.0.4.10"),sQuery(id+"F0.wireOp",EDGE,"E3.0.4.11"),sQuery(id+"F0.wireOp",EDGE,"E3.0.4.12"),sQuery(id+"F0.wireOp",EDGE,"E3.0.4.13"),sQuery(id+"F0.wireOp",EDGE,"E3.0.4.14"),sQuery(id+"F0.wireOp",EDGE,"E3.0.4.15"),sQuery(id+"F0.wireOp",EDGE,"E3.0.5.4"),sQuery(id+"F0.wireOp",EDGE,"E3.0.5.5"),sQuery(id+"F0.wireOp",EDGE,"E3.0.5.6"),sQuery(id+"F0.wireOp",EDGE,"E3.0.5.7"),sQuery(id+"F0.wireOp",EDGE,"E3.0.5.8"),sQuery(id+"F0.wireOp",EDGE,"E3.0.5.9"),sQuery(id+"F0.wireOp",EDGE,"E3.0.5.10"),sQuery(id+"F0.wireOp",EDGE,"E3.0.5.11"),sQuery(id+"F0.wireOp",EDGE,"E3.0.5.12"),sQuery(id+"F0.wireOp",EDGE,"E3.0.5.13"),sQuery(id+"F0.wireOp",EDGE,"E3.0.5.14"),sQuery(id+"F0.wireOp",EDGE,"E3.0.5.15"),sQuery(id+"F0.wireOp",EDGE,"E3.0.6.4"),sQuery(id+"F0.wireOp",EDGE,"E3.0.6.5"),sQuery(id+"F0.wireOp",EDGE,"E3.0.6.6"),sQuery(id+"F0.wireOp",EDGE,"E3.0.6.7"),sQuery(id+"F0.wireOp",EDGE,"E3.0.6.8"),sQuery(id+"F0.wireOp",EDGE,"E3.0.6.9"),sQuery(id+"F0.wireOp",EDGE,"E3.0.6.10"),sQuery(id+"F0.wireOp",EDGE,"E3.0.6.11"),sQuery(id+"F0.wireOp",EDGE,"E3.0.6.12"),sQuery(id+"F0.wireOp",EDGE,"E3.0.6.13"),sQuery(id+"F0.wireOp",EDGE,"E3.0.6.14"),sQuery(id+"F0.wireOp",EDGE,"E3.0.6.15"),sQuery(id+"F0.wireOp",EDGE,"E3.0.7.4"),sQuery(id+"F0.wireOp",EDGE,"E3.0.7.5"),sQuery(id+"F0.wireOp",EDGE,"E3.0.7.6"),sQuery(id+"F0.wireOp",EDGE,"E3.0.7.7"),sQuery(id+"F0.wireOp",EDGE,"E3.0.7.8"),sQuery(id+"F0.wireOp",EDGE,"E3.0.7.9"),sQuery(id+"F0.wireOp",EDGE,"E3.0.7.10"),sQuery(id+"F0.wireOp",EDGE,"E3.0.7.11"),sQuery(id+"F0.wireOp",EDGE,"E3.0.7.12"),sQuery(id+"F0.wireOp",EDGE,"E3.0.7.13"),sQuery(id+"F0.wireOp",EDGE,"E3.0.7.14"),sQuery(id+"F0.wireOp",EDGE,"E3.0.7.15"),sQuery(id+"F0.wireOp",EDGE,"E3.0.8.4"),sQuery(id+"F0.wireOp",EDGE,"E3.0.8.5"),sQuery(id+"F0.wireOp",EDGE,"E3.0.8.6"),sQuery(id+"F0.wireOp",EDGE,"E3.0.8.7"),sQuery(id+"F0.wireOp",EDGE,"E3.0.8.8"),sQuery(id+"F0.wireOp",EDGE,"E3.0.8.9"),sQuery(id+"F0.wireOp",EDGE,"E3.0.8.10"),sQuery(id+"F0.wireOp",EDGE,"E3.0.8.11"),sQuery(id+"F0.wireOp",EDGE,"E3.0.8.12"),sQuery(id+"F0.wireOp",EDGE,"E3.0.8.13"),sQuery(id+"F0.wireOp",EDGE,"E3.0.8.14"),sQuery(id+"F0.wireOp",EDGE,"E3.0.8.15"),sQuery(id+"F0.wireOp",EDGE,"E3.0.9.4"),sQuery(id+"F0.wireOp",EDGE,"E3.0.9.5"),sQuery(id+"F0.wireOp",EDGE,"E3.0.9.6"),sQuery(id+"F0.wireOp",EDGE,"E3.0.9.7"),sQuery(id+"F0.wireOp",EDGE,"E3.0.9.8"),sQuery(id+"F0.wireOp",EDGE,"E3.0.9.9"),sQuery(id+"F0.wireOp",EDGE,"E3.0.9.10"),sQuery(id+"F0.wireOp",EDGE,"E3.0.9.11"),sQuery(id+"F0.wireOp",EDGE,"E3.0.9.12"),sQuery(id+"F0.wireOp",EDGE,"E3.0.9.13"),sQuery(id+"F0.wireOp",EDGE,"E3.0.9.14"),sQuery(id+"F0.wireOp",EDGE,"E3.0.9.15"),sQuery(id+"F0.wireOp",EDGE,"E3.1.0.4"),sQuery(id+"F0.wireOp",EDGE,"E3.1.0.5"),sQuery(id+"F0.wireOp",EDGE,"E3.1.0.6"),sQuery(id+"F0.wireOp",EDGE,"E3.1.0.7"),sQuery(id+"F0.wireOp",EDGE,"E3.1.0.8"),sQuery(id+"F0.wireOp",EDGE,"E3.1.0.9"),sQuery(id+"F0.wireOp",EDGE,"E3.1.0.10"),sQuery(id+"F0.wireOp",EDGE,"E3.1.0.11"),sQuery(id+"F0.wireOp",EDGE,"E3.1.0.12"),sQuery(id+"F0.wireOp",EDGE,"E3.1.0.13"),sQuery(id+"F0.wireOp",EDGE,"E3.1.0.14"),sQuery(id+"F0.wireOp",EDGE,"E3.1.0.15"),sQuery(id+"F0.wireOp",EDGE,"E3.1.1.4"),sQuery(id+"F0.wireOp",EDGE,"E3.1.1.5"),sQuery(id+"F0.wireOp",EDGE,"E3.1.1.6"),sQuery(id+"F0.wireOp",EDGE,"E3.1.1.7"),sQuery(id+"F0.wireOp",EDGE,"E3.1.1.8"),sQuery(id+"F0.wireOp",EDGE,"E3.1.1.9"),sQuery(id+"F0.wireOp",EDGE,"E3.1.1.10"),sQuery(id+"F0.wireOp",EDGE,"E3.1.1.11"),sQuery(id+"F0.wireOp",EDGE,"E3.1.1.12"),sQuery(id+"F0.wireOp",EDGE,"E3.1.1.13"),sQuery(id+"F0.wireOp",EDGE,"E3.1.1.14"),sQuery(id+"F0.wireOp",EDGE,"E3.1.1.15"),sQuery(id+"F0.wireOp",EDGE,"E3.1.2.4"),sQuery(id+"F0.wireOp",EDGE,"E3.1.2.5"),sQuery(id+"F0.wireOp",EDGE,"E3.1.2.6"),sQuery(id+"F0.wireOp",EDGE,"E3.1.2.7"),sQuery(id+"F0.wireOp",EDGE,"E3.1.2.8"),sQuery(id+"F0.wireOp",EDGE,"E3.1.2.9"),sQuery(id+"F0.wireOp",EDGE,"E3.1.2.10"),sQuery(id+"F0.wireOp",EDGE,"E3.1.2.11"),sQuery(id+"F0.wireOp",EDGE,"E3.1.2.12"),sQuery(id+"F0.wireOp",EDGE,"E3.1.2.13"),sQuery(id+"F0.wireOp",EDGE,"E3.1.2.14"),sQuery(id+"F0.wireOp",EDGE,"E3.1.2.15"),sQuery(id+"F0.wireOp",EDGE,"E3.1.3.4"),sQuery(id+"F0.wireOp",EDGE,"E3.1.3.5"),sQuery(id+"F0.wireOp",EDGE,"E3.1.3.6"),sQuery(id+"F0.wireOp",EDGE,"E3.1.3.7"),sQuery(id+"F0.wireOp",EDGE,"E3.1.3.8"),sQuery(id+"F0.wireOp",EDGE,"E3.1.3.9"),sQuery(id+"F0.wireOp",EDGE,"E3.1.3.10"),sQuery(id+"F0.wireOp",EDGE,"E3.1.3.11"),sQuery(id+"F0.wireOp",EDGE,"E3.1.3.12"),sQuery(id+"F0.wireOp",EDGE,"E3.1.3.13"),sQuery(id+"F0.wireOp",EDGE,"E3.1.3.14"),sQuery(id+"F0.wireOp",EDGE,"E3.1.3.15"),sQuery(id+"F0.wireOp",EDGE,"E3.1.4.4"),sQuery(id+"F0.wireOp",EDGE,"E3.1.4.5"),sQuery(id+"F0.wireOp",EDGE,"E3.1.4.6"),sQuery(id+"F0.wireOp",EDGE,"E3.1.4.7"),sQuery(id+"F0.wireOp",EDGE,"E3.1.4.8"),sQuery(id+"F0.wireOp",EDGE,"E3.1.4.9"),sQuery(id+"F0.wireOp",EDGE,"E3.1.4.10"),sQuery(id+"F0.wireOp",EDGE,"E3.1.4.11"),sQuery(id+"F0.wireOp",EDGE,"E3.1.4.12"),sQuery(id+"F0.wireOp",EDGE,"E3.1.4.13"),sQuery(id+"F0.wireOp",EDGE,"E3.1.4.14"),sQuery(id+"F0.wireOp",EDGE,"E3.1.4.15"),sQuery(id+"F0.wireOp",EDGE,"E3.1.5.4"),sQuery(id+"F0.wireOp",EDGE,"E3.1.5.5"),sQuery(id+"F0.wireOp",EDGE,"E3.1.5.6"),sQuery(id+"F0.wireOp",EDGE,"E3.1.5.7"),sQuery(id+"F0.wireOp",EDGE,"E3.1.5.8"),sQuery(id+"F0.wireOp",EDGE,"E3.1.5.9"),sQuery(id+"F0.wireOp",EDGE,"E3.1.5.10"),sQuery(id+"F0.wireOp",EDGE,"E3.1.5.11"),sQuery(id+"F0.wireOp",EDGE,"E3.1.5.12"),sQuery(id+"F0.wireOp",EDGE,"E3.1.5.13"),sQuery(id+"F0.wireOp",EDGE,"E3.1.5.14"),sQuery(id+"F0.wireOp",EDGE,"E3.1.5.15"),sQuery(id+"F0.wireOp",EDGE,"E3.1.6.4"),sQuery(id+"F0.wireOp",EDGE,"E3.1.6.5"),sQuery(id+"F0.wireOp",EDGE,"E3.1.6.6"),sQuery(id+"F0.wireOp",EDGE,"E3.1.6.7"),sQuery(id+"F0.wireOp",EDGE,"E3.1.6.8"),sQuery(id+"F0.wireOp",EDGE,"E3.1.6.9"),sQuery(id+"F0.wireOp",EDGE,"E3.1.6.10"),sQuery(id+"F0.wireOp",EDGE,"E3.1.6.11"),sQuery(id+"F0.wireOp",EDGE,"E3.1.6.12"),sQuery(id+"F0.wireOp",EDGE,"E3.1.6.13"),sQuery(id+"F0.wireOp",EDGE,"E3.1.6.14"),sQuery(id+"F0.wireOp",EDGE,"E3.1.6.15"),sQuery(id+"F0.wireOp",EDGE,"E3.1.7.4"),sQuery(id+"F0.wireOp",EDGE,"E3.1.7.5"),sQuery(id+"F0.wireOp",EDGE,"E3.1.7.6"),sQuery(id+"F0.wireOp",EDGE,"E3.1.7.7"),sQuery(id+"F0.wireOp",EDGE,"E3.1.7.8"),sQuery(id+"F0.wireOp",EDGE,"E3.1.7.9"),sQuery(id+"F0.wireOp",EDGE,"E3.1.7.10"),sQuery(id+"F0.wireOp",EDGE,"E3.1.7.11"),sQuery(id+"F0.wireOp",EDGE,"E3.1.7.12"),sQuery(id+"F0.wireOp",EDGE,"E3.1.7.13"),sQuery(id+"F0.wireOp",EDGE,"E3.1.7.14"),sQuery(id+"F0.wireOp",EDGE,"E3.1.7.15"),sQuery(id+"F0.wireOp",EDGE,"E3.1.8.4"),sQuery(id+"F0.wireOp",EDGE,"E3.1.8.5"),sQuery(id+"F0.wireOp",EDGE,"E3.1.8.6"),sQuery(id+"F0.wireOp",EDGE,"E3.1.8.7"),sQuery(id+"F0.wireOp",EDGE,"E3.1.8.8"),sQuery(id+"F0.wireOp",EDGE,"E3.1.8.9"),sQuery(id+"F0.wireOp",EDGE,"E3.1.8.10"),sQuery(id+"F0.wireOp",EDGE,"E3.1.8.11"),sQuery(id+"F0.wireOp",EDGE,"E3.1.8.12"),sQuery(id+"F0.wireOp",EDGE,"E3.1.8.13"),sQuery(id+"F0.wireOp",EDGE,"E3.1.8.14"),sQuery(id+"F0.wireOp",EDGE,"E3.1.8.15"),sQuery(id+"F0.wireOp",EDGE,"E3.1.9.4"),sQuery(id+"F0.wireOp",EDGE,"E3.1.9.5"),sQuery(id+"F0.wireOp",EDGE,"E3.1.9.6"),sQuery(id+"F0.wireOp",EDGE,"E3.1.9.7"),sQuery(id+"F0.wireOp",EDGE,"E3.1.9.8"),sQuery(id+"F0.wireOp",EDGE,"E3.1.9.9"),sQuery(id+"F0.wireOp",EDGE,"E3.1.9.10"),sQuery(id+"F0.wireOp",EDGE,"E3.1.9.11"),sQuery(id+"F0.wireOp",EDGE,"E3.1.9.12"),sQuery(id+"F0.wireOp",EDGE,"E3.1.9.13"),sQuery(id+"F0.wireOp",EDGE,"E3.1.9.14"),sQuery(id+"F0.wireOp",EDGE,"E3.1.9.15"),sQuery(id+"F0.wireOp",EDGE,"E3.2.0.4"),sQuery(id+"F0.wireOp",EDGE,"E3.2.0.5"),sQuery(id+"F0.wireOp",EDGE,"E3.2.0.6"),sQuery(id+"F0.wireOp",EDGE,"E3.2.0.7"),sQuery(id+"F0.wireOp",EDGE,"E3.2.0.8"),sQuery(id+"F0.wireOp",EDGE,"E3.2.0.9"),sQuery(id+"F0.wireOp",EDGE,"E3.2.0.10"),sQuery(id+"F0.wireOp",EDGE,"E3.2.0.11"),sQuery(id+"F0.wireOp",EDGE,"E3.2.0.12"),sQuery(id+"F0.wireOp",EDGE,"E3.2.0.13"),sQuery(id+"F0.wireOp",EDGE,"E3.2.0.14"),sQuery(id+"F0.wireOp",EDGE,"E3.2.0.15"),sQuery(id+"F0.wireOp",EDGE,"E3.2.1.4"),sQuery(id+"F0.wireOp",EDGE,"E3.2.1.5"),sQuery(id+"F0.wireOp",EDGE,"E3.2.1.6"),sQuery(id+"F0.wireOp",EDGE,"E3.2.1.7"),sQuery(id+"F0.wireOp",EDGE,"E3.2.1.8"),sQuery(id+"F0.wireOp",EDGE,"E3.2.1.9"),sQuery(id+"F0.wireOp",EDGE,"E3.2.1.10"),sQuery(id+"F0.wireOp",EDGE,"E3.2.1.11"),sQuery(id+"F0.wireOp",EDGE,"E3.2.1.12"),sQuery(id+"F0.wireOp",EDGE,"E3.2.1.13"),sQuery(id+"F0.wireOp",EDGE,"E3.2.1.14"),sQuery(id+"F0.wireOp",EDGE,"E3.2.1.15"),sQuery(id+"F0.wireOp",EDGE,"E3.2.2.4"),sQuery(id+"F0.wireOp",EDGE,"E3.2.2.5"),sQuery(id+"F0.wireOp",EDGE,"E3.2.2.6"),sQuery(id+"F0.wireOp",EDGE,"E3.2.2.7"),sQuery(id+"F0.wireOp",EDGE,"E3.2.2.8"),sQuery(id+"F0.wireOp",EDGE,"E3.2.2.9"),sQuery(id+"F0.wireOp",EDGE,"E3.2.2.10"),sQuery(id+"F0.wireOp",EDGE,"E3.2.2.11"),sQuery(id+"F0.wireOp",EDGE,"E3.2.2.12"),sQuery(id+"F0.wireOp",EDGE,"E3.2.2.13"),sQuery(id+"F0.wireOp",EDGE,"E3.2.2.14"),sQuery(id+"F0.wireOp",EDGE,"E3.2.2.15"),sQuery(id+"F0.wireOp",EDGE,"E3.2.3.4"),sQuery(id+"F0.wireOp",EDGE,"E3.2.3.5"),sQuery(id+"F0.wireOp",EDGE,"E3.2.3.6"),sQuery(id+"F0.wireOp",EDGE,"E3.2.3.7"),sQuery(id+"F0.wireOp",EDGE,"E3.2.3.8"),sQuery(id+"F0.wireOp",EDGE,"E3.2.3.9"),sQuery(id+"F0.wireOp",EDGE,"E3.2.3.10"),sQuery(id+"F0.wireOp",EDGE,"E3.2.3.11"),sQuery(id+"F0.wireOp",EDGE,"E3.2.3.12"),sQuery(id+"F0.wireOp",EDGE,"E3.2.3.13"),sQuery(id+"F0.wireOp",EDGE,"E3.2.3.14"),sQuery(id+"F0.wireOp",EDGE,"E3.2.3.15"),sQuery(id+"F0.wireOp",EDGE,"E3.2.4.4"),sQuery(id+"F0.wireOp",EDGE,"E3.2.4.5"),sQuery(id+"F0.wireOp",EDGE,"E3.2.4.6"),sQuery(id+"F0.wireOp",EDGE,"E3.2.4.7"),sQuery(id+"F0.wireOp",EDGE,"E3.2.4.8"),sQuery(id+"F0.wireOp",EDGE,"E3.2.4.9"),sQuery(id+"F0.wireOp",EDGE,"E3.2.4.10"),sQuery(id+"F0.wireOp",EDGE,"E3.2.4.11"),sQuery(id+"F0.wireOp",EDGE,"E3.2.4.12"),sQuery(id+"F0.wireOp",EDGE,"E3.2.4.13"),sQuery(id+"F0.wireOp",EDGE,"E3.2.4.14"),sQuery(id+"F0.wireOp",EDGE,"E3.2.4.15"),sQuery(id+"F0.wireOp",EDGE,"E3.2.5.4"),sQuery(id+"F0.wireOp",EDGE,"E3.2.5.5"),sQuery(id+"F0.wireOp",EDGE,"E3.2.5.6"),sQuery(id+"F0.wireOp",EDGE,"E3.2.5.7"),sQuery(id+"F0.wireOp",EDGE,"E3.2.5.8"),sQuery(id+"F0.wireOp",EDGE,"E3.2.5.9"),sQuery(id+"F0.wireOp",EDGE,"E3.2.5.10"),sQuery(id+"F0.wireOp",EDGE,"E3.2.5.11"),sQuery(id+"F0.wireOp",EDGE,"E3.2.5.12"),sQuery(id+"F0.wireOp",EDGE,"E3.2.5.13"),sQuery(id+"F0.wireOp",EDGE,"E3.2.5.14"),sQuery(id+"F0.wireOp",EDGE,"E3.2.5.15"),sQuery(id+"F0.wireOp",EDGE,"E3.2.6.4"),sQuery(id+"F0.wireOp",EDGE,"E3.2.6.5"),sQuery(id+"F0.wireOp",EDGE,"E3.2.6.6"),sQuery(id+"F0.wireOp",EDGE,"E3.2.6.7"),sQuery(id+"F0.wireOp",EDGE,"E3.2.6.8"),sQuery(id+"F0.wireOp",EDGE,"E3.2.6.9"),sQuery(id+"F0.wireOp",EDGE,"E3.2.6.10"),sQuery(id+"F0.wireOp",EDGE,"E3.2.6.11"),sQuery(id+"F0.wireOp",EDGE,"E3.2.6.12"),sQuery(id+"F0.wireOp",EDGE,"E3.2.6.13"),sQuery(id+"F0.wireOp",EDGE,"E3.2.6.14"),sQuery(id+"F0.wireOp",EDGE,"E3.2.6.15"),sQuery(id+"F0.wireOp",EDGE,"E3.2.7.4"),sQuery(id+"F0.wireOp",EDGE,"E3.2.7.5"),sQuery(id+"F0.wireOp",EDGE,"E3.2.7.6"),sQuery(id+"F0.wireOp",EDGE,"E3.2.7.7"),sQuery(id+"F0.wireOp",EDGE,"E3.2.7.8"),sQuery(id+"F0.wireOp",EDGE,"E3.2.7.9"),sQuery(id+"F0.wireOp",EDGE,"E3.2.7.10"),sQuery(id+"F0.wireOp",EDGE,"E3.2.7.11"),sQuery(id+"F0.wireOp",EDGE,"E3.2.7.12"),sQuery(id+"F0.wireOp",EDGE,"E3.2.7.13"),sQuery(id+"F0.wireOp",EDGE,"E3.2.7.14"),sQuery(id+"F0.wireOp",EDGE,"E3.2.7.15"),sQuery(id+"F0.wireOp",EDGE,"E3.2.8.4"),sQuery(id+"F0.wireOp",EDGE,"E3.2.8.5"),sQuery(id+"F0.wireOp",EDGE,"E3.2.8.6"),sQuery(id+"F0.wireOp",EDGE,"E3.2.8.7"),sQuery(id+"F0.wireOp",EDGE,"E3.2.8.8"),sQuery(id+"F0.wireOp",EDGE,"E3.2.8.9"),sQuery(id+"F0.wireOp",EDGE,"E3.2.8.10"),sQuery(id+"F0.wireOp",EDGE,"E3.2.8.11"),sQuery(id+"F0.wireOp",EDGE,"E3.2.8.12"),sQuery(id+"F0.wireOp",EDGE,"E3.2.8.13"),sQuery(id+"F0.wireOp",EDGE,"E3.2.8.14"),sQuery(id+"F0.wireOp",EDGE,"E3.2.8.15"),sQuery(id+"F0.wireOp",EDGE,"E3.2.9.4"),sQuery(id+"F0.wireOp",EDGE,"E3.2.9.5"),sQuery(id+"F0.wireOp",EDGE,"E3.2.9.6"),sQuery(id+"F0.wireOp",EDGE,"E3.2.9.7"),sQuery(id+"F0.wireOp",EDGE,"E3.2.9.8"),sQuery(id+"F0.wireOp",EDGE,"E3.2.9.9"),sQuery(id+"F0.wireOp",EDGE,"E3.2.9.10"),sQuery(id+"F0.wireOp",EDGE,"E3.2.9.11"),sQuery(id+"F0.wireOp",EDGE,"E3.2.9.12"),sQuery(id+"F0.wireOp",EDGE,"E3.2.9.13"),sQuery(id+"F0.wireOp",EDGE,"E3.2.9.14"),sQuery(id+"F0.wireOp",EDGE,"E3.2.9.15"),sQuery(id+"F0.wireOp",EDGE,"E3.3.0.4"),sQuery(id+"F0.wireOp",EDGE,"E3.3.0.5"),sQuery(id+"F0.wireOp",EDGE,"E3.3.0.6"),sQuery(id+"F0.wireOp",EDGE,"E3.3.0.7"),sQuery(id+"F0.wireOp",EDGE,"E3.3.0.8"),sQuery(id+"F0.wireOp",EDGE,"E3.3.0.9"),sQuery(id+"F0.wireOp",EDGE,"E3.3.0.10"),sQuery(id+"F0.wireOp",EDGE,"E3.3.0.11"),sQuery(id+"F0.wireOp",EDGE,"E3.3.0.12"),sQuery(id+"F0.wireOp",EDGE,"E3.3.0.13"),sQuery(id+"F0.wireOp",EDGE,"E3.3.0.14"),sQuery(id+"F0.wireOp",EDGE,"E3.3.0.15"),sQuery(id+"F0.wireOp",EDGE,"E3.3.1.4"),sQuery(id+"F0.wireOp",EDGE,"E3.3.1.5"),sQuery(id+"F0.wireOp",EDGE,"E3.3.1.6"),sQuery(id+"F0.wireOp",EDGE,"E3.3.1.7"),sQuery(id+"F0.wireOp",EDGE,"E3.3.1.8"),sQuery(id+"F0.wireOp",EDGE,"E3.3.1.9"),sQuery(id+"F0.wireOp",EDGE,"E3.3.1.10"),sQuery(id+"F0.wireOp",EDGE,"E3.3.1.11"),sQuery(id+"F0.wireOp",EDGE,"E3.3.1.12"),sQuery(id+"F0.wireOp",EDGE,"E3.3.1.13"),sQuery(id+"F0.wireOp",EDGE,"E3.3.1.14"),sQuery(id+"F0.wireOp",EDGE,"E3.3.1.15"),sQuery(id+"F0.wireOp",EDGE,"E3.3.2.4"),sQuery(id+"F0.wireOp",EDGE,"E3.3.2.5"),sQuery(id+"F0.wireOp",EDGE,"E3.3.2.6"),sQuery(id+"F0.wireOp",EDGE,"E3.3.2.7"),sQuery(id+"F0.wireOp",EDGE,"E3.3.2.8"),sQuery(id+"F0.wireOp",EDGE,"E3.3.2.9"),sQuery(id+"F0.wireOp",EDGE,"E3.3.2.10"),sQuery(id+"F0.wireOp",EDGE,"E3.3.2.11"),sQuery(id+"F0.wireOp",EDGE,"E3.3.2.12"),sQuery(id+"F0.wireOp",EDGE,"E3.3.2.13"),sQuery(id+"F0.wireOp",EDGE,"E3.3.2.14"),sQuery(id+"F0.wireOp",EDGE,"E3.3.2.15"),sQuery(id+"F0.wireOp",EDGE,"E3.3.3.4"),sQuery(id+"F0.wireOp",EDGE,"E3.3.3.5"),sQuery(id+"F0.wireOp",EDGE,"E3.3.3.6"),sQuery(id+"F0.wireOp",EDGE,"E3.3.3.7"),sQuery(id+"F0.wireOp",EDGE,"E3.3.3.8"),sQuery(id+"F0.wireOp",EDGE,"E3.3.3.9"),sQuery(id+"F0.wireOp",EDGE,"E3.3.3.10"),sQuery(id+"F0.wireOp",EDGE,"E3.3.3.11"),sQuery(id+"F0.wireOp",EDGE,"E3.3.3.12"),sQuery(id+"F0.wireOp",EDGE,"E3.3.3.13"),sQuery(id+"F0.wireOp",EDGE,"E3.3.3.14"),sQuery(id+"F0.wireOp",EDGE,"E3.3.3.15"),sQuery(id+"F0.wireOp",EDGE,"E3.3.4.4"),sQuery(id+"F0.wireOp",EDGE,"E3.3.4.5"),sQuery(id+"F0.wireOp",EDGE,"E3.3.4.6"),sQuery(id+"F0.wireOp",EDGE,"E3.3.4.7"),sQuery(id+"F0.wireOp",EDGE,"E3.3.4.8"),sQuery(id+"F0.wireOp",EDGE,"E3.3.4.9"),sQuery(id+"F0.wireOp",EDGE,"E3.3.4.10"),sQuery(id+"F0.wireOp",EDGE,"E3.3.4.11"),sQuery(id+"F0.wireOp",EDGE,"E3.3.4.12"),sQuery(id+"F0.wireOp",EDGE,"E3.3.4.13"),sQuery(id+"F0.wireOp",EDGE,"E3.3.4.14"),sQuery(id+"F0.wireOp",EDGE,"E3.3.4.15"),sQuery(id+"F0.wireOp",EDGE,"E3.3.5.4"),sQuery(id+"F0.wireOp",EDGE,"E3.3.5.5"),sQuery(id+"F0.wireOp",EDGE,"E3.3.5.6"),sQuery(id+"F0.wireOp",EDGE,"E3.3.5.7"),sQuery(id+"F0.wireOp",EDGE,"E3.3.5.8"),sQuery(id+"F0.wireOp",EDGE,"E3.3.5.9"),sQuery(id+"F0.wireOp",EDGE,"E3.3.5.10"),sQuery(id+"F0.wireOp",EDGE,"E3.3.5.11"),sQuery(id+"F0.wireOp",EDGE,"E3.3.5.12"),sQuery(id+"F0.wireOp",EDGE,"E3.3.5.13"),sQuery(id+"F0.wireOp",EDGE,"E3.3.5.14"),sQuery(id+"F0.wireOp",EDGE,"E3.3.5.15"),sQuery(id+"F0.wireOp",EDGE,"E3.3.6.4"),sQuery(id+"F0.wireOp",EDGE,"E3.3.6.5"),sQuery(id+"F0.wireOp",EDGE,"E3.3.6.6"),sQuery(id+"F0.wireOp",EDGE,"E3.3.6.7"),sQuery(id+"F0.wireOp",EDGE,"E3.3.6.8"),sQuery(id+"F0.wireOp",EDGE,"E3.3.6.9"),sQuery(id+"F0.wireOp",EDGE,"E3.3.6.10"),sQuery(id+"F0.wireOp",EDGE,"E3.3.6.11"),sQuery(id+"F0.wireOp",EDGE,"E3.3.6.12"),sQuery(id+"F0.wireOp",EDGE,"E3.3.6.13"),sQuery(id+"F0.wireOp",EDGE,"E3.3.6.14"),sQuery(id+"F0.wireOp",EDGE,"E3.3.6.15"),sQuery(id+"F0.wireOp",EDGE,"E3.3.7.4"),sQuery(id+"F0.wireOp",EDGE,"E3.3.7.5"),sQuery(id+"F0.wireOp",EDGE,"E3.3.7.6"),sQuery(id+"F0.wireOp",EDGE,"E3.3.7.7"),sQuery(id+"F0.wireOp",EDGE,"E3.3.7.8"),sQuery(id+"F0.wireOp",EDGE,"E3.3.7.9"),sQuery(id+"F0.wireOp",EDGE,"E3.3.7.10"),sQuery(id+"F0.wireOp",EDGE,"E3.3.7.11"),sQuery(id+"F0.wireOp",EDGE,"E3.3.7.12"),sQuery(id+"F0.wireOp",EDGE,"E3.3.7.13"),sQuery(id+"F0.wireOp",EDGE,"E3.3.7.14"),sQuery(id+"F0.wireOp",EDGE,"E3.3.7.15"),sQuery(id+"F0.wireOp",EDGE,"E3.3.8.4"),sQuery(id+"F0.wireOp",EDGE,"E3.3.8.5"),sQuery(id+"F0.wireOp",EDGE,"E3.3.8.6"),sQuery(id+"F0.wireOp",EDGE,"E3.3.8.7"),sQuery(id+"F0.wireOp",EDGE,"E3.3.8.8"),sQuery(id+"F0.wireOp",EDGE,"E3.3.8.9"),sQuery(id+"F0.wireOp",EDGE,"E3.3.8.10"),sQuery(id+"F0.wireOp",EDGE,"E3.3.8.11"),sQuery(id+"F0.wireOp",EDGE,"E3.3.8.12"),sQuery(id+"F0.wireOp",EDGE,"E3.3.8.13"),sQuery(id+"F0.wireOp",EDGE,"E3.3.8.14"),sQuery(id+"F0.wireOp",EDGE,"E3.3.8.15"),sQuery(id+"F0.wireOp",EDGE,"E3.3.9.4"),sQuery(id+"F0.wireOp",EDGE,"E3.3.9.5"),sQuery(id+"F0.wireOp",EDGE,"E3.3.9.6"),sQuery(id+"F0.wireOp",EDGE,"E3.3.9.7"),sQuery(id+"F0.wireOp",EDGE,"E3.3.9.8"),sQuery(id+"F0.wireOp",EDGE,"E3.3.9.9"),sQuery(id+"F0.wireOp",EDGE,"E3.3.9.10"),sQuery(id+"F0.wireOp",EDGE,"E3.3.9.11"),sQuery(id+"F0.wireOp",EDGE,"E3.3.9.12"),sQuery(id+"F0.wireOp",EDGE,"E3.3.9.13"),sQuery(id+"F0.wireOp",EDGE,"E3.3.9.14"),sQuery(id+"F0.wireOp",EDGE,"E3.3.9.15"),sQuery(id+"F0.wireOp",EDGE,"E3.4.0.4"),sQuery(id+"F0.wireOp",EDGE,"E3.4.0.5"),sQuery(id+"F0.wireOp",EDGE,"E3.4.0.6"),sQuery(id+"F0.wireOp",EDGE,"E3.4.0.7"),sQuery(id+"F0.wireOp",EDGE,"E3.4.0.8"),sQuery(id+"F0.wireOp",EDGE,"E3.4.0.9"),sQuery(id+"F0.wireOp",EDGE,"E3.4.0.10"),sQuery(id+"F0.wireOp",EDGE,"E3.4.0.11"),sQuery(id+"F0.wireOp",EDGE,"E3.4.0.12"),sQuery(id+"F0.wireOp",EDGE,"E3.4.0.13"),sQuery(id+"F0.wireOp",EDGE,"E3.4.0.14"),sQuery(id+"F0.wireOp",EDGE,"E3.4.0.15"),sQuery(id+"F0.wireOp",EDGE,"E3.4.1.4"),sQuery(id+"F0.wireOp",EDGE,"E3.4.1.5"),sQuery(id+"F0.wireOp",EDGE,"E3.4.1.6"),sQuery(id+"F0.wireOp",EDGE,"E3.4.1.7"),sQuery(id+"F0.wireOp",EDGE,"E3.4.1.8"),sQuery(id+"F0.wireOp",EDGE,"E3.4.1.9"),sQuery(id+"F0.wireOp",EDGE,"E3.4.1.10"),sQuery(id+"F0.wireOp",EDGE,"E3.4.1.11"),sQuery(id+"F0.wireOp",EDGE,"E3.4.1.12"),sQuery(id+"F0.wireOp",EDGE,"E3.4.1.13"),sQuery(id+"F0.wireOp",EDGE,"E3.4.1.14"),sQuery(id+"F0.wireOp",EDGE,"E3.4.1.15"),sQuery(id+"F0.wireOp",EDGE,"E3.4.2.4"),sQuery(id+"F0.wireOp",EDGE,"E3.4.2.5"),sQuery(id+"F0.wireOp",EDGE,"E3.4.2.6"),sQuery(id+"F0.wireOp",EDGE,"E3.4.2.7"),sQuery(id+"F0.wireOp",EDGE,"E3.4.2.8"),sQuery(id+"F0.wireOp",EDGE,"E3.4.2.9"),sQuery(id+"F0.wireOp",EDGE,"E3.4.2.10"),sQuery(id+"F0.wireOp",EDGE,"E3.4.2.11"),sQuery(id+"F0.wireOp",EDGE,"E3.4.2.12"),sQuery(id+"F0.wireOp",EDGE,"E3.4.2.13"),sQuery(id+"F0.wireOp",EDGE,"E3.4.2.14"),sQuery(id+"F0.wireOp",EDGE,"E3.4.2.15"),sQuery(id+"F0.wireOp",EDGE,"E3.4.3.4"),sQuery(id+"F0.wireOp",EDGE,"E3.4.3.5"),sQuery(id+"F0.wireOp",EDGE,"E3.4.3.6"),sQuery(id+"F0.wireOp",EDGE,"E3.4.3.7"),sQuery(id+"F0.wireOp",EDGE,"E3.4.3.8"),sQuery(id+"F0.wireOp",EDGE,"E3.4.3.9"),sQuery(id+"F0.wireOp",EDGE,"E3.4.3.10"),sQuery(id+"F0.wireOp",EDGE,"E3.4.3.11"),sQuery(id+"F0.wireOp",EDGE,"E3.4.3.12"),sQuery(id+"F0.wireOp",EDGE,"E3.4.3.13"),sQuery(id+"F0.wireOp",EDGE,"E3.4.3.14"),sQuery(id+"F0.wireOp",EDGE,"E3.4.3.15"),sQuery(id+"F0.wireOp",EDGE,"E3.4.4.4"),sQuery(id+"F0.wireOp",EDGE,"E3.4.4.5"),sQuery(id+"F0.wireOp",EDGE,"E3.4.4.6"),sQuery(id+"F0.wireOp",EDGE,"E3.4.4.7"),sQuery(id+"F0.wireOp",EDGE,"E3.4.4.8"),sQuery(id+"F0.wireOp",EDGE,"E3.4.4.9"),sQuery(id+"F0.wireOp",EDGE,"E3.4.4.10"),sQuery(id+"F0.wireOp",EDGE,"E3.4.4.11"),sQuery(id+"F0.wireOp",EDGE,"E3.4.4.12"),sQuery(id+"F0.wireOp",EDGE,"E3.4.4.13"),sQuery(id+"F0.wireOp",EDGE,"E3.4.4.14"),sQuery(id+"F0.wireOp",EDGE,"E3.4.4.15"),sQuery(id+"F0.wireOp",EDGE,"E3.4.5.4"),sQuery(id+"F0.wireOp",EDGE,"E3.4.5.5"),sQuery(id+"F0.wireOp",EDGE,"E3.4.5.6"),sQuery(id+"F0.wireOp",EDGE,"E3.4.5.7"),sQuery(id+"F0.wireOp",EDGE,"E3.4.5.8"),sQuery(id+"F0.wireOp",EDGE,"E3.4.5.9"),sQuery(id+"F0.wireOp",EDGE,"E3.4.5.10"),sQuery(id+"F0.wireOp",EDGE,"E3.4.5.11"),sQuery(id+"F0.wireOp",EDGE,"E3.4.5.12"),sQuery(id+"F0.wireOp",EDGE,"E3.4.5.13"),sQuery(id+"F0.wireOp",EDGE,"E3.4.5.14"),sQuery(id+"F0.wireOp",EDGE,"E3.4.5.15"),sQuery(id+"F0.wireOp",EDGE,"E3.4.6.4"),sQuery(id+"F0.wireOp",EDGE,"E3.4.6.5"),sQuery(id+"F0.wireOp",EDGE,"E3.4.6.6"),sQuery(id+"F0.wireOp",EDGE,"E3.4.6.7"),sQuery(id+"F0.wireOp",EDGE,"E3.4.6.8"),sQuery(id+"F0.wireOp",EDGE,"E3.4.6.9"),sQuery(id+"F0.wireOp",EDGE,"E3.4.6.10"),sQuery(id+"F0.wireOp",EDGE,"E3.4.6.11"),sQuery(id+"F0.wireOp",EDGE,"E3.4.6.12"),sQuery(id+"F0.wireOp",EDGE,"E3.4.6.13"),sQuery(id+"F0.wireOp",EDGE,"E3.4.6.14"),sQuery(id+"F0.wireOp",EDGE,"E3.4.6.15"),sQuery(id+"F0.wireOp",EDGE,"E3.4.7.4"),sQuery(id+"F0.wireOp",EDGE,"E3.4.7.5"),sQuery(id+"F0.wireOp",EDGE,"E3.4.7.6"),sQuery(id+"F0.wireOp",EDGE,"E3.4.7.7"),sQuery(id+"F0.wireOp",EDGE,"E3.4.7.8"),sQuery(id+"F0.wireOp",EDGE,"E3.4.7.9"),sQuery(id+"F0.wireOp",EDGE,"E3.4.7.10"),sQuery(id+"F0.wireOp",EDGE,"E3.4.7.11"),sQuery(id+"F0.wireOp",EDGE,"E3.4.7.12"),sQuery(id+"F0.wireOp",EDGE,"E3.4.7.13"),sQuery(id+"F0.wireOp",EDGE,"E3.4.7.14"),sQuery(id+"F0.wireOp",EDGE,"E3.4.7.15"),sQuery(id+"F0.wireOp",EDGE,"E3.4.8.4"),sQuery(id+"F0.wireOp",EDGE,"E3.4.8.5"),sQuery(id+"F0.wireOp",EDGE,"E3.4.8.6"),sQuery(id+"F0.wireOp",EDGE,"E3.4.8.7"),sQuery(id+"F0.wireOp",EDGE,"E3.4.8.8"),sQuery(id+"F0.wireOp",EDGE,"E3.4.8.9"),sQuery(id+"F0.wireOp",EDGE,"E3.4.8.10"),sQuery(id+"F0.wireOp",EDGE,"E3.4.8.11"),sQuery(id+"F0.wireOp",EDGE,"E3.4.8.12"),sQuery(id+"F0.wireOp",EDGE,"E3.4.8.13"),sQuery(id+"F0.wireOp",EDGE,"E3.4.8.14"),sQuery(id+"F0.wireOp",EDGE,"E3.4.8.15"),sQuery(id+"F0.wireOp",EDGE,"E3.4.9.4"),sQuery(id+"F0.wireOp",EDGE,"E3.4.9.5"),sQuery(id+"F0.wireOp",EDGE,"E3.4.9.6"),sQuery(id+"F0.wireOp",EDGE,"E3.4.9.7"),sQuery(id+"F0.wireOp",EDGE,"E3.4.9.8"),sQuery(id+"F0.wireOp",EDGE,"E3.4.9.9"),sQuery(id+"F0.wireOp",EDGE,"E3.4.9.10"),sQuery(id+"F0.wireOp",EDGE,"E3.4.9.11"),sQuery(id+"F0.wireOp",EDGE,"E3.4.9.12"),sQuery(id+"F0.wireOp",EDGE,"E3.4.9.13"),sQuery(id+"F0.wireOp",EDGE,"E3.4.9.14"),sQuery(id+"F0.wireOp",EDGE,"E3.4.9.15"),sQuery(id+"F0.wireOp",EDGE,"E3.5.0.4"),sQuery(id+"F0.wireOp",EDGE,"E3.5.0.5"),sQuery(id+"F0.wireOp",EDGE,"E3.5.0.6"),sQuery(id+"F0.wireOp",EDGE,"E3.5.0.7"),sQuery(id+"F0.wireOp",EDGE,"E3.5.0.8"),sQuery(id+"F0.wireOp",EDGE,"E3.5.0.9"),sQuery(id+"F0.wireOp",EDGE,"E3.5.0.10"),sQuery(id+"F0.wireOp",EDGE,"E3.5.0.11"),sQuery(id+"F0.wireOp",EDGE,"E3.5.0.12"),sQuery(id+"F0.wireOp",EDGE,"E3.5.0.13"),sQuery(id+"F0.wireOp",EDGE,"E3.5.0.14"),sQuery(id+"F0.wireOp",EDGE,"E3.5.0.15"),sQuery(id+"F0.wireOp",EDGE,"E3.5.1.4"),sQuery(id+"F0.wireOp",EDGE,"E3.5.1.5"),sQuery(id+"F0.wireOp",EDGE,"E3.5.1.6"),sQuery(id+"F0.wireOp",EDGE,"E3.5.1.7"),sQuery(id+"F0.wireOp",EDGE,"E3.5.1.8"),sQuery(id+"F0.wireOp",EDGE,"E3.5.1.9"),sQuery(id+"F0.wireOp",EDGE,"E3.5.1.10"),sQuery(id+"F0.wireOp",EDGE,"E3.5.1.11"),sQuery(id+"F0.wireOp",EDGE,"E3.5.1.12"),sQuery(id+"F0.wireOp",EDGE,"E3.5.1.13"),sQuery(id+"F0.wireOp",EDGE,"E3.5.1.14"),sQuery(id+"F0.wireOp",EDGE,"E3.5.1.15"),sQuery(id+"F0.wireOp",EDGE,"E3.5.2.4"),sQuery(id+"F0.wireOp",EDGE,"E3.5.2.5"),sQuery(id+"F0.wireOp",EDGE,"E3.5.2.6"),sQuery(id+"F0.wireOp",EDGE,"E3.5.2.7"),sQuery(id+"F0.wireOp",EDGE,"E3.5.2.8"),sQuery(id+"F0.wireOp",EDGE,"E3.5.2.9"),sQuery(id+"F0.wireOp",EDGE,"E3.5.2.10"),sQuery(id+"F0.wireOp",EDGE,"E3.5.2.11"),sQuery(id+"F0.wireOp",EDGE,"E3.5.2.12"),sQuery(id+"F0.wireOp",EDGE,"E3.5.2.13"),sQuery(id+"F0.wireOp",EDGE,"E3.5.2.14"),sQuery(id+"F0.wireOp",EDGE,"E3.5.2.15"),sQuery(id+"F0.wireOp",EDGE,"E3.5.3.4"),sQuery(id+"F0.wireOp",EDGE,"E3.5.3.5"),sQuery(id+"F0.wireOp",EDGE,"E3.5.3.6"),sQuery(id+"F0.wireOp",EDGE,"E3.5.3.7"),sQuery(id+"F0.wireOp",EDGE,"E3.5.3.8"),sQuery(id+"F0.wireOp",EDGE,"E3.5.3.9"),sQuery(id+"F0.wireOp",EDGE,"E3.5.3.10"),sQuery(id+"F0.wireOp",EDGE,"E3.5.3.11"),sQuery(id+"F0.wireOp",EDGE,"E3.5.3.12"),sQuery(id+"F0.wireOp",EDGE,"E3.5.3.13"),sQuery(id+"F0.wireOp",EDGE,"E3.5.3.14"),sQuery(id+"F0.wireOp",EDGE,"E3.5.3.15"),sQuery(id+"F0.wireOp",EDGE,"E3.5.4.4"),sQuery(id+"F0.wireOp",EDGE,"E3.5.4.5"),sQuery(id+"F0.wireOp",EDGE,"E3.5.4.6"),sQuery(id+"F0.wireOp",EDGE,"E3.5.4.7"),sQuery(id+"F0.wireOp",EDGE,"E3.5.4.8"),sQuery(id+"F0.wireOp",EDGE,"E3.5.4.9"),sQuery(id+"F0.wireOp",EDGE,"E3.5.4.10"),sQuery(id+"F0.wireOp",EDGE,"E3.5.4.11"),sQuery(id+"F0.wireOp",EDGE,"E3.5.4.12"),sQuery(id+"F0.wireOp",EDGE,"E3.5.4.13"),sQuery(id+"F0.wireOp",EDGE,"E3.5.4.14"),sQuery(id+"F0.wireOp",EDGE,"E3.5.4.15"),sQuery(id+"F0.wireOp",EDGE,"E3.5.5.4"),sQuery(id+"F0.wireOp",EDGE,"E3.5.5.5"),sQuery(id+"F0.wireOp",EDGE,"E3.5.5.6"),sQuery(id+"F0.wireOp",EDGE,"E3.5.5.7"),sQuery(id+"F0.wireOp",EDGE,"E3.5.5.8"),sQuery(id+"F0.wireOp",EDGE,"E3.5.5.9"),sQuery(id+"F0.wireOp",EDGE,"E3.5.5.10"),sQuery(id+"F0.wireOp",EDGE,"E3.5.5.11"),sQuery(id+"F0.wireOp",EDGE,"E3.5.5.12"),sQuery(id+"F0.wireOp",EDGE,"E3.5.5.13"),sQuery(id+"F0.wireOp",EDGE,"E3.5.5.14"),sQuery(id+"F0.wireOp",EDGE,"E3.5.5.15"),sQuery(id+"F0.wireOp",EDGE,"E3.5.6.4"),sQuery(id+"F0.wireOp",EDGE,"E3.5.6.5"),sQuery(id+"F0.wireOp",EDGE,"E3.5.6.6"),sQuery(id+"F0.wireOp",EDGE,"E3.5.6.7"),sQuery(id+"F0.wireOp",EDGE,"E3.5.6.8"),sQuery(id+"F0.wireOp",EDGE,"E3.5.6.9"),sQuery(id+"F0.wireOp",EDGE,"E3.5.6.10"),sQuery(id+"F0.wireOp",EDGE,"E3.5.6.11"),sQuery(id+"F0.wireOp",EDGE,"E3.5.6.12"),sQuery(id+"F0.wireOp",EDGE,"E3.5.6.13"),sQuery(id+"F0.wireOp",EDGE,"E3.5.6.14"),sQuery(id+"F0.wireOp",EDGE,"E3.5.6.15"),sQuery(id+"F0.wireOp",EDGE,"E3.5.7.4"),sQuery(id+"F0.wireOp",EDGE,"E3.5.7.5"),sQuery(id+"F0.wireOp",EDGE,"E3.5.7.6"),sQuery(id+"F0.wireOp",EDGE,"E3.5.7.7"),sQuery(id+"F0.wireOp",EDGE,"E3.5.7.8"),sQuery(id+"F0.wireOp",EDGE,"E3.5.7.9"),sQuery(id+"F0.wireOp",EDGE,"E3.5.7.10"),sQuery(id+"F0.wireOp",EDGE,"E3.5.7.11"),sQuery(id+"F0.wireOp",EDGE,"E3.5.7.12"),sQuery(id+"F0.wireOp",EDGE,"E3.5.7.13"),sQuery(id+"F0.wireOp",EDGE,"E3.5.7.14"),sQuery(id+"F0.wireOp",EDGE,"E3.5.7.15"),sQuery(id+"F0.wireOp",EDGE,"E3.5.8.4"),sQuery(id+"F0.wireOp",EDGE,"E3.5.8.5"),sQuery(id+"F0.wireOp",EDGE,"E3.5.8.6"),sQuery(id+"F0.wireOp",EDGE,"E3.5.8.7"),sQuery(id+"F0.wireOp",EDGE,"E3.5.8.8"),sQuery(id+"F0.wireOp",EDGE,"E3.5.8.9"),sQuery(id+"F0.wireOp",EDGE,"E3.5.8.10"),sQuery(id+"F0.wireOp",EDGE,"E3.5.8.11"),sQuery(id+"F0.wireOp",EDGE,"E3.5.8.12"),sQuery(id+"F0.wireOp",EDGE,"E3.5.8.13"),sQuery(id+"F0.wireOp",EDGE,"E3.5.8.14"),sQuery(id+"F0.wireOp",EDGE,"E3.5.8.15"),sQuery(id+"F0.wireOp",EDGE,"E3.5.9.4"),sQuery(id+"F0.wireOp",EDGE,"E3.5.9.5"),sQuery(id+"F0.wireOp",EDGE,"E3.5.9.6"),sQuery(id+"F0.wireOp",EDGE,"E3.5.9.7"),sQuery(id+"F0.wireOp",EDGE,"E3.5.9.8"),sQuery(id+"F0.wireOp",EDGE,"E3.5.9.9"),sQuery(id+"F0.wireOp",EDGE,"E3.5.9.10"),sQuery(id+"F0.wireOp",EDGE,"E3.5.9.11"),sQuery(id+"F0.wireOp",EDGE,"E3.5.9.12"),sQuery(id+"F0.wireOp",EDGE,"E3.5.9.13"),sQuery(id+"F0.wireOp",EDGE,"E3.5.9.14"),sQuery(id+"F0.wireOp",EDGE,"E3.5.9.15"),sQuery(id+"F0.wireOp",EDGE,"E3.6.0.4"),sQuery(id+"F0.wireOp",EDGE,"E3.6.0.5"),sQuery(id+"F0.wireOp",EDGE,"E3.6.0.6"),sQuery(id+"F0.wireOp",EDGE,"E3.6.0.7"),sQuery(id+"F0.wireOp",EDGE,"E3.6.0.8"),sQuery(id+"F0.wireOp",EDGE,"E3.6.0.9"),sQuery(id+"F0.wireOp",EDGE,"E3.6.0.10"),sQuery(id+"F0.wireOp",EDGE,"E3.6.0.11"),sQuery(id+"F0.wireOp",EDGE,"E3.6.0.12"),sQuery(id+"F0.wireOp",EDGE,"E3.6.0.13"),sQuery(id+"F0.wireOp",EDGE,"E3.6.0.14"),sQuery(id+"F0.wireOp",EDGE,"E3.6.0.15"),sQuery(id+"F0.wireOp",EDGE,"E3.6.1.4"),sQuery(id+"F0.wireOp",EDGE,"E3.6.1.5"),sQuery(id+"F0.wireOp",EDGE,"E3.6.1.6"),sQuery(id+"F0.wireOp",EDGE,"E3.6.1.7"),sQuery(id+"F0.wireOp",EDGE,"E3.6.1.8"),sQuery(id+"F0.wireOp",EDGE,"E3.6.1.9"),sQuery(id+"F0.wireOp",EDGE,"E3.6.1.10"),sQuery(id+"F0.wireOp",EDGE,"E3.6.1.11"),sQuery(id+"F0.wireOp",EDGE,"E3.6.1.12"),sQuery(id+"F0.wireOp",EDGE,"E3.6.1.13"),sQuery(id+"F0.wireOp",EDGE,"E3.6.1.14"),sQuery(id+"F0.wireOp",EDGE,"E3.6.1.15"),sQuery(id+"F0.wireOp",EDGE,"E3.6.2.4"),sQuery(id+"F0.wireOp",EDGE,"E3.6.2.5"),sQuery(id+"F0.wireOp",EDGE,"E3.6.2.6"),sQuery(id+"F0.wireOp",EDGE,"E3.6.2.7"),sQuery(id+"F0.wireOp",EDGE,"E3.6.2.8"),sQuery(id+"F0.wireOp",EDGE,"E3.6.2.9"),sQuery(id+"F0.wireOp",EDGE,"E3.6.2.10"),sQuery(id+"F0.wireOp",EDGE,"E3.6.2.11"),sQuery(id+"F0.wireOp",EDGE,"E3.6.2.12"),sQuery(id+"F0.wireOp",EDGE,"E3.6.2.13"),sQuery(id+"F0.wireOp",EDGE,"E3.6.2.14"),sQuery(id+"F0.wireOp",EDGE,"E3.6.2.15"),sQuery(id+"F0.wireOp",EDGE,"E3.6.3.4"),sQuery(id+"F0.wireOp",EDGE,"E3.6.3.5"),sQuery(id+"F0.wireOp",EDGE,"E3.6.3.6"),sQuery(id+"F0.wireOp",EDGE,"E3.6.3.7"),sQuery(id+"F0.wireOp",EDGE,"E3.6.3.8"),sQuery(id+"F0.wireOp",EDGE,"E3.6.3.9"),sQuery(id+"F0.wireOp",EDGE,"E3.6.3.10"),sQuery(id+"F0.wireOp",EDGE,"E3.6.3.11"),sQuery(id+"F0.wireOp",EDGE,"E3.6.3.12"),sQuery(id+"F0.wireOp",EDGE,"E3.6.3.13"),sQuery(id+"F0.wireOp",EDGE,"E3.6.3.14"),sQuery(id+"F0.wireOp",EDGE,"E3.6.3.15"),sQuery(id+"F0.wireOp",EDGE,"E3.6.4.4"),sQuery(id+"F0.wireOp",EDGE,"E3.6.4.5"),sQuery(id+"F0.wireOp",EDGE,"E3.6.4.6"),sQuery(id+"F0.wireOp",EDGE,"E3.6.4.7"),sQuery(id+"F0.wireOp",EDGE,"E3.6.4.8"),sQuery(id+"F0.wireOp",EDGE,"E3.6.4.9"),sQuery(id+"F0.wireOp",EDGE,"E3.6.4.10"),sQuery(id+"F0.wireOp",EDGE,"E3.6.4.11"),sQuery(id+"F0.wireOp",EDGE,"E3.6.4.12"),sQuery(id+"F0.wireOp",EDGE,"E3.6.4.13"),sQuery(id+"F0.wireOp",EDGE,"E3.6.4.14"),sQuery(id+"F0.wireOp",EDGE,"E3.6.4.15"),sQuery(id+"F0.wireOp",EDGE,"E3.6.5.4"),sQuery(id+"F0.wireOp",EDGE,"E3.6.5.5"),sQuery(id+"F0.wireOp",EDGE,"E3.6.5.6"),sQuery(id+"F0.wireOp",EDGE,"E3.6.5.7"),sQuery(id+"F0.wireOp",EDGE,"E3.6.5.8"),sQuery(id+"F0.wireOp",EDGE,"E3.6.5.9"),sQuery(id+"F0.wireOp",EDGE,"E3.6.5.10"),sQuery(id+"F0.wireOp",EDGE,"E3.6.5.11"),sQuery(id+"F0.wireOp",EDGE,"E3.6.5.12"),sQuery(id+"F0.wireOp",EDGE,"E3.6.5.13"),sQuery(id+"F0.wireOp",EDGE,"E3.6.5.14"),sQuery(id+"F0.wireOp",EDGE,"E3.6.5.15"),sQuery(id+"F0.wireOp",EDGE,"E3.6.6.4"),sQuery(id+"F0.wireOp",EDGE,"E3.6.6.5"),sQuery(id+"F0.wireOp",EDGE,"E3.6.6.6"),sQuery(id+"F0.wireOp",EDGE,"E3.6.6.7"),sQuery(id+"F0.wireOp",EDGE,"E3.6.6.8"),sQuery(id+"F0.wireOp",EDGE,"E3.6.6.9"),sQuery(id+"F0.wireOp",EDGE,"E3.6.6.10"),sQuery(id+"F0.wireOp",EDGE,"E3.6.6.11"),sQuery(id+"F0.wireOp",EDGE,"E3.6.6.12"),sQuery(id+"F0.wireOp",EDGE,"E3.6.6.13"),sQuery(id+"F0.wireOp",EDGE,"E3.6.6.14"),sQuery(id+"F0.wireOp",EDGE,"E3.6.6.15"),sQuery(id+"F0.wireOp",EDGE,"E3.6.7.4"),sQuery(id+"F0.wireOp",EDGE,"E3.6.7.5"),sQuery(id+"F0.wireOp",EDGE,"E3.6.7.6"),sQuery(id+"F0.wireOp",EDGE,"E3.6.7.7"),sQuery(id+"F0.wireOp",EDGE,"E3.6.7.8"),sQuery(id+"F0.wireOp",EDGE,"E3.6.7.9"),sQuery(id+"F0.wireOp",EDGE,"E3.6.7.10"),sQuery(id+"F0.wireOp",EDGE,"E3.6.7.11"),sQuery(id+"F0.wireOp",EDGE,"E3.6.7.12"),sQuery(id+"F0.wireOp",EDGE,"E3.6.7.13"),sQuery(id+"F0.wireOp",EDGE,"E3.6.7.14"),sQuery(id+"F0.wireOp",EDGE,"E3.6.7.15"),sQuery(id+"F0.wireOp",EDGE,"E3.6.8.4"),sQuery(id+"F0.wireOp",EDGE,"E3.6.8.5"),sQuery(id+"F0.wireOp",EDGE,"E3.6.8.6"),sQuery(id+"F0.wireOp",EDGE,"E3.6.8.7"),sQuery(id+"F0.wireOp",EDGE,"E3.6.8.8"),sQuery(id+"F0.wireOp",EDGE,"E3.6.8.9"),sQuery(id+"F0.wireOp",EDGE,"E3.6.8.10"),sQuery(id+"F0.wireOp",EDGE,"E3.6.8.11"),sQuery(id+"F0.wireOp",EDGE,"E3.6.8.12"),sQuery(id+"F0.wireOp",EDGE,"E3.6.8.13"),sQuery(id+"F0.wireOp",EDGE,"E3.6.8.14"),sQuery(id+"F0.wireOp",EDGE,"E3.6.8.15"),sQuery(id+"F0.wireOp",EDGE,"E3.6.9.4"),sQuery(id+"F0.wireOp",EDGE,"E3.6.9.5"),sQuery(id+"F0.wireOp",EDGE,"E3.6.9.6"),sQuery(id+"F0.wireOp",EDGE,"E3.6.9.7"),sQuery(id+"F0.wireOp",EDGE,"E3.6.9.8"),sQuery(id+"F0.wireOp",EDGE,"E3.6.9.9"),sQuery(id+"F0.wireOp",EDGE,"E3.6.9.10"),sQuery(id+"F0.wireOp",EDGE,"E3.6.9.11"),sQuery(id+"F0.wireOp",EDGE,"E3.6.9.12"),sQuery(id+"F0.wireOp",EDGE,"E3.6.9.13"),sQuery(id+"F0.wireOp",EDGE,"E3.6.9.14"),sQuery(id+"F0.wireOp",EDGE,"E3.6.9.15"),sQuery(id+"F0.wireOp",EDGE,"E3.7.0.4"),sQuery(id+"F0.wireOp",EDGE,"E3.7.0.5"),sQuery(id+"F0.wireOp",EDGE,"E3.7.0.6"),sQuery(id+"F0.wireOp",EDGE,"E3.7.0.7"),sQuery(id+"F0.wireOp",EDGE,"E3.7.0.8"),sQuery(id+"F0.wireOp",EDGE,"E3.7.0.9"),sQuery(id+"F0.wireOp",EDGE,"E3.7.0.10"),sQuery(id+"F0.wireOp",EDGE,"E3.7.0.11"),sQuery(id+"F0.wireOp",EDGE,"E3.7.0.12"),sQuery(id+"F0.wireOp",EDGE,"E3.7.0.13"),sQuery(id+"F0.wireOp",EDGE,"E3.7.0.14"),sQuery(id+"F0.wireOp",EDGE,"E3.7.0.15"),sQuery(id+"F0.wireOp",EDGE,"E3.7.1.4"),sQuery(id+"F0.wireOp",EDGE,"E3.7.1.5"),sQuery(id+"F0.wireOp",EDGE,"E3.7.1.6"),sQuery(id+"F0.wireOp",EDGE,"E3.7.1.7"),sQuery(id+"F0.wireOp",EDGE,"E3.7.1.8"),sQuery(id+"F0.wireOp",EDGE,"E3.7.1.9"),sQuery(id+"F0.wireOp",EDGE,"E3.7.1.10"),sQuery(id+"F0.wireOp",EDGE,"E3.7.1.11"),sQuery(id+"F0.wireOp",EDGE,"E3.7.1.12"),sQuery(id+"F0.wireOp",EDGE,"E3.7.1.13"),sQuery(id+"F0.wireOp",EDGE,"E3.7.1.14"),sQuery(id+"F0.wireOp",EDGE,"E3.7.1.15"),sQuery(id+"F0.wireOp",EDGE,"E3.7.2.4"),sQuery(id+"F0.wireOp",EDGE,"E3.7.2.5"),sQuery(id+"F0.wireOp",EDGE,"E3.7.2.6"),sQuery(id+"F0.wireOp",EDGE,"E3.7.2.7"),sQuery(id+"F0.wireOp",EDGE,"E3.7.2.8"),sQuery(id+"F0.wireOp",EDGE,"E3.7.2.9"),sQuery(id+"F0.wireOp",EDGE,"E3.7.2.10"),sQuery(id+"F0.wireOp",EDGE,"E3.7.2.11"),sQuery(id+"F0.wireOp",EDGE,"E3.7.2.12"),sQuery(id+"F0.wireOp",EDGE,"E3.7.2.13"),sQuery(id+"F0.wireOp",EDGE,"E3.7.2.14"),sQuery(id+"F0.wireOp",EDGE,"E3.7.2.15"),sQuery(id+"F0.wireOp",EDGE,"E3.7.3.4"),sQuery(id+"F0.wireOp",EDGE,"E3.7.3.5"),sQuery(id+"F0.wireOp",EDGE,"E3.7.3.6"),sQuery(id+"F0.wireOp",EDGE,"E3.7.3.7"),sQuery(id+"F0.wireOp",EDGE,"E3.7.3.8"),sQuery(id+"F0.wireOp",EDGE,"E3.7.3.9"),sQuery(id+"F0.wireOp",EDGE,"E3.7.3.10"),sQuery(id+"F0.wireOp",EDGE,"E3.7.3.11"),sQuery(id+"F0.wireOp",EDGE,"E3.7.3.12"),sQuery(id+"F0.wireOp",EDGE,"E3.7.3.13"),sQuery(id+"F0.wireOp",EDGE,"E3.7.3.14"),sQuery(id+"F0.wireOp",EDGE,"E3.7.3.15"),sQuery(id+"F0.wireOp",EDGE,"E3.7.4.4"),sQuery(id+"F0.wireOp",EDGE,"E3.7.4.5"),sQuery(id+"F0.wireOp",EDGE,"E3.7.4.6"),sQuery(id+"F0.wireOp",EDGE,"E3.7.4.7"),sQuery(id+"F0.wireOp",EDGE,"E3.7.4.8"),sQuery(id+"F0.wireOp",EDGE,"E3.7.4.9"),sQuery(id+"F0.wireOp",EDGE,"E3.7.4.10"),sQuery(id+"F0.wireOp",EDGE,"E3.7.4.11"),sQuery(id+"F0.wireOp",EDGE,"E3.7.4.12"),sQuery(id+"F0.wireOp",EDGE,"E3.7.4.13"),sQuery(id+"F0.wireOp",EDGE,"E3.7.4.14"),sQuery(id+"F0.wireOp",EDGE,"E3.7.4.15"),sQuery(id+"F0.wireOp",EDGE,"E3.7.5.4"),sQuery(id+"F0.wireOp",EDGE,"E3.7.5.5"),sQuery(id+"F0.wireOp",EDGE,"E3.7.5.6"),sQuery(id+"F0.wireOp",EDGE,"E3.7.5.7"),sQuery(id+"F0.wireOp",EDGE,"E3.7.5.8"),sQuery(id+"F0.wireOp",EDGE,"E3.7.5.9"),sQuery(id+"F0.wireOp",EDGE,"E3.7.5.10"),sQuery(id+"F0.wireOp",EDGE,"E3.7.5.11"),sQuery(id+"F0.wireOp",EDGE,"E3.7.5.12"),sQuery(id+"F0.wireOp",EDGE,"E3.7.5.13"),sQuery(id+"F0.wireOp",EDGE,"E3.7.5.14"),sQuery(id+"F0.wireOp",EDGE,"E3.7.5.15"),sQuery(id+"F0.wireOp",EDGE,"E3.7.6.4"),sQuery(id+"F0.wireOp",EDGE,"E3.7.6.5"),sQuery(id+"F0.wireOp",EDGE,"E3.7.6.6"),sQuery(id+"F0.wireOp",EDGE,"E3.7.6.7"),sQuery(id+"F0.wireOp",EDGE,"E3.7.6.8"),sQuery(id+"F0.wireOp",EDGE,"E3.7.6.9"),sQuery(id+"F0.wireOp",EDGE,"E3.7.6.10"),sQuery(id+"F0.wireOp",EDGE,"E3.7.6.11"),sQuery(id+"F0.wireOp",EDGE,"E3.7.6.12"),sQuery(id+"F0.wireOp",EDGE,"E3.7.6.13"),sQuery(id+"F0.wireOp",EDGE,"E3.7.6.14"),sQuery(id+"F0.wireOp",EDGE,"E3.7.6.15"),sQuery(id+"F0.wireOp",EDGE,"E3.7.7.4"),sQuery(id+"F0.wireOp",EDGE,"E3.7.7.5"),sQuery(id+"F0.wireOp",EDGE,"E3.7.7.6"),sQuery(id+"F0.wireOp",EDGE,"E3.7.7.7"),sQuery(id+"F0.wireOp",EDGE,"E3.7.7.8"),sQuery(id+"F0.wireOp",EDGE,"E3.7.7.9"),sQuery(id+"F0.wireOp",EDGE,"E3.7.7.10"),sQuery(id+"F0.wireOp",EDGE,"E3.7.7.11"),sQuery(id+"F0.wireOp",EDGE,"E3.7.7.12"),sQuery(id+"F0.wireOp",EDGE,"E3.7.7.13"),sQuery(id+"F0.wireOp",EDGE,"E3.7.7.14"),sQuery(id+"F0.wireOp",EDGE,"E3.7.7.15"),sQuery(id+"F0.wireOp",EDGE,"E3.7.8.4"),sQuery(id+"F0.wireOp",EDGE,"E3.7.8.5"),sQuery(id+"F0.wireOp",EDGE,"E3.7.8.6"),sQuery(id+"F0.wireOp",EDGE,"E3.7.8.7"),sQuery(id+"F0.wireOp",EDGE,"E3.7.8.8"),sQuery(id+"F0.wireOp",EDGE,"E3.7.8.9"),sQuery(id+"F0.wireOp",EDGE,"E3.7.8.10"),sQuery(id+"F0.wireOp",EDGE,"E3.7.8.11"),sQuery(id+"F0.wireOp",EDGE,"E3.7.8.12"),sQuery(id+"F0.wireOp",EDGE,"E3.7.8.13"),sQuery(id+"F0.wireOp",EDGE,"E3.7.8.14"),sQuery(id+"F0.wireOp",EDGE,"E3.7.8.15"),sQuery(id+"F0.wireOp",EDGE,"E3.7.9.4"),sQuery(id+"F0.wireOp",EDGE,"E3.7.9.5"),sQuery(id+"F0.wireOp",EDGE,"E3.7.9.6"),sQuery(id+"F0.wireOp",EDGE,"E3.7.9.7"),sQuery(id+"F0.wireOp",EDGE,"E3.7.9.8"),sQuery(id+"F0.wireOp",EDGE,"E3.7.9.9"),sQuery(id+"F0.wireOp",EDGE,"E3.7.9.10"),sQuery(id+"F0.wireOp",EDGE,"E3.7.9.11"),sQuery(id+"F0.wireOp",EDGE,"E3.7.9.12"),sQuery(id+"F0.wireOp",EDGE,"E3.7.9.13"),sQuery(id+"F0.wireOp",EDGE,"E3.7.9.14"),sQuery(id+"F0.wireOp",EDGE,"E3.7.9.15"),sQuery(id+"F0.wireOp",EDGE,"E3.8.0.4"),sQuery(id+"F0.wireOp",EDGE,"E3.8.0.5"),sQuery(id+"F0.wireOp",EDGE,"E3.8.0.6"),sQuery(id+"F0.wireOp",EDGE,"E3.8.0.7"),sQuery(id+"F0.wireOp",EDGE,"E3.8.0.8"),sQuery(id+"F0.wireOp",EDGE,"E3.8.0.9"),sQuery(id+"F0.wireOp",EDGE,"E3.8.0.10"),sQuery(id+"F0.wireOp",EDGE,"E3.8.0.11"),sQuery(id+"F0.wireOp",EDGE,"E3.8.0.12"),sQuery(id+"F0.wireOp",EDGE,"E3.8.0.13"),sQuery(id+"F0.wireOp",EDGE,"E3.8.0.14"),sQuery(id+"F0.wireOp",EDGE,"E3.8.0.15"),sQuery(id+"F0.wireOp",EDGE,"E3.8.1.4"),sQuery(id+"F0.wireOp",EDGE,"E3.8.1.5"),sQuery(id+"F0.wireOp",EDGE,"E3.8.1.6"),sQuery(id+"F0.wireOp",EDGE,"E3.8.1.7"),sQuery(id+"F0.wireOp",EDGE,"E3.8.1.8"),sQuery(id+"F0.wireOp",EDGE,"E3.8.1.9"),sQuery(id+"F0.wireOp",EDGE,"E3.8.1.10"),sQuery(id+"F0.wireOp",EDGE,"E3.8.1.11"),sQuery(id+"F0.wireOp",EDGE,"E3.8.1.12"),sQuery(id+"F0.wireOp",EDGE,"E3.8.1.13"),sQuery(id+"F0.wireOp",EDGE,"E3.8.1.14"),sQuery(id+"F0.wireOp",EDGE,"E3.8.1.15"),sQuery(id+"F0.wireOp",EDGE,"E3.8.2.4"),sQuery(id+"F0.wireOp",EDGE,"E3.8.2.5"),sQuery(id+"F0.wireOp",EDGE,"E3.8.2.6"),sQuery(id+"F0.wireOp",EDGE,"E3.8.2.7"),sQuery(id+"F0.wireOp",EDGE,"E3.8.2.8"),sQuery(id+"F0.wireOp",EDGE,"E3.8.2.9"),sQuery(id+"F0.wireOp",EDGE,"E3.8.2.10"),sQuery(id+"F0.wireOp",EDGE,"E3.8.2.11"),sQuery(id+"F0.wireOp",EDGE,"E3.8.2.12"),sQuery(id+"F0.wireOp",EDGE,"E3.8.2.13"),sQuery(id+"F0.wireOp",EDGE,"E3.8.2.14"),sQuery(id+"F0.wireOp",EDGE,"E3.8.2.15"),sQuery(id+"F0.wireOp",EDGE,"E3.8.3.4"),sQuery(id+"F0.wireOp",EDGE,"E3.8.3.5"),sQuery(id+"F0.wireOp",EDGE,"E3.8.3.6"),sQuery(id+"F0.wireOp",EDGE,"E3.8.3.7"),sQuery(id+"F0.wireOp",EDGE,"E3.8.3.8"),sQuery(id+"F0.wireOp",EDGE,"E3.8.3.9"),sQuery(id+"F0.wireOp",EDGE,"E3.8.3.10"),sQuery(id+"F0.wireOp",EDGE,"E3.8.3.11"),sQuery(id+"F0.wireOp",EDGE,"E3.8.3.12"),sQuery(id+"F0.wireOp",EDGE,"E3.8.3.13"),sQuery(id+"F0.wireOp",EDGE,"E3.8.3.14"),sQuery(id+"F0.wireOp",EDGE,"E3.8.3.15"),sQuery(id+"F0.wireOp",EDGE,"E3.8.4.4"),sQuery(id+"F0.wireOp",EDGE,"E3.8.4.5"),sQuery(id+"F0.wireOp",EDGE,"E3.8.4.6"),sQuery(id+"F0.wireOp",EDGE,"E3.8.4.7"),sQuery(id+"F0.wireOp",EDGE,"E3.8.4.8"),sQuery(id+"F0.wireOp",EDGE,"E3.8.4.9"),sQuery(id+"F0.wireOp",EDGE,"E3.8.4.10"),sQuery(id+"F0.wireOp",EDGE,"E3.8.4.11"),sQuery(id+"F0.wireOp",EDGE,"E3.8.4.12"),sQuery(id+"F0.wireOp",EDGE,"E3.8.4.13"),sQuery(id+"F0.wireOp",EDGE,"E3.8.4.14"),sQuery(id+"F0.wireOp",EDGE,"E3.8.4.15"),sQuery(id+"F0.wireOp",EDGE,"E3.8.5.4"),sQuery(id+"F0.wireOp",EDGE,"E3.8.5.5"),sQuery(id+"F0.wireOp",EDGE,"E3.8.5.6"),sQuery(id+"F0.wireOp",EDGE,"E3.8.5.7"),sQuery(id+"F0.wireOp",EDGE,"E3.8.5.8"),sQuery(id+"F0.wireOp",EDGE,"E3.8.5.9"),sQuery(id+"F0.wireOp",EDGE,"E3.8.5.10"),sQuery(id+"F0.wireOp",EDGE,"E3.8.5.11"),sQuery(id+"F0.wireOp",EDGE,"E3.8.5.12"),sQuery(id+"F0.wireOp",EDGE,"E3.8.5.13"),sQuery(id+"F0.wireOp",EDGE,"E3.8.5.14"),sQuery(id+"F0.wireOp",EDGE,"E3.8.5.15"),sQuery(id+"F0.wireOp",EDGE,"E3.8.6.4"),sQuery(id+"F0.wireOp",EDGE,"E3.8.6.5"),sQuery(id+"F0.wireOp",EDGE,"E3.8.6.6"),sQuery(id+"F0.wireOp",EDGE,"E3.8.6.7"),sQuery(id+"F0.wireOp",EDGE,"E3.8.6.8"),sQuery(id+"F0.wireOp",EDGE,"E3.8.6.9"),sQuery(id+"F0.wireOp",EDGE,"E3.8.6.10"),sQuery(id+"F0.wireOp",EDGE,"E3.8.6.11"),sQuery(id+"F0.wireOp",EDGE,"E3.8.6.12"),sQuery(id+"F0.wireOp",EDGE,"E3.8.6.13"),sQuery(id+"F0.wireOp",EDGE,"E3.8.6.14"),sQuery(id+"F0.wireOp",EDGE,"E3.8.6.15"),sQuery(id+"F0.wireOp",EDGE,"E3.8.7.4"),sQuery(id+"F0.wireOp",EDGE,"E3.8.7.5"),sQuery(id+"F0.wireOp",EDGE,"E3.8.7.6"),sQuery(id+"F0.wireOp",EDGE,"E3.8.7.7"),sQuery(id+"F0.wireOp",EDGE,"E3.8.7.8"),sQuery(id+"F0.wireOp",EDGE,"E3.8.7.9"),sQuery(id+"F0.wireOp",EDGE,"E3.8.7.10"),sQuery(id+"F0.wireOp",EDGE,"E3.8.7.11"),sQuery(id+"F0.wireOp",EDGE,"E3.8.7.12"),sQuery(id+"F0.wireOp",EDGE,"E3.8.7.13"),sQuery(id+"F0.wireOp",EDGE,"E3.8.7.14"),sQuery(id+"F0.wireOp",EDGE,"E3.8.7.15"),sQuery(id+"F0.wireOp",EDGE,"E3.8.8.4"),sQuery(id+"F0.wireOp",EDGE,"E3.8.8.5"),sQuery(id+"F0.wireOp",EDGE,"E3.8.8.6"),sQuery(id+"F0.wireOp",EDGE,"E3.8.8.7"),sQuery(id+"F0.wireOp",EDGE,"E3.8.8.8"),sQuery(id+"F0.wireOp",EDGE,"E3.8.8.9"),sQuery(id+"F0.wireOp",EDGE,"E3.8.8.10"),sQuery(id+"F0.wireOp",EDGE,"E3.8.8.11"),sQuery(id+"F0.wireOp",EDGE,"E3.8.8.12"),sQuery(id+"F0.wireOp",EDGE,"E3.8.8.13"),sQuery(id+"F0.wireOp",EDGE,"E3.8.8.14"),sQuery(id+"F0.wireOp",EDGE,"E3.8.8.15"),sQuery(id+"F0.wireOp",EDGE,"E3.8.9.4"),sQuery(id+"F0.wireOp",EDGE,"E3.8.9.5"),sQuery(id+"F0.wireOp",EDGE,"E3.8.9.6"),sQuery(id+"F0.wireOp",EDGE,"E3.8.9.7"),sQuery(id+"F0.wireOp",EDGE,"E3.8.9.8"),sQuery(id+"F0.wireOp",EDGE,"E3.8.9.9"),sQuery(id+"F0.wireOp",EDGE,"E3.8.9.10"),sQuery(id+"F0.wireOp",EDGE,"E3.8.9.11"),sQuery(id+"F0.wireOp",EDGE,"E3.8.9.12"),sQuery(id+"F0.wireOp",EDGE,"E3.8.9.13"),sQuery(id+"F0.wireOp",EDGE,"E3.8.9.14"),sQuery(id+"F0.wireOp",EDGE,"E3.8.9.15"),sQuery(id+"F0.wireOp",EDGE,"E3.9.0.4"),sQuery(id+"F0.wireOp",EDGE,"E3.9.0.5"),sQuery(id+"F0.wireOp",EDGE,"E3.9.0.6"),sQuery(id+"F0.wireOp",EDGE,"E3.9.0.7"),sQuery(id+"F0.wireOp",EDGE,"E3.9.0.8"),sQuery(id+"F0.wireOp",EDGE,"E3.9.0.9"),sQuery(id+"F0.wireOp",EDGE,"E3.9.0.10"),sQuery(id+"F0.wireOp",EDGE,"E3.9.0.11"),sQuery(id+"F0.wireOp",EDGE,"E3.9.0.12"),sQuery(id+"F0.wireOp",EDGE,"E3.9.0.13"),sQuery(id+"F0.wireOp",EDGE,"E3.9.0.14"),sQuery(id+"F0.wireOp",EDGE,"E3.9.0.15"),sQuery(id+"F0.wireOp",EDGE,"E3.9.1.4"),sQuery(id+"F0.wireOp",EDGE,"E3.9.1.5"),sQuery(id+"F0.wireOp",EDGE,"E3.9.1.6"),sQuery(id+"F0.wireOp",EDGE,"E3.9.1.7"),sQuery(id+"F0.wireOp",EDGE,"E3.9.1.8"),sQuery(id+"F0.wireOp",EDGE,"E3.9.1.9"),sQuery(id+"F0.wireOp",EDGE,"E3.9.1.10"),sQuery(id+"F0.wireOp",EDGE,"E3.9.1.11"),sQuery(id+"F0.wireOp",EDGE,"E3.9.1.12"),sQuery(id+"F0.wireOp",EDGE,"E3.9.1.13"),sQuery(id+"F0.wireOp",EDGE,"E3.9.1.14"),sQuery(id+"F0.wireOp",EDGE,"E3.9.1.15"),sQuery(id+"F0.wireOp",EDGE,"E3.9.2.4"),sQuery(id+"F0.wireOp",EDGE,"E3.9.2.5"),sQuery(id+"F0.wireOp",EDGE,"E3.9.2.6"),sQuery(id+"F0.wireOp",EDGE,"E3.9.2.7"),sQuery(id+"F0.wireOp",EDGE,"E3.9.2.8"),sQuery(id+"F0.wireOp",EDGE,"E3.9.2.9"),sQuery(id+"F0.wireOp",EDGE,"E3.9.2.10"),sQuery(id+"F0.wireOp",EDGE,"E3.9.2.11"),sQuery(id+"F0.wireOp",EDGE,"E3.9.2.12"),sQuery(id+"F0.wireOp",EDGE,"E3.9.2.13"),sQuery(id+"F0.wireOp",EDGE,"E3.9.2.14"),sQuery(id+"F0.wireOp",EDGE,"E3.9.2.15"),sQuery(id+"F0.wireOp",EDGE,"E3.9.3.4"),sQuery(id+"F0.wireOp",EDGE,"E3.9.3.5"),sQuery(id+"F0.wireOp",EDGE,"E3.9.3.6"),sQuery(id+"F0.wireOp",EDGE,"E3.9.3.7"),sQuery(id+"F0.wireOp",EDGE,"E3.9.3.8"),sQuery(id+"F0.wireOp",EDGE,"E3.9.3.9"),sQuery(id+"F0.wireOp",EDGE,"E3.9.3.10"),sQuery(id+"F0.wireOp",EDGE,"E3.9.3.11"),sQuery(id+"F0.wireOp",EDGE,"E3.9.3.12"),sQuery(id+"F0.wireOp",EDGE,"E3.9.3.13"),sQuery(id+"F0.wireOp",EDGE,"E3.9.3.14"),sQuery(id+"F0.wireOp",EDGE,"E3.9.3.15"),sQuery(id+"F0.wireOp",EDGE,"E3.9.4.4"),sQuery(id+"F0.wireOp",EDGE,"E3.9.4.5"),sQuery(id+"F0.wireOp",EDGE,"E3.9.4.6"),sQuery(id+"F0.wireOp",EDGE,"E3.9.4.7"),sQuery(id+"F0.wireOp",EDGE,"E3.9.4.8"),sQuery(id+"F0.wireOp",EDGE,"E3.9.4.9"),sQuery(id+"F0.wireOp",EDGE,"E3.9.4.10"),sQuery(id+"F0.wireOp",EDGE,"E3.9.4.11"),sQuery(id+"F0.wireOp",EDGE,"E3.9.4.12"),sQuery(id+"F0.wireOp",EDGE,"E3.9.4.13"),sQuery(id+"F0.wireOp",EDGE,"E3.9.4.14"),sQuery(id+"F0.wireOp",EDGE,"E3.9.4.15"),sQuery(id+"F0.wireOp",EDGE,"E3.9.5.4"),sQuery(id+"F0.wireOp",EDGE,"E3.9.5.5"),sQuery(id+"F0.wireOp",EDGE,"E3.9.5.6"),sQuery(id+"F0.wireOp",EDGE,"E3.9.5.7"),sQuery(id+"F0.wireOp",EDGE,"E3.9.5.8"),sQuery(id+"F0.wireOp",EDGE,"E3.9.5.9"),sQuery(id+"F0.wireOp",EDGE,"E3.9.5.10"),sQuery(id+"F0.wireOp",EDGE,"E3.9.5.11"),sQuery(id+"F0.wireOp",EDGE,"E3.9.5.12"),sQuery(id+"F0.wireOp",EDGE,"E3.9.5.13"),sQuery(id+"F0.wireOp",EDGE,"E3.9.5.14"),sQuery(id+"F0.wireOp",EDGE,"E3.9.5.15"),sQuery(id+"F0.wireOp",EDGE,"E3.9.6.4"),sQuery(id+"F0.wireOp",EDGE,"E3.9.6.5"),sQuery(id+"F0.wireOp",EDGE,"E3.9.6.6"),sQuery(id+"F0.wireOp",EDGE,"E3.9.6.7"),sQuery(id+"F0.wireOp",EDGE,"E3.9.6.8"),sQuery(id+"F0.wireOp",EDGE,"E3.9.6.9"),sQuery(id+"F0.wireOp",EDGE,"E3.9.6.10"),sQuery(id+"F0.wireOp",EDGE,"E3.9.6.11"),sQuery(id+"F0.wireOp",EDGE,"E3.9.6.12"),sQuery(id+"F0.wireOp",EDGE,"E3.9.6.13"),sQuery(id+"F0.wireOp",EDGE,"E3.9.6.14"),sQuery(id+"F0.wireOp",EDGE,"E3.9.6.15"),sQuery(id+"F0.wireOp",EDGE,"E3.9.7.4"),sQuery(id+"F0.wireOp",EDGE,"E3.9.7.5"),sQuery(id+"F0.wireOp",EDGE,"E3.9.7.6"),sQuery(id+"F0.wireOp",EDGE,"E3.9.7.7"),sQuery(id+"F0.wireOp",EDGE,"E3.9.7.8"),sQuery(id+"F0.wireOp",EDGE,"E3.9.7.9"),sQuery(id+"F0.wireOp",EDGE,"E3.9.7.10"),sQuery(id+"F0.wireOp",EDGE,"E3.9.7.11"),sQuery(id+"F0.wireOp",EDGE,"E3.9.7.12"),sQuery(id+"F0.wireOp",EDGE,"E3.9.7.13"),sQuery(id+"F0.wireOp",EDGE,"E3.9.7.14"),sQuery(id+"F0.wireOp",EDGE,"E3.9.7.15"),sQuery(id+"F0.wireOp",EDGE,"E3.9.8.4"),sQuery(id+"F0.wireOp",EDGE,"E3.9.8.5"),sQuery(id+"F0.wireOp",EDGE,"E3.9.8.6"),sQuery(id+"F0.wireOp",EDGE,"E3.9.8.7"),sQuery(id+"F0.wireOp",EDGE,"E3.9.8.8"),sQuery(id+"F0.wireOp",EDGE,"E3.9.8.9"),sQuery(id+"F0.wireOp",EDGE,"E3.9.8.10"),sQuery(id+"F0.wireOp",EDGE,"E3.9.8.11"),sQuery(id+"F0.wireOp",EDGE,"E3.9.8.12"),sQuery(id+"F0.wireOp",EDGE,"E3.9.8.13"),sQuery(id+"F0.wireOp",EDGE,"E3.9.8.14"),sQuery(id+"F0.wireOp",EDGE,"E3.9.8.15"),sQuery(id+"F0.wireOp",EDGE,"E3.9.9.4"),sQuery(id+"F0.wireOp",EDGE,"E3.9.9.5"),sQuery(id+"F0.wireOp",EDGE,"E3.9.9.6"),sQuery(id+"F0.wireOp",EDGE,"E3.9.9.7"),sQuery(id+"F0.wireOp",EDGE,"E3.9.9.8"),sQuery(id+"F0.wireOp",EDGE,"E3.9.9.9"),sQuery(id+"F0.wireOp",EDGE,"E3.9.9.10"),sQuery(id+"F0.wireOp",EDGE,"E3.9.9.11"),sQuery(id+"F0.wireOp",EDGE,"E3.9.9.12"),sQuery(id+"F0.wireOp",EDGE,"E3.9.9.13"),sQuery(id+"F0.wireOp",EDGE,"E3.9.9.14"),sQuery(id+"F0.wireOp",EDGE,"E3.9.9.15"),sQuery(id+"F0.wireOp",EDGE,"E4.6.10.0"),sQuery(id+"F0.wireOp",EDGE,"E4.9.10.0"),sQuery(id+"F0.wireOp",EDGE,"E4.12.10.0"),sQuery(id+"F0.wireOp",EDGE,"E4.15.10.0"),sQuery(id+"F0.wireOp",EDGE,"E4.18.10.0"),sQuery(id+"F0.wireOp",EDGE,"E4.21.10.0"),sQuery(id+"F0.wireOp",EDGE,"E4.24.10.0"),sQuery(id+"F0.wireOp",EDGE,"E4.27.10.0"),sQuery(id+"F0.wireOp",EDGE,"E4.30.10.0"),sQuery(id+"F0.wireOp",EDGE,"E4.33.10.0"),sQuery(id+"F0.wireOp",EDGE,"E4.36.10.0"),sQuery(id+"F0.wireOp",EDGE,"E4.39.10.0"),sQuery(id+"F0.wireOp",EDGE,"E4.6.10.1"),sQuery(id+"F0.wireOp",EDGE,"E4.9.10.1"),sQuery(id+"F0.wireOp",EDGE,"E4.12.10.1"),sQuery(id+"F0.wireOp",EDGE,"E4.15.10.1"),sQuery(id+"F0.wireOp",EDGE,"E4.18.10.1"),sQuery(id+"F0.wireOp",EDGE,"E4.21.10.1"),sQuery(id+"F0.wireOp",EDGE,"E4.24.10.1"),sQuery(id+"F0.wireOp",EDGE,"E4.27.10.1"),sQuery(id+"F0.wireOp",EDGE,"E4.30.10.1"),sQuery(id+"F0.wireOp",EDGE,"E4.33.10.1"),sQuery(id+"F0.wireOp",EDGE,"E4.36.10.1"),sQuery(id+"F0.wireOp",EDGE,"E4.39.10.1"),sQuery(id+"F0.wireOp",EDGE,"E4.6.10.2"),sQuery(id+"F0.wireOp",EDGE,"E4.9.10.2"),sQuery(id+"F0.wireOp",EDGE,"E4.12.10.2"),sQuery(id+"F0.wireOp",EDGE,"E4.15.10.2"),sQuery(id+"F0.wireOp",EDGE,"E4.18.10.2"),sQuery(id+"F0.wireOp",EDGE,"E4.21.10.2"),sQuery(id+"F0.wireOp",EDGE,"E4.24.10.2"),sQuery(id+"F0.wireOp",EDGE,"E4.27.10.2"),sQuery(id+"F0.wireOp",EDGE,"E4.30.10.2"),sQuery(id+"F0.wireOp",EDGE,"E4.33.10.2"),sQuery(id+"F0.wireOp",EDGE,"E4.36.10.2"),sQuery(id+"F0.wireOp",EDGE,"E4.39.10.2"),sQuery(id+"F0.wireOp",EDGE,"E4.6.10.3"),sQuery(id+"F0.wireOp",EDGE,"E4.9.10.3"),sQuery(id+"F0.wireOp",EDGE,"E4.12.10.3"),sQuery(id+"F0.wireOp",EDGE,"E4.15.10.3"),sQuery(id+"F0.wireOp",EDGE,"E4.18.10.3"),sQuery(id+"F0.wireOp",EDGE,"E4.21.10.3"),sQuery(id+"F0.wireOp",EDGE,"E4.24.10.3"),sQuery(id+"F0.wireOp",EDGE,"E4.27.10.3"),sQuery(id+"F0.wireOp",EDGE,"E4.30.10.3"),sQuery(id+"F0.wireOp",EDGE,"E4.33.10.3"),sQuery(id+"F0.wireOp",EDGE,"E4.36.10.3"),sQuery(id+"F0.wireOp",EDGE,"E4.39.10.3"),sQuery(id+"F0.wireOp",EDGE,"E4.6.10.4"),sQuery(id+"F0.wireOp",EDGE,"E4.9.10.4"),sQuery(id+"F0.wireOp",EDGE,"E4.12.10.4"),sQuery(id+"F0.wireOp",EDGE,"E4.15.10.4"),sQuery(id+"F0.wireOp",EDGE,"E4.18.10.4"),sQuery(id+"F0.wireOp",EDGE,"E4.21.10.4"),sQuery(id+"F0.wireOp",EDGE,"E4.24.10.4"),sQuery(id+"F0.wireOp",EDGE,"E4.27.10.4"),sQuery(id+"F0.wireOp",EDGE,"E4.30.10.4"),sQuery(id+"F0.wireOp",EDGE,"E4.33.10.4"),sQuery(id+"F0.wireOp",EDGE,"E4.36.10.4"),sQuery(id+"F0.wireOp",EDGE,"E4.39.10.4"),sQuery(id+"F0.wireOp",EDGE,"E4.6.10.5"),sQuery(id+"F0.wireOp",EDGE,"E4.9.10.5"),sQuery(id+"F0.wireOp",EDGE,"E4.12.10.5"),sQuery(id+"F0.wireOp",EDGE,"E4.15.10.5"),sQuery(id+"F0.wireOp",EDGE,"E4.18.10.5"),sQuery(id+"F0.wireOp",EDGE,"E4.21.10.5"),sQuery(id+"F0.wireOp",EDGE,"E4.24.10.5"),sQuery(id+"F0.wireOp",EDGE,"E4.27.10.5"),sQuery(id+"F0.wireOp",EDGE,"E4.30.10.5"),sQuery(id+"F0.wireOp",EDGE,"E4.33.10.5"),sQuery(id+"F0.wireOp",EDGE,"E4.36.10.5"),sQuery(id+"F0.wireOp",EDGE,"E4.39.10.5"),sQuery(id+"F0.wireOp",EDGE,"E4.6.10.6"),sQuery(id+"F0.wireOp",EDGE,"E4.9.10.6"),sQuery(id+"F0.wireOp",EDGE,"E4.12.10.6"),sQuery(id+"F0.wireOp",EDGE,"E4.15.10.6"),sQuery(id+"F0.wireOp",EDGE,"E4.18.10.6"),sQuery(id+"F0.wireOp",EDGE,"E4.21.10.6"),sQuery(id+"F0.wireOp",EDGE,"E4.24.10.6"),sQuery(id+"F0.wireOp",EDGE,"E4.27.10.6"),sQuery(id+"F0.wireOp",EDGE,"E4.30.10.6"),sQuery(id+"F0.wireOp",EDGE,"E4.33.10.6"),sQuery(id+"F0.wireOp",EDGE,"E4.36.10.6"),sQuery(id+"F0.wireOp",EDGE,"E4.39.10.6"),sQuery(id+"F0.wireOp",EDGE,"E4.6.10.7"),sQuery(id+"F0.wireOp",EDGE,"E4.9.10.7"),sQuery(id+"F0.wireOp",EDGE,"E4.12.10.7"),sQuery(id+"F0.wireOp",EDGE,"E4.15.10.7"),sQuery(id+"F0.wireOp",EDGE,"E4.18.10.7"),sQuery(id+"F0.wireOp",EDGE,"E4.21.10.7"),sQuery(id+"F0.wireOp",EDGE,"E4.24.10.7"),sQuery(id+"F0.wireOp",EDGE,"E4.27.10.7"),sQuery(id+"F0.wireOp",EDGE,"E4.30.10.7"),sQuery(id+"F0.wireOp",EDGE,"E4.33.10.7"),sQuery(id+"F0.wireOp",EDGE,"E4.36.10.7"),sQuery(id+"F0.wireOp",EDGE,"E4.39.10.7"),sQuery(id+"F0.wireOp",EDGE,"E4.6.10.8"),sQuery(id+"F0.wireOp",EDGE,"E4.9.10.8"),sQuery(id+"F0.wireOp",EDGE,"E4.12.10.8"),sQuery(id+"F0.wireOp",EDGE,"E4.15.10.8"),sQuery(id+"F0.wireOp",EDGE,"E4.18.10.8"),sQuery(id+"F0.wireOp",EDGE,"E4.21.10.8"),sQuery(id+"F0.wireOp",EDGE,"E4.24.10.8"),sQuery(id+"F0.wireOp",EDGE,"E4.27.10.8"),sQuery(id+"F0.wireOp",EDGE,"E4.30.10.8"),sQuery(id+"F0.wireOp",EDGE,"E4.33.10.8"),sQuery(id+"F0.wireOp",EDGE,"E4.36.10.8"),sQuery(id+"F0.wireOp",EDGE,"E4.39.10.8"),sQuery(id+"F0.wireOp",EDGE,"E4.6.10.9"),sQuery(id+"F0.wireOp",EDGE,"E4.9.10.9"),sQuery(id+"F0.wireOp",EDGE,"E4.12.10.9"),sQuery(id+"F0.wireOp",EDGE,"E4.15.10.9"),sQuery(id+"F0.wireOp",EDGE,"E4.18.10.9"),sQuery(id+"F0.wireOp",EDGE,"E4.21.10.9"),sQuery(id+"F0.wireOp",EDGE,"E4.24.10.9"),sQuery(id+"F0.wireOp",EDGE,"E4.27.10.9"),sQuery(id+"F0.wireOp",EDGE,"E4.30.10.9"),sQuery(id+"F0.wireOp",EDGE,"E4.33.10.9"),sQuery(id+"F0.wireOp",EDGE,"E4.36.10.9"),sQuery(id+"F0.wireOp",EDGE,"E4.39.10.9"),sQuery(id+"F0.wireOp",EDGE,"E4.6.11.0"),sQuery(id+"F0.wireOp",EDGE,"E4.9.11.0"),sQuery(id+"F0.wireOp",EDGE,"E4.12.11.0"),sQuery(id+"F0.wireOp",EDGE,"E4.15.11.0"),sQuery(id+"F0.wireOp",EDGE,"E4.18.11.0"),sQuery(id+"F0.wireOp",EDGE,"E4.21.11.0"),sQuery(id+"F0.wireOp",EDGE,"E4.24.11.0"),sQuery(id+"F0.wireOp",EDGE,"E4.27.11.0"),sQuery(id+"F0.wireOp",EDGE,"E4.30.11.0"),sQuery(id+"F0.wireOp",EDGE,"E4.33.11.0"),sQuery(id+"F0.wireOp",EDGE,"E4.36.11.0"),sQuery(id+"F0.wireOp",EDGE,"E4.39.11.0"),sQuery(id+"F0.wireOp",EDGE,"E4.6.11.1"),sQuery(id+"F0.wireOp",EDGE,"E4.9.11.1"),sQuery(id+"F0.wireOp",EDGE,"E4.12.11.1"),sQuery(id+"F0.wireOp",EDGE,"E4.15.11.1"),sQuery(id+"F0.wireOp",EDGE,"E4.18.11.1"),sQuery(id+"F0.wireOp",EDGE,"E4.21.11.1"),sQuery(id+"F0.wireOp",EDGE,"E4.24.11.1"),sQuery(id+"F0.wireOp",EDGE,"E4.27.11.1"),sQuery(id+"F0.wireOp",EDGE,"E4.30.11.1"),sQuery(id+"F0.wireOp",EDGE,"E4.33.11.1"),sQuery(id+"F0.wireOp",EDGE,"E4.36.11.1"),sQuery(id+"F0.wireOp",EDGE,"E4.39.11.1"),sQuery(id+"F0.wireOp",EDGE,"E4.6.11.2"),sQuery(id+"F0.wireOp",EDGE,"E4.9.11.2"),sQuery(id+"F0.wireOp",EDGE,"E4.12.11.2"),sQuery(id+"F0.wireOp",EDGE,"E4.15.11.2"),sQuery(id+"F0.wireOp",EDGE,"E4.18.11.2"),sQuery(id+"F0.wireOp",EDGE,"E4.21.11.2"),sQuery(id+"F0.wireOp",EDGE,"E4.24.11.2"),sQuery(id+"F0.wireOp",EDGE,"E4.27.11.2"),sQuery(id+"F0.wireOp",EDGE,"E4.30.11.2"),sQuery(id+"F0.wireOp",EDGE,"E4.33.11.2"),sQuery(id+"F0.wireOp",EDGE,"E4.36.11.2"),sQuery(id+"F0.wireOp",EDGE,"E4.39.11.2"),sQuery(id+"F0.wireOp",EDGE,"E4.6.11.3"),sQuery(id+"F0.wireOp",EDGE,"E4.9.11.3"),sQuery(id+"F0.wireOp",EDGE,"E4.12.11.3"),sQuery(id+"F0.wireOp",EDGE,"E4.15.11.3"),sQuery(id+"F0.wireOp",EDGE,"E4.18.11.3"),sQuery(id+"F0.wireOp",EDGE,"E4.21.11.3"),sQuery(id+"F0.wireOp",EDGE,"E4.24.11.3"),sQuery(id+"F0.wireOp",EDGE,"E4.27.11.3"),sQuery(id+"F0.wireOp",EDGE,"E4.30.11.3"),sQuery(id+"F0.wireOp",EDGE,"E4.33.11.3"),sQuery(id+"F0.wireOp",EDGE,"E4.36.11.3"),sQuery(id+"F0.wireOp",EDGE,"E4.39.11.3"),sQuery(id+"F0.wireOp",EDGE,"E4.6.11.4"),sQuery(id+"F0.wireOp",EDGE,"E4.9.11.4"),sQuery(id+"F0.wireOp",EDGE,"E4.12.11.4"),sQuery(id+"F0.wireOp",EDGE,"E4.15.11.4"),sQuery(id+"F0.wireOp",EDGE,"E4.18.11.4"),sQuery(id+"F0.wireOp",EDGE,"E4.21.11.4"),sQuery(id+"F0.wireOp",EDGE,"E4.24.11.4"),sQuery(id+"F0.wireOp",EDGE,"E4.27.11.4"),sQuery(id+"F0.wireOp",EDGE,"E4.30.11.4"),sQuery(id+"F0.wireOp",EDGE,"E4.33.11.4"),sQuery(id+"F0.wireOp",EDGE,"E4.36.11.4"),sQuery(id+"F0.wireOp",EDGE,"E4.39.11.4"),sQuery(id+"F0.wireOp",EDGE,"E4.6.11.5"),sQuery(id+"F0.wireOp",EDGE,"E4.9.11.5"),sQuery(id+"F0.wireOp",EDGE,"E4.12.11.5"),sQuery(id+"F0.wireOp",EDGE,"E4.15.11.5"),sQuery(id+"F0.wireOp",EDGE,"E4.18.11.5"),sQuery(id+"F0.wireOp",EDGE,"E4.21.11.5"),sQuery(id+"F0.wireOp",EDGE,"E4.24.11.5"),sQuery(id+"F0.wireOp",EDGE,"E4.27.11.5"),sQuery(id+"F0.wireOp",EDGE,"E4.30.11.5"),sQuery(id+"F0.wireOp",EDGE,"E4.33.11.5"),sQuery(id+"F0.wireOp",EDGE,"E4.36.11.5"),sQuery(id+"F0.wireOp",EDGE,"E4.39.11.5"),sQuery(id+"F0.wireOp",EDGE,"E4.6.11.6"),sQuery(id+"F0.wireOp",EDGE,"E4.9.11.6"),sQuery(id+"F0.wireOp",EDGE,"E4.12.11.6"),sQuery(id+"F0.wireOp",EDGE,"E4.15.11.6"),sQuery(id+"F0.wireOp",EDGE,"E4.18.11.6"),sQuery(id+"F0.wireOp",EDGE,"E4.21.11.6"),sQuery(id+"F0.wireOp",EDGE,"E4.24.11.6"),sQuery(id+"F0.wireOp",EDGE,"E4.27.11.6"),sQuery(id+"F0.wireOp",EDGE,"E4.30.11.6"),sQuery(id+"F0.wireOp",EDGE,"E4.33.11.6"),sQuery(id+"F0.wireOp",EDGE,"E4.36.11.6"),sQuery(id+"F0.wireOp",EDGE,"E4.39.11.6"),sQuery(id+"F0.wireOp",EDGE,"E4.6.11.7"),sQuery(id+"F0.wireOp",EDGE,"E4.9.11.7"),sQuery(id+"F0.wireOp",EDGE,"E4.12.11.7"),sQuery(id+"F0.wireOp",EDGE,"E4.15.11.7"),sQuery(id+"F0.wireOp",EDGE,"E4.18.11.7"),sQuery(id+"F0.wireOp",EDGE,"E4.21.11.7"),sQuery(id+"F0.wireOp",EDGE,"E4.24.11.7"),sQuery(id+"F0.wireOp",EDGE,"E4.27.11.7"),sQuery(id+"F0.wireOp",EDGE,"E4.30.11.7"),sQuery(id+"F0.wireOp",EDGE,"E4.33.11.7"),sQuery(id+"F0.wireOp",EDGE,"E4.36.11.7"),sQuery(id+"F0.wireOp",EDGE,"E4.39.11.7"),sQuery(id+"F0.wireOp",EDGE,"E4.6.11.8"),sQuery(id+"F0.wireOp",EDGE,"E4.9.11.8"),sQuery(id+"F0.wireOp",EDGE,"E4.12.11.8"),sQuery(id+"F0.wireOp",EDGE,"E4.15.11.8"),sQuery(id+"F0.wireOp",EDGE,"E4.18.11.8"),sQuery(id+"F0.wireOp",EDGE,"E4.21.11.8"),sQuery(id+"F0.wireOp",EDGE,"E4.24.11.8"),sQuery(id+"F0.wireOp",EDGE,"E4.27.11.8"),sQuery(id+"F0.wireOp",EDGE,"E4.30.11.8"),sQuery(id+"F0.wireOp",EDGE,"E4.33.11.8"),sQuery(id+"F0.wireOp",EDGE,"E4.36.11.8"),sQuery(id+"F0.wireOp",EDGE,"E4.39.11.8"),sQuery(id+"F0.wireOp",EDGE,"E4.6.11.9"),sQuery(id+"F0.wireOp",EDGE,"E4.9.11.9"),sQuery(id+"F0.wireOp",EDGE,"E4.12.11.9"),sQuery(id+"F0.wireOp",EDGE,"E4.15.11.9"),sQuery(id+"F0.wireOp",EDGE,"E4.18.11.9"),sQuery(id+"F0.wireOp",EDGE,"E4.21.11.9"),sQuery(id+"F0.wireOp",EDGE,"E4.24.11.9"),sQuery(id+"F0.wireOp",EDGE,"E4.27.11.9"),sQuery(id+"F0.wireOp",EDGE,"E4.30.11.9"),sQuery(id+"F0.wireOp",EDGE,"E4.33.11.9"),sQuery(id+"F0.wireOp",EDGE,"E4.36.11.9"),sQuery(id+"F0.wireOp",EDGE,"E4.39.11.9"),sQuery(id+"F0.wireOp",EDGE,"E4.6.12.0"),sQuery(id+"F0.wireOp",EDGE,"E4.9.12.0"),sQuery(id+"F0.wireOp",EDGE,"E4.12.12.0"),sQuery(id+"F0.wireOp",EDGE,"E4.15.12.0"),sQuery(id+"F0.wireOp",EDGE,"E4.18.12.0"),sQuery(id+"F0.wireOp",EDGE,"E4.21.12.0"),sQuery(id+"F0.wireOp",EDGE,"E4.24.12.0"),sQuery(id+"F0.wireOp",EDGE,"E4.27.12.0"),sQuery(id+"F0.wireOp",EDGE,"E4.30.12.0"),sQuery(id+"F0.wireOp",EDGE,"E4.33.12.0"),sQuery(id+"F0.wireOp",EDGE,"E4.36.12.0"),sQuery(id+"F0.wireOp",EDGE,"E4.39.12.0"),sQuery(id+"F0.wireOp",EDGE,"E4.6.12.1"),sQuery(id+"F0.wireOp",EDGE,"E4.9.12.1"),sQuery(id+"F0.wireOp",EDGE,"E4.12.12.1"),sQuery(id+"F0.wireOp",EDGE,"E4.15.12.1"),sQuery(id+"F0.wireOp",EDGE,"E4.18.12.1"),sQuery(id+"F0.wireOp",EDGE,"E4.21.12.1"),sQuery(id+"F0.wireOp",EDGE,"E4.24.12.1"),sQuery(id+"F0.wireOp",EDGE,"E4.27.12.1"),sQuery(id+"F0.wireOp",EDGE,"E4.30.12.1"),sQuery(id+"F0.wireOp",EDGE,"E4.33.12.1"),sQuery(id+"F0.wireOp",EDGE,"E4.36.12.1"),sQuery(id+"F0.wireOp",EDGE,"E4.39.12.1"),sQuery(id+"F0.wireOp",EDGE,"E4.6.12.2"),sQuery(id+"F0.wireOp",EDGE,"E4.9.12.2"),sQuery(id+"F0.wireOp",EDGE,"E4.12.12.2"),sQuery(id+"F0.wireOp",EDGE,"E4.15.12.2"),sQuery(id+"F0.wireOp",EDGE,"E4.18.12.2"),sQuery(id+"F0.wireOp",EDGE,"E4.21.12.2"),sQuery(id+"F0.wireOp",EDGE,"E4.24.12.2"),sQuery(id+"F0.wireOp",EDGE,"E4.27.12.2"),sQuery(id+"F0.wireOp",EDGE,"E4.30.12.2"),sQuery(id+"F0.wireOp",EDGE,"E4.33.12.2"),sQuery(id+"F0.wireOp",EDGE,"E4.36.12.2"),sQuery(id+"F0.wireOp",EDGE,"E4.39.12.2"),sQuery(id+"F0.wireOp",EDGE,"E4.6.12.3"),sQuery(id+"F0.wireOp",EDGE,"E4.9.12.3"),sQuery(id+"F0.wireOp",EDGE,"E4.12.12.3"),sQuery(id+"F0.wireOp",EDGE,"E4.15.12.3"),sQuery(id+"F0.wireOp",EDGE,"E4.18.12.3"),sQuery(id+"F0.wireOp",EDGE,"E4.21.12.3"),sQuery(id+"F0.wireOp",EDGE,"E4.24.12.3"),sQuery(id+"F0.wireOp",EDGE,"E4.27.12.3"),sQuery(id+"F0.wireOp",EDGE,"E4.30.12.3"),sQuery(id+"F0.wireOp",EDGE,"E4.33.12.3"),sQuery(id+"F0.wireOp",EDGE,"E4.36.12.3"),sQuery(id+"F0.wireOp",EDGE,"E4.39.12.3"),sQuery(id+"F0.wireOp",EDGE,"E4.6.12.4"),sQuery(id+"F0.wireOp",EDGE,"E4.9.12.4"),sQuery(id+"F0.wireOp",EDGE,"E4.12.12.4"),sQuery(id+"F0.wireOp",EDGE,"E4.15.12.4"),sQuery(id+"F0.wireOp",EDGE,"E4.18.12.4"),sQuery(id+"F0.wireOp",EDGE,"E4.21.12.4"),sQuery(id+"F0.wireOp",EDGE,"E4.24.12.4"),sQuery(id+"F0.wireOp",EDGE,"E4.27.12.4"),sQuery(id+"F0.wireOp",EDGE,"E4.30.12.4"),sQuery(id+"F0.wireOp",EDGE,"E4.33.12.4"),sQuery(id+"F0.wireOp",EDGE,"E4.36.12.4"),sQuery(id+"F0.wireOp",EDGE,"E4.39.12.4"),sQuery(id+"F0.wireOp",EDGE,"E4.6.12.5"),sQuery(id+"F0.wireOp",EDGE,"E4.9.12.5"),sQuery(id+"F0.wireOp",EDGE,"E4.12.12.5"),sQuery(id+"F0.wireOp",EDGE,"E4.15.12.5"),sQuery(id+"F0.wireOp",EDGE,"E4.18.12.5"),sQuery(id+"F0.wireOp",EDGE,"E4.21.12.5"),sQuery(id+"F0.wireOp",EDGE,"E4.24.12.5"),sQuery(id+"F0.wireOp",EDGE,"E4.27.12.5"),sQuery(id+"F0.wireOp",EDGE,"E4.30.12.5"),sQuery(id+"F0.wireOp",EDGE,"E4.33.12.5"),sQuery(id+"F0.wireOp",EDGE,"E4.36.12.5"),sQuery(id+"F0.wireOp",EDGE,"E4.39.12.5"),sQuery(id+"F0.wireOp",EDGE,"E4.6.12.6"),sQuery(id+"F0.wireOp",EDGE,"E4.9.12.6"),sQuery(id+"F0.wireOp",EDGE,"E4.12.12.6"),sQuery(id+"F0.wireOp",EDGE,"E4.15.12.6"),sQuery(id+"F0.wireOp",EDGE,"E4.18.12.6"),sQuery(id+"F0.wireOp",EDGE,"E4.21.12.6"),sQuery(id+"F0.wireOp",EDGE,"E4.24.12.6"),sQuery(id+"F0.wireOp",EDGE,"E4.27.12.6"),sQuery(id+"F0.wireOp",EDGE,"E4.30.12.6"),sQuery(id+"F0.wireOp",EDGE,"E4.33.12.6"),sQuery(id+"F0.wireOp",EDGE,"E4.36.12.6"),sQuery(id+"F0.wireOp",EDGE,"E4.39.12.6"),sQuery(id+"F0.wireOp",EDGE,"E4.6.12.7"),sQuery(id+"F0.wireOp",EDGE,"E4.9.12.7"),sQuery(id+"F0.wireOp",EDGE,"E4.12.12.7"),sQuery(id+"F0.wireOp",EDGE,"E4.15.12.7"),sQuery(id+"F0.wireOp",EDGE,"E4.18.12.7"),sQuery(id+"F0.wireOp",EDGE,"E4.21.12.7"),sQuery(id+"F0.wireOp",EDGE,"E4.24.12.7"),sQuery(id+"F0.wireOp",EDGE,"E4.27.12.7"),sQuery(id+"F0.wireOp",EDGE,"E4.30.12.7"),sQuery(id+"F0.wireOp",EDGE,"E4.33.12.7"),sQuery(id+"F0.wireOp",EDGE,"E4.36.12.7"),sQuery(id+"F0.wireOp",EDGE,"E4.39.12.7"),sQuery(id+"F0.wireOp",EDGE,"E4.6.12.8"),sQuery(id+"F0.wireOp",EDGE,"E4.9.12.8"),sQuery(id+"F0.wireOp",EDGE,"E4.12.12.8"),sQuery(id+"F0.wireOp",EDGE,"E4.15.12.8"),sQuery(id+"F0.wireOp",EDGE,"E4.18.12.8"),sQuery(id+"F0.wireOp",EDGE,"E4.21.12.8"),sQuery(id+"F0.wireOp",EDGE,"E4.24.12.8"),sQuery(id+"F0.wireOp",EDGE,"E4.27.12.8"),sQuery(id+"F0.wireOp",EDGE,"E4.30.12.8"),sQuery(id+"F0.wireOp",EDGE,"E4.33.12.8"),sQuery(id+"F0.wireOp",EDGE,"E4.36.12.8"),sQuery(id+"F0.wireOp",EDGE,"E4.39.12.8"),sQuery(id+"F0.wireOp",EDGE,"E4.6.12.9"),sQuery(id+"F0.wireOp",EDGE,"E4.9.12.9"),sQuery(id+"F0.wireOp",EDGE,"E4.12.12.9"),sQuery(id+"F0.wireOp",EDGE,"E4.15.12.9"),sQuery(id+"F0.wireOp",EDGE,"E4.18.12.9"),sQuery(id+"F0.wireOp",EDGE,"E4.21.12.9"),sQuery(id+"F0.wireOp",EDGE,"E4.24.12.9"),sQuery(id+"F0.wireOp",EDGE,"E4.27.12.9"),sQuery(id+"F0.wireOp",EDGE,"E4.30.12.9"),sQuery(id+"F0.wireOp",EDGE,"E4.33.12.9"),sQuery(id+"F0.wireOp",EDGE,"E4.36.12.9"),sQuery(id+"F0.wireOp",EDGE,"E4.39.12.9"),sQuery(id+"F0.wireOp",EDGE,"E4.6.13.0"),sQuery(id+"F0.wireOp",EDGE,"E4.9.13.0"),sQuery(id+"F0.wireOp",EDGE,"E4.12.13.0"),sQuery(id+"F0.wireOp",EDGE,"E4.15.13.0"),sQuery(id+"F0.wireOp",EDGE,"E4.18.13.0"),sQuery(id+"F0.wireOp",EDGE,"E4.21.13.0"),sQuery(id+"F0.wireOp",EDGE,"E4.24.13.0"),sQuery(id+"F0.wireOp",EDGE,"E4.27.13.0"),sQuery(id+"F0.wireOp",EDGE,"E4.30.13.0"),sQuery(id+"F0.wireOp",EDGE,"E4.33.13.0"),sQuery(id+"F0.wireOp",EDGE,"E4.36.13.0"),sQuery(id+"F0.wireOp",EDGE,"E4.39.13.0"),sQuery(id+"F0.wireOp",EDGE,"E4.6.13.1"),sQuery(id+"F0.wireOp",EDGE,"E4.9.13.1"),sQuery(id+"F0.wireOp",EDGE,"E4.12.13.1"),sQuery(id+"F0.wireOp",EDGE,"E4.15.13.1"),sQuery(id+"F0.wireOp",EDGE,"E4.18.13.1"),sQuery(id+"F0.wireOp",EDGE,"E4.21.13.1"),sQuery(id+"F0.wireOp",EDGE,"E4.24.13.1"),sQuery(id+"F0.wireOp",EDGE,"E4.27.13.1"),sQuery(id+"F0.wireOp",EDGE,"E4.30.13.1"),sQuery(id+"F0.wireOp",EDGE,"E4.33.13.1"),sQuery(id+"F0.wireOp",EDGE,"E4.36.13.1"),sQuery(id+"F0.wireOp",EDGE,"E4.39.13.1"),sQuery(id+"F0.wireOp",EDGE,"E4.6.13.2"),sQuery(id+"F0.wireOp",EDGE,"E4.9.13.2"),sQuery(id+"F0.wireOp",EDGE,"E4.12.13.2"),sQuery(id+"F0.wireOp",EDGE,"E4.15.13.2"),sQuery(id+"F0.wireOp",EDGE,"E4.18.13.2"),sQuery(id+"F0.wireOp",EDGE,"E4.21.13.2"),sQuery(id+"F0.wireOp",EDGE,"E4.24.13.2"),sQuery(id+"F0.wireOp",EDGE,"E4.27.13.2"),sQuery(id+"F0.wireOp",EDGE,"E4.30.13.2"),sQuery(id+"F0.wireOp",EDGE,"E4.33.13.2"),sQuery(id+"F0.wireOp",EDGE,"E4.36.13.2"),sQuery(id+"F0.wireOp",EDGE,"E4.39.13.2"),sQuery(id+"F0.wireOp",EDGE,"E4.6.13.3"),sQuery(id+"F0.wireOp",EDGE,"E4.9.13.3"),sQuery(id+"F0.wireOp",EDGE,"E4.12.13.3"),sQuery(id+"F0.wireOp",EDGE,"E4.15.13.3"),sQuery(id+"F0.wireOp",EDGE,"E4.18.13.3"),sQuery(id+"F0.wireOp",EDGE,"E4.21.13.3"),sQuery(id+"F0.wireOp",EDGE,"E4.24.13.3"),sQuery(id+"F0.wireOp",EDGE,"E4.27.13.3"),sQuery(id+"F0.wireOp",EDGE,"E4.30.13.3"),sQuery(id+"F0.wireOp",EDGE,"E4.33.13.3"),sQuery(id+"F0.wireOp",EDGE,"E4.36.13.3"),sQuery(id+"F0.wireOp",EDGE,"E4.39.13.3"),sQuery(id+"F0.wireOp",EDGE,"E4.6.13.4"),sQuery(id+"F0.wireOp",EDGE,"E4.9.13.4"),sQuery(id+"F0.wireOp",EDGE,"E4.12.13.4"),sQuery(id+"F0.wireOp",EDGE,"E4.15.13.4"),sQuery(id+"F0.wireOp",EDGE,"E4.18.13.4"),sQuery(id+"F0.wireOp",EDGE,"E4.21.13.4"),sQuery(id+"F0.wireOp",EDGE,"E4.24.13.4"),sQuery(id+"F0.wireOp",EDGE,"E4.27.13.4"),sQuery(id+"F0.wireOp",EDGE,"E4.30.13.4"),sQuery(id+"F0.wireOp",EDGE,"E4.33.13.4"),sQuery(id+"F0.wireOp",EDGE,"E4.36.13.4"),sQuery(id+"F0.wireOp",EDGE,"E4.39.13.4"),sQuery(id+"F0.wireOp",EDGE,"E4.6.13.5"),sQuery(id+"F0.wireOp",EDGE,"E4.9.13.5"),sQuery(id+"F0.wireOp",EDGE,"E4.12.13.5"),sQuery(id+"F0.wireOp",EDGE,"E4.15.13.5"),sQuery(id+"F0.wireOp",EDGE,"E4.18.13.5"),sQuery(id+"F0.wireOp",EDGE,"E4.21.13.5"),sQuery(id+"F0.wireOp",EDGE,"E4.24.13.5"),sQuery(id+"F0.wireOp",EDGE,"E4.27.13.5"),sQuery(id+"F0.wireOp",EDGE,"E4.30.13.5"),sQuery(id+"F0.wireOp",EDGE,"E4.33.13.5"),sQuery(id+"F0.wireOp",EDGE,"E4.36.13.5"),sQuery(id+"F0.wireOp",EDGE,"E4.39.13.5"),sQuery(id+"F0.wireOp",EDGE,"E4.6.13.6"),sQuery(id+"F0.wireOp",EDGE,"E4.9.13.6"),sQuery(id+"F0.wireOp",EDGE,"E4.12.13.6"),sQuery(id+"F0.wireOp",EDGE,"E4.15.13.6"),sQuery(id+"F0.wireOp",EDGE,"E4.18.13.6"),sQuery(id+"F0.wireOp",EDGE,"E4.21.13.6"),sQuery(id+"F0.wireOp",EDGE,"E4.24.13.6"),sQuery(id+"F0.wireOp",EDGE,"E4.27.13.6"),sQuery(id+"F0.wireOp",EDGE,"E4.30.13.6"),sQuery(id+"F0.wireOp",EDGE,"E4.33.13.6"),sQuery(id+"F0.wireOp",EDGE,"E4.36.13.6"),sQuery(id+"F0.wireOp",EDGE,"E4.39.13.6"),sQuery(id+"F0.wireOp",EDGE,"E4.6.13.7"),sQuery(id+"F0.wireOp",EDGE,"E4.9.13.7"),sQuery(id+"F0.wireOp",EDGE,"E4.12.13.7"),sQuery(id+"F0.wireOp",EDGE,"E4.15.13.7"),sQuery(id+"F0.wireOp",EDGE,"E4.18.13.7"),sQuery(id+"F0.wireOp",EDGE,"E4.21.13.7"),sQuery(id+"F0.wireOp",EDGE,"E4.24.13.7"),sQuery(id+"F0.wireOp",EDGE,"E4.27.13.7"),sQuery(id+"F0.wireOp",EDGE,"E4.30.13.7"),sQuery(id+"F0.wireOp",EDGE,"E4.33.13.7"),sQuery(id+"F0.wireOp",EDGE,"E4.36.13.7"),sQuery(id+"F0.wireOp",EDGE,"E4.39.13.7"),sQuery(id+"F0.wireOp",EDGE,"E4.6.13.8"),sQuery(id+"F0.wireOp",EDGE,"E4.9.13.8"),sQuery(id+"F0.wireOp",EDGE,"E4.12.13.8"),sQuery(id+"F0.wireOp",EDGE,"E4.15.13.8"),sQuery(id+"F0.wireOp",EDGE,"E4.18.13.8"),sQuery(id+"F0.wireOp",EDGE,"E4.21.13.8"),sQuery(id+"F0.wireOp",EDGE,"E4.24.13.8"),sQuery(id+"F0.wireOp",EDGE,"E4.27.13.8"),sQuery(id+"F0.wireOp",EDGE,"E4.30.13.8"),sQuery(id+"F0.wireOp",EDGE,"E4.33.13.8"),sQuery(id+"F0.wireOp",EDGE,"E4.36.13.8"),sQuery(id+"F0.wireOp",EDGE,"E4.39.13.8"),sQuery(id+"F0.wireOp",EDGE,"E4.6.13.9"),sQuery(id+"F0.wireOp",EDGE,"E4.9.13.9"),sQuery(id+"F0.wireOp",EDGE,"E4.12.13.9"),sQuery(id+"F0.wireOp",EDGE,"E4.15.13.9"),sQuery(id+"F0.wireOp",EDGE,"E4.18.13.9"),sQuery(id+"F0.wireOp",EDGE,"E4.21.13.9"),sQuery(id+"F0.wireOp",EDGE,"E4.24.13.9"),sQuery(id+"F0.wireOp",EDGE,"E4.27.13.9"),sQuery(id+"F0.wireOp",EDGE,"E4.30.13.9"),sQuery(id+"F0.wireOp",EDGE,"E4.33.13.9"),sQuery(id+"F0.wireOp",EDGE,"E4.36.13.9"),sQuery(id+"F0.wireOp",EDGE,"E4.39.13.9"),sQuery(id+"F0.wireOp",EDGE,"E4.6.14.0"),sQuery(id+"F0.wireOp",EDGE,"E4.9.14.0"),sQuery(id+"F0.wireOp",EDGE,"E4.12.14.0"),sQuery(id+"F0.wireOp",EDGE,"E4.15.14.0"),sQuery(id+"F0.wireOp",EDGE,"E4.18.14.0"),sQuery(id+"F0.wireOp",EDGE,"E4.21.14.0"),sQuery(id+"F0.wireOp",EDGE,"E4.24.14.0"),sQuery(id+"F0.wireOp",EDGE,"E4.27.14.0"),sQuery(id+"F0.wireOp",EDGE,"E4.30.14.0"),sQuery(id+"F0.wireOp",EDGE,"E4.33.14.0"),sQuery(id+"F0.wireOp",EDGE,"E4.36.14.0"),sQuery(id+"F0.wireOp",EDGE,"E4.39.14.0"),sQuery(id+"F0.wireOp",EDGE,"E4.6.14.1"),sQuery(id+"F0.wireOp",EDGE,"E4.9.14.1"),sQuery(id+"F0.wireOp",EDGE,"E4.12.14.1"),sQuery(id+"F0.wireOp",EDGE,"E4.15.14.1"),sQuery(id+"F0.wireOp",EDGE,"E4.18.14.1"),sQuery(id+"F0.wireOp",EDGE,"E4.21.14.1"),sQuery(id+"F0.wireOp",EDGE,"E4.24.14.1"),sQuery(id+"F0.wireOp",EDGE,"E4.27.14.1"),sQuery(id+"F0.wireOp",EDGE,"E4.30.14.1"),sQuery(id+"F0.wireOp",EDGE,"E4.33.14.1"),sQuery(id+"F0.wireOp",EDGE,"E4.36.14.1"),sQuery(id+"F0.wireOp",EDGE,"E4.39.14.1"),sQuery(id+"F0.wireOp",EDGE,"E4.6.14.2"),sQuery(id+"F0.wireOp",EDGE,"E4.9.14.2"),sQuery(id+"F0.wireOp",EDGE,"E4.12.14.2"),sQuery(id+"F0.wireOp",EDGE,"E4.15.14.2"),sQuery(id+"F0.wireOp",EDGE,"E4.18.14.2"),sQuery(id+"F0.wireOp",EDGE,"E4.21.14.2"),sQuery(id+"F0.wireOp",EDGE,"E4.24.14.2"),sQuery(id+"F0.wireOp",EDGE,"E4.27.14.2"),sQuery(id+"F0.wireOp",EDGE,"E4.30.14.2"),sQuery(id+"F0.wireOp",EDGE,"E4.33.14.2"),sQuery(id+"F0.wireOp",EDGE,"E4.36.14.2"),sQuery(id+"F0.wireOp",EDGE,"E4.39.14.2"),sQuery(id+"F0.wireOp",EDGE,"E4.6.14.3"),sQuery(id+"F0.wireOp",EDGE,"E4.9.14.3"),sQuery(id+"F0.wireOp",EDGE,"E4.12.14.3"),sQuery(id+"F0.wireOp",EDGE,"E4.15.14.3"),sQuery(id+"F0.wireOp",EDGE,"E4.18.14.3"),sQuery(id+"F0.wireOp",EDGE,"E4.21.14.3"),sQuery(id+"F0.wireOp",EDGE,"E4.24.14.3"),sQuery(id+"F0.wireOp",EDGE,"E4.27.14.3"),sQuery(id+"F0.wireOp",EDGE,"E4.30.14.3"),sQuery(id+"F0.wireOp",EDGE,"E4.33.14.3"),sQuery(id+"F0.wireOp",EDGE,"E4.36.14.3"),sQuery(id+"F0.wireOp",EDGE,"E4.39.14.3"),sQuery(id+"F0.wireOp",EDGE,"E4.6.14.4"),sQuery(id+"F0.wireOp",EDGE,"E4.9.14.4"),sQuery(id+"F0.wireOp",EDGE,"E4.12.14.4"),sQuery(id+"F0.wireOp",EDGE,"E4.15.14.4"),sQuery(id+"F0.wireOp",EDGE,"E4.18.14.4"),sQuery(id+"F0.wireOp",EDGE,"E4.21.14.4"),sQuery(id+"F0.wireOp",EDGE,"E4.24.14.4"),sQuery(id+"F0.wireOp",EDGE,"E4.27.14.4"),sQuery(id+"F0.wireOp",EDGE,"E4.30.14.4"),sQuery(id+"F0.wireOp",EDGE,"E4.33.14.4"),sQuery(id+"F0.wireOp",EDGE,"E4.36.14.4"),sQuery(id+"F0.wireOp",EDGE,"E4.39.14.4"),sQuery(id+"F0.wireOp",EDGE,"E4.6.14.5"),sQuery(id+"F0.wireOp",EDGE,"E4.9.14.5"),sQuery(id+"F0.wireOp",EDGE,"E4.12.14.5"),sQuery(id+"F0.wireOp",EDGE,"E4.15.14.5"),sQuery(id+"F0.wireOp",EDGE,"E4.18.14.5"),sQuery(id+"F0.wireOp",EDGE,"E4.21.14.5"),sQuery(id+"F0.wireOp",EDGE,"E4.24.14.5"),sQuery(id+"F0.wireOp",EDGE,"E4.27.14.5"),sQuery(id+"F0.wireOp",EDGE,"E4.30.14.5"),sQuery(id+"F0.wireOp",EDGE,"E4.33.14.5"),sQuery(id+"F0.wireOp",EDGE,"E4.36.14.5"),sQuery(id+"F0.wireOp",EDGE,"E4.39.14.5"),sQuery(id+"F0.wireOp",EDGE,"E4.6.14.6"),sQuery(id+"F0.wireOp",EDGE,"E4.9.14.6"),sQuery(id+"F0.wireOp",EDGE,"E4.12.14.6"),sQuery(id+"F0.wireOp",EDGE,"E4.15.14.6"),sQuery(id+"F0.wireOp",EDGE,"E4.18.14.6"),sQuery(id+"F0.wireOp",EDGE,"E4.21.14.6"),sQuery(id+"F0.wireOp",EDGE,"E4.24.14.6"),sQuery(id+"F0.wireOp",EDGE,"E4.27.14.6"),sQuery(id+"F0.wireOp",EDGE,"E4.30.14.6"),sQuery(id+"F0.wireOp",EDGE,"E4.33.14.6"),sQuery(id+"F0.wireOp",EDGE,"E4.36.14.6"),sQuery(id+"F0.wireOp",EDGE,"E4.39.14.6"),sQuery(id+"F0.wireOp",EDGE,"E4.6.14.7"),sQuery(id+"F0.wireOp",EDGE,"E4.9.14.7"),sQuery(id+"F0.wireOp",EDGE,"E4.12.14.7"),sQuery(id+"F0.wireOp",EDGE,"E4.15.14.7"),sQuery(id+"F0.wireOp",EDGE,"E4.18.14.7"),sQuery(id+"F0.wireOp",EDGE,"E4.21.14.7"),sQuery(id+"F0.wireOp",EDGE,"E4.24.14.7"),sQuery(id+"F0.wireOp",EDGE,"E4.27.14.7"),sQuery(id+"F0.wireOp",EDGE,"E4.30.14.7"),sQuery(id+"F0.wireOp",EDGE,"E4.33.14.7"),sQuery(id+"F0.wireOp",EDGE,"E4.36.14.7"),sQuery(id+"F0.wireOp",EDGE,"E4.39.14.7"),sQuery(id+"F0.wireOp",EDGE,"E4.6.14.8"),sQuery(id+"F0.wireOp",EDGE,"E4.9.14.8"),sQuery(id+"F0.wireOp",EDGE,"E4.12.14.8"),sQuery(id+"F0.wireOp",EDGE,"E4.15.14.8"),sQuery(id+"F0.wireOp",EDGE,"E4.18.14.8"),sQuery(id+"F0.wireOp",EDGE,"E4.21.14.8"),sQuery(id+"F0.wireOp",EDGE,"E4.24.14.8"),sQuery(id+"F0.wireOp",EDGE,"E4.27.14.8"),sQuery(id+"F0.wireOp",EDGE,"E4.30.14.8"),sQuery(id+"F0.wireOp",EDGE,"E4.33.14.8"),sQuery(id+"F0.wireOp",EDGE,"E4.36.14.8"),sQuery(id+"F0.wireOp",EDGE,"E4.39.14.8"),sQuery(id+"F0.wireOp",EDGE,"E4.6.14.9"),sQuery(id+"F0.wireOp",EDGE,"E4.9.14.9"),sQuery(id+"F0.wireOp",EDGE,"E4.12.14.9"),sQuery(id+"F0.wireOp",EDGE,"E4.15.14.9"),sQuery(id+"F0.wireOp",EDGE,"E4.18.14.9"),sQuery(id+"F0.wireOp",EDGE,"E4.21.14.9"),sQuery(id+"F0.wireOp",EDGE,"E4.24.14.9"),sQuery(id+"F0.wireOp",EDGE,"E4.27.14.9"),sQuery(id+"F0.wireOp",EDGE,"E4.30.14.9"),sQuery(id+"F0.wireOp",EDGE,"E4.33.14.9"),sQuery(id+"F0.wireOp",EDGE,"E4.36.14.9"),sQuery(id+"F0.wireOp",EDGE,"E4.39.14.9"),sQuery(id+"F0.wireOp",EDGE,"E4.6.15.0"),sQuery(id+"F0.wireOp",EDGE,"E4.9.15.0"),sQuery(id+"F0.wireOp",EDGE,"E4.12.15.0"),sQuery(id+"F0.wireOp",EDGE,"E4.15.15.0"),sQuery(id+"F0.wireOp",EDGE,"E4.18.15.0"),sQuery(id+"F0.wireOp",EDGE,"E4.21.15.0"),sQuery(id+"F0.wireOp",EDGE,"E4.24.15.0"),sQuery(id+"F0.wireOp",EDGE,"E4.27.15.0"),sQuery(id+"F0.wireOp",EDGE,"E4.30.15.0"),sQuery(id+"F0.wireOp",EDGE,"E4.33.15.0"),sQuery(id+"F0.wireOp",EDGE,"E4.36.15.0"),sQuery(id+"F0.wireOp",EDGE,"E4.39.15.0"),sQuery(id+"F0.wireOp",EDGE,"E4.6.15.1"),sQuery(id+"F0.wireOp",EDGE,"E4.9.15.1"),sQuery(id+"F0.wireOp",EDGE,"E4.12.15.1"),sQuery(id+"F0.wireOp",EDGE,"E4.15.15.1"),sQuery(id+"F0.wireOp",EDGE,"E4.18.15.1"),sQuery(id+"F0.wireOp",EDGE,"E4.21.15.1"),sQuery(id+"F0.wireOp",EDGE,"E4.24.15.1"),sQuery(id+"F0.wireOp",EDGE,"E4.27.15.1"),sQuery(id+"F0.wireOp",EDGE,"E4.30.15.1"),sQuery(id+"F0.wireOp",EDGE,"E4.33.15.1"),sQuery(id+"F0.wireOp",EDGE,"E4.36.15.1"),sQuery(id+"F0.wireOp",EDGE,"E4.39.15.1"),sQuery(id+"F0.wireOp",EDGE,"E4.6.15.2"),sQuery(id+"F0.wireOp",EDGE,"E4.9.15.2"),sQuery(id+"F0.wireOp",EDGE,"E4.12.15.2"),sQuery(id+"F0.wireOp",EDGE,"E4.15.15.2"),sQuery(id+"F0.wireOp",EDGE,"E4.18.15.2"),sQuery(id+"F0.wireOp",EDGE,"E4.21.15.2"),sQuery(id+"F0.wireOp",EDGE,"E4.24.15.2"),sQuery(id+"F0.wireOp",EDGE,"E4.27.15.2"),sQuery(id+"F0.wireOp",EDGE,"E4.30.15.2"),sQuery(id+"F0.wireOp",EDGE,"E4.33.15.2"),sQuery(id+"F0.wireOp",EDGE,"E4.36.15.2"),sQuery(id+"F0.wireOp",EDGE,"E4.39.15.2"),sQuery(id+"F0.wireOp",EDGE,"E4.6.15.3"),sQuery(id+"F0.wireOp",EDGE,"E4.9.15.3"),sQuery(id+"F0.wireOp",EDGE,"E4.12.15.3"),sQuery(id+"F0.wireOp",EDGE,"E4.15.15.3"),sQuery(id+"F0.wireOp",EDGE,"E4.18.15.3"),sQuery(id+"F0.wireOp",EDGE,"E4.21.15.3"),sQuery(id+"F0.wireOp",EDGE,"E4.24.15.3"),sQuery(id+"F0.wireOp",EDGE,"E4.27.15.3"),sQuery(id+"F0.wireOp",EDGE,"E4.30.15.3"),sQuery(id+"F0.wireOp",EDGE,"E4.33.15.3"),sQuery(id+"F0.wireOp",EDGE,"E4.36.15.3"),sQuery(id+"F0.wireOp",EDGE,"E4.39.15.3"),sQuery(id+"F0.wireOp",EDGE,"E4.6.15.4"),sQuery(id+"F0.wireOp",EDGE,"E4.9.15.4"),sQuery(id+"F0.wireOp",EDGE,"E4.12.15.4"),sQuery(id+"F0.wireOp",EDGE,"E4.15.15.4"),sQuery(id+"F0.wireOp",EDGE,"E4.18.15.4"),sQuery(id+"F0.wireOp",EDGE,"E4.21.15.4"),sQuery(id+"F0.wireOp",EDGE,"E4.24.15.4"),sQuery(id+"F0.wireOp",EDGE,"E4.27.15.4"),sQuery(id+"F0.wireOp",EDGE,"E4.30.15.4"),sQuery(id+"F0.wireOp",EDGE,"E4.33.15.4"),sQuery(id+"F0.wireOp",EDGE,"E4.36.15.4"),sQuery(id+"F0.wireOp",EDGE,"E4.39.15.4"),sQuery(id+"F0.wireOp",EDGE,"E4.6.15.5"),sQuery(id+"F0.wireOp",EDGE,"E4.9.15.5"),sQuery(id+"F0.wireOp",EDGE,"E4.12.15.5"),sQuery(id+"F0.wireOp",EDGE,"E4.15.15.5"),sQuery(id+"F0.wireOp",EDGE,"E4.18.15.5"),sQuery(id+"F0.wireOp",EDGE,"E4.21.15.5"),sQuery(id+"F0.wireOp",EDGE,"E4.24.15.5"),sQuery(id+"F0.wireOp",EDGE,"E4.27.15.5"),sQuery(id+"F0.wireOp",EDGE,"E4.30.15.5"),sQuery(id+"F0.wireOp",EDGE,"E4.33.15.5"),sQuery(id+"F0.wireOp",EDGE,"E4.36.15.5"),sQuery(id+"F0.wireOp",EDGE,"E4.39.15.5"),sQuery(id+"F0.wireOp",EDGE,"E4.6.15.6"),sQuery(id+"F0.wireOp",EDGE,"E4.9.15.6"),sQuery(id+"F0.wireOp",EDGE,"E4.12.15.6"),sQuery(id+"F0.wireOp",EDGE,"E4.15.15.6"),sQuery(id+"F0.wireOp",EDGE,"E4.18.15.6"),sQuery(id+"F0.wireOp",EDGE,"E4.21.15.6"),sQuery(id+"F0.wireOp",EDGE,"E4.24.15.6"),sQuery(id+"F0.wireOp",EDGE,"E4.27.15.6"),sQuery(id+"F0.wireOp",EDGE,"E4.30.15.6"),sQuery(id+"F0.wireOp",EDGE,"E4.33.15.6"),sQuery(id+"F0.wireOp",EDGE,"E4.36.15.6"),sQuery(id+"F0.wireOp",EDGE,"E4.39.15.6"),sQuery(id+"F0.wireOp",EDGE,"E4.6.15.7"),sQuery(id+"F0.wireOp",EDGE,"E4.9.15.7"),sQuery(id+"F0.wireOp",EDGE,"E4.12.15.7"),sQuery(id+"F0.wireOp",EDGE,"E4.15.15.7"),sQuery(id+"F0.wireOp",EDGE,"E4.18.15.7"),sQuery(id+"F0.wireOp",EDGE,"E4.21.15.7"),sQuery(id+"F0.wireOp",EDGE,"E4.24.15.7"),sQuery(id+"F0.wireOp",EDGE,"E4.27.15.7"),sQuery(id+"F0.wireOp",EDGE,"E4.30.15.7"),sQuery(id+"F0.wireOp",EDGE,"E4.33.15.7"),sQuery(id+"F0.wireOp",EDGE,"E4.36.15.7"),sQuery(id+"F0.wireOp",EDGE,"E4.39.15.7"),sQuery(id+"F0.wireOp",EDGE,"E4.6.15.8"),sQuery(id+"F0.wireOp",EDGE,"E4.9.15.8"),sQuery(id+"F0.wireOp",EDGE,"E4.12.15.8"),sQuery(id+"F0.wireOp",EDGE,"E4.15.15.8"),sQuery(id+"F0.wireOp",EDGE,"E4.18.15.8"),sQuery(id+"F0.wireOp",EDGE,"E4.21.15.8"),sQuery(id+"F0.wireOp",EDGE,"E4.24.15.8"),sQuery(id+"F0.wireOp",EDGE,"E4.27.15.8"),sQuery(id+"F0.wireOp",EDGE,"E4.30.15.8"),sQuery(id+"F0.wireOp",EDGE,"E4.33.15.8"),sQuery(id+"F0.wireOp",EDGE,"E4.36.15.8"),sQuery(id+"F0.wireOp",EDGE,"E4.39.15.8"),sQuery(id+"F0.wireOp",EDGE,"E4.6.15.9"),sQuery(id+"F0.wireOp",EDGE,"E4.9.15.9"),sQuery(id+"F0.wireOp",EDGE,"E4.12.15.9"),sQuery(id+"F0.wireOp",EDGE,"E4.15.15.9"),sQuery(id+"F0.wireOp",EDGE,"E4.18.15.9"),sQuery(id+"F0.wireOp",EDGE,"E4.21.15.9"),sQuery(id+"F0.wireOp",EDGE,"E4.24.15.9"),sQuery(id+"F0.wireOp",EDGE,"E4.27.15.9"),sQuery(id+"F0.wireOp",EDGE,"E4.30.15.9"),sQuery(id+"F0.wireOp",EDGE,"E4.33.15.9"),sQuery(id+"F0.wireOp",EDGE,"E4.36.15.9"),sQuery(id+"F0.wireOp",EDGE,"E4.39.15.9"),sQuery(id+"F0.wireOp",EDGE,"E4.6.16.0"),sQuery(id+"F0.wireOp",EDGE,"E4.9.16.0"),sQuery(id+"F0.wireOp",EDGE,"E4.12.16.0"),sQuery(id+"F0.wireOp",EDGE,"E4.15.16.0"),sQuery(id+"F0.wireOp",EDGE,"E4.18.16.0"),sQuery(id+"F0.wireOp",EDGE,"E4.21.16.0"),sQuery(id+"F0.wireOp",EDGE,"E4.24.16.0"),sQuery(id+"F0.wireOp",EDGE,"E4.27.16.0"),sQuery(id+"F0.wireOp",EDGE,"E4.30.16.0"),sQuery(id+"F0.wireOp",EDGE,"E4.33.16.0"),sQuery(id+"F0.wireOp",EDGE,"E4.36.16.0"),sQuery(id+"F0.wireOp",EDGE,"E4.39.16.0"),sQuery(id+"F0.wireOp",EDGE,"E4.6.16.1"),sQuery(id+"F0.wireOp",EDGE,"E4.9.16.1"),sQuery(id+"F0.wireOp",EDGE,"E4.12.16.1"),sQuery(id+"F0.wireOp",EDGE,"E4.15.16.1"),sQuery(id+"F0.wireOp",EDGE,"E4.18.16.1"),sQuery(id+"F0.wireOp",EDGE,"E4.21.16.1"),sQuery(id+"F0.wireOp",EDGE,"E4.24.16.1"),sQuery(id+"F0.wireOp",EDGE,"E4.27.16.1"),sQuery(id+"F0.wireOp",EDGE,"E4.30.16.1"),sQuery(id+"F0.wireOp",EDGE,"E4.33.16.1"),sQuery(id+"F0.wireOp",EDGE,"E4.36.16.1"),sQuery(id+"F0.wireOp",EDGE,"E4.39.16.1"),sQuery(id+"F0.wireOp",EDGE,"E4.6.16.2"),sQuery(id+"F0.wireOp",EDGE,"E4.9.16.2"),sQuery(id+"F0.wireOp",EDGE,"E4.12.16.2"),sQuery(id+"F0.wireOp",EDGE,"E4.15.16.2"),sQuery(id+"F0.wireOp",EDGE,"E4.18.16.2"),sQuery(id+"F0.wireOp",EDGE,"E4.21.16.2"),sQuery(id+"F0.wireOp",EDGE,"E4.24.16.2"),sQuery(id+"F0.wireOp",EDGE,"E4.27.16.2"),sQuery(id+"F0.wireOp",EDGE,"E4.30.16.2"),sQuery(id+"F0.wireOp",EDGE,"E4.33.16.2"),sQuery(id+"F0.wireOp",EDGE,"E4.36.16.2"),sQuery(id+"F0.wireOp",EDGE,"E4.39.16.2"),sQuery(id+"F0.wireOp",EDGE,"E4.6.16.3"),sQuery(id+"F0.wireOp",EDGE,"E4.9.16.3"),sQuery(id+"F0.wireOp",EDGE,"E4.12.16.3"),sQuery(id+"F0.wireOp",EDGE,"E4.15.16.3"),sQuery(id+"F0.wireOp",EDGE,"E4.18.16.3"),sQuery(id+"F0.wireOp",EDGE,"E4.21.16.3"),sQuery(id+"F0.wireOp",EDGE,"E4.24.16.3"),sQuery(id+"F0.wireOp",EDGE,"E4.27.16.3"),sQuery(id+"F0.wireOp",EDGE,"E4.30.16.3"),sQuery(id+"F0.wireOp",EDGE,"E4.33.16.3"),sQuery(id+"F0.wireOp",EDGE,"E4.36.16.3"),sQuery(id+"F0.wireOp",EDGE,"E4.39.16.3"),sQuery(id+"F0.wireOp",EDGE,"E4.6.16.4"),sQuery(id+"F0.wireOp",EDGE,"E4.9.16.4"),sQuery(id+"F0.wireOp",EDGE,"E4.12.16.4"),sQuery(id+"F0.wireOp",EDGE,"E4.15.16.4"),sQuery(id+"F0.wireOp",EDGE,"E4.18.16.4"),sQuery(id+"F0.wireOp",EDGE,"E4.21.16.4"),sQuery(id+"F0.wireOp",EDGE,"E4.24.16.4"),sQuery(id+"F0.wireOp",EDGE,"E4.27.16.4"),sQuery(id+"F0.wireOp",EDGE,"E4.30.16.4"),sQuery(id+"F0.wireOp",EDGE,"E4.33.16.4"),sQuery(id+"F0.wireOp",EDGE,"E4.36.16.4"),sQuery(id+"F0.wireOp",EDGE,"E4.39.16.4"),sQuery(id+"F0.wireOp",EDGE,"E4.6.16.5"),sQuery(id+"F0.wireOp",EDGE,"E4.9.16.5"),sQuery(id+"F0.wireOp",EDGE,"E4.12.16.5"),sQuery(id+"F0.wireOp",EDGE,"E4.15.16.5"),sQuery(id+"F0.wireOp",EDGE,"E4.18.16.5"),sQuery(id+"F0.wireOp",EDGE,"E4.21.16.5"),sQuery(id+"F0.wireOp",EDGE,"E4.24.16.5"),sQuery(id+"F0.wireOp",EDGE,"E4.27.16.5"),sQuery(id+"F0.wireOp",EDGE,"E4.30.16.5"),sQuery(id+"F0.wireOp",EDGE,"E4.33.16.5"),sQuery(id+"F0.wireOp",EDGE,"E4.36.16.5"),sQuery(id+"F0.wireOp",EDGE,"E4.39.16.5"),sQuery(id+"F0.wireOp",EDGE,"E4.6.16.6"),sQuery(id+"F0.wireOp",EDGE,"E4.9.16.6"),sQuery(id+"F0.wireOp",EDGE,"E4.12.16.6"),sQuery(id+"F0.wireOp",EDGE,"E4.15.16.6"),sQuery(id+"F0.wireOp",EDGE,"E4.18.16.6"),sQuery(id+"F0.wireOp",EDGE,"E4.21.16.6"),sQuery(id+"F0.wireOp",EDGE,"E4.24.16.6"),sQuery(id+"F0.wireOp",EDGE,"E4.27.16.6"),sQuery(id+"F0.wireOp",EDGE,"E4.30.16.6"),sQuery(id+"F0.wireOp",EDGE,"E4.33.16.6"),sQuery(id+"F0.wireOp",EDGE,"E4.36.16.6"),sQuery(id+"F0.wireOp",EDGE,"E4.39.16.6"),sQuery(id+"F0.wireOp",EDGE,"E4.6.16.7"),sQuery(id+"F0.wireOp",EDGE,"E4.9.16.7"),sQuery(id+"F0.wireOp",EDGE,"E4.12.16.7"),sQuery(id+"F0.wireOp",EDGE,"E4.15.16.7"),sQuery(id+"F0.wireOp",EDGE,"E4.18.16.7"),sQuery(id+"F0.wireOp",EDGE,"E4.21.16.7"),sQuery(id+"F0.wireOp",EDGE,"E4.24.16.7"),sQuery(id+"F0.wireOp",EDGE,"E4.27.16.7"),sQuery(id+"F0.wireOp",EDGE,"E4.30.16.7"),sQuery(id+"F0.wireOp",EDGE,"E4.33.16.7"),sQuery(id+"F0.wireOp",EDGE,"E4.36.16.7"),sQuery(id+"F0.wireOp",EDGE,"E4.39.16.7"),sQuery(id+"F0.wireOp",EDGE,"E4.6.16.8"),sQuery(id+"F0.wireOp",EDGE,"E4.9.16.8"),sQuery(id+"F0.wireOp",EDGE,"E4.12.16.8"),sQuery(id+"F0.wireOp",EDGE,"E4.15.16.8"),sQuery(id+"F0.wireOp",EDGE,"E4.18.16.8"),sQuery(id+"F0.wireOp",EDGE,"E4.21.16.8"),sQuery(id+"F0.wireOp",EDGE,"E4.24.16.8"),sQuery(id+"F0.wireOp",EDGE,"E4.27.16.8"),sQuery(id+"F0.wireOp",EDGE,"E4.30.16.8"),sQuery(id+"F0.wireOp",EDGE,"E4.33.16.8"),sQuery(id+"F0.wireOp",EDGE,"E4.36.16.8"),sQuery(id+"F0.wireOp",EDGE,"E4.39.16.8"),sQuery(id+"F0.wireOp",EDGE,"E4.6.16.9"),sQuery(id+"F0.wireOp",EDGE,"E4.9.16.9"),sQuery(id+"F0.wireOp",EDGE,"E4.12.16.9"),sQuery(id+"F0.wireOp",EDGE,"E4.15.16.9"),sQuery(id+"F0.wireOp",EDGE,"E4.18.16.9"),sQuery(id+"F0.wireOp",EDGE,"E4.21.16.9"),sQuery(id+"F0.wireOp",EDGE,"E4.24.16.9"),sQuery(id+"F0.wireOp",EDGE,"E4.27.16.9"),sQuery(id+"F0.wireOp",EDGE,"E4.30.16.9"),sQuery(id+"F0.wireOp",EDGE,"E4.33.16.9"),sQuery(id+"F0.wireOp",EDGE,"E4.36.16.9"),sQuery(id+"F0.wireOp",EDGE,"E4.39.16.9"),sQuery(id+"F0.wireOp",EDGE,"E4.6.17.0"),sQuery(id+"F0.wireOp",EDGE,"E4.9.17.0"),sQuery(id+"F0.wireOp",EDGE,"E4.12.17.0"),sQuery(id+"F0.wireOp",EDGE,"E4.15.17.0"),sQuery(id+"F0.wireOp",EDGE,"E4.18.17.0"),sQuery(id+"F0.wireOp",EDGE,"E4.21.17.0"),sQuery(id+"F0.wireOp",EDGE,"E4.24.17.0"),sQuery(id+"F0.wireOp",EDGE,"E4.27.17.0"),sQuery(id+"F0.wireOp",EDGE,"E4.30.17.0"),sQuery(id+"F0.wireOp",EDGE,"E4.33.17.0"),sQuery(id+"F0.wireOp",EDGE,"E4.36.17.0"),sQuery(id+"F0.wireOp",EDGE,"E4.39.17.0"),sQuery(id+"F0.wireOp",EDGE,"E4.6.17.1"),sQuery(id+"F0.wireOp",EDGE,"E4.9.17.1"),sQuery(id+"F0.wireOp",EDGE,"E4.12.17.1"),sQuery(id+"F0.wireOp",EDGE,"E4.15.17.1"),sQuery(id+"F0.wireOp",EDGE,"E4.18.17.1"),sQuery(id+"F0.wireOp",EDGE,"E4.21.17.1"),sQuery(id+"F0.wireOp",EDGE,"E4.24.17.1"),sQuery(id+"F0.wireOp",EDGE,"E4.27.17.1"),sQuery(id+"F0.wireOp",EDGE,"E4.30.17.1"),sQuery(id+"F0.wireOp",EDGE,"E4.33.17.1"),sQuery(id+"F0.wireOp",EDGE,"E4.36.17.1"),sQuery(id+"F0.wireOp",EDGE,"E4.39.17.1"),sQuery(id+"F0.wireOp",EDGE,"E4.6.17.2"),sQuery(id+"F0.wireOp",EDGE,"E4.9.17.2"),sQuery(id+"F0.wireOp",EDGE,"E4.12.17.2"),sQuery(id+"F0.wireOp",EDGE,"E4.15.17.2"),sQuery(id+"F0.wireOp",EDGE,"E4.18.17.2"),sQuery(id+"F0.wireOp",EDGE,"E4.21.17.2"),sQuery(id+"F0.wireOp",EDGE,"E4.24.17.2"),sQuery(id+"F0.wireOp",EDGE,"E4.27.17.2"),sQuery(id+"F0.wireOp",EDGE,"E4.30.17.2"),sQuery(id+"F0.wireOp",EDGE,"E4.33.17.2"),sQuery(id+"F0.wireOp",EDGE,"E4.36.17.2"),sQuery(id+"F0.wireOp",EDGE,"E4.39.17.2"),sQuery(id+"F0.wireOp",EDGE,"E4.6.17.3"),sQuery(id+"F0.wireOp",EDGE,"E4.9.17.3"),sQuery(id+"F0.wireOp",EDGE,"E4.12.17.3"),sQuery(id+"F0.wireOp",EDGE,"E4.15.17.3"),sQuery(id+"F0.wireOp",EDGE,"E4.18.17.3"),sQuery(id+"F0.wireOp",EDGE,"E4.21.17.3"),sQuery(id+"F0.wireOp",EDGE,"E4.24.17.3"),sQuery(id+"F0.wireOp",EDGE,"E4.27.17.3"),sQuery(id+"F0.wireOp",EDGE,"E4.30.17.3"),sQuery(id+"F0.wireOp",EDGE,"E4.33.17.3"),sQuery(id+"F0.wireOp",EDGE,"E4.36.17.3"),sQuery(id+"F0.wireOp",EDGE,"E4.39.17.3"),sQuery(id+"F0.wireOp",EDGE,"E4.6.17.4"),sQuery(id+"F0.wireOp",EDGE,"E4.9.17.4"),sQuery(id+"F0.wireOp",EDGE,"E4.12.17.4"),sQuery(id+"F0.wireOp",EDGE,"E4.15.17.4"),sQuery(id+"F0.wireOp",EDGE,"E4.18.17.4"),sQuery(id+"F0.wireOp",EDGE,"E4.21.17.4"),sQuery(id+"F0.wireOp",EDGE,"E4.24.17.4"),sQuery(id+"F0.wireOp",EDGE,"E4.27.17.4"),sQuery(id+"F0.wireOp",EDGE,"E4.30.17.4"),sQuery(id+"F0.wireOp",EDGE,"E4.33.17.4"),sQuery(id+"F0.wireOp",EDGE,"E4.36.17.4"),sQuery(id+"F0.wireOp",EDGE,"E4.39.17.4"),sQuery(id+"F0.wireOp",EDGE,"E4.6.17.5"),sQuery(id+"F0.wireOp",EDGE,"E4.9.17.5"),sQuery(id+"F0.wireOp",EDGE,"E4.12.17.5"),sQuery(id+"F0.wireOp",EDGE,"E4.15.17.5"),sQuery(id+"F0.wireOp",EDGE,"E4.18.17.5"),sQuery(id+"F0.wireOp",EDGE,"E4.21.17.5"),sQuery(id+"F0.wireOp",EDGE,"E4.24.17.5"),sQuery(id+"F0.wireOp",EDGE,"E4.27.17.5"),sQuery(id+"F0.wireOp",EDGE,"E4.30.17.5"),sQuery(id+"F0.wireOp",EDGE,"E4.33.17.5"),sQuery(id+"F0.wireOp",EDGE,"E4.36.17.5"),sQuery(id+"F0.wireOp",EDGE,"E4.39.17.5"),sQuery(id+"F0.wireOp",EDGE,"E4.6.17.6"),sQuery(id+"F0.wireOp",EDGE,"E4.9.17.6"),sQuery(id+"F0.wireOp",EDGE,"E4.12.17.6"),sQuery(id+"F0.wireOp",EDGE,"E4.15.17.6"),sQuery(id+"F0.wireOp",EDGE,"E4.18.17.6"),sQuery(id+"F0.wireOp",EDGE,"E4.21.17.6"),sQuery(id+"F0.wireOp",EDGE,"E4.24.17.6"),sQuery(id+"F0.wireOp",EDGE,"E4.27.17.6"),sQuery(id+"F0.wireOp",EDGE,"E4.30.17.6"),sQuery(id+"F0.wireOp",EDGE,"E4.33.17.6"),sQuery(id+"F0.wireOp",EDGE,"E4.36.17.6"),sQuery(id+"F0.wireOp",EDGE,"E4.39.17.6"),sQuery(id+"F0.wireOp",EDGE,"E4.6.17.7"),sQuery(id+"F0.wireOp",EDGE,"E4.9.17.7"),sQuery(id+"F0.wireOp",EDGE,"E4.12.17.7"),sQuery(id+"F0.wireOp",EDGE,"E4.15.17.7"),sQuery(id+"F0.wireOp",EDGE,"E4.18.17.7"),sQuery(id+"F0.wireOp",EDGE,"E4.21.17.7"),sQuery(id+"F0.wireOp",EDGE,"E4.24.17.7"),sQuery(id+"F0.wireOp",EDGE,"E4.27.17.7"),sQuery(id+"F0.wireOp",EDGE,"E4.30.17.7"),sQuery(id+"F0.wireOp",EDGE,"E4.33.17.7"),sQuery(id+"F0.wireOp",EDGE,"E4.36.17.7"),sQuery(id+"F0.wireOp",EDGE,"E4.39.17.7"),sQuery(id+"F0.wireOp",EDGE,"E4.6.17.8"),sQuery(id+"F0.wireOp",EDGE,"E4.9.17.8"),sQuery(id+"F0.wireOp",EDGE,"E4.12.17.8"),sQuery(id+"F0.wireOp",EDGE,"E4.15.17.8"),sQuery(id+"F0.wireOp",EDGE,"E4.18.17.8"),sQuery(id+"F0.wireOp",EDGE,"E4.21.17.8"),sQuery(id+"F0.wireOp",EDGE,"E4.24.17.8"),sQuery(id+"F0.wireOp",EDGE,"E4.27.17.8"),sQuery(id+"F0.wireOp",EDGE,"E4.30.17.8"),sQuery(id+"F0.wireOp",EDGE,"E4.33.17.8"),sQuery(id+"F0.wireOp",EDGE,"E4.36.17.8"),sQuery(id+"F0.wireOp",EDGE,"E4.39.17.8"),sQuery(id+"F0.wireOp",EDGE,"E4.6.17.9"),sQuery(id+"F0.wireOp",EDGE,"E4.9.17.9"),sQuery(id+"F0.wireOp",EDGE,"E4.12.17.9"),sQuery(id+"F0.wireOp",EDGE,"E4.15.17.9"),sQuery(id+"F0.wireOp",EDGE,"E4.18.17.9"),sQuery(id+"F0.wireOp",EDGE,"E4.21.17.9"),sQuery(id+"F0.wireOp",EDGE,"E4.24.17.9"),sQuery(id+"F0.wireOp",EDGE,"E4.27.17.9"),sQuery(id+"F0.wireOp",EDGE,"E4.30.17.9"),sQuery(id+"F0.wireOp",EDGE,"E4.33.17.9"),sQuery(id+"F0.wireOp",EDGE,"E4.36.17.9"),sQuery(id+"F0.wireOp",EDGE,"E4.39.17.9"),sQuery(id+"F0.wireOp",EDGE,"E4.6.18.0"),sQuery(id+"F0.wireOp",EDGE,"E4.9.18.0"),sQuery(id+"F0.wireOp",EDGE,"E4.12.18.0"),sQuery(id+"F0.wireOp",EDGE,"E4.15.18.0"),sQuery(id+"F0.wireOp",EDGE,"E4.18.18.0"),sQuery(id+"F0.wireOp",EDGE,"E4.21.18.0"),sQuery(id+"F0.wireOp",EDGE,"E4.24.18.0"),sQuery(id+"F0.wireOp",EDGE,"E4.27.18.0"),sQuery(id+"F0.wireOp",EDGE,"E4.30.18.0"),sQuery(id+"F0.wireOp",EDGE,"E4.33.18.0"),sQuery(id+"F0.wireOp",EDGE,"E4.36.18.0"),sQuery(id+"F0.wireOp",EDGE,"E4.39.18.0"),sQuery(id+"F0.wireOp",EDGE,"E4.6.18.1"),sQuery(id+"F0.wireOp",EDGE,"E4.9.18.1"),sQuery(id+"F0.wireOp",EDGE,"E4.12.18.1"),sQuery(id+"F0.wireOp",EDGE,"E4.15.18.1"),sQuery(id+"F0.wireOp",EDGE,"E4.18.18.1"),sQuery(id+"F0.wireOp",EDGE,"E4.21.18.1"),sQuery(id+"F0.wireOp",EDGE,"E4.24.18.1"),sQuery(id+"F0.wireOp",EDGE,"E4.27.18.1"),sQuery(id+"F0.wireOp",EDGE,"E4.30.18.1"),sQuery(id+"F0.wireOp",EDGE,"E4.33.18.1"),sQuery(id+"F0.wireOp",EDGE,"E4.36.18.1"),sQuery(id+"F0.wireOp",EDGE,"E4.39.18.1"),sQuery(id+"F0.wireOp",EDGE,"E4.6.18.2"),sQuery(id+"F0.wireOp",EDGE,"E4.9.18.2"),sQuery(id+"F0.wireOp",EDGE,"E4.12.18.2"),sQuery(id+"F0.wireOp",EDGE,"E4.15.18.2"),sQuery(id+"F0.wireOp",EDGE,"E4.18.18.2"),sQuery(id+"F0.wireOp",EDGE,"E4.21.18.2"),sQuery(id+"F0.wireOp",EDGE,"E4.24.18.2"),sQuery(id+"F0.wireOp",EDGE,"E4.27.18.2"),sQuery(id+"F0.wireOp",EDGE,"E4.30.18.2"),sQuery(id+"F0.wireOp",EDGE,"E4.33.18.2"),sQuery(id+"F0.wireOp",EDGE,"E4.36.18.2"),sQuery(id+"F0.wireOp",EDGE,"E4.39.18.2"),sQuery(id+"F0.wireOp",EDGE,"E4.6.18.3"),sQuery(id+"F0.wireOp",EDGE,"E4.9.18.3"),sQuery(id+"F0.wireOp",EDGE,"E4.12.18.3"),sQuery(id+"F0.wireOp",EDGE,"E4.15.18.3"),sQuery(id+"F0.wireOp",EDGE,"E4.18.18.3"),sQuery(id+"F0.wireOp",EDGE,"E4.21.18.3"),sQuery(id+"F0.wireOp",EDGE,"E4.24.18.3"),sQuery(id+"F0.wireOp",EDGE,"E4.27.18.3"),sQuery(id+"F0.wireOp",EDGE,"E4.30.18.3"),sQuery(id+"F0.wireOp",EDGE,"E4.33.18.3"),sQuery(id+"F0.wireOp",EDGE,"E4.36.18.3"),sQuery(id+"F0.wireOp",EDGE,"E4.39.18.3"),sQuery(id+"F0.wireOp",EDGE,"E4.6.18.4"),sQuery(id+"F0.wireOp",EDGE,"E4.9.18.4"),sQuery(id+"F0.wireOp",EDGE,"E4.12.18.4"),sQuery(id+"F0.wireOp",EDGE,"E4.15.18.4"),sQuery(id+"F0.wireOp",EDGE,"E4.18.18.4"),sQuery(id+"F0.wireOp",EDGE,"E4.21.18.4"),sQuery(id+"F0.wireOp",EDGE,"E4.24.18.4"),sQuery(id+"F0.wireOp",EDGE,"E4.27.18.4"),sQuery(id+"F0.wireOp",EDGE,"E4.30.18.4"),sQuery(id+"F0.wireOp",EDGE,"E4.33.18.4"),sQuery(id+"F0.wireOp",EDGE,"E4.36.18.4"),sQuery(id+"F0.wireOp",EDGE,"E4.39.18.4"),sQuery(id+"F0.wireOp",EDGE,"E4.6.18.5"),sQuery(id+"F0.wireOp",EDGE,"E4.9.18.5"),sQuery(id+"F0.wireOp",EDGE,"E4.12.18.5"),sQuery(id+"F0.wireOp",EDGE,"E4.15.18.5"),sQuery(id+"F0.wireOp",EDGE,"E4.18.18.5"),sQuery(id+"F0.wireOp",EDGE,"E4.21.18.5"),sQuery(id+"F0.wireOp",EDGE,"E4.24.18.5"),sQuery(id+"F0.wireOp",EDGE,"E4.27.18.5"),sQuery(id+"F0.wireOp",EDGE,"E4.30.18.5"),sQuery(id+"F0.wireOp",EDGE,"E4.33.18.5"),sQuery(id+"F0.wireOp",EDGE,"E4.36.18.5"),sQuery(id+"F0.wireOp",EDGE,"E4.39.18.5"),sQuery(id+"F0.wireOp",EDGE,"E4.6.18.6"),sQuery(id+"F0.wireOp",EDGE,"E4.9.18.6"),sQuery(id+"F0.wireOp",EDGE,"E4.12.18.6"),sQuery(id+"F0.wireOp",EDGE,"E4.15.18.6"),sQuery(id+"F0.wireOp",EDGE,"E4.18.18.6"),sQuery(id+"F0.wireOp",EDGE,"E4.21.18.6"),sQuery(id+"F0.wireOp",EDGE,"E4.24.18.6"),sQuery(id+"F0.wireOp",EDGE,"E4.27.18.6"),sQuery(id+"F0.wireOp",EDGE,"E4.30.18.6"),sQuery(id+"F0.wireOp",EDGE,"E4.33.18.6"),sQuery(id+"F0.wireOp",EDGE,"E4.36.18.6"),sQuery(id+"F0.wireOp",EDGE,"E4.39.18.6"),sQuery(id+"F0.wireOp",EDGE,"E4.6.18.7"),sQuery(id+"F0.wireOp",EDGE,"E4.9.18.7"),sQuery(id+"F0.wireOp",EDGE,"E4.12.18.7"),sQuery(id+"F0.wireOp",EDGE,"E4.15.18.7"),sQuery(id+"F0.wireOp",EDGE,"E4.18.18.7"),sQuery(id+"F0.wireOp",EDGE,"E4.21.18.7"),sQuery(id+"F0.wireOp",EDGE,"E4.24.18.7"),sQuery(id+"F0.wireOp",EDGE,"E4.27.18.7"),sQuery(id+"F0.wireOp",EDGE,"E4.30.18.7"),sQuery(id+"F0.wireOp",EDGE,"E4.33.18.7"),sQuery(id+"F0.wireOp",EDGE,"E4.36.18.7"),sQuery(id+"F0.wireOp",EDGE,"E4.39.18.7"),sQuery(id+"F0.wireOp",EDGE,"E4.6.18.8"),sQuery(id+"F0.wireOp",EDGE,"E4.9.18.8"),sQuery(id+"F0.wireOp",EDGE,"E4.12.18.8"),sQuery(id+"F0.wireOp",EDGE,"E4.15.18.8"),sQuery(id+"F0.wireOp",EDGE,"E4.18.18.8"),sQuery(id+"F0.wireOp",EDGE,"E4.21.18.8"),sQuery(id+"F0.wireOp",EDGE,"E4.24.18.8"),sQuery(id+"F0.wireOp",EDGE,"E4.27.18.8"),sQuery(id+"F0.wireOp",EDGE,"E4.30.18.8"),sQuery(id+"F0.wireOp",EDGE,"E4.33.18.8"),sQuery(id+"F0.wireOp",EDGE,"E4.36.18.8"),sQuery(id+"F0.wireOp",EDGE,"E4.39.18.8"),sQuery(id+"F0.wireOp",EDGE,"E4.6.18.9"),sQuery(id+"F0.wireOp",EDGE,"E4.9.18.9"),sQuery(id+"F0.wireOp",EDGE,"E4.12.18.9"),sQuery(id+"F0.wireOp",EDGE,"E4.15.18.9"),sQuery(id+"F0.wireOp",EDGE,"E4.18.18.9"),sQuery(id+"F0.wireOp",EDGE,"E4.21.18.9"),sQuery(id+"F0.wireOp",EDGE,"E4.24.18.9"),sQuery(id+"F0.wireOp",EDGE,"E4.27.18.9"),sQuery(id+"F0.wireOp",EDGE,"E4.30.18.9"),sQuery(id+"F0.wireOp",EDGE,"E4.33.18.9"),sQuery(id+"F0.wireOp",EDGE,"E4.36.18.9"),sQuery(id+"F0.wireOp",EDGE,"E4.39.18.9"),sQuery(id+"F0.wireOp",EDGE,"E4.6.19.0"),sQuery(id+"F0.wireOp",EDGE,"E4.9.19.0"),sQuery(id+"F0.wireOp",EDGE,"E4.12.19.0"),sQuery(id+"F0.wireOp",EDGE,"E4.15.19.0"),sQuery(id+"F0.wireOp",EDGE,"E4.18.19.0"),sQuery(id+"F0.wireOp",EDGE,"E4.21.19.0"),sQuery(id+"F0.wireOp",EDGE,"E4.24.19.0"),sQuery(id+"F0.wireOp",EDGE,"E4.27.19.0"),sQuery(id+"F0.wireOp",EDGE,"E4.30.19.0"),sQuery(id+"F0.wireOp",EDGE,"E4.33.19.0"),sQuery(id+"F0.wireOp",EDGE,"E4.36.19.0"),sQuery(id+"F0.wireOp",EDGE,"E4.39.19.0"),sQuery(id+"F0.wireOp",EDGE,"E4.6.19.1"),sQuery(id+"F0.wireOp",EDGE,"E4.9.19.1"),sQuery(id+"F0.wireOp",EDGE,"E4.12.19.1"),sQuery(id+"F0.wireOp",EDGE,"E4.15.19.1"),sQuery(id+"F0.wireOp",EDGE,"E4.18.19.1"),sQuery(id+"F0.wireOp",EDGE,"E4.21.19.1"),sQuery(id+"F0.wireOp",EDGE,"E4.24.19.1"),sQuery(id+"F0.wireOp",EDGE,"E4.27.19.1"),sQuery(id+"F0.wireOp",EDGE,"E4.30.19.1"),sQuery(id+"F0.wireOp",EDGE,"E4.33.19.1"),sQuery(id+"F0.wireOp",EDGE,"E4.36.19.1"),sQuery(id+"F0.wireOp",EDGE,"E4.39.19.1"),sQuery(id+"F0.wireOp",EDGE,"E4.6.19.2"),sQuery(id+"F0.wireOp",EDGE,"E4.9.19.2"),sQuery(id+"F0.wireOp",EDGE,"E4.12.19.2"),sQuery(id+"F0.wireOp",EDGE,"E4.15.19.2"),sQuery(id+"F0.wireOp",EDGE,"E4.18.19.2"),sQuery(id+"F0.wireOp",EDGE,"E4.21.19.2"),sQuery(id+"F0.wireOp",EDGE,"E4.24.19.2"),sQuery(id+"F0.wireOp",EDGE,"E4.27.19.2"),sQuery(id+"F0.wireOp",EDGE,"E4.30.19.2"),sQuery(id+"F0.wireOp",EDGE,"E4.33.19.2"),sQuery(id+"F0.wireOp",EDGE,"E4.36.19.2"),sQuery(id+"F0.wireOp",EDGE,"E4.39.19.2"),sQuery(id+"F0.wireOp",EDGE,"E4.6.19.3"),sQuery(id+"F0.wireOp",EDGE,"E4.9.19.3"),sQuery(id+"F0.wireOp",EDGE,"E4.12.19.3"),sQuery(id+"F0.wireOp",EDGE,"E4.15.19.3"),sQuery(id+"F0.wireOp",EDGE,"E4.18.19.3"),sQuery(id+"F0.wireOp",EDGE,"E4.21.19.3"),sQuery(id+"F0.wireOp",EDGE,"E4.24.19.3"),sQuery(id+"F0.wireOp",EDGE,"E4.27.19.3"),sQuery(id+"F0.wireOp",EDGE,"E4.30.19.3"),sQuery(id+"F0.wireOp",EDGE,"E4.33.19.3"),sQuery(id+"F0.wireOp",EDGE,"E4.36.19.3"),sQuery(id+"F0.wireOp",EDGE,"E4.39.19.3"),sQuery(id+"F0.wireOp",EDGE,"E4.6.19.4"),sQuery(id+"F0.wireOp",EDGE,"E4.9.19.4"),sQuery(id+"F0.wireOp",EDGE,"E4.12.19.4"),sQuery(id+"F0.wireOp",EDGE,"E4.15.19.4"),sQuery(id+"F0.wireOp",EDGE,"E4.18.19.4"),sQuery(id+"F0.wireOp",EDGE,"E4.21.19.4"),sQuery(id+"F0.wireOp",EDGE,"E4.24.19.4"),sQuery(id+"F0.wireOp",EDGE,"E4.27.19.4"),sQuery(id+"F0.wireOp",EDGE,"E4.30.19.4"),sQuery(id+"F0.wireOp",EDGE,"E4.33.19.4"),sQuery(id+"F0.wireOp",EDGE,"E4.36.19.4"),sQuery(id+"F0.wireOp",EDGE,"E4.39.19.4"),sQuery(id+"F0.wireOp",EDGE,"E4.6.19.5"),sQuery(id+"F0.wireOp",EDGE,"E4.9.19.5"),sQuery(id+"F0.wireOp",EDGE,"E4.12.19.5"),sQuery(id+"F0.wireOp",EDGE,"E4.15.19.5"),sQuery(id+"F0.wireOp",EDGE,"E4.18.19.5"),sQuery(id+"F0.wireOp",EDGE,"E4.21.19.5"),sQuery(id+"F0.wireOp",EDGE,"E4.24.19.5"),sQuery(id+"F0.wireOp",EDGE,"E4.27.19.5"),sQuery(id+"F0.wireOp",EDGE,"E4.30.19.5"),sQuery(id+"F0.wireOp",EDGE,"E4.33.19.5"),sQuery(id+"F0.wireOp",EDGE,"E4.36.19.5"),sQuery(id+"F0.wireOp",EDGE,"E4.39.19.5"),sQuery(id+"F0.wireOp",EDGE,"E4.6.19.6"),sQuery(id+"F0.wireOp",EDGE,"E4.9.19.6"),sQuery(id+"F0.wireOp",EDGE,"E4.12.19.6"),sQuery(id+"F0.wireOp",EDGE,"E4.15.19.6"),sQuery(id+"F0.wireOp",EDGE,"E4.18.19.6"),sQuery(id+"F0.wireOp",EDGE,"E4.21.19.6"),sQuery(id+"F0.wireOp",EDGE,"E4.24.19.6"),sQuery(id+"F0.wireOp",EDGE,"E4.27.19.6"),sQuery(id+"F0.wireOp",EDGE,"E4.30.19.6"),sQuery(id+"F0.wireOp",EDGE,"E4.33.19.6"),sQuery(id+"F0.wireOp",EDGE,"E4.36.19.6"),sQuery(id+"F0.wireOp",EDGE,"E4.39.19.6"),sQuery(id+"F0.wireOp",EDGE,"E4.6.19.7"),sQuery(id+"F0.wireOp",EDGE,"E4.9.19.7"),sQuery(id+"F0.wireOp",EDGE,"E4.12.19.7"),sQuery(id+"F0.wireOp",EDGE,"E4.15.19.7"),sQuery(id+"F0.wireOp",EDGE,"E4.18.19.7"),sQuery(id+"F0.wireOp",EDGE,"E4.21.19.7"),sQuery(id+"F0.wireOp",EDGE,"E4.24.19.7"),sQuery(id+"F0.wireOp",EDGE,"E4.27.19.7"),sQuery(id+"F0.wireOp",EDGE,"E4.30.19.7"),sQuery(id+"F0.wireOp",EDGE,"E4.33.19.7"),sQuery(id+"F0.wireOp",EDGE,"E4.36.19.7"),sQuery(id+"F0.wireOp",EDGE,"E4.39.19.7"),sQuery(id+"F0.wireOp",EDGE,"E4.6.19.8"),sQuery(id+"F0.wireOp",EDGE,"E4.9.19.8"),sQuery(id+"F0.wireOp",EDGE,"E4.12.19.8"),sQuery(id+"F0.wireOp",EDGE,"E4.15.19.8"),sQuery(id+"F0.wireOp",EDGE,"E4.18.19.8"),sQuery(id+"F0.wireOp",EDGE,"E4.21.19.8"),sQuery(id+"F0.wireOp",EDGE,"E4.24.19.8"),sQuery(id+"F0.wireOp",EDGE,"E4.27.19.8"),sQuery(id+"F0.wireOp",EDGE,"E4.30.19.8"),sQuery(id+"F0.wireOp",EDGE,"E4.33.19.8"),sQuery(id+"F0.wireOp",EDGE,"E4.36.19.8"),sQuery(id+"F0.wireOp",EDGE,"E4.39.19.8"),sQuery(id+"F0.wireOp",EDGE,"E4.6.19.9"),sQuery(id+"F0.wireOp",EDGE,"E4.9.19.9"),sQuery(id+"F0.wireOp",EDGE,"E4.12.19.9"),sQuery(id+"F0.wireOp",EDGE,"E4.15.19.9"),sQuery(id+"F0.wireOp",EDGE,"E4.18.19.9"),sQuery(id+"F0.wireOp",EDGE,"E4.21.19.9"),sQuery(id+"F0.wireOp",EDGE,"E4.24.19.9"),sQuery(id+"F0.wireOp",EDGE,"E4.27.19.9"),sQuery(id+"F0.wireOp",EDGE,"E4.30.19.9"),sQuery(id+"F0.wireOp",EDGE,"E4.33.19.9"),sQuery(id+"F0.wireOp",EDGE,"E4.36.19.9"),sQuery(id+"F0.wireOp",EDGE,"E4.39.19.9"),sQuery(id+"F0.wireOp",EDGE,"E5.bottom"),sQuery(id+"F0.wireOp",EDGE,"E5.top"),sQuery(id+"F0.wireOp",EDGE,"E5.left"),sQuery(id+"F0.wireOp",EDGE,"E5.right")])]});
            var Q1;
            Q1=makeQuery(id+"F4.opExtrude","SWEPT_BODY",BODY,{"disambiguationData":[OSD([sQuery(id+"F3.wireOp",EDGE,"E7")])]});
            var Q2;
            Q2=makeQuery(id+"F4.opExtrude","SWEPT_BODY",BODY,{"disambiguationData":[OSD([sQuery(id+"F3.wireOp",EDGE,"E7")])]});
            booleanBodies(context, id + "F5", {"operationType" : BooleanOperationType.INTERSECTION, "tools" : qUnion([Q0, Q1, Q2])});
        }
        {
            var Q0;
            Q0=makeQuery(id+"F3.imprint","IMPRINT",FACE,{"disambiguationData":[TD([[makeQuery(id+"F3.imprint","IMPRINT",EDGE,{"derivedFrom":sQuery(id+"F3.wireOp",EDGE,"E7")}),-1.0]])]});
            extrude(context, id + "F6", {"entities" : qUnion([Q0]), "operationType" : NewBodyOperationType.ADD, "depth" : 4 * mm, "offsetDistance" : 25 * mm});
        }
        {
            var Q0;
            {var subQ0=sQuery(id+"F3.wireOp",EDGE,"E7");Q0=makeQuery(id+"F6.boolean.opBoolean","MERGE",FACE,{"derivedFrom":[makeQuery(id+"F4.opExtrude","CAP_FACE",FACE,{"disambiguationData":[OSD([subQ0])],"isStart":false}),makeQuery(id+"F6.opExtrude","CAP_FACE",FACE,{"disambiguationData":[OSD([subQ0,sQuery(id+"F3.wireOp",EDGE,"E8")])],"isStart":false})]});}
            var sketch = newSketch(context, id + "F7", { "sketchPlane" : qUnion([Q0])});
            skCircle(sketch, "E9", {"center": v(64.81, 48.26) * mm, "radius": 269.3 * mm, "construction": true});
            skLineSegment(sketch, "E10.bottom", {"start": v(119.31, 102.76) * mm, "end": v(10.31, 102.76) * mm, "construction": true});
            skLineSegment(sketch, "E10.top", {"start": v(119.31, -6.24) * mm, "end": v(10.31, -6.24) * mm, "construction": true});
            skLineSegment(sketch, "E10.left", {"start": v(119.31, 102.76) * mm, "end": v(119.31, -6.24) * mm, "construction": true});
            skLineSegment(sketch, "E10.right", {"start": v(10.31, 102.76) * mm, "end": v(10.31, -6.24) * mm, "construction": true});
            skCircle(sketch, "E11", {"center": v(10.31, 102.76) * mm, "radius": 2.25 * mm});
            skCircle(sketch, "E12", {"center": v(119.31, 102.76) * mm, "radius": 2.25 * mm});
            skCircle(sketch, "E13", {"center": v(119.31, -6.24) * mm, "radius": 2.25 * mm});
            skCircle(sketch, "E14", {"center": v(10.31, -6.24) * mm, "radius": 2.25 * mm});
            skLineSegment(sketch, "E15.bottom", {"start": v(124.31, 107.76) * mm, "end": v(5.31, 107.76) * mm});
            skLineSegment(sketch, "E15.top", {"start": v(124.31, -11.24) * mm, "end": v(5.31, -11.24) * mm});
            skLineSegment(sketch, "E15.left", {"start": v(124.31, 107.76) * mm, "end": v(124.31, -11.24) * mm});
            skLineSegment(sketch, "E15.right", {"start": v(5.31, 107.76) * mm, "end": v(5.31, -11.24) * mm});
            skLineSegment(sketch, "E16", {"start": v(64.81, 48.26) * mm, "end": v(157.2, 48.26) * mm, "construction": true});
            skLineSegment(sketch, "E17", {"start": v(124.31, 59.76) * mm, "end": v(159.31, 59.76) * mm});
            skLineSegment(sketch, "E18", {"start": v(159.31, 59.76) * mm, "end": v(159.31, 68.76) * mm});
            skLineSegment(sketch, "E19", {"start": v(159.31, 68.76) * mm, "end": v(124.31, 68.76) * mm});
            skCircle(sketch, "E20", {"center": v(154.81, 64.26) * mm, "radius": 4.5 * mm, "construction": true});
            skLineSegment(sketch, "E21.MirrorCS", {"start": v(124.31, 36.76) * mm, "end": v(159.31, 36.76) * mm});
            skCircle(sketch, "E22.MirrorC", {"center": v(154.81, 32.26) * mm, "radius": 4.5 * mm, "construction": true});
            skLineSegment(sketch, "E23.MirrorCS", {"start": v(159.31, 27.76) * mm, "end": v(124.31, 27.76) * mm});
            skLineSegment(sketch, "E24.MirrorCS", {"start": v(159.31, 36.76) * mm, "end": v(159.31, 27.76) * mm});
            skSolve(sketch);
        }
        {
            var Q0;
            Q0=makeQuery(id+"F7.imprint","IMPRINT",FACE,{"disambiguationData":[TD([[makeQuery(id+"F7.imprint","IMPRINT",EDGE,{"derivedFrom":sQuery(id+"F7.wireOp",EDGE,"E11")}),-1.0]])]});
            var Q1;
            {var subQ0=sQuery(id+"F7.wireOp",EDGE,"E17");Q1=makeQuery(id+"F7.imprint","IMPRINT",FACE,{"disambiguationData":[TD([[makeQuery(id+"F7.imprint","IMPRINT",EDGE,{"derivedFrom":subQ0}),1.0]])]});}
            var Q2;
            {var subQ0=sQuery(id+"F7.wireOp",EDGE,"E21.MirrorCS");Q2=makeQuery(id+"F7.imprint","IMPRINT",FACE,{"disambiguationData":[TD([[makeQuery(id+"F7.imprint","IMPRINT",EDGE,{"derivedFrom":subQ0}),-1.0]])]});}
            extrude(context, id + "F8", {"entities" : qUnion([Q0, Q1, Q2]), "operationType" : NewBodyOperationType.ADD, "oppositeDirection" : true, "depth" : 4 * mm, "offsetDistance" : 25 * mm});
        }
        {
            var Q0;
            {var subQ0=sQuery(id+"F3.wireOp",EDGE,"E8");var subQ1=sQuery(id+"F3.wireOp",EDGE,"E7");Q0=makeQuery(id+"F8.boolean.opBoolean","MERGE",FACE,{"derivedFrom":[makeQuery(id+"F6.boolean.opBoolean","MERGE",FACE,{"derivedFrom":[makeQuery(id+"F4.opExtrude","CAP_FACE",FACE,{"disambiguationData":[OSD([subQ1])],"isStart":false}),makeQuery(id+"F6.opExtrude","CAP_FACE",FACE,{"disambiguationData":[OSD([subQ1,subQ0])],"isStart":false})]}),makeQuery(id+"F8.opExtrude","CAP_FACE",FACE,{"disambiguationData":[OSD([subQ0,sQuery(id+"F7.wireOp",EDGE,"E11"),sQuery(id+"F7.wireOp",EDGE,"E12"),sQuery(id+"F7.wireOp",EDGE,"E13"),sQuery(id+"F7.wireOp",EDGE,"E14"),sQuery(id+"F7.wireOp",EDGE,"E15.bottom"),sQuery(id+"F7.wireOp",EDGE,"E15.top"),sQuery(id+"F7.wireOp",EDGE,"E15.left"),sQuery(id+"F7.wireOp",EDGE,"E15.right"),sQuery(id+"F7.wireOp",EDGE,"E17"),sQuery(id+"F7.wireOp",EDGE,"E18"),sQuery(id+"F7.wireOp",EDGE,"E19"),sQuery(id+"F7.wireOp",EDGE,"E21.MirrorCS"),sQuery(id+"F7.wireOp",EDGE,"E23.MirrorCS"),sQuery(id+"F7.wireOp",EDGE,"E24.MirrorCS")])],"isStart":true})]});}
            var sketch = newSketch(context, id + "F9", { "sketchPlane" : qUnion([Q0])});
            skLineSegment(sketch, "E25.bottom", {"start": v(159.31, 68.76) * mm, "end": v(155.31, 68.76) * mm});
            skLineSegment(sketch, "E25.top", {"start": v(159.31, 59.76) * mm, "end": v(155.31, 59.76) * mm});
            skLineSegment(sketch, "E25.left", {"start": v(159.31, 68.76) * mm, "end": v(159.31, 59.76) * mm});
            skLineSegment(sketch, "E25.right", {"start": v(155.31, 68.76) * mm, "end": v(155.31, 59.76) * mm});
            skLineSegment(sketch, "E26.bottom", {"start": v(159.31, 36.76) * mm, "end": v(155.31, 36.76) * mm});
            skLineSegment(sketch, "E26.top", {"start": v(159.31, 27.76) * mm, "end": v(155.31, 27.76) * mm});
            skLineSegment(sketch, "E26.left", {"start": v(159.31, 36.76) * mm, "end": v(159.31, 27.76) * mm});
            skLineSegment(sketch, "E26.right", {"start": v(155.31, 36.76) * mm, "end": v(155.31, 27.76) * mm});
            skSolve(sketch);
        }
        {
            var Q0;
            Q0=makeQuery(id+"F9.imprint","IMPRINT",FACE,{"disambiguationData":[TD([[makeQuery(id+"F9.imprint","IMPRINT",EDGE,{"derivedFrom":sQuery(id+"F9.wireOp",EDGE,"E25.bottom")}),1.0]])]});
            var Q1;
            Q1=makeQuery(id+"F9.imprint","IMPRINT",FACE,{"disambiguationData":[TD([[makeQuery(id+"F9.imprint","IMPRINT",EDGE,{"derivedFrom":sQuery(id+"F9.wireOp",EDGE,"E26.bottom")}),-1.0]])]});
            extrude(context, id + "F10", {"entities" : qUnion([Q0, Q1]), "operationType" : NewBodyOperationType.ADD, "depth" : 30 * mm, "offsetDistance" : 25 * mm});
        }
        {
            var Q0;
            Q0=makeQuery(id+"F10.boolean.opBoolean","MERGE",FACE,{"derivedFrom":[makeQuery(id+"F8.opExtrude","SWEPT_FACE",FACE,{"disambiguationData":[OSD([sQuery(id+"F7.wireOp",EDGE,"E18")])]}),makeQuery(id+"F10.opExtrude","SWEPT_FACE",FACE,{"disambiguationData":[OSD([sQuery(id+"F9.wireOp",EDGE,"E25.left")])]})]});
            var sketch = newSketch(context, id + "F11", { "sketchPlane" : qUnion([Q0])});
            skCircle(sketch, "E27", {"center": v(-29.5, 32.26) * mm, "radius": 4.5 * mm, "construction": true});
            skCircle(sketch, "E28", {"center": v(-29.5, 64.26) * mm, "radius": 4.5 * mm, "construction": true});
            skCircle(sketch, "E29", {"center": v(-29.5, 64.26) * mm, "radius": 2.25 * mm});
            skCircle(sketch, "E30", {"center": v(-29.5, 32.26) * mm, "radius": 2.25 * mm});
            skSolve(sketch);
        }
        {
            var Q0;
            Q0=makeQuery(id+"F11.imprint","IMPRINT",FACE,{"disambiguationData":[TD([[makeQuery(id+"F11.imprint","IMPRINT",EDGE,{"derivedFrom":sQuery(id+"F11.wireOp",EDGE,"E30")}),1.0]])]});
            var Q1;
            Q1=makeQuery(id+"F11.imprint","IMPRINT",FACE,{"disambiguationData":[TD([[makeQuery(id+"F11.imprint","IMPRINT",EDGE,{"derivedFrom":sQuery(id+"F11.wireOp",EDGE,"E29")}),1.0]])]});
            extrude(context, id + "F12", {"entities" : qUnion([Q0, Q1]), "operationType" : NewBodyOperationType.REMOVE, "endBound" : BoundingType.THROUGH_ALL, "oppositeDirection" : true, "depth" : 25 * mm, "offsetDistance" : 25 * mm});
        }
        {
            var Q0;
            Q0=makeQuery(id+"F8.opExtrude","SWEPT_EDGE",EDGE,{"disambiguationData":[OSD([sQuery(id+"F7.wireOp",EDGE,"E15.left"),sQuery(id+"F7.wireOp",EDGE,"E21.MirrorCS")])]});
            var Q1;
            Q1=makeQuery(id+"F8.opExtrude","SWEPT_EDGE",EDGE,{"disambiguationData":[OSD([sQuery(id+"F7.wireOp",EDGE,"E15.left"),sQuery(id+"F7.wireOp",EDGE,"E19")])]});
            var Q2;
            Q2=makeQuery(id+"F8.opExtrude","SWEPT_EDGE",EDGE,{"disambiguationData":[OSD([sQuery(id+"F7.wireOp",EDGE,"E15.left"),sQuery(id+"F7.wireOp",EDGE,"E17")])]});
            var Q3;
            Q3=makeQuery(id+"F8.opExtrude","SWEPT_EDGE",EDGE,{"disambiguationData":[OSD([sQuery(id+"F7.wireOp",EDGE,"E15.left"),sQuery(id+"F7.wireOp",EDGE,"E23.MirrorCS")])]});
            var Q4;
            Q4=makeQuery(id+"F10.opExtrude","CAP_EDGE",EDGE,{"disambiguationData":[OSD([sQuery(id+"F9.wireOp",EDGE,"E26.right")])],"isStart":true});
            var Q5;
            Q5=makeQuery(id+"F10.opExtrude","CAP_EDGE",EDGE,{"disambiguationData":[OSD([sQuery(id+"F9.wireOp",EDGE,"E25.right")])],"isStart":true});
            fillet(context, id + "F13", {"entities" : qUnion([Q0, Q1, Q2, Q3, Q4, Q5]), "radius" : 12 * mm, "tangentPropagation" : true, "allowEdgeOverflow" : false});
        }
    });
